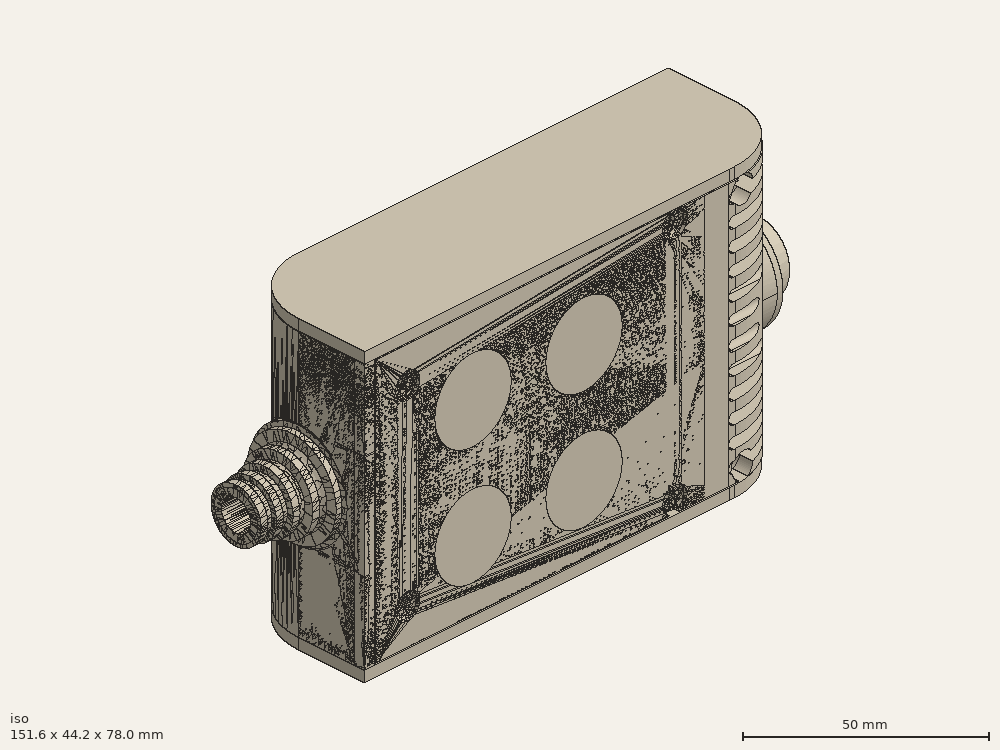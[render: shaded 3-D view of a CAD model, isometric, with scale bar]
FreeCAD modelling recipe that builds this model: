
FCSTD DOCUMENT  (FreeCAD 0.19R0.19.2)
Label: enclosure_176FCStd
License: All rights reserved
LicenseURL: http://en.wikipedia.org/wiki/All_rights_reserved
objects: Part::Revolution×152, Part::MultiFuse×146, Part::Feature×146, Sketcher::SketchObject×84, Part::Cut×70, Part::Cylinder×70, Part::Extrusion×67, Part::Fillet×58, Part::Box×36, App::MeasureDistance×4, PartDesign::Body×2, Image::ImagePlane×1
note: 831 computed .brp shape members not serialized (recipe doc carries the construction recipe); baked Part::Feature solids carry a one-line shape summary decoded from their .brp

FEATURE [Sketcher::SketchObject] Sketch  label="topSketch"
  FullyConstrained = true
  sketch-geometry (20):
    g0: LineSegment StartX=5.21097e-06 StartY=3 StartZ=0 EndX=5.21097e-06 EndY=19 EndZ=0
    g1: ArcOfCircle CenterX=19 CenterY=19 CenterZ=0 NormalX=0 NormalY=0 NormalZ=1 AngleXU=0 Radius=19 StartAngle=1.5708 EndAngle=3.14159
    g2: ArcOfCircle CenterX=19 CenterY=19 CenterZ=0 NormalX=0 NormalY=0 NormalZ=1 AngleXU=0 Radius=16 StartAngle=1.5708 EndAngle=3.14159
    g3: LineSegment StartX=114 StartY=35 StartZ=0 EndX=19 EndY=35 EndZ=0
    g4: LineSegment StartX=5.21097e-06 StartY=3 StartZ=0 EndX=5.21097e-06 EndY=0 EndZ=0
    g5: LineSegment StartX=3 StartY=0 StartZ=0 EndX=5.21097e-06 EndY=0 EndZ=0
    g6: LineSegment StartX=3 StartY=19 StartZ=0 EndX=3 EndY=0 EndZ=0
    g7: LineSegment StartX=19 StartY=38 StartZ=0 EndX=124 EndY=38 EndZ=0
    g8: Circle CenterX=119 CenterY=35 CenterZ=0 NormalX=0 NormalY=0 NormalZ=1 AngleXU=0 Radius=1
    g9: Circle CenterX=121 CenterY=35 CenterZ=0 NormalX=0 NormalY=0 NormalZ=1 AngleXU=0 Radius=1
    g10: Circle CenterX=121 CenterY=33 CenterZ=0 NormalX=0 NormalY=0 NormalZ=1 AngleXU=0 Radius=1
    g11: BSplineCurve PolesCount=3 KnotsCount=2 Degree=2 IsPeriodic=0
    g12: GeomPoint X=119 Y=35 Z=0
    g13: GeomPoint X=121 Y=33 Z=0
    g14: LineSegment StartX=119 StartY=35 StartZ=0 EndX=114 EndY=35 EndZ=0
    g15: ArcOfCircle CenterX=105 CenterY=19 CenterZ=0 NormalX=0 NormalY=0 NormalZ=1 AngleXU=0 Radius=19 StartAngle=5.7297 EndAngle=6.28319
    g16: ArcOfCircle CenterX=105 CenterY=19 CenterZ=0 NormalX=0 NormalY=0 NormalZ=1 AngleXU=0 Radius=16 StartAngle=5.60905 EndAngle=6.28319
    g17: LineSegment StartX=121 StartY=33 StartZ=0 EndX=121 EndY=19 EndZ=0
    g18: LineSegment StartX=124 StartY=38 StartZ=0 EndX=124 EndY=19 EndZ=0
    g19: LineSegment StartX=117.5 StartY=9.01251 StartZ=0 EndX=121.163 EndY=9.0125 EndZ=0
  constraints (46):
    c: Vertical(g0)
    c: Block(g0)
    c: Coincident(g1,g0)
    c: Block(g1)
    c: Coincident(g2,g1)
    c: Block(g2)
    c: Coincident(g3,g2)
    c: Horizontal(g3)
    c: Tangent(g3,g2)
    c: Coincident(g4,g0)
    c: Distance(g4) = 3
    c: Vertical(g4)
    c: Coincident(g5,g4)
    c: Horizontal(g5)
    c: Coincident(g6,g2)
    c: Coincident(g6,g5)
    c: Vertical(g6)
    c: Horizontal(g7)
    c: Distance(g7) = 105
    c: Coincident(g7,g1)
    c: Block(g3)
    c: Weight(g8) = 1
    c: Equal(g8,g9)
    c: Equal(g8,g10)
    c: InternalAlignment(g8,g11)
    c: InternalAlignment(g9,g11)
    c: InternalAlignment(g10,g11)
    c: InternalAlignment(g12,g11)
    c: InternalAlignment(g13,g11)
    c: Block(g11)
    c: Coincident(g14,g11)
    c: Coincident(g14,g3)
    c: Horizontal(g14)
    c: Block(g15)
    c: Coincident(g16,g15)
    c: Block(g16)
    c: Coincident(g17,g11)
    c: Coincident(g17,g16)
    c: Vertical(g17)
    c: Distance(g17) = 14
    c: Coincident(g18,g7)
    c: Coincident(g18,g15)
    c: Vertical(g18)
    c: Distance(g18) = 19
    c: Coincident(g19,g16)
    c: Coincident(g19,g15)
FEATURE [Sketcher::SketchObject] Sketch001  label="bottomSketch"
  FullyConstrained = true
  sketch-geometry (32):
    g0: LineSegment StartX=3.3 StartY=-6.03275e-07 StartZ=0 EndX=98 EndY=-6.03275e-07 EndZ=0
    g1: ArcOfCircle CenterX=98 CenterY=19 CenterZ=0 NormalX=0 NormalY=0 NormalZ=1 AngleXU=0 Radius=19 StartAngle=4.71239 EndAngle=5.71103
    g2: LineSegment StartX=6.3 StartY=8 StartZ=0 EndX=3.3 EndY=8 EndZ=0
    g3: LineSegment StartX=3.3 StartY=8 StartZ=0 EndX=3.3 EndY=-6.03275e-07 EndZ=0
    g4: ArcOfCircle CenterX=8.3 CenterY=5 CenterZ=0 NormalX=0 NormalY=0 NormalZ=1 AngleXU=0 Radius=2 StartAngle=3.14159 EndAngle=4.71239
    g5: LineSegment StartX=6.3 StartY=8 StartZ=0 EndX=6.3 EndY=5 EndZ=0
    g6: ArcOfCircle CenterX=98 CenterY=19 CenterZ=0 NormalX=0 NormalY=0 NormalZ=1 AngleXU=0 Radius=12.7 StartAngle=4.71239 EndAngle=6.28319
    g7: LineSegment StartX=94.7 StartY=3 StartZ=0 EndX=8.3 EndY=3 EndZ=0
    g8-g12: Circle x5 (B-spline internal-alignment scaffolding for g13; pole/knot coordinates omitted)
    g13: BSplineCurve PolesCount=5 KnotsCount=3 Degree=3 IsPeriodic=0
    g14: GeomPoint X=98 Y=6.3 Z=0
    g15: GeomPoint X=96.3938 Y=4.71946 Z=0
    g16: GeomPoint X=94.7 Y=3 Z=0
    g17-g23: Circle x7 (B-spline internal-alignment scaffolding for g24; pole/knot coordinates omitted)
    g24: BSplineCurve PolesCount=7 KnotsCount=5 Degree=3 IsPeriodic=0
    g25-g29: GeomPoint x5 (B-spline internal-alignment scaffolding for g24; pole/knot coordinates omitted)
    g30: ArcOfCircle CenterX=98 CenterY=19 CenterZ=0 NormalX=0 NormalY=0 NormalZ=1 AngleXU=0 Radius=15.7 StartAngle=5.81226 EndAngle=6.28319
    g31: LineSegment StartX=110.7 StartY=19 StartZ=0 EndX=113.7 EndY=19 EndZ=0
  constraints (41):
    c: Horizontal(g0)
    c: Coincident(g1,g0)
    c: Block(g1)
    c: Horizontal(g2)
    c: Distance(g2) = 3
    c: Coincident(g3,g2)
    c: Vertical(g3)
    c: Coincident(g3,g0)
    c: Block(g4)
    c: Block(g2)
    c: Coincident(g5,g2)
    c: Coincident(g5,g4)
    c: Vertical(g5)
    c: Coincident(g6,g1)
    c: Block(g6)
    c: Coincident(g7,g4)
    c: Horizontal(g7)
    c: Block(g0)
    c: Block(g7)
    c: Block(g3)
    c: Coincident(g13,g6)
    c: Weight(g8) = 1
    c: Equal(g8, g9-g12) x4
    c: Coincident(g13,g7)
    c: InternalAlignment(g8-g12 -> g13) x5
    c: InternalAlignment(g14,g13)
    c: InternalAlignment(g15,g13)
    c: InternalAlignment(g16,g13)
    c: Block(g13)
    c: Weight(g17) = 1
    c: Equal(g17, g18-g23) x6
    c: Coincident(g24,g1)
    c: InternalAlignment(g17-g23 -> g24) x7
    c: InternalAlignment(g25-g29 -> g24) x5
    c: Block(g24)
    c: Coincident(g30,g24)
    c: Coincident(g31,g6)
    c: Coincident(g31,g30)
    c: Horizontal(g31)
    c: Block(g31)
    c: Block(g30)
FEATURE [Part::Extrusion] Extrude  label="top"
  Base = -> Sketch
  Dir = (0,0,1)
  DirMode = 2
  FaceMakerClass = Part::FaceMakerBullseye
  LengthFwd = 72
  LengthRev = 0
  Solid = true
  Symmetric = false
FEATURE [Part::Extrusion] Extrude001  label="bottom"
  Base = -> Sketch001
  Dir = (0,0,1)
  DirMode = 2
  FaceMakerClass = Part::FaceMakerBullseye
  LengthFwd = 71.4
  LengthRev = 0
  Placement = pos=(0,0,0.3) rot=(0,0,1;0rad)
  Solid = true
  Symmetric = false
FEATURE [Sketcher::SketchObject] Sketch002  label="topSketch001"
  FullyConstrained = true
  sketch-geometry (8):
    g0: ArcOfCircle CenterX=19 CenterY=19.0975 CenterZ=0 NormalX=0 NormalY=0 NormalZ=1 AngleXU=0 Radius=18.9025 StartAngle=1.5708 EndAngle=3.14674
    g1: LineSegment StartX=0.0977805 StartY=19.0003 StartZ=0 EndX=0.0977805 EndY=0.000251602 EndZ=0
    g2: LineSegment StartX=19 StartY=38 StartZ=0 EndX=124 EndY=38 EndZ=0
    g3: LineSegment StartX=0.0977805 StartY=0.000251602 StartZ=0 EndX=105.098 EndY=0.000251602 EndZ=0
    g4: LineSegment StartX=124 StartY=38 StartZ=0 EndX=125.616 EndY=38 EndZ=0
    g5: LineSegment StartX=105.098 StartY=0.000251602 StartZ=0 EndX=106.713 EndY=0.000251602 EndZ=0
    g6: ArcOfCircle CenterX=106.616 CenterY=19 CenterZ=0 NormalX=0 NormalY=0 NormalZ=1 AngleXU=0 Radius=19 StartAngle=4.71754 EndAngle=6.28319
    g7: LineSegment StartX=125.616 StartY=38 StartZ=0 EndX=125.616 EndY=19 EndZ=0
  constraints (21):
    c: Block(g0)
    c: Coincident(g1,g0)
    c: Vertical(g1)
    c: Horizontal(g2)
    c: Distance(g2) = 105
    c: Coincident(g2,g0)
    c: Distance(g1) = 19
    c: Coincident(g3,g1)
    c: Horizontal(g3)
    c: Distance(g3) = 105
    c: Coincident(g4,g2)
    c: Horizontal(g4)
    c: Distance(g4) = 1.61553
    c: Horizontal(g5)
    c: Equal(g4,g5) = 1.61553
    c: Coincident(g5,g3)
    c: Block(g6)
    c: Coincident(g6,g5)
    c: Coincident(g7,g4)
    c: Coincident(g7,g6)
    c: Vertical(g7)
FEATURE [Part::Extrusion] Extrude002  label="sideA"
  Base = -> Sketch002
  Dir = (0,0,1)
  DirMode = 2
  FaceMakerClass = Part::FaceMakerBullseye
  LengthFwd = 3
  LengthRev = 0
  Placement = pos=(0,0,-3) rot=(0,0,1;0rad)
  Solid = true
  Symmetric = false
FEATURE [Sketcher::SketchObject] Sketch003  label="topSketch002"
  FullyConstrained = true
  sketch-geometry (6):
    g0: LineSegment StartX=19 StartY=38 StartZ=0 EndX=117 EndY=38 EndZ=0
    g1: ArcOfCircle CenterX=19 CenterY=19 CenterZ=0 NormalX=0 NormalY=0 NormalZ=1 AngleXU=0 Radius=19 StartAngle=1.5708 EndAngle=3.14159
    g2: LineSegment StartX=117 StartY=38 StartZ=0 EndX=117 EndY=19 EndZ=0
    g3: LineSegment StartX=98 StartY=1.0161e-12 StartZ=0 EndX=5.22862e-06 EndY=1.0161e-12 EndZ=0
    g4: LineSegment StartX=5.22862e-06 StartY=19 StartZ=0 EndX=5.22862e-06 EndY=1.0161e-12 EndZ=0
    g5: ArcOfCircle CenterX=98 CenterY=19 CenterZ=0 NormalX=0 NormalY=0 NormalZ=1 AngleXU=0 Radius=19 StartAngle=4.71239 EndAngle=6.28319
  constraints (16):
    c: Horizontal(g0)
    c: Distance(g0) = 98
    c: Coincident(g1,g0)
    c: Block(g1)
    c: Coincident(g2,g0)
    c: Vertical(g2)
    c: Distance(g2) = 19
    c: Horizontal(g3)
    c: Coincident(g4,g1)
    c: Vertical(g4)
    c: Coincident(g3,g4)
    c: Block(g3)
    c: Coincident(g5,g2)
    c: Coincident(g5,g3)
    c: Block(g0)
    c: Block(g5)
FEATURE [Sketcher::SketchObject] Sketch004
  FullyConstrained = true
  MapMode = 3
  Placement = pos=(0,0,0) rot=(1,0,0;1.5708rad)
  Support = -> [Extrude]
  sketch-geometry (8):
    g0: Circle CenterX=80.351 CenterY=-67.6202 CenterZ=0 NormalX=0 NormalY=0 NormalZ=1 AngleXU=0 Radius=2
    g1: Circle CenterX=80.351 CenterY=-67.6202 CenterZ=0 NormalX=0 NormalY=0 NormalZ=1 AngleXU=0 Radius=3
    g2: Circle CenterX=80.351 CenterY=-4.92017 CenterZ=0 NormalX=0 NormalY=0 NormalZ=1 AngleXU=0 Radius=2
    g3: Circle CenterX=80.351 CenterY=-4.92017 CenterZ=0 NormalX=0 NormalY=0 NormalZ=1 AngleXU=0 Radius=3
    g4: Circle CenterX=23.851 CenterY=-4.92017 CenterZ=0 NormalX=0 NormalY=0 NormalZ=1 AngleXU=0 Radius=2
    g5: Circle CenterX=23.851 CenterY=-4.92017 CenterZ=0 NormalX=0 NormalY=0 NormalZ=1 AngleXU=0 Radius=3
    g6: Circle CenterX=23.851 CenterY=-67.6202 CenterZ=0 NormalX=0 NormalY=0 NormalZ=1 AngleXU=0 Radius=2
    g7: Circle CenterX=23.851 CenterY=-67.6202 CenterZ=0 NormalX=0 NormalY=0 NormalZ=1 AngleXU=0 Radius=3
  constraints (8):
    c: Block(g3)
    c: Block(g2)
    c: Block(g1)
    c: Block(g0)
    c: Block(g6)
    c: Block(g7)
    c: Block(g4)
    c: Block(g5)
FEATURE [Part::Extrusion] Extrude004
  Base = -> Sketch004
  Dir = (0,-1,2e-16)
  DirMode = 2
  FaceMakerClass = Part::FaceMakerBullseye
  LengthFwd = 6
  LengthRev = 0
  Placement = pos=(0,9,0) rot=(0,0,1;0rad)
  Solid = true
  Symmetric = false
FEATURE [Sketcher::SketchObject] Sketch005
  FullyConstrained = true
  MapMode = 3
  Placement = pos=(0,0,0) rot=(1,0,0;1.5708rad)
  Support = -> [Extrude]
  sketch-geometry (8):
    g0: Circle CenterX=80.351 CenterY=-67.6202 CenterZ=0 NormalX=0 NormalY=0 NormalZ=1 AngleXU=0 Radius=3
    g1: Circle CenterX=80.351 CenterY=-4.92017 CenterZ=0 NormalX=0 NormalY=0 NormalZ=1 AngleXU=0 Radius=3
    g2: Circle CenterX=23.851 CenterY=-4.92017 CenterZ=0 NormalX=0 NormalY=0 NormalZ=1 AngleXU=0 Radius=3
    g3: Circle CenterX=23.851 CenterY=-67.6202 CenterZ=0 NormalX=0 NormalY=0 NormalZ=1 AngleXU=0 Radius=3
    g4: Circle CenterX=23.851 CenterY=-67.6202 CenterZ=0 NormalX=0 NormalY=0 NormalZ=1 AngleXU=0 Radius=5
    g5: Circle CenterX=80.351 CenterY=-67.6202 CenterZ=0 NormalX=0 NormalY=0 NormalZ=1 AngleXU=0 Radius=5
    g6: Circle CenterX=23.851 CenterY=-4.92017 CenterZ=0 NormalX=0 NormalY=0 NormalZ=1 AngleXU=0 Radius=5
    g7: Circle CenterX=80.351 CenterY=-4.92017 CenterZ=0 NormalX=0 NormalY=0 NormalZ=1 AngleXU=0 Radius=5
  constraints (8):
    c: Block(g1)
    c: Block(g0)
    c: Block(g3)
    c: Block(g2)
    c: Block(g5)
    c: Block(g4)
    c: Block(g6)
    c: Block(g7)
FEATURE [Part::Extrusion] Extrude005
  Base = -> Sketch005
  Dir = (0,-1,2e-16)
  DirMode = 2
  FaceMakerClass = Part::FaceMakerBullseye
  LengthFwd = 2
  LengthRev = 0
  Solid = true
  Symmetric = false
FEATURE [Sketcher::SketchObject] Sketch006
  FullyConstrained = true
  MapMode = 3
  Placement = pos=(0,0,0) rot=(1,0,0;1.5708rad)
  sketch-geometry (8):
    g0: Circle CenterX=80.351 CenterY=-67.6202 CenterZ=0 NormalX=0 NormalY=0 NormalZ=1 AngleXU=0 Radius=3
    g1: Circle CenterX=80.351 CenterY=-4.92017 CenterZ=0 NormalX=0 NormalY=0 NormalZ=1 AngleXU=0 Radius=3
    g2: Circle CenterX=23.851 CenterY=-4.92017 CenterZ=0 NormalX=0 NormalY=0 NormalZ=1 AngleXU=0 Radius=3
    g3: Circle CenterX=23.851 CenterY=-67.6202 CenterZ=0 NormalX=0 NormalY=0 NormalZ=1 AngleXU=0 Radius=3
    g4: Circle CenterX=23.851 CenterY=-67.6202 CenterZ=0 NormalX=0 NormalY=0 NormalZ=1 AngleXU=0 Radius=5
    g5: Circle CenterX=80.351 CenterY=-67.6202 CenterZ=0 NormalX=0 NormalY=0 NormalZ=1 AngleXU=0 Radius=5
    g6: Circle CenterX=23.851 CenterY=-4.92017 CenterZ=0 NormalX=0 NormalY=0 NormalZ=1 AngleXU=0 Radius=5
    g7: Circle CenterX=80.351 CenterY=-4.92017 CenterZ=0 NormalX=0 NormalY=0 NormalZ=1 AngleXU=0 Radius=5
  constraints (8):
    c: Block(g1)
    c: Block(g0)
    c: Block(g3)
    c: Block(g2)
    c: Block(g5)
    c: Block(g4)
    c: Block(g6)
    c: Block(g7)
FEATURE [Part::Extrusion] Extrude007
  Base = -> Sketch006
  Dir = (0,-1,2e-16)
  DirMode = 2
  FaceMakerClass = Part::FaceMakerBullseye
  LengthFwd = 2
  LengthRev = 0
  Solid = true
  Symmetric = false
FEATURE [Part::Fillet] Fillet
  Base = -> Extrude007
  Edges = 4 edges r=1.99: [Edge6,Edge12,Edge18,Edge24]
FEATURE [Part::Cut] Cut
  Base = -> Extrude005
  Placement = pos=(0,5,0) rot=(0,0,1;0rad)
  Tool = -> Fillet
FEATURE [Part::MultiFuse] Fusion  label="pCBScrews"
  Placement = pos=(-2.5,0,72.3) rot=(0,0,1;0rad)
  Shapes = -> [Extrude004,Cut]
FEATURE [App::MeasureDistance] Distance  label="Distance: 0.69 mm"
  Distance = 0.685967
  P1 = (24.0138,2.9647,0.3)
  P2 = (23.8901,3,-0.373787)
FEATURE [App::MeasureDistance] Distance001  label="Distance: 0.53 mm"
  Distance = 0.533607
  P1 = (80.2939,3,72.2334)
  P2 = (80.281,2.99661,71.7)
FEATURE [Part::Fillet] Fillet001
  Base = -> Extrude001
  Edges = 1 edges r=2.4: [Edge17]
FEATURE [Part::Fillet] Fillet002  label="bottom001"
  Base = -> Fillet001
  Edges = 1 edges r=2.4: [Edge36]
FEATURE [Part::Fillet] Fillet003  label="top001"
  Base = -> Extrude
  Edges = 1 edges r=2: [Edge1]
FEATURE [Sketcher::SketchObject] Sketch007
  FullyConstrained = true
  sketch-geometry (16):
    g0: LineSegment StartX=4 StartY=0 StartZ=0 EndX=4 EndY=2.4 EndZ=0
    g1: LineSegment StartX=4 StartY=2.4 StartZ=0 EndX=7 EndY=2.4 EndZ=0
    g2: LineSegment StartX=4 StartY=0 StartZ=0 EndX=5.7 EndY=0 EndZ=0
    g3: LineSegment StartX=5.7 StartY=0 StartZ=0 EndX=5.7 EndY=-5.6 EndZ=0
    g4-g8: Circle x5 (B-spline internal-alignment scaffolding for g9; pole/knot coordinates omitted)
    g9: BSplineCurve PolesCount=5 KnotsCount=3 Degree=3 IsPeriodic=0
    g10: GeomPoint X=7 Y=2.4 Z=0
    g11: GeomPoint X=10.4582 Y=-1.55472 Z=0
    g12: GeomPoint X=14 Y=-5.6 Z=0
    g13: LineSegment StartX=14 StartY=-5.6 StartZ=0 EndX=14 EndY=-14.1 EndZ=0
    g14: LineSegment StartX=14 StartY=-14.1 StartZ=0 EndX=6.5 EndY=-14.1 EndZ=0
    g15: LineSegment StartX=5.7 StartY=-5.6 StartZ=0 EndX=6.5 EndY=-14.1 EndZ=0
  constraints (28):
    c: Distance(g0) = 2.4
    c: Vertical(g0)
    c: Block(g0)
    c: Coincident(g1,g0)
    c: Horizontal(g1)
    c: Distance(g1) = 3
    c: Coincident(g2,g0)
    c: Horizontal(g2)
    c: Distance(g2) = 1.7
    c: Coincident(g3,g2)
    c: Vertical(g3)
    c: Distance(g3) = 5.6
    c: Coincident(g9,g1)
    c: Weight(g4) = 1
    c: Equal(g4, g5-g8) x4
    c: InternalAlignment(g4-g8 -> g9) x5
    c: InternalAlignment(g10,g9)
    c: InternalAlignment(g11,g9)
    c: InternalAlignment(g12,g9)
    c: Block(g9)
    c: Coincident(g13,g9)
    c: Vertical(g13)
    c: Distance(g13) = 8.5
    c: Coincident(g14,g13)
    c: Horizontal(g14)
    c: Distance(g14) = 7.5
    c: Coincident(g15,g3)
    c: Coincident(g15,g14)
FEATURE [Part::Feature] Face
  shape: bbox 10 x 16.5 x 2e-07 mm, 1 faces, 0 solids (baked)
FEATURE [Part::Revolution] Revolve  label="plugHousing"
  Angle = 360
  Axis = (0,1,0)
  Base = (0,0,0)
  FaceMakerClass = Part::FaceMakerBullseye
  Placement = pos=(0,0,36.15) rot=(0,0,1;0rad)
  Solid = false
  Source = -> Face
  Symmetric = false
FEATURE [Part::Feature] Face001
  shape: bbox 10 x 16.5 x 2e-07 mm, 1 faces, 0 solids (baked)
FEATURE [Part::Revolution] Revolve001  label="plugHousing001"
  Angle = 360
  Axis = (0,1,0)
  Base = (0,0,0)
  FaceMakerClass = Part::FaceMakerBullseye
  Placement = pos=(0,0,36.15) rot=(0,0,1;0rad)
  Solid = false
  Source = -> Face001
  Symmetric = false
FEATURE [Part::MultiFuse] Fusion001  label="plugHousing002"
  Placement = pos=(0,0,0) rot=(0,0,1;1.5708rad)
  Shapes = -> [Revolve001,Revolve]
FEATURE [Part::Feature] Face002
  shape: bbox 10 x 16.5 x 2e-07 mm, 1 faces, 0 solids (baked)
FEATURE [Part::Revolution] Revolve003  label="plugHousing005"
  Angle = 360
  Axis = (0,1,0)
  Base = (0,0,0)
  FaceMakerClass = Part::FaceMakerBullseye
  Placement = pos=(0,0,36.15) rot=(0,0,1;0rad)
  Solid = false
  Source = -> Face002
  Symmetric = false
FEATURE [Part::Feature] Face003
  shape: bbox 10 x 16.5 x 2e-07 mm, 1 faces, 0 solids (baked)
FEATURE [Part::Revolution] Revolve002  label="plugHousing003"
  Angle = 360
  Axis = (0,1,0)
  Base = (0,0,0)
  FaceMakerClass = Part::FaceMakerBullseye
  Placement = pos=(0,0,36.15) rot=(0,0,1;0rad)
  Solid = false
  Source = -> Face003
  Symmetric = false
FEATURE [Part::MultiFuse] Fusion002  label="plugHousing004"
  Placement = pos=(0,0,0) rot=(0,0,1;1.5708rad)
  Shapes = -> [Revolve002,Revolve003]
FEATURE [Part::MultiFuse] Fusion003  label="plugHousing006"
  Placement = pos=(0,19,0) rot=(0,0,1;3.14159rad)
  Shapes = -> [Fusion002,Fusion001]
FEATURE [Part::Feature] Face004
  shape: bbox 10 x 16.5 x 2e-07 mm, 1 faces, 0 solids (baked)
FEATURE [Part::Revolution] Revolve006  label="plugHousing010"
  Angle = 360
  Axis = (0,1,0)
  Base = (0,0,0)
  FaceMakerClass = Part::FaceMakerBullseye
  Placement = pos=(0,0,36.15) rot=(0,0,1;0rad)
  Solid = false
  Source = -> Face004
  Symmetric = false
FEATURE [Part::Feature] Face005
  shape: bbox 10 x 16.5 x 2e-07 mm, 1 faces, 0 solids (baked)
FEATURE [Part::Revolution] Revolve007  label="plugHousing011"
  Angle = 360
  Axis = (0,1,0)
  Base = (0,0,0)
  FaceMakerClass = Part::FaceMakerBullseye
  Placement = pos=(0,0,36.15) rot=(0,0,1;0rad)
  Solid = false
  Source = -> Face005
  Symmetric = false
FEATURE [Part::Feature] Face006
  shape: bbox 10 x 16.5 x 2e-07 mm, 1 faces, 0 solids (baked)
FEATURE [Part::Revolution] Revolve004  label="plugHousing007"
  Angle = 360
  Axis = (0,1,0)
  Base = (0,0,0)
  FaceMakerClass = Part::FaceMakerBullseye
  Placement = pos=(0,0,36.15) rot=(0,0,1;0rad)
  Solid = false
  Source = -> Face006
  Symmetric = false
FEATURE [Part::MultiFuse] Fusion004  label="plugHousing009"
  Placement = pos=(0,0,0) rot=(0,0,1;1.5708rad)
  Shapes = -> [Revolve004,Revolve007]
FEATURE [Part::Feature] Face007
  shape: bbox 10 x 16.5 x 2e-07 mm, 1 faces, 0 solids (baked)
FEATURE [Part::Revolution] Revolve005  label="plugHousing008"
  Angle = 360
  Axis = (0,1,0)
  Base = (0,0,0)
  FaceMakerClass = Part::FaceMakerBullseye
  Placement = pos=(0,0,36.15) rot=(0,0,1;0rad)
  Solid = false
  Source = -> Face007
  Symmetric = false
FEATURE [Part::MultiFuse] Fusion005  label="plugHousing012"
  Placement = pos=(0,0,0) rot=(0,0,1;1.5708rad)
  Shapes = -> [Revolve006,Revolve005]
FEATURE [Part::MultiFuse] Fusion006  label="plugHousing013"
  Placement = pos=(0,19,0) rot=(0,0,1;3.14159rad)
  Shapes = -> [Fusion005,Fusion004]
FEATURE [Part::MultiFuse] Fusion007  label="plugHousing014"
  Placement = pos=(122.621,0,-0.15) rot=(0,0,1;0rad)
  Shapes = -> [Fusion003,Fusion006]
FEATURE [Part::Cylinder] Cylinder002
  Angle = 360
  AttacherType = Attacher::AttachEngine3D
  Height = 20
  Placement = pos=(0,0,36.15) rot=(0,0,1;0rad)
  Radius = 4
FEATURE [Part::Cylinder] Cylinder003
  Angle = 360
  AttacherType = Attacher::AttachEngine3D
  Height = 10
  Placement = pos=(0,0,36.15) rot=(0,0,1;0rad)
  Radius = 4
FEATURE [Part::MultiFuse] Fusion009  label="removeToCreateHoleForPlugHousing"
  Placement = pos=(70,19,36.15) rot=(0,1,0;1.5708rad)
  Shapes = -> [Cylinder002,Cylinder003]
FEATURE [Part::Cylinder] Cylinder004
  Angle = 360
  AttacherType = Attacher::AttachEngine3D
  Height = 20
  Placement = pos=(0,0,36.15) rot=(0,0,1;0rad)
  Radius = 4
FEATURE [Part::Cylinder] Cylinder005
  Angle = 360
  AttacherType = Attacher::AttachEngine3D
  Height = 10
  Placement = pos=(0,0,36.15) rot=(0,0,1;0rad)
  Radius = 4
FEATURE [Part::MultiFuse] Fusion010  label="removeToCreateHoleForPlugHousing001"
  Placement = pos=(70,19,36.15) rot=(0,1,0;1.5708rad)
  Shapes = -> [Cylinder004,Cylinder005]
FEATURE [Part::Cut] Cut001
  Base = -> Fillet003
  Tool = -> Fusion010
FEATURE [Part::Cut] Cut002  label="Bottom"
  Base = -> Fillet002
  Tool = -> Fusion009
FEATURE [Part::Feature] Face008
  shape: bbox 10 x 16.5 x 2e-07 mm, 1 faces, 0 solids (baked)
FEATURE [Part::Revolution] Revolve011  label="plugHousing021"
  Angle = 360
  Axis = (0,1,0)
  Base = (0,0,0)
  FaceMakerClass = Part::FaceMakerBullseye
  Placement = pos=(0,0,36.15) rot=(0,0,1;0rad)
  Solid = false
  Source = -> Face008
  Symmetric = false
FEATURE [Part::Feature] Face009
  shape: bbox 10 x 16.5 x 2e-07 mm, 1 faces, 0 solids (baked)
FEATURE [Part::Revolution] Revolve012  label="plugHousing022"
  Angle = 360
  Axis = (0,1,0)
  Base = (0,0,0)
  FaceMakerClass = Part::FaceMakerBullseye
  Placement = pos=(0,0,36.15) rot=(0,0,1;0rad)
  Solid = false
  Source = -> Face009
  Symmetric = false
FEATURE [Part::Feature] Face010 .. Face013  x4 (patterned run collapsed; names and placements below)
  shape: bbox 10 x 16.5 x 2e-07 mm, 1 faces, 0 solids (baked)
FEATURE [Part::Revolution] Revolve015  label="plugHousing027"
  Angle = 360
  Axis = (0,1,0)
  Base = (0,0,0)
  FaceMakerClass = Part::FaceMakerBullseye
  Placement = pos=(0,0,36.15) rot=(0,0,1;0rad)
  Solid = false
  Source = -> Face013
  Symmetric = false
FEATURE [Part::Feature] Face014
  shape: bbox 10 x 16.5 x 2e-07 mm, 1 faces, 0 solids (baked)
FEATURE [Part::Feature] Face015
  shape: bbox 10 x 16.5 x 2e-07 mm, 1 faces, 0 solids (baked)
FEATURE [Part::Feature] Face016
  shape: bbox 10 x 16.5 x 2e-07 mm, 1 faces, 0 solids (baked)
FEATURE [Part::Revolution] Revolve019  label="plugHousing033"
  Angle = 360
  Axis = (0,1,0)
  Base = (0,0,0)
  FaceMakerClass = Part::FaceMakerBullseye
  Placement = pos=(0,0,36.15) rot=(0,0,1;0rad)
  Solid = false
  Source = -> Face016
  Symmetric = false
FEATURE [Part::Feature] Face017
  shape: bbox 10 x 16.5 x 2e-07 mm, 1 faces, 0 solids (baked)
FEATURE [Part::Revolution] Revolve020  label="plugHousing034"
  Angle = 360
  Axis = (0,1,0)
  Base = (0,0,0)
  FaceMakerClass = Part::FaceMakerBullseye
  Placement = pos=(0,0,36.15) rot=(0,0,1;0rad)
  Solid = false
  Source = -> Face017
  Symmetric = false
FEATURE [Part::Feature] Face018
  shape: bbox 10 x 16.5 x 2e-07 mm, 1 faces, 0 solids (baked)
FEATURE [Part::Revolution] Revolve016  label="plugHousing030"
  Angle = 360
  Axis = (0,1,0)
  Base = (0,0,0)
  FaceMakerClass = Part::FaceMakerBullseye
  Placement = pos=(0,0,36.15) rot=(0,0,1;0rad)
  Solid = false
  Source = -> Face018
  Symmetric = false
FEATURE [Part::MultiFuse] Fusion020  label="plugHousing038"
  Placement = pos=(0,0,0) rot=(0,0,1;1.5708rad)
  Shapes = -> [Revolve016,Revolve020]
FEATURE [Part::Feature] Face019
  shape: bbox 10 x 16.5 x 2e-07 mm, 1 faces, 0 solids (baked)
FEATURE [Part::Feature] Face020
  shape: bbox 10 x 16.5 x 2e-07 mm, 1 faces, 0 solids (baked)
FEATURE [Part::Revolution] Revolve017  label="plugHousing031"
  Angle = 360
  Axis = (0,1,0)
  Base = (0,0,0)
  FaceMakerClass = Part::FaceMakerBullseye
  Placement = pos=(0,0,36.15) rot=(0,0,1;0rad)
  Solid = false
  Source = -> Face020
  Symmetric = false
FEATURE [Part::MultiFuse] Fusion021  label="plugHousing039"
  Placement = pos=(0,0,0) rot=(0,0,1;1.5708rad)
  Shapes = -> [Revolve019,Revolve017]
FEATURE [Part::MultiFuse] Fusion023  label="plugHousing041"
  Placement = pos=(0,19,0) rot=(0,0,1;3.14159rad)
  Shapes = -> [Fusion021,Fusion020]
FEATURE [Part::Revolution] Revolve022  label="plugHousing043"
  Angle = 360
  Axis = (0,1,0)
  Base = (0,0,0)
  FaceMakerClass = Part::FaceMakerBullseye
  Placement = pos=(0,0,36.15) rot=(0,0,1;0rad)
  Solid = false
  Source = -> Face019
  Symmetric = false
FEATURE [Part::Feature] Face021
  shape: bbox 10 x 16.5 x 2e-07 mm, 1 faces, 0 solids (baked)
FEATURE [Part::Revolution] Revolve023  label="plugHousing044"
  Angle = 360
  Axis = (0,1,0)
  Base = (0,0,0)
  FaceMakerClass = Part::FaceMakerBullseye
  Placement = pos=(0,0,36.15) rot=(0,0,1;0rad)
  Solid = false
  Source = -> Face021
  Symmetric = false
FEATURE [Part::Feature] Face022
  shape: bbox 10 x 16.5 x 2e-07 mm, 1 faces, 0 solids (baked)
FEATURE [Part::Revolution] Revolve018  label="plugHousing032"
  Angle = 360
  Axis = (0,1,0)
  Base = (0,0,0)
  FaceMakerClass = Part::FaceMakerBullseye
  Placement = pos=(0,0,36.15) rot=(0,0,1;0rad)
  Solid = false
  Source = -> Face022
  Symmetric = false
FEATURE [Part::MultiFuse] Fusion022  label="plugHousing040"
  Placement = pos=(0,0,0) rot=(0,0,1;1.5708rad)
  Shapes = -> [Revolve018,Revolve023]
FEATURE [Part::Feature] Face023
  shape: bbox 10 x 16.5 x 2e-07 mm, 1 faces, 0 solids (baked)
FEATURE [Part::Revolution] Revolve021  label="plugHousing035"
  Angle = 360
  Axis = (0,1,0)
  Base = (0,0,0)
  FaceMakerClass = Part::FaceMakerBullseye
  Placement = pos=(0,0,36.15) rot=(0,0,1;0rad)
  Solid = false
  Source = -> Face023
  Symmetric = false
FEATURE [Part::MultiFuse] Fusion018  label="plugHousing036"
  Placement = pos=(0,0,0) rot=(0,0,1;1.5708rad)
  Shapes = -> [Revolve022,Revolve021]
FEATURE [Part::MultiFuse] Fusion019  label="plugHousing037"
  Placement = pos=(0,19,0) rot=(0,0,1;3.14159rad)
  Shapes = -> [Fusion018,Fusion022]
FEATURE [Part::MultiFuse] Fusion024  label="plugHousing042"
  Placement = pos=(122.621,0,-0.15) rot=(0,0,1;0rad)
  Shapes = -> [Fusion023,Fusion019]
FEATURE [Part::Cylinder] Cylinder006
  Angle = 360
  AttacherType = Attacher::AttachEngine3D
  Height = 20
  Placement = pos=(0,0,36.15) rot=(0,0,1;0rad)
  Radius = 14.3
FEATURE [Part::Cylinder] Cylinder007
  Angle = 360
  AttacherType = Attacher::AttachEngine3D
  Height = 10
  Placement = pos=(0,0,36.15) rot=(0,0,1;0rad)
  Radius = 4
FEATURE [Part::MultiFuse] Fusion026  label="removeToCreteHoleForPlugHousing"
  Placement = pos=(70,19,36) rot=(0,1,0;1.5708rad)
  Shapes = -> [Cylinder006,Cylinder007]
FEATURE [Part::Box] Box001  label="Cube001"
  AttacherType = Attacher::AttachEngine3D
  Height = 28
  Length = 3
  Placement = pos=(110.7,19,22) rot=(0,0,1;0rad)
  Width = 15.7
FEATURE [Part::Cut] Cut003  label="top002"
  Base = -> Cut001
  Tool = -> Fusion007
FEATURE [Part::Revolution] Revolve008  label="plugHousing015"
  Angle = 360
  Axis = (0,1,0)
  Base = (0,0,0)
  FaceMakerClass = Part::FaceMakerBullseye
  Placement = pos=(0,0,36.15) rot=(0,0,1;0rad)
  Solid = false
  Source = -> Face010
  Symmetric = false
FEATURE [Part::MultiFuse] Fusion013  label="plugHousing020"
  Placement = pos=(0,0,0) rot=(0,0,1;1.5708rad)
  Shapes = -> [Revolve008,Revolve012]
FEATURE [Part::Cut] Cut004  label="top003"
  Base = -> Cut003
  Placement = pos=(1,0,0) rot=(0,0,1;0rad)
  Tool = -> Fusion026
FEATURE [Part::Cylinder] Cylinder008
  Angle = 360
  AttacherType = Attacher::AttachEngine3D
  Height = 20
  Placement = pos=(0,0,36.15) rot=(0,0,1;0rad)
  Radius = 10.3
FEATURE [Part::Cylinder] Cylinder009
  Angle = 360
  AttacherType = Attacher::AttachEngine3D
  Height = 10
  Placement = pos=(0,0,36.15) rot=(0,0,1;0rad)
  Radius = 4
FEATURE [Part::MultiFuse] Fusion027  label="removeToCreteHoleForPlugHousing001"
  Placement = pos=(70,19,36) rot=(0,1,0;1.5708rad)
  Shapes = -> [Cylinder008,Cylinder009]
FEATURE [Part::Cut] Cut005  label="plugHousingTab"
  Base = -> Box001
  Tool = -> Fusion027
FEATURE [Part::MultiFuse] Fusion028  label="plugHousing045"
  Shapes = -> [Fusion024,Cut005]
FEATURE [Part::Box] Box002  label="Cube002"
  AttacherType = Attacher::AttachEngine3D
  Height = 28.8
  Length = 3
  Placement = pos=(107.3,28,21.6) rot=(0,0,1;0rad)
  Width = 7
FEATURE [Part::Box] Box003  label="Cube003"
  AttacherType = Attacher::AttachEngine3D
  Height = 3
  Length = 6.4
  Placement = pos=(107.3,28,18.6) rot=(0,0,1;0rad)
  Width = 7
FEATURE [Part::Box] Box004  label="Cube004"
  AttacherType = Attacher::AttachEngine3D
  Height = 3
  Length = 6.4
  Placement = pos=(107.3,28,50.4) rot=(0,0,1;0rad)
  Width = 7
FEATURE [Part::MultiFuse] Fusion029  label="plugHousingBracketHolder"
  Shapes = -> [Box004,Box002,Box003]
FEATURE [Part::Cylinder] Cylinder010
  Angle = 360
  AttacherType = Attacher::AttachEngine3D
  Height = 20
  Placement = pos=(0,0,36.15) rot=(0,0,1;0rad)
  Radius = 14.3
FEATURE [Part::Cylinder] Cylinder011
  Angle = 360
  AttacherType = Attacher::AttachEngine3D
  Height = 10
  Placement = pos=(0,0,36.15) rot=(0,0,1;0rad)
  Radius = 4
FEATURE [Part::MultiFuse] Fusion030  label="removeToCreteHoleForPlugHousing002"
  Placement = pos=(70,19,36) rot=(0,1,0;1.5708rad)
  Shapes = -> [Cylinder010,Cylinder011]
FEATURE [Part::Cut] Cut006  label="plugHousingBracketHolder001"
  Base = -> Fusion029
  Tool = -> Fusion030
FEATURE [Part::Cylinder] Cylinder012
  Angle = 360
  AttacherType = Attacher::AttachEngine3D
  Height = 20
  Placement = pos=(0,0,36.15) rot=(0,0,1;0rad)
  Radius = 7
FEATURE [Part::Cylinder] Cylinder013
  Angle = 360
  AttacherType = Attacher::AttachEngine3D
  Height = 10
  Placement = pos=(0,0,36.15) rot=(0,0,1;0rad)
  Radius = 4
FEATURE [Part::MultiFuse] Fusion032  label="removeToCreteHoleForPlugHousing003"
  Placement = pos=(70,19,36) rot=(0,1,0;1.5708rad)
  Shapes = -> [Cylinder012,Cylinder013]
FEATURE [Part::Cut] Cut007  label="bottom002"
  Base = -> Cut002
  Tool = -> Fusion032
FEATURE [Sketcher::SketchObject] Sketch008
  FullyConstrained = true
  sketch-geometry (54):
    g0: LineSegment StartX=-4.2 StartY=0 StartZ=0 EndX=-6.2 EndY=0 EndZ=0
    g1: LineSegment StartX=-14 StartY=-18 StartZ=0 EndX=-14 EndY=-26.5 EndZ=0
    g2: LineSegment StartX=-4.2 StartY=0 StartZ=0 EndX=-4.2 EndY=-13.4877 EndZ=0
    g3: Circle CenterX=-4.2 CenterY=-13.4877 CenterZ=0 NormalX=0 NormalY=0 NormalZ=1 AngleXU=0 Radius=1
    g4: Circle CenterX=-4.2 CenterY=-26.5 CenterZ=0 NormalX=0 NormalY=0 NormalZ=1 AngleXU=0 Radius=1
    g5: Circle CenterX=-8.2 CenterY=-26.5 CenterZ=0 NormalX=0 NormalY=0 NormalZ=1 AngleXU=0 Radius=1
    g6: BSplineCurve PolesCount=3 KnotsCount=2 Degree=2 IsPeriodic=0
    g7: GeomPoint X=-4.2 Y=-13.4877 Z=0
    g8: GeomPoint X=-8.2 Y=-26.5 Z=0
    g9: LineSegment StartX=-14 StartY=-26.5 StartZ=0 EndX=-8.2 EndY=-26.5 EndZ=0
    g10: LineSegment StartX=-10.15 StartY=-12 StartZ=0 EndX=-10.15 EndY=-14 EndZ=0
    g11: LineSegment StartX=-12.8401 StartY=-16 StartZ=0 EndX=-10.1571 EndY=-16 EndZ=0
    g12: LineSegment StartX=-10.15 StartY=-14 StartZ=0 EndX=-8.70761 EndY=-14 EndZ=0
    g13: LineSegment StartX=-12.8401 StartY=-16 StartZ=0 EndX=-12.8401 EndY=-17.6958 EndZ=0
    g14: LineSegment StartX=-10.15 StartY=-12 StartZ=0 EndX=-7.79258 EndY=-12 EndZ=0
    g15: Circle CenterX=-6.2215 CenterY=-2 CenterZ=0 NormalX=0 NormalY=0 NormalZ=1 AngleXU=0 Radius=1
    g16: Circle CenterX=-6.22762 CenterY=-2.58724 CenterZ=0 NormalX=0 NormalY=0 NormalZ=1 AngleXU=0 Radius=1
    g17: Circle CenterX=-6.32538 CenterY=-4 CenterZ=0 NormalX=0 NormalY=0 NormalZ=1 AngleXU=0 Radius=1
    g18: BSplineCurve PolesCount=3 KnotsCount=2 Degree=2 IsPeriodic=0
    g19: GeomPoint X=-6.2215 Y=-2 Z=0
    g20: GeomPoint X=-6.32538 Y=-4 Z=0
    g21: Circle CenterX=-6.48644 CenterY=-5.99526 CenterZ=0 NormalX=0 NormalY=0 NormalZ=1 AngleXU=0 Radius=1
    g22: Circle CenterX=-6.58486 CenterY=-6.99526 CenterZ=0 NormalX=0 NormalY=0 NormalZ=1 AngleXU=0 Radius=1
    g23: Circle CenterX=-6.77343 CenterY=-8 CenterZ=0 NormalX=0 NormalY=0 NormalZ=1 AngleXU=0 Radius=1
    g24: BSplineCurve PolesCount=3 KnotsCount=2 Degree=2 IsPeriodic=0
    g25: GeomPoint X=-6.48644 Y=-5.99526 Z=0
    g26: GeomPoint X=-6.77343 Y=-8 Z=0
    g27: Circle CenterX=-7.19003 CenterY=-10 CenterZ=0 NormalX=0 NormalY=0 NormalZ=1 AngleXU=0 Radius=1
    g28: Circle CenterX=-7.44407 CenterY=-11.0915 CenterZ=0 NormalX=0 NormalY=0 NormalZ=1 AngleXU=0 Radius=1
    g29: Circle CenterX=-7.79258 CenterY=-12 CenterZ=0 NormalX=0 NormalY=0 NormalZ=1 AngleXU=0 Radius=1
    g30: BSplineCurve PolesCount=3 KnotsCount=2 Degree=2 IsPeriodic=0
    g31: GeomPoint X=-7.19003 Y=-10 Z=0
    g32: GeomPoint X=-7.79258 Y=-12 Z=0
    g33: Circle CenterX=-8.70761 CenterY=-14 CenterZ=0 NormalX=0 NormalY=0 NormalZ=1 AngleXU=0 Radius=1
    g34: Circle CenterX=-9.33087 CenterY=-15.1837 CenterZ=0 NormalX=0 NormalY=0 NormalZ=1 AngleXU=0 Radius=1
    g35: Circle CenterX=-10.1571 CenterY=-16 CenterZ=0 NormalX=0 NormalY=0 NormalZ=1 AngleXU=0 Radius=1
    g36: BSplineCurve PolesCount=3 KnotsCount=2 Degree=2 IsPeriodic=0
    g37: GeomPoint X=-8.70761 Y=-14 Z=0
    g38: GeomPoint X=-10.1571 Y=-16 Z=0
    g39: Circle CenterX=-12.8401 CenterY=-17.6958 CenterZ=0 NormalX=0 NormalY=0 NormalZ=1 AngleXU=0 Radius=1
    g40: Circle CenterX=-13.3521 CenterY=-17.9027 CenterZ=0 NormalX=0 NormalY=0 NormalZ=1 AngleXU=0 Radius=1
    g41: Circle CenterX=-14 CenterY=-18 CenterZ=0 NormalX=0 NormalY=0 NormalZ=1 AngleXU=0 Radius=1
    g42: BSplineCurve PolesCount=3 KnotsCount=2 Degree=2 IsPeriodic=0
    g43: GeomPoint X=-12.8401 Y=-17.6958 Z=0
    g44: GeomPoint X=-14 Y=-18 Z=0
    g45: LineSegment StartX=-6.2 StartY=0 StartZ=0 EndX=-7.2 EndY=0 EndZ=0
    g46: LineSegment StartX=-7.2 StartY=0 StartZ=0 EndX=-7.2 EndY=-2 EndZ=0
    g47: LineSegment StartX=-7.2 StartY=-2 StartZ=0 EndX=-6.2215 EndY=-2 EndZ=0
    g48: LineSegment StartX=-6.32538 StartY=-4 StartZ=0 EndX=-7.65538 EndY=-4 EndZ=0
    g49: LineSegment StartX=-7.65538 StartY=-4 StartZ=0 EndX=-7.65538 EndY=-5.99526 EndZ=0
    g50: LineSegment StartX=-7.65538 StartY=-5.99526 StartZ=0 EndX=-6.48644 EndY=-5.99526 EndZ=0
    g51: LineSegment StartX=-6.77343 StartY=-8 StartZ=0 EndX=-8.43343 EndY=-8 EndZ=0
    g52: LineSegment StartX=-8.43343 StartY=-8 StartZ=0 EndX=-8.43343 EndY=-10 EndZ=0
    g53: LineSegment StartX=-8.43343 StartY=-10 StartZ=0 EndX=-7.19003 EndY=-10 EndZ=0
  constraints (112):
    c: Horizontal(g0)
    c: Distance(g0) = 2
    c: Block(g0)
    c: Vertical(g1)
    c: Coincident(g2,g0)
    c: Vertical(g2)
    c: Block(g2)
    c: Coincident(g6,g2)
    c: Weight(g3) = 1
    c: Equal(g3,g4)
    c: Equal(g3,g5)
    c: InternalAlignment(g3,g6)
    c: InternalAlignment(g4,g6)
    c: InternalAlignment(g5,g6)
    c: InternalAlignment(g7,g6)
    c: InternalAlignment(g8,g6)
    c: Block(g6)
    c: Coincident(g9,g1)
    c: Coincident(g9,g6)
    c: Horizontal(g9)
    c: Vertical(g10)
    c: Block(g10)
    c: Horizontal(g11)
    c: Block(g11)
    c: Coincident(g12,g10)
    c: Horizontal(g12)
    c: Block(g12)
    c: Coincident(g13,g11)
    c: Vertical(g13)
    c: Block(g13)
    c: Coincident(g14,g10)
    c: Horizontal(g14)
    c: Block(g14)
    c: Block(g9)
    c: Block(g1)
    c: Weight(g15) = 1
    c: Equal(g15,g16)
    c: Equal(g15,g17)
    c: InternalAlignment(g15,g18)
    c: InternalAlignment(g16,g18)
    c: InternalAlignment(g17,g18)
    c: InternalAlignment(g19,g18)
    c: InternalAlignment(g20,g18)
    c: Weight(g21) = 1
    c: Equal(g21,g22)
    c: Equal(g21,g23)
    c: InternalAlignment(g21,g24)
    c: InternalAlignment(g22,g24)
    c: InternalAlignment(g23,g24)
    c: InternalAlignment(g25,g24)
    c: InternalAlignment(g26,g24)
    c: Weight(g27) = 1
    c: Equal(g27,g28)
    c: Equal(g27,g29)
    c: Coincident(g30,g14)
    c: InternalAlignment(g27,g30)
    c: InternalAlignment(g28,g30)
    c: InternalAlignment(g29,g30)
    c: InternalAlignment(g31,g30)
    c: InternalAlignment(g32,g30)
    c: Coincident(g36,g12)
    c: Weight(g33) = 1
    c: Equal(g33,g34)
    c: Equal(g33,g35)
    c: Coincident(g36,g11)
    c: InternalAlignment(g33,g36)
    c: InternalAlignment(g34,g36)
    c: InternalAlignment(g35,g36)
    c: InternalAlignment(g37,g36)
    c: InternalAlignment(g38,g36)
    c: Coincident(g42,g13)
    c: Weight(g39) = 1
    c: Equal(g39,g40)
    c: Equal(g39,g41)
    c: Coincident(g42,g1)
    c: InternalAlignment(g39,g42)
    c: InternalAlignment(g40,g42)
    c: InternalAlignment(g41,g42)
    c: InternalAlignment(g43,g42)
    c: InternalAlignment(g44,g42)
    c: Block(g18)
    c: Block(g24)
    c: Block(g30)
    c: Block(g36)
    c: Block(g42)
    c: Horizontal(g45)
    c: Coincident(g45,g0)
    c: Vertical(g46)
    c: Coincident(g46,g45)
    c: Coincident(g47,g46)
    c: Coincident(g47,g18)
    c: Horizontal(g47)
    c: Block(g46)
    c: Coincident(g48,g18)
    c: Horizontal(g48)
    c: Distance(g48) = 1.33
    c: Vertical(g49)
    c: Coincident(g49,g48)
    c: Coincident(g50,g49)
    c: Coincident(g50,g24)
    c: Horizontal(g50)
    c: Tangent(g50,g22)
    c: Horizontal(g51)
    c: Coincident(g51,g24)
    c: Block(g51)
    c: Vertical(g52)
    c: Block(g52)
    c: Coincident(g52,g51)
    c: Coincident(g53,g52)
    c: Coincident(g53,g30)
    c: Horizontal(g53)
    c: Distance(g1) = 8.5
FEATURE [Part::Feature] Face024
  shape: bbox 9.8 x 26.5 x 2e-07 mm, 1 faces, 0 solids (baked)
FEATURE [Part::Revolution] Revolve024
  Angle = 360
  Axis = (0,1,0)
  Base = (0,0,0)
  FaceMakerClass = Part::FaceMakerBullseye
  Placement = pos=(0,0,0) rot=(0,0,1;1.5708rad)
  Solid = false
  Source = -> Face024
  Symmetric = false
FEATURE [Part::Feature] Face025
  shape: bbox 9.8 x 26.5 x 2e-07 mm, 1 faces, 0 solids (baked)
FEATURE [Part::Revolution] Revolve025
  Angle = 360
  Axis = (0,1,0)
  Base = (0,0,0)
  FaceMakerClass = Part::FaceMakerBullseye
  Placement = pos=(0,0,0) rot=(0,0,1;1.5708rad)
  Solid = false
  Source = -> Face025
  Symmetric = false
FEATURE [Part::MultiFuse] Fusion033
  Placement = pos=(-18,19,36) rot=(0,0,1;0rad)
  Shapes = -> [Revolve025,Revolve024]
FEATURE [Part::Cylinder] Cylinder014
  Angle = 360
  AttacherType = Attacher::AttachEngine3D
  Height = 20
  Placement = pos=(0,0,36.15) rot=(0,0,1;0rad)
  Radius = 14.3
FEATURE [Part::Cylinder] Cylinder015
  Angle = 360
  AttacherType = Attacher::AttachEngine3D
  Height = 10
  Placement = pos=(0,0,36.15) rot=(0,0,1;0rad)
  Radius = 4
FEATURE [Part::MultiFuse] Fusion034  label="removeToCreteHoleForPlugHousing004"
  Placement = pos=(-42,19,36) rot=(0,1,0;1.5708rad)
  Shapes = -> [Cylinder014,Cylinder015]
FEATURE [Part::Cut] Cut008  label="top004"
  Base = -> Cut004
  Placement = pos=(-1,0,0) rot=(0,0,1;0rad)
  Tool = -> Fusion034
FEATURE [Part::Box] Box005  label="Cube005"
  AttacherType = Attacher::AttachEngine3D
  Height = 28
  Length = 3
  Placement = pos=(110.7,19,22) rot=(0,0,1;0rad)
  Width = 15.7
FEATURE [Part::Cylinder] Cylinder016
  Angle = 360
  AttacherType = Attacher::AttachEngine3D
  Height = 10
  Placement = pos=(0,0,36.15) rot=(0,0,1;0rad)
  Radius = 4
FEATURE [Part::Cylinder] Cylinder017
  Angle = 360
  AttacherType = Attacher::AttachEngine3D
  Height = 20
  Placement = pos=(0,0,36.15) rot=(0,0,1;0rad)
  Radius = 10.3
FEATURE [Part::MultiFuse] Fusion035  label="removeToCreteHoleForPlugHousing005"
  Placement = pos=(70,19,36) rot=(0,1,0;1.5708rad)
  Shapes = -> [Cylinder017,Cylinder016]
FEATURE [Part::Cut] Cut009  label="plugHousingTab001"
  Base = -> Box005
  Placement = pos=(-107.4,-14,0) rot=(0,0,1;0rad)
  Tool = -> Fusion035
FEATURE [Part::Box] Box006  label="Cube006"
  AttacherType = Attacher::AttachEngine3D
  Height = 28
  Length = 3
  Placement = pos=(110.7,19,22) rot=(0,0,1;0rad)
  Width = 15.7
FEATURE [Part::Cylinder] Cylinder018
  Angle = 360
  AttacherType = Attacher::AttachEngine3D
  Height = 10
  Placement = pos=(0,0,36.15) rot=(0,0,1;0rad)
  Radius = 4
FEATURE [Part::Cylinder] Cylinder019
  Angle = 360
  AttacherType = Attacher::AttachEngine3D
  Height = 20
  Placement = pos=(0,0,36.15) rot=(0,0,1;0rad)
  Radius = 10.3
FEATURE [Part::MultiFuse] Fusion036  label="removeToCreteHoleForPlugHousing006"
  Placement = pos=(70,19,36) rot=(0,1,0;1.5708rad)
  Shapes = -> [Cylinder019,Cylinder018]
FEATURE [Part::Cut] Cut010  label="plugHousingTab002"
  Base = -> Box006
  Placement = pos=(-107.4,-14,0) rot=(0,0,1;0rad)
  Tool = -> Fusion036
FEATURE [Part::MultiFuse] Fusion037
  Placement = pos=(9.6,23,0) rot=(0,0,1;3.14159rad)
  Shapes = -> [Cut009,Cut010]
FEATURE [Part::Box] Box  label="Cube"
  AttacherType = Attacher::AttachEngine3D
  Height = 10
  Length = 3
  Placement = pos=(3.3,4,12) rot=(0,0,1;0rad)
  Width = 10
FEATURE [Part::Fillet] Fillet004
  Base = -> Fusion028
  Edges = 1 edges r=2: [Edge25]
FEATURE [Part::Fillet] Fillet005  label="plugHousing046"
  Base = -> Fillet004
  Edges = 1 edges r=2: [Edge8]
FEATURE [Part::Fillet] Fillet006
  Base = -> Box
  Edges = 1 edges r=2: [Edge11]
FEATURE [Part::Box] Box007  label="Cube007"
  AttacherType = Attacher::AttachEngine3D
  Height = 10
  Length = 3
  Placement = pos=(3.3,4,50) rot=(0,0,1;0rad)
  Width = 10
FEATURE [Part::Fillet] Fillet007
  Base = -> Box007
  Edges = 1 edges r=2: [Edge12]
FEATURE [Part::Box] Box008  label="Cube008"
  AttacherType = Attacher::AttachEngine3D
  Height = 28
  Length = 4
  Placement = pos=(5,0,22) rot=(0,0,1;0rad)
  Width = 10
FEATURE [Part::Fillet] Fillet008
  Base = -> Box008
  Edges = 1 edges r=1: [Edge7]
FEATURE [Part::Fillet] Fillet009
  Base = -> Fillet008
  Edges = 1 edges r=2: [Edge5]
FEATURE [Part::Fillet] Fillet010
  Base = -> Fillet009
  Edges = 1 edges r=2: [Edge2]
FEATURE [Sketcher::SketchObject] Sketch009  label="topSketch003"
  FullyConstrained = true
  sketch-geometry (4):
    g0: LineSegment StartX=16.8446 StartY=31.512 StartZ=0 EndX=16.3251 EndY=34.4666 EndZ=0
    g1: ArcOfCircle CenterX=19 CenterY=19.2524 CenterZ=0 NormalX=0 NormalY=0 NormalZ=1 AngleXU=0 Radius=15.4476 StartAngle=1.74483 EndAngle=2.72717
    g2: ArcOfCircle CenterX=19 CenterY=19.2524 CenterZ=0 NormalX=0 NormalY=0 NormalZ=1 AngleXU=0 Radius=12.4476 StartAngle=1.74483 EndAngle=2.73189
    g3: LineSegment StartX=4.86004 StartY=25.4725 StartZ=0 EndX=7.58253 EndY=24.2107 EndZ=0
  constraints (7):
    c: Block(g0)
    c: Coincident(g1,g0)
    c: Coincident(g2,g0)
    c: Coincident(g3,g1)
    c: Coincident(g3,g2)
    c: Block(g1)
    c: Block(g2)
FEATURE [Part::Extrusion] Extrude008
  Base = -> Sketch009
  Dir = (0,0,1)
  DirMode = 2
  FaceMakerClass = Part::FaceMakerBullseye
  LengthFwd = 10
  LengthRev = 0
  Placement = pos=(0,0,31) rot=(0,0,1;0rad)
  Solid = true
  Symmetric = false
FEATURE [Part::Cylinder] Cylinder020
  Angle = 360
  AttacherType = Attacher::AttachEngine3D
  Height = 20
  Placement = pos=(0,0,36.15) rot=(0,0,1;0rad)
  Radius = 8.2
FEATURE [Part::Cylinder] Cylinder021
  Angle = 360
  AttacherType = Attacher::AttachEngine3D
  Height = 10
  Placement = pos=(0,0,36.15) rot=(0,0,1;0rad)
  Radius = 4
FEATURE [Part::MultiFuse] Fusion038  label="removeToCreteHoleForPlugHousing007"
  Placement = pos=(-42,19,36) rot=(0,1,0;1.5708rad)
  Shapes = -> [Cylinder020,Cylinder021]
FEATURE [Part::Cut] Cut011
  Base = -> Extrude008
  Tool = -> Fusion038
FEATURE [Part::Fillet] Fillet011
  Base = -> Cut011
  Edges = 1 edges r=2: [Edge1]
FEATURE [Part::Fillet] Fillet012
  Base = -> Fillet011
  Edges = 1 edges r=2.5: [Edge1]
FEATURE [Part::Fillet] Fillet013
  Base = -> Fillet012
  Edges = 1 edges r=2.5: [Edge2]
FEATURE [Part::Box] Box010  label="Cube010"
  AttacherType = Attacher::AttachEngine3D
  Height = 16
  Length = 8
  Placement = pos=(12.7,31.52,28) rot=(0,0,1;0rad)
  Width = 4
FEATURE [Sketcher::SketchObject] Sketch010  label="topSketch004"
  FullyConstrained = true
  sketch-geometry (4):
    g0: LineSegment StartX=16.8446 StartY=31.512 StartZ=0 EndX=16.3251 EndY=34.4666 EndZ=0
    g1: ArcOfCircle CenterX=19 CenterY=19.2524 CenterZ=0 NormalX=0 NormalY=0 NormalZ=1 AngleXU=0 Radius=15.4476 StartAngle=1.74483 EndAngle=2.72717
    g2: ArcOfCircle CenterX=19 CenterY=19.2524 CenterZ=0 NormalX=0 NormalY=0 NormalZ=1 AngleXU=0 Radius=12.4476 StartAngle=1.74483 EndAngle=2.73189
    g3: LineSegment StartX=4.86004 StartY=25.4725 StartZ=0 EndX=7.58253 EndY=24.2107 EndZ=0
  constraints (7):
    c: Block(g0)
    c: Coincident(g1,g0)
    c: Coincident(g2,g0)
    c: Coincident(g3,g1)
    c: Coincident(g3,g2)
    c: Block(g1)
    c: Block(g2)
FEATURE [Part::Cylinder] Cylinder022
  Angle = 360
  AttacherType = Attacher::AttachEngine3D
  Height = 10
  Placement = pos=(0,0,36.15) rot=(0,0,1;0rad)
  Radius = 4
FEATURE [Sketcher::SketchObject] Sketch011  label="topSketch005"
  FullyConstrained = true
  sketch-geometry (4):
    g0: LineSegment StartX=16.8446 StartY=31.512 StartZ=0 EndX=16.3251 EndY=34.4666 EndZ=0
    g1: ArcOfCircle CenterX=19 CenterY=19.2524 CenterZ=0 NormalX=0 NormalY=0 NormalZ=1 AngleXU=0 Radius=15.4476 StartAngle=1.74483 EndAngle=2.72717
    g2: ArcOfCircle CenterX=19 CenterY=19.2524 CenterZ=0 NormalX=0 NormalY=0 NormalZ=1 AngleXU=0 Radius=12.4476 StartAngle=1.74483 EndAngle=2.73189
    g3: LineSegment StartX=4.86004 StartY=25.4725 StartZ=0 EndX=7.58253 EndY=24.2107 EndZ=0
  constraints (7):
    c: Block(g0)
    c: Coincident(g1,g0)
    c: Coincident(g2,g0)
    c: Coincident(g3,g1)
    c: Coincident(g3,g2)
    c: Block(g1)
    c: Block(g2)
FEATURE [Part::Extrusion] Extrude010
  Base = -> Sketch011
  Dir = (0,0,1)
  DirMode = 2
  FaceMakerClass = Part::FaceMakerBullseye
  LengthFwd = 10.6
  LengthRev = 0
  Placement = pos=(0,0,31) rot=(0,0,1;0rad)
  Solid = true
  Symmetric = false
FEATURE [Part::Cylinder] Cylinder023
  Angle = 360
  AttacherType = Attacher::AttachEngine3D
  Height = 20
  Placement = pos=(0,0,36.15) rot=(0,0,1;0rad)
  Radius = 8.2
FEATURE [Part::MultiFuse] Fusion039  label="removeToCreteHoleForPlugHousing008"
  Placement = pos=(-42,19,36) rot=(0,1,0;1.5708rad)
  Shapes = -> [Cylinder023,Cylinder022]
FEATURE [Part::Cut] Cut012
  Base = -> Extrude010
  Placement = pos=(0,0,-0.3) rot=(0,0,1;0rad)
  Tool = -> Fusion039
FEATURE [Part::Cut] Cut013
  Base = -> Box010
  Tool = -> Cut012
FEATURE [Part::Fillet] Fillet014
  Base = -> Cut013
  Edges = 1 edges r=0.7: [Edge13]
FEATURE [Part::Fillet] Fillet015
  Base = -> Fillet014
  Edges = 1 edges r=0.7: [Edge13]
FEATURE [Part::Fillet] Fillet016
  Base = -> Fillet015
  Edges = 1 edges r=0.7: [Edge16]
FEATURE [Part::Fillet] Fillet017
  Base = -> Fillet016
  Edges = 1 edges r=0.7: [Edge11]
FEATURE [Part::Fillet] Fillet018
  Base = -> Fillet017
  Edges = 1 edges r=0.7: [Edge10]
FEATURE [Part::Fillet] Fillet019
  Base = -> Fillet018
  Edges = 1 edges r=1.2: [Edge5]
FEATURE [Part::Fillet] Fillet020
  Base = -> Fillet019
  Edges = 1 edges r=1.2: [Edge12]
FEATURE [Part::Fillet] Fillet021
  Base = -> Fillet020
  Edges = 1 edges r=2: [Edge1]
  Placement = pos=(0.3,0,0) rot=(0,0,1;0rad)
FEATURE [Part::MultiFuse] Fusion040  label="top005"
  Shapes = -> [Cut008,Fillet021]
FEATURE [Part::MultiFuse] Fusion041  label="wireHolder"
  Shapes = -> [Fusion033,Fillet013]
FEATURE [Part::MultiFuse] Fusion042
  Shapes = -> [Fillet007,Fusion041]
FEATURE [Part::MultiFuse] Fusion043  label="wireHolder001"
  Shapes = -> [Fusion042,Fillet010]
FEATURE [Part::MultiFuse] Fusion044  label="wireHolder002"
  Shapes = -> [Fillet006,Fusion037,Fusion043]
FEATURE [Part::Feature] Face026
  shape: bbox 11 x 6 x 2e-07 mm, 1 faces, 0 solids (baked)
FEATURE [Part::Revolution] Revolve026
  Angle = 360
  Axis = (0,1,0)
  Base = (0,0,0)
  FaceMakerClass = Part::FaceMakerBullseye
  Placement = pos=(30.3,-1,19.7) rot=(0,0,1;0rad)
  Solid = false
  Source = -> Face026
  Symmetric = false
FEATURE [Sketcher::SketchObject] Sketch013  label="topSketch006"
  FullyConstrained = true
  sketch-geometry (13):
    g0: LineSegment StartX=117 StartY=19 StartZ=0 EndX=117 EndY=38 EndZ=0
    g1: ArcOfCircle CenterX=98 CenterY=19 CenterZ=0 NormalX=0 NormalY=0 NormalZ=1 AngleXU=0 Radius=19 StartAngle=5.7297 EndAngle=6.28319
    g2: LineSegment StartX=0 StartY=3 StartZ=0 EndX=0 EndY=19 EndZ=0
    g3: LineSegment StartX=19 StartY=38 StartZ=0 EndX=117 EndY=38 EndZ=0
    g4: ArcOfCircle CenterX=19 CenterY=19 CenterZ=0 NormalX=0 NormalY=0 NormalZ=1 AngleXU=0 Radius=19 StartAngle=1.5708 EndAngle=3.14159
    g5: ArcOfCircle CenterX=19 CenterY=19 CenterZ=0 NormalX=0 NormalY=0 NormalZ=1 AngleXU=0 Radius=16 StartAngle=1.5708 EndAngle=3.14159
    g6: ArcOfCircle CenterX=98 CenterY=19 CenterZ=0 NormalX=0 NormalY=0 NormalZ=1 AngleXU=0 Radius=16 StartAngle=5.60905 EndAngle=6.28319
    g7: LineSegment StartX=114 StartY=19 StartZ=0 EndX=114 EndY=35 EndZ=0
    g8: LineSegment StartX=110.5 StartY=9.01251 StartZ=0 EndX=114.163 EndY=9.01251 EndZ=0
    g9: LineSegment StartX=114 StartY=35 StartZ=0 EndX=19 EndY=35 EndZ=0
    g10: LineSegment StartX=0 StartY=3 StartZ=0 EndX=0 EndY=0 EndZ=0
    g11: LineSegment StartX=3 StartY=0 StartZ=0 EndX=0 EndY=0 EndZ=0
    g12: LineSegment StartX=3 StartY=19 StartZ=0 EndX=3 EndY=0 EndZ=0
  constraints (33):
    c: Vertical(g0)
    c: Distance(g0) = 19
    c: Block(g0)
    c: Coincident(g1,g0)
    c: Block(g1)
    c: Vertical(g2)
    c: Block(g2)
    c: Coincident(g3,g0)
    c: Horizontal(g3)
    c: Distance(g3) = 98
    c: Coincident(g4,g3)
    c: Coincident(g4,g2)
    c: Block(g4)
    c: Coincident(g5,g4)
    c: Coincident(g6,g1)
    c: Block(g6)
    c: Block(g5)
    c: Coincident(g7,g6)
    c: Vertical(g7)
    c: Coincident(g8,g6)
    c: Coincident(g8,g1)
    c: Coincident(g9,g7)
    c: Coincident(g9,g5)
    c: Horizontal(g9)
    c: Tangent(g9,g5)
    c: Coincident(g10,g2)
    c: Distance(g10) = 3
    c: Vertical(g10)
    c: Coincident(g11,g10)
    c: Horizontal(g11)
    c: Coincident(g12,g5)
    c: Coincident(g12,g11)
    c: Vertical(g12)
FEATURE [Part::Extrusion] Extrude011  label="top006"
  Base = -> Sketch013
  Dir = (0,0,1)
  DirMode = 2
  FaceMakerClass = Part::FaceMakerBullseye
  LengthFwd = 72
  LengthRev = 0
  Solid = true
  Symmetric = false
FEATURE [Sketcher::SketchObject] Sketch014
  FullyConstrained = true
  MapMode = 3
  Placement = pos=(0,0,0) rot=(1,0,0;1.5708rad)
  Support = -> [Extrude011]
  sketch-geometry (8):
    g0: Circle CenterX=80.351 CenterY=-67.6202 CenterZ=0 NormalX=0 NormalY=0 NormalZ=1 AngleXU=0 Radius=2
    g1: Circle CenterX=80.351 CenterY=-67.6202 CenterZ=0 NormalX=0 NormalY=0 NormalZ=1 AngleXU=0 Radius=3
    g2: Circle CenterX=80.351 CenterY=-4.92017 CenterZ=0 NormalX=0 NormalY=0 NormalZ=1 AngleXU=0 Radius=2
    g3: Circle CenterX=80.351 CenterY=-4.92017 CenterZ=0 NormalX=0 NormalY=0 NormalZ=1 AngleXU=0 Radius=3
    g4: Circle CenterX=23.851 CenterY=-4.92017 CenterZ=0 NormalX=0 NormalY=0 NormalZ=1 AngleXU=0 Radius=2
    g5: Circle CenterX=23.851 CenterY=-4.92017 CenterZ=0 NormalX=0 NormalY=0 NormalZ=1 AngleXU=0 Radius=3
    g6: Circle CenterX=23.851 CenterY=-67.6202 CenterZ=0 NormalX=0 NormalY=0 NormalZ=1 AngleXU=0 Radius=2
    g7: Circle CenterX=23.851 CenterY=-67.6202 CenterZ=0 NormalX=0 NormalY=0 NormalZ=1 AngleXU=0 Radius=3
  constraints (8):
    c: Block(g3)
    c: Block(g2)
    c: Block(g1)
    c: Block(g0)
    c: Block(g6)
    c: Block(g7)
    c: Block(g4)
    c: Block(g5)
FEATURE [Part::Feature] Face027
  shape: bbox 11 x 6 x 2e-07 mm, 1 faces, 0 solids (baked)
FEATURE [Part::Revolution] Revolve027
  Angle = 360
  Axis = (0,1,0)
  Base = (0,0,0)
  FaceMakerClass = Part::FaceMakerBullseye
  Placement = pos=(30.3,-1,51.7) rot=(0,0,1;0rad)
  Solid = false
  Source = -> Face027
  Symmetric = false
FEATURE [Part::Feature] Face028
  shape: bbox 11 x 6 x 2e-07 mm, 1 faces, 0 solids (baked)
FEATURE [Part::Revolution] Revolve028
  Angle = 360
  Axis = (0,1,0)
  Base = (0,0,0)
  FaceMakerClass = Part::FaceMakerBullseye
  Placement = pos=(62.3,-1,19.7) rot=(0,0,1;0rad)
  Solid = false
  Source = -> Face028
  Symmetric = false
FEATURE [Part::Feature] Face029
  shape: bbox 11 x 6 x 2e-07 mm, 1 faces, 0 solids (baked)
FEATURE [Part::Revolution] Revolve029
  Angle = 360
  Axis = (0,1,0)
  Base = (0,0,0)
  FaceMakerClass = Part::FaceMakerBullseye
  Placement = pos=(62.3,-1,51.7) rot=(0,0,1;0rad)
  Solid = false
  Source = -> Face029
  Symmetric = false
FEATURE [Part::Feature] Wire
  shape: bbox 11 x 5.2 x 2e-07 mm, 0 faces, 0 solids (baked)
FEATURE [Part::Revolution] Revolve030
  Angle = 360
  Axis = (0,1,0)
  Base = (0,0,0)
  FaceMakerClass = Part::FaceMakerBullseye
  Placement = pos=(30.3,38,19.7) rot=(0,0,1;0rad)
  Solid = true
  Source = -> Wire
  Symmetric = false
FEATURE [Part::Feature] Wire001
  shape: bbox 11 x 5.2 x 2e-07 mm, 0 faces, 0 solids (baked)
FEATURE [Part::Revolution] Revolve031
  Angle = 360
  Axis = (0,1,0)
  Base = (0,0,0)
  FaceMakerClass = Part::FaceMakerBullseye
  Placement = pos=(30.3,38,51.7) rot=(0,0,1;0rad)
  Solid = true
  Source = -> Wire001
  Symmetric = false
FEATURE [Part::Feature] Wire002
  shape: bbox 11 x 5.2 x 2e-07 mm, 0 faces, 0 solids (baked)
FEATURE [Part::Revolution] Revolve032
  Angle = 360
  Axis = (0,1,0)
  Base = (0,0,0)
  FaceMakerClass = Part::FaceMakerBullseye
  Placement = pos=(62.3,38,51.7) rot=(0,0,1;0rad)
  Solid = true
  Source = -> Wire002
  Symmetric = false
FEATURE [Part::Feature] Wire003
  shape: bbox 11 x 5.2 x 2e-07 mm, 0 faces, 0 solids (baked)
FEATURE [Part::Revolution] Revolve033
  Angle = 360
  Axis = (0,1,0)
  Base = (0,0,0)
  FaceMakerClass = Part::FaceMakerBullseye
  Placement = pos=(62.3,38,19.7) rot=(0,0,1;0rad)
  Solid = true
  Source = -> Wire003
  Symmetric = false
FEATURE [Part::MultiFuse] Fusion045  label="altRandScrewHousing"
  Shapes = -> [Revolve029,Revolve027,Revolve028,Revolve026]
FEATURE [Part::MultiFuse] Fusion046  label="fanScrewHousing"
  Shapes = -> [Revolve033,Revolve032,Revolve031,Revolve030]
FEATURE [Sketcher::SketchObject] Sketch015
  FullyConstrained = true
  sketch-geometry (17):
    g0: Circle CenterX=-3.5 CenterY=23.5 CenterZ=0 NormalX=0 NormalY=0 NormalZ=1 AngleXU=0 Radius=1
    g1: Circle CenterX=-1 CenterY=15.25 CenterZ=0 NormalX=0 NormalY=0 NormalZ=1 AngleXU=0 Radius=1
    g2: Circle CenterX=-3.5 CenterY=7 CenterZ=0 NormalX=0 NormalY=0 NormalZ=1 AngleXU=0 Radius=1
    g3: BSplineCurve PolesCount=3 KnotsCount=2 Degree=2 IsPeriodic=0
    g4: GeomPoint X=-3.5 Y=23.5 Z=0
    g5: GeomPoint X=-3.5 Y=7 Z=0
    g6: Circle CenterX=-4.8 CenterY=30.5 CenterZ=0 NormalX=0 NormalY=0 NormalZ=1 AngleXU=0 Radius=1
    g7: Circle CenterX=-3.5 CenterY=30.5 CenterZ=0 NormalX=0 NormalY=0 NormalZ=1 AngleXU=0 Radius=1
    g8: Circle CenterX=-3.5 CenterY=29.2 CenterZ=0 NormalX=0 NormalY=0 NormalZ=1 AngleXU=0 Radius=1
    g9: BSplineCurve PolesCount=3 KnotsCount=2 Degree=2 IsPeriodic=0
    g10: GeomPoint X=-4.8 Y=30.5 Z=0
    g11: GeomPoint X=-3.5 Y=29.2 Z=0
    g12: LineSegment StartX=-3.5 StartY=29.2 StartZ=0 EndX=-3.5 EndY=23.5 EndZ=0
    g13: LineSegment StartX=-4.8 StartY=30.5 StartZ=0 EndX=0 EndY=30.5 EndZ=0
    g14: LineSegment StartX=-3.5 StartY=0.3 StartZ=0 EndX=0 EndY=0.3 EndZ=0
    g15: LineSegment StartX=-3.5 StartY=0.3 StartZ=0 EndX=-3.5 EndY=7 EndZ=0
    g16: LineSegment StartX=0 StartY=0.3 StartZ=0 EndX=0 EndY=30.5 EndZ=0
  constraints (33):
    c: Weight(g0) = 1
    c: Equal(g0,g1)
    c: Equal(g0,g2)
    c: InternalAlignment(g0,g3)
    c: InternalAlignment(g1,g3)
    c: InternalAlignment(g2,g3)
    c: InternalAlignment(g4,g3)
    c: InternalAlignment(g5,g3)
    c: Block(g3)
    c: Weight(g6) = 1
    c: Equal(g6,g7)
    c: Equal(g6,g8)
    c: InternalAlignment(g6,g9)
    c: InternalAlignment(g7,g9)
    c: InternalAlignment(g8,g9)
    c: InternalAlignment(g10,g9)
    c: InternalAlignment(g11,g9)
    c: Block(g9)
    c: Coincident(g12,g9)
    c: Coincident(g12,g3)
    c: Vertical(g12)
    c: Coincident(g13,g9)
    c: Horizontal(g13)
    c: Distance(g13) = 4.8
    c: Horizontal(g14)
    c: Block(g14)
    c: Coincident(g15,g14)
    c: Coincident(g15,g3)
    c: Vertical(g15)
    c: Coincident(g16,g14)
    c: Coincident(g16,g13)
    c: Vertical(g16)
    c: Tangent(g16,g1)
FEATURE [Sketcher::SketchObject] Sketch016
  FullyConstrained = true
  sketch-geometry (16):
    g0: Circle CenterX=-3.5 CenterY=23.5 CenterZ=0 NormalX=0 NormalY=0 NormalZ=1 AngleXU=0 Radius=1
    g1: Circle CenterX=-1 CenterY=15.25 CenterZ=0 NormalX=0 NormalY=0 NormalZ=1 AngleXU=0 Radius=1
    g2: Circle CenterX=-3.5 CenterY=7 CenterZ=0 NormalX=0 NormalY=0 NormalZ=1 AngleXU=0 Radius=1
    g3: BSplineCurve PolesCount=3 KnotsCount=2 Degree=2 IsPeriodic=0
    g4: GeomPoint X=-3.5 Y=23.5 Z=0
    g5: GeomPoint X=-3.5 Y=7 Z=0
    g6: LineSegment StartX=-3.5 StartY=28.2 StartZ=0 EndX=-3.5 EndY=23.5 EndZ=0
    g7: LineSegment StartX=0 StartY=29.5 StartZ=0 EndX=0 EndY=30 EndZ=0
    g8: LineSegment StartX=-3.5 StartY=28.2 StartZ=0 EndX=-3.5 EndY=30 EndZ=0
    g9: LineSegment StartX=0 StartY=30 StartZ=0 EndX=0 EndY=30.5 EndZ=0
    g10: LineSegment StartX=0 StartY=30.5 StartZ=0 EndX=-3.5 EndY=30.5 EndZ=0
    g11: LineSegment StartX=-3.5 StartY=30.5 StartZ=0 EndX=-3.5 EndY=30 EndZ=0
    g12: LineSegment StartX=0 StartY=29.5 StartZ=0 EndX=0 EndY=5 EndZ=0
    g13: LineSegment StartX=-3.5 StartY=0.3 StartZ=0 EndX=-3.5 EndY=7 EndZ=0
    g14: LineSegment StartX=-3.5 StartY=0.3 StartZ=0 EndX=0 EndY=0.3 EndZ=0
    g15: LineSegment StartX=0 StartY=5 StartZ=0 EndX=0 EndY=0.3 EndZ=0
  constraints (39):
    c: Weight(g0) = 1
    c: Equal(g0,g1)
    c: Equal(g0,g2)
    c: InternalAlignment(g0,g3)
    c: InternalAlignment(g1,g3)
    c: InternalAlignment(g2,g3)
    c: InternalAlignment(g4,g3)
    c: InternalAlignment(g5,g3)
    c: Block(g3)
    c: Coincident(g6,g3)
    c: Vertical(g6)
    c: Vertical(g7)
    c: Distance(g7) = 0.5
    c: Coincident(g8,g6)
    c: Vertical(g8)
    c: Block(g6)
    c: Block(g7)
    c: Vertical(g9)
    c: Equal(g7,g9) = 0.5
    c: Block(g9)
    c: Coincident(g9,g7)
    c: Horizontal(g10)
    c: Coincident(g10,g9)
    c: Coincident(g11,g10)
    c: Coincident(g11,g8)
    c: Vertical(g11)
    c: Block(g11)
    c: Coincident(g12,g7)
    c: Vertical(g12)
    c: Coincident(g13,g3)
    c: Vertical(g13)
    c: Distance(g13) = 6.7
    c: Coincident(g14,g13)
    c: Horizontal(g14)
    c: Block(g14)
    c: Coincident(g15,g12)
    c: Coincident(g15,g14)
    c: Vertical(g15)
    c: Block(g15)
FEATURE [Sketcher::SketchObject] Sketch017
  FullyConstrained = true
  sketch-geometry (11):
    g0: LineSegment StartX=-3.5 StartY=1e-16 StartZ=0 EndX=-1.6 EndY=1e-16 EndZ=0
    g1: LineSegment StartX=-1.6 StartY=1e-16 StartZ=0 EndX=-1.6 EndY=1.5 EndZ=0
    g2: LineSegment StartX=-3.5 StartY=1.5 StartZ=0 EndX=-1.6 EndY=1.5 EndZ=0
    g3: LineSegment StartX=-3.5 StartY=1e-16 StartZ=0 EndX=-4.8 EndY=1e-16 EndZ=0
    g4: Circle CenterX=-3.5 CenterY=1.3 CenterZ=0 NormalX=0 NormalY=0 NormalZ=1 AngleXU=0 Radius=1
    g5: Circle CenterX=-3.5 CenterY=1e-16 CenterZ=0 NormalX=0 NormalY=0 NormalZ=1 AngleXU=0 Radius=1
    g6: Circle CenterX=-4.8 CenterY=1e-16 CenterZ=0 NormalX=0 NormalY=0 NormalZ=1 AngleXU=0 Radius=1
    g7: BSplineCurve PolesCount=3 KnotsCount=2 Degree=2 IsPeriodic=0
    g8: GeomPoint X=-3.5 Y=1.3 Z=0
    g9: GeomPoint X=-4.8 Y=1e-16 Z=0
    g10: LineSegment StartX=-3.5 StartY=1.3 StartZ=0 EndX=-3.5 EndY=1.5 EndZ=0
  constraints (24):
    c: Horizontal(g0)
    c: Distance(g0) = 1.9
    c: Block(g0)
    c: Coincident(g1,g0)
    c: Vertical(g1)
    c: Coincident(g2,g1)
    c: Horizontal(g2)
    c: Coincident(g3,g0)
    c: Horizontal(g3)
    c: Distance(g3) = 1.3
    c: Weight(g4) = 1
    c: Equal(g4,g5)
    c: Coincident(g5,g0)
    c: Equal(g4,g6)
    c: Coincident(g7,g3)
    c: InternalAlignment(g4,g7)
    c: InternalAlignment(g5,g7)
    c: InternalAlignment(g6,g7)
    c: InternalAlignment(g8,g7)
    c: InternalAlignment(g9,g7)
    c: Coincident(g10,g7)
    c: Coincident(g10,g2)
    c: Vertical(g10)
    c: Block(g10)
FEATURE [Part::Feature] Face035
  shape: bbox 3.2 x 1.5 x 2e-07 mm, 1 faces, 0 solids (baked)
FEATURE [Part::Revolution] Revolve039  label="backCaseScrewRetainer"
  Angle = 360
  Axis = (0,1,0)
  Base = (0,0,0)
  FaceMakerClass = Part::FaceMakerBullseye
  Placement = pos=(12.5,3,62) rot=(0,0,1;0rad)
  Solid = false
  Source = -> Face035
  Symmetric = false
FEATURE [Part::Feature] Face036
  shape: bbox 3.2 x 1.5 x 2e-07 mm, 1 faces, 0 solids (baked)
FEATURE [Part::Feature] Face039
  shape: bbox 4.8 x 30.2 x 2e-07 mm, 1 faces, 0 solids (baked)
FEATURE [Part::Revolution] Revolve043  label="frontCaseScrewPost002"
  Angle = 360
  Axis = (0,1,0)
  Base = (0,0,0)
  FaceMakerClass = Part::FaceMakerBullseye
  Placement = pos=(89.5,4.5,3.5) rot=(0,0,1;0rad)
  Solid = false
  Source = -> Face039
  Symmetric = false
FEATURE [Part::Feature] Face042
  shape: bbox 4.8 x 30.2 x 2e-07 mm, 1 faces, 0 solids (baked)
FEATURE [Part::Revolution] Revolve046  label="frontCaseScrewPost003"
  Angle = 360
  Axis = (0,1,0)
  Base = (0,0,0)
  FaceMakerClass = Part::FaceMakerBullseye
  Placement = pos=(89.5,4.5,68.5) rot=(0,0,1;0rad)
  Solid = false
  Source = -> Face042
  Symmetric = false
FEATURE [Part::Feature] Face043
  shape: bbox 3.2 x 1.5 x 2e-07 mm, 1 faces, 0 solids (baked)
FEATURE [Part::Revolution] Revolve047  label="frontCaseScrewRetainer002"
  Angle = 360
  Axis = (0,1,0)
  Base = (0,0,0)
  FaceMakerClass = Part::FaceMakerBullseye
  Placement = pos=(89.5,3,68.5) rot=(0,0,1;0rad)
  Solid = false
  Source = -> Face043
  Symmetric = false
FEATURE [Part::Feature] Face044
  shape: bbox 3.2 x 1.5 x 2e-07 mm, 1 faces, 0 solids (baked)
FEATURE [Part::Revolution] Revolve048  label="frontCaseScrewRetainer003"
  Angle = 360
  Axis = (0,1,0)
  Base = (0,0,0)
  FaceMakerClass = Part::FaceMakerBullseye
  Placement = pos=(89.5,3,3.5) rot=(0,0,1;0rad)
  Solid = false
  Source = -> Face044
  Symmetric = false
FEATURE [App::MeasureDistance] Distance002  label="Distance: 1.67 mm"
  Distance = 1.66921
  P1 = (99.2361,4.7524,71.7)
  P2 = (99.2347,6.42161,71.7)
FEATURE [Sketcher::SketchObject] Sketch018
  FullyConstrained = true
  sketch-geometry (7):
    g0: LineSegment StartX=0 StartY=0 StartZ=0 EndX=0 EndY=6 EndZ=0
    g1: Circle CenterX=0 CenterY=0 CenterZ=0 NormalX=0 NormalY=0 NormalZ=1 AngleXU=0 Radius=1
    g2: Circle CenterX=8 CenterY=6 CenterZ=0 NormalX=0 NormalY=0 NormalZ=1 AngleXU=0 Radius=1
    g3: BSplineCurve PolesCount=3 KnotsCount=2 Degree=2 IsPeriodic=0
    g4: GeomPoint X=0 Y=0 Z=0
    g5: GeomPoint X=8 Y=6 Z=0
    g6: LineSegment StartX=0 StartY=6 StartZ=0 EndX=8 EndY=6 EndZ=0
  constraints (14):
    c: Coincident(g0,g-1)
    c: Distance(g0) = 6
    c: Vertical(g0)
    c: Coincident(g3,g0)
    c: Weight(g1) = 1
    c: Equal(g1,g2)
    c: InternalAlignment(g1,g3)
    c: InternalAlignment(g2,g3)
    c: InternalAlignment(g4,g3)
    c: InternalAlignment(g5,g3)
    c: Block(g3)
    c: Coincident(g6,g0)
    c: Coincident(g6,g3)
    c: Horizontal(g6)
FEATURE [Part::Extrusion] Extrude012  label="caseScrewPillarBracket"
  Base = -> Sketch018
  Dir = (0,0,1)
  DirMode = 2
  FaceMakerClass = Part::FaceMakerBullseye
  LengthFwd = 2.4
  LengthRev = 0
  Placement = pos=(15.76,29,8.8) rot=(0,1,0;0rad)
  Solid = true
  Symmetric = false
FEATURE [Sketcher::SketchObject] Sketch019
  FullyConstrained = true
  sketch-geometry (7):
    g0: LineSegment StartX=0 StartY=0 StartZ=0 EndX=0 EndY=6 EndZ=0
    g1: Circle CenterX=0 CenterY=0 CenterZ=0 NormalX=0 NormalY=0 NormalZ=1 AngleXU=0 Radius=1
    g2: Circle CenterX=8 CenterY=6 CenterZ=0 NormalX=0 NormalY=0 NormalZ=1 AngleXU=0 Radius=1
    g3: BSplineCurve PolesCount=3 KnotsCount=2 Degree=2 IsPeriodic=0
    g4: GeomPoint X=0 Y=0 Z=0
    g5: GeomPoint X=8 Y=6 Z=0
    g6: LineSegment StartX=0 StartY=6 StartZ=0 EndX=8 EndY=6 EndZ=0
  constraints (14):
    c: Coincident(g0,g-1)
    c: Distance(g0) = 6
    c: Vertical(g0)
    c: Coincident(g3,g0)
    c: Weight(g1) = 1
    c: Equal(g1,g2)
    c: InternalAlignment(g1,g3)
    c: InternalAlignment(g2,g3)
    c: InternalAlignment(g4,g3)
    c: InternalAlignment(g5,g3)
    c: Block(g3)
    c: Coincident(g6,g0)
    c: Coincident(g6,g3)
    c: Horizontal(g6)
FEATURE [Part::Extrusion] Extrude013  label="caseScrewPillarBracket001"
  Base = -> Sketch019
  Dir = (0,0,1)
  DirMode = 2
  FaceMakerClass = Part::FaceMakerBullseye
  LengthFwd = 2.4
  LengthRev = 0
  Placement = pos=(15.76,29,60.8) rot=(0,0,1;0rad)
  Solid = true
  Symmetric = false
FEATURE [Sketcher::SketchObject] Sketch020
  FullyConstrained = true
  sketch-geometry (7):
    g0: LineSegment StartX=0 StartY=0 StartZ=0 EndX=0 EndY=6 EndZ=0
    g1: Circle CenterX=0 CenterY=0 CenterZ=0 NormalX=0 NormalY=0 NormalZ=1 AngleXU=0 Radius=1
    g2: Circle CenterX=8 CenterY=6 CenterZ=0 NormalX=0 NormalY=0 NormalZ=1 AngleXU=0 Radius=1
    g3: BSplineCurve PolesCount=3 KnotsCount=2 Degree=2 IsPeriodic=0
    g4: GeomPoint X=0 Y=0 Z=0
    g5: GeomPoint X=8 Y=6 Z=0
    g6: LineSegment StartX=0 StartY=6 StartZ=0 EndX=8 EndY=6 EndZ=0
  constraints (14):
    c: Coincident(g0,g-1)
    c: Distance(g0) = 6
    c: Vertical(g0)
    c: Coincident(g3,g0)
    c: Weight(g1) = 1
    c: Equal(g1,g2)
    c: InternalAlignment(g1,g3)
    c: InternalAlignment(g2,g3)
    c: InternalAlignment(g4,g3)
    c: InternalAlignment(g5,g3)
    c: Block(g3)
    c: Coincident(g6,g0)
    c: Coincident(g6,g3)
    c: Horizontal(g6)
FEATURE [Part::Extrusion] Extrude014  label="caseScrewPillarBracket002"
  Base = -> Sketch020
  Dir = (0,0,1)
  DirMode = 2
  FaceMakerClass = Part::FaceMakerBullseye
  LengthFwd = 2.4
  LengthRev = 0
  Placement = pos=(13.7,29,13.26) rot=(0,-1,0;1.5708rad)
  Solid = true
  Symmetric = false
FEATURE [Sketcher::SketchObject] Sketch021
  FullyConstrained = true
  sketch-geometry (7):
    g0: LineSegment StartX=0 StartY=0 StartZ=0 EndX=0 EndY=6 EndZ=0
    g1: Circle CenterX=0 CenterY=0 CenterZ=0 NormalX=0 NormalY=0 NormalZ=1 AngleXU=0 Radius=1
    g2: Circle CenterX=8 CenterY=6 CenterZ=0 NormalX=0 NormalY=0 NormalZ=1 AngleXU=0 Radius=1
    g3: BSplineCurve PolesCount=3 KnotsCount=2 Degree=2 IsPeriodic=0
    g4: GeomPoint X=0 Y=0 Z=0
    g5: GeomPoint X=8 Y=6 Z=0
    g6: LineSegment StartX=0 StartY=6 StartZ=0 EndX=8 EndY=6 EndZ=0
  constraints (14):
    c: Coincident(g0,g-1)
    c: Distance(g0) = 6
    c: Vertical(g0)
    c: Coincident(g3,g0)
    c: Weight(g1) = 1
    c: Equal(g1,g2)
    c: InternalAlignment(g1,g3)
    c: InternalAlignment(g2,g3)
    c: InternalAlignment(g4,g3)
    c: InternalAlignment(g5,g3)
    c: Block(g3)
    c: Coincident(g6,g0)
    c: Coincident(g6,g3)
    c: Horizontal(g6)
FEATURE [Part::Extrusion] Extrude015  label="caseScrewPillarBracket003"
  Base = -> Sketch021
  Dir = (0,0,1)
  DirMode = 2
  FaceMakerClass = Part::FaceMakerBullseye
  LengthFwd = 2.4
  LengthRev = 0
  Placement = pos=(11.3,29,58.74) rot=(0,1,0;1.5708rad)
  Solid = true
  Symmetric = false
FEATURE [Sketcher::SketchObject] Sketch022
  FullyConstrained = true
  sketch-geometry (7):
    g0: LineSegment StartX=0 StartY=0 StartZ=0 EndX=0 EndY=6 EndZ=0
    g1: Circle CenterX=0 CenterY=0 CenterZ=0 NormalX=0 NormalY=0 NormalZ=1 AngleXU=0 Radius=1
    g2: Circle CenterX=8 CenterY=6 CenterZ=0 NormalX=0 NormalY=0 NormalZ=1 AngleXU=0 Radius=1
    g3: BSplineCurve PolesCount=3 KnotsCount=2 Degree=2 IsPeriodic=0
    g4: GeomPoint X=0 Y=0 Z=0
    g5: GeomPoint X=8 Y=6 Z=0
    g6: LineSegment StartX=0 StartY=6 StartZ=0 EndX=8 EndY=6 EndZ=0
  constraints (14):
    c: Coincident(g0,g-1)
    c: Distance(g0) = 6
    c: Vertical(g0)
    c: Coincident(g3,g0)
    c: Weight(g1) = 1
    c: Equal(g1,g2)
    c: InternalAlignment(g1,g3)
    c: InternalAlignment(g2,g3)
    c: InternalAlignment(g4,g3)
    c: InternalAlignment(g5,g3)
    c: Block(g3)
    c: Coincident(g6,g0)
    c: Coincident(g6,g3)
    c: Horizontal(g6)
FEATURE [Part::Extrusion] Extrude016  label="caseScrewPillarBracket004"
  Base = -> Sketch022
  Dir = (0,0,1)
  DirMode = 2
  FaceMakerClass = Part::FaceMakerBullseye
  LengthFwd = 2.4
  LengthRev = 0
  Placement = pos=(88.3,29,65.23) rot=(0,1,0;1.5708rad)
  Solid = true
  Symmetric = false
FEATURE [Sketcher::SketchObject] Sketch023
  FullyConstrained = true
  sketch-geometry (7):
    g0: LineSegment StartX=0 StartY=0 StartZ=0 EndX=0 EndY=6 EndZ=0
    g1: Circle CenterX=0 CenterY=0 CenterZ=0 NormalX=0 NormalY=0 NormalZ=1 AngleXU=0 Radius=1
    g2: Circle CenterX=8 CenterY=6 CenterZ=0 NormalX=0 NormalY=0 NormalZ=1 AngleXU=0 Radius=1
    g3: BSplineCurve PolesCount=3 KnotsCount=2 Degree=2 IsPeriodic=0
    g4: GeomPoint X=0 Y=0 Z=0
    g5: GeomPoint X=8 Y=6 Z=0
    g6: LineSegment StartX=0 StartY=6 StartZ=0 EndX=8 EndY=6 EndZ=0
  constraints (14):
    c: Coincident(g0,g-1)
    c: Distance(g0) = 6
    c: Vertical(g0)
    c: Coincident(g3,g0)
    c: Weight(g1) = 1
    c: Equal(g1,g2)
    c: InternalAlignment(g1,g3)
    c: InternalAlignment(g2,g3)
    c: InternalAlignment(g4,g3)
    c: InternalAlignment(g5,g3)
    c: Block(g3)
    c: Coincident(g6,g0)
    c: Coincident(g6,g3)
    c: Horizontal(g6)
FEATURE [Part::Extrusion] Extrude017  label="caseScrewPillarBracket005"
  Base = -> Sketch023
  Dir = (0,0,1)
  DirMode = 2
  FaceMakerClass = Part::FaceMakerBullseye
  LengthFwd = 2.4
  LengthRev = 0
  Placement = pos=(90.7,29,6.77) rot=(0,-1,0;1.5708rad)
  Solid = true
  Symmetric = false
FEATURE [Sketcher::SketchObject] Sketch024
  FullyConstrained = true
  sketch-geometry (7):
    g0: LineSegment StartX=0 StartY=0 StartZ=0 EndX=0 EndY=6 EndZ=0
    g1: Circle CenterX=0 CenterY=0 CenterZ=0 NormalX=0 NormalY=0 NormalZ=1 AngleXU=0 Radius=1
    g2: Circle CenterX=8 CenterY=6 CenterZ=0 NormalX=0 NormalY=0 NormalZ=1 AngleXU=0 Radius=1
    g3: BSplineCurve PolesCount=3 KnotsCount=2 Degree=2 IsPeriodic=0
    g4: GeomPoint X=0 Y=0 Z=0
    g5: GeomPoint X=8 Y=6 Z=0
    g6: LineSegment StartX=0 StartY=6 StartZ=0 EndX=8 EndY=6 EndZ=0
  constraints (14):
    c: Coincident(g0,g-1)
    c: Distance(g0) = 6
    c: Vertical(g0)
    c: Coincident(g3,g0)
    c: Weight(g1) = 1
    c: Equal(g1,g2)
    c: InternalAlignment(g1,g3)
    c: InternalAlignment(g2,g3)
    c: InternalAlignment(g4,g3)
    c: InternalAlignment(g5,g3)
    c: Block(g3)
    c: Coincident(g6,g0)
    c: Coincident(g6,g3)
    c: Horizontal(g6)
FEATURE [Part::Extrusion] Extrude018  label="caseScrewPillarBracket006"
  Base = -> Sketch024
  Dir = (0,0,1)
  DirMode = 2
  FaceMakerClass = Part::FaceMakerBullseye
  LengthFwd = 2.4
  LengthRev = 0
  Placement = pos=(103.7,29,6.77) rot=(0,-1,0;1.5708rad)
  Solid = true
  Symmetric = false
FEATURE [Sketcher::SketchObject] Sketch025
  FullyConstrained = true
  sketch-geometry (7):
    g0: LineSegment StartX=0 StartY=0 StartZ=0 EndX=0 EndY=6 EndZ=0
    g1: Circle CenterX=0 CenterY=0 CenterZ=0 NormalX=0 NormalY=0 NormalZ=1 AngleXU=0 Radius=1
    g2: Circle CenterX=8 CenterY=6 CenterZ=0 NormalX=0 NormalY=0 NormalZ=1 AngleXU=0 Radius=1
    g3: BSplineCurve PolesCount=3 KnotsCount=2 Degree=2 IsPeriodic=0
    g4: GeomPoint X=0 Y=0 Z=0
    g5: GeomPoint X=8 Y=6 Z=0
    g6: LineSegment StartX=0 StartY=6 StartZ=0 EndX=8 EndY=6 EndZ=0
  constraints (14):
    c: Coincident(g0,g-1)
    c: Distance(g0) = 6
    c: Vertical(g0)
    c: Coincident(g3,g0)
    c: Weight(g1) = 1
    c: Equal(g1,g2)
    c: InternalAlignment(g1,g3)
    c: InternalAlignment(g2,g3)
    c: InternalAlignment(g4,g3)
    c: InternalAlignment(g5,g3)
    c: Block(g3)
    c: Coincident(g6,g0)
    c: Coincident(g6,g3)
    c: Horizontal(g6)
FEATURE [Part::Extrusion] Extrude019  label="caseScrewPillarBracket007"
  Base = -> Sketch025
  Dir = (0,0,1)
  DirMode = 2
  FaceMakerClass = Part::FaceMakerBullseye
  LengthFwd = 2.4
  LengthRev = 0
  Placement = pos=(101.3,29,65.23) rot=(0,1,0;1.5708rad)
  Solid = true
  Symmetric = false
FEATURE [Part::Box] Box011  label="frontCaseScrewPillarBracket"
  AttacherType = Attacher::AttachEngine3D
  Height = 2.4
  Length = 16
  Placement = pos=(87,28,2.3) rot=(0,0,1;0rad)
  Width = 7
FEATURE [Part::Box] Box012  label="frontCaseScrewPillarBracket001"
  AttacherType = Attacher::AttachEngine3D
  Height = 2.4
  Length = 16
  Placement = pos=(87,28,67.3) rot=(0,0,1;0rad)
  Width = 7
FEATURE [Sketcher::SketchObject] Sketch026
  FullyConstrained = true
  sketch-geometry (17):
    g0: Circle CenterX=-3.5 CenterY=23.5 CenterZ=0 NormalX=0 NormalY=0 NormalZ=1 AngleXU=0 Radius=1
    g1: Circle CenterX=-1 CenterY=15.25 CenterZ=0 NormalX=0 NormalY=0 NormalZ=1 AngleXU=0 Radius=1
    g2: Circle CenterX=-3.5 CenterY=7 CenterZ=0 NormalX=0 NormalY=0 NormalZ=1 AngleXU=0 Radius=1
    g3: BSplineCurve PolesCount=3 KnotsCount=2 Degree=2 IsPeriodic=0
    g4: GeomPoint X=-3.5 Y=23.5 Z=0
    g5: GeomPoint X=-3.5 Y=7 Z=0
    g6: Circle CenterX=-4.8 CenterY=30.5 CenterZ=0 NormalX=0 NormalY=0 NormalZ=1 AngleXU=0 Radius=1
    g7: Circle CenterX=-3.5 CenterY=30.5 CenterZ=0 NormalX=0 NormalY=0 NormalZ=1 AngleXU=0 Radius=1
    g8: Circle CenterX=-3.5 CenterY=29.2 CenterZ=0 NormalX=0 NormalY=0 NormalZ=1 AngleXU=0 Radius=1
    g9: BSplineCurve PolesCount=3 KnotsCount=2 Degree=2 IsPeriodic=0
    g10: GeomPoint X=-4.8 Y=30.5 Z=0
    g11: GeomPoint X=-3.5 Y=29.2 Z=0
    g12: LineSegment StartX=-3.5 StartY=29.2 StartZ=0 EndX=-3.5 EndY=23.5 EndZ=0
    g13: LineSegment StartX=-4.8 StartY=30.5 StartZ=0 EndX=0 EndY=30.5 EndZ=0
    g14: LineSegment StartX=-3.5 StartY=5 StartZ=0 EndX=-3.5 EndY=7 EndZ=0
    g15: LineSegment StartX=0 StartY=5 StartZ=0 EndX=0 EndY=30.5 EndZ=0
    g16: LineSegment StartX=-3.5 StartY=5 StartZ=0 EndX=0 EndY=5 EndZ=0
  constraints (33):
    c: Weight(g0) = 1
    c: Equal(g0,g1)
    c: Equal(g0,g2)
    c: InternalAlignment(g0,g3)
    c: InternalAlignment(g1,g3)
    c: InternalAlignment(g2,g3)
    c: InternalAlignment(g4,g3)
    c: InternalAlignment(g5,g3)
    c: Block(g3)
    c: Weight(g6) = 1
    c: Equal(g6,g7)
    c: Equal(g6,g8)
    c: InternalAlignment(g6,g9)
    c: InternalAlignment(g7,g9)
    c: InternalAlignment(g8,g9)
    c: InternalAlignment(g10,g9)
    c: InternalAlignment(g11,g9)
    c: Block(g9)
    c: Coincident(g12,g9)
    c: Coincident(g12,g3)
    c: Vertical(g12)
    c: Coincident(g13,g9)
    c: Horizontal(g13)
    c: Distance(g13) = 4.8
    c: Coincident(g14,g3)
    c: Vertical(g14)
    c: Coincident(g15,g13)
    c: Vertical(g15)
    c: Tangent(g15,g1)
    c: Distance(g14) = 2
    c: Coincident(g16,g14)
    c: Horizontal(g16)
    c: Coincident(g15,g16)
FEATURE [Part::Feature] Face050
  shape: bbox 4.8 x 25.5 x 2e-07 mm, 1 faces, 0 solids (baked)
FEATURE [Part::Revolution] Revolve054  label="moreFrontCaseScrewPost001"
  Angle = 360
  Axis = (0,1,0)
  Base = (0,0,0)
  FaceMakerClass = Part::FaceMakerBullseye
  Placement = pos=(102.5,4.5,3.5) rot=(0,0,1;0rad)
  Solid = false
  Source = -> Face050
  Symmetric = false
FEATURE [Part::Feature] Face051
  shape: bbox 4.8 x 25.5 x 2e-07 mm, 1 faces, 0 solids (baked)
FEATURE [Part::Revolution] Revolve055  label="moreFrontCaseScrewPost002"
  Angle = 360
  Axis = (0,1,0)
  Base = (0,0,0)
  FaceMakerClass = Part::FaceMakerBullseye
  Placement = pos=(102.5,4.5,68.5) rot=(0,0,1;0rad)
  Solid = false
  Source = -> Face051
  Symmetric = false
FEATURE [Sketcher::SketchObject] Sketch027
  FullyConstrained = true
  sketch-geometry (10):
    g0: LineSegment StartX=-1.6 StartY=4.7 StartZ=0 EndX=-1.6 EndY=1.7 EndZ=0
    g1: LineSegment StartX=-3.5 StartY=4.7 StartZ=0 EndX=-1.6 EndY=4.7 EndZ=0
    g2: LineSegment StartX=-1.6 StartY=1.7 StartZ=0 EndX=-1.6 EndY=1.5 EndZ=0
    g3: LineSegment StartX=-1.6 StartY=1.5 StartZ=0 EndX=-5.2 EndY=1.5 EndZ=0
    g4: Circle CenterX=-3.5 CenterY=4.7 CenterZ=0 NormalX=0 NormalY=0 NormalZ=1 AngleXU=0 Radius=1
    g5: Circle CenterX=-3.59627 CenterY=2.99743 CenterZ=0 NormalX=0 NormalY=0 NormalZ=1 AngleXU=0 Radius=1
    g6: Circle CenterX=-5.2 CenterY=1.5 CenterZ=0 NormalX=0 NormalY=0 NormalZ=1 AngleXU=0 Radius=1
    g7: BSplineCurve PolesCount=3 KnotsCount=2 Degree=2 IsPeriodic=0
    g8: GeomPoint X=-3.5 Y=4.7 Z=0
    g9: GeomPoint X=-5.2 Y=1.5 Z=0
  constraints (23):
    c: Vertical(g0)
    c: Distance(g0) = 3
    c: Coincident(g1,g0)
    c: Horizontal(g1)
    c: Block(g0)
    c: Block(g1)
    c: Coincident(g2,g0)
    c: Vertical(g2)
    c: Distance(g2) = 0.2
    c: Coincident(g3,g2)
    c: Horizontal(g3)
    c: Block(g3)
    c: Coincident(g7,g1)
    c: Weight(g4) = 1
    c: Equal(g4,g5)
    c: Equal(g4,g6)
    c: Coincident(g7,g3)
    c: InternalAlignment(g4,g7)
    c: InternalAlignment(g5,g7)
    c: InternalAlignment(g6,g7)
    c: InternalAlignment(g8,g7)
    c: InternalAlignment(g9,g7)
    c: Block(g7)
FEATURE [Sketcher::SketchObject] Sketch028
  FullyConstrained = true
  sketch-geometry (18):
    g0: LineSegment StartX=0 StartY=3e-16 StartZ=0 EndX=0 EndY=1.7 EndZ=0
    g1: LineSegment StartX=-3.5 StartY=0 StartZ=0 EndX=-3.5 EndY=0.9 EndZ=0
    g2: Circle CenterX=-2.7 CenterY=1.7 CenterZ=0 NormalX=0 NormalY=0 NormalZ=1 AngleXU=0 Radius=1
    g3: Circle CenterX=-3.5 CenterY=1.7 CenterZ=0 NormalX=0 NormalY=0 NormalZ=1 AngleXU=0 Radius=1
    g4: Circle CenterX=-3.5 CenterY=0.9 CenterZ=0 NormalX=0 NormalY=0 NormalZ=1 AngleXU=0 Radius=1
    g5: BSplineCurve PolesCount=3 KnotsCount=2 Degree=2 IsPeriodic=0
    g6: GeomPoint X=-2.7 Y=1.7 Z=0
    g7: GeomPoint X=-3.5 Y=0.9 Z=0
    g8: LineSegment StartX=-3.5 StartY=0 StartZ=0 EndX=-3.5 EndY=-7 EndZ=0
    g9: LineSegment StartX=0 StartY=3e-16 StartZ=0 EndX=0 EndY=-7 EndZ=0
    g10: LineSegment StartX=-3.5 StartY=-7 StartZ=0 EndX=0 EndY=-7 EndZ=0
    g11: LineSegment StartX=-2.7 StartY=1.7 StartZ=0 EndX=-1.6 EndY=1.7 EndZ=0
    g12: LineSegment StartX=0 StartY=1.7 StartZ=0 EndX=0 EndY=4.5 EndZ=0
    g13: LineSegment StartX=0 StartY=4.5 StartZ=0 EndX=0 EndY=10.8 EndZ=0
    g14: LineSegment StartX=0 StartY=10.8 StartZ=0 EndX=-2 EndY=10.8 EndZ=0
    g15: LineSegment StartX=-1.6 StartY=4.7 StartZ=0 EndX=-1.6 EndY=1.7 EndZ=0
    g16: LineSegment StartX=-1.6 StartY=4.7 StartZ=0 EndX=-2 EndY=4.7 EndZ=0
    g17: LineSegment StartX=-2 StartY=4.7 StartZ=0 EndX=-2 EndY=10.8 EndZ=0
  constraints (44):
    c: Vertical(g0)
    c: Vertical(g1)
    c: Distance(g1) = 0.9
    c: Block(g0)
    c: Distance(g0) = 1.7
    c: Weight(g2) = 1
    c: Equal(g2,g3)
    c: Equal(g2,g4)
    c: Coincident(g5,g1)
    c: InternalAlignment(g2,g5)
    c: InternalAlignment(g3,g5)
    c: InternalAlignment(g4,g5)
    c: InternalAlignment(g6,g5)
    c: InternalAlignment(g7,g5)
    c: Block(g5)
    c: Coincident(g8,g1)
    c: Vertical(g8)
    c: Distance(g8) = 7
    c: Vertical(g9)
    c: Equal(g8,g9) = 7
    c: Coincident(g9,g0)
    c: Coincident(g10,g8)
    c: Coincident(g10,g9)
    c: Horizontal(g10)
    c: Coincident(g11,g5)
    c: Horizontal(g11)
    c: Coincident(g12,g0)
    c: Vertical(g12)
    c: Distance(g12) = 2.8
    c: Coincident(g13,g12)
    c: Vertical(g13)
    c: Distance(g13) = 6.3
    c: Coincident(g14,g13)
    c: Horizontal(g14)
    c: Distance(g14) = 2
    c: Vertical(g15)
    c: Distance(g15) = 3
    c: Block(g11)
    c: Coincident(g15,g11)
    c: Coincident(g16,g15)
    c: Horizontal(g16)
    c: Coincident(g17,g16)
    c: Coincident(g17,g14)
    c: Vertical(g17)
FEATURE [Part::Revolution] Revolve040  label="backCaseScrewRetainer001"
  Angle = 360
  Axis = (0,1,0)
  Base = (0,0,0)
  FaceMakerClass = Part::FaceMakerBullseye
  Placement = pos=(12.5,3,10) rot=(0,0,1;0rad)
  Solid = false
  Source = -> Face036
  Symmetric = false
FEATURE [Part::Feature] Face055
  shape: bbox 3.5 x 30.2 x 2e-07 mm, 1 faces, 0 solids (baked)
FEATURE [Part::Revolution] Revolve059  label="backCaseScrewPost"
  Angle = 360
  Axis = (0,1,0)
  Base = (0,0,0)
  FaceMakerClass = Part::FaceMakerBullseye
  Placement = pos=(12.5,4.5,10) rot=(0,0,1;0rad)
  Solid = false
  Source = -> Face055
  Symmetric = false
FEATURE [Part::Feature] Face056
  shape: bbox 3.5 x 30.2 x 2e-07 mm, 1 faces, 0 solids (baked)
FEATURE [Part::Revolution] Revolve060  label="backCaseScrewPost001"
  Angle = 360
  Axis = (0,1,0)
  Base = (0,0,0)
  FaceMakerClass = Part::FaceMakerBullseye
  Placement = pos=(12.5,4.5,62) rot=(0,0,1;0rad)
  Solid = false
  Source = -> Face056
  Symmetric = false
FEATURE [Part::Feature] Face057
  shape: bbox 3.5 x 17.8 x 2e-07 mm, 1 faces, 0 solids (baked)
FEATURE [Part::Revolution] Revolve061  label="removeToCreateScrewAndThreadedInsertHole"
  Angle = 360
  Axis = (0,1,0)
  Base = (0,0,0)
  FaceMakerClass = Part::FaceMakerBullseye
  Placement = pos=(12.5,0,10) rot=(0,0,1;0rad)
  Solid = false
  Source = -> Face057
  Symmetric = false
FEATURE [Part::Feature] Face058
  shape: bbox 3.5 x 17.8 x 2e-07 mm, 1 faces, 0 solids (baked)
FEATURE [Part::Revolution] Revolve062  label="removeToCreateScrewAndThreadedInsertHole001"
  Angle = 360
  Axis = (0,1,0)
  Base = (0,0,0)
  FaceMakerClass = Part::FaceMakerBullseye
  Placement = pos=(12.5,0,62) rot=(0,0,1;0rad)
  Solid = false
  Source = -> Face058
  Symmetric = false
FEATURE [Part::Feature] Face059
  shape: bbox 3.5 x 17.8 x 2e-07 mm, 1 faces, 0 solids (baked)
FEATURE [Part::Revolution] Revolve063  label="removeToCreateScrewAndThreadedInsertHole002"
  Angle = 360
  Axis = (0,1,0)
  Base = (0,0,0)
  FaceMakerClass = Part::FaceMakerBullseye
  Placement = pos=(89.5,0,68.5) rot=(0,0,1;0rad)
  Solid = false
  Source = -> Face059
  Symmetric = false
FEATURE [Part::Feature] Face060
  shape: bbox 3.5 x 17.8 x 2e-07 mm, 1 faces, 0 solids (baked)
FEATURE [Part::Revolution] Revolve064  label="removeToCreateScrewAndThreadedInsertHole003"
  Angle = 360
  Axis = (0,1,0)
  Base = (0,0,0)
  FaceMakerClass = Part::FaceMakerBullseye
  Placement = pos=(89.5,0,3.5) rot=(0,0,1;0rad)
  Solid = false
  Source = -> Face060
  Symmetric = false
FEATURE [Part::Feature] Face061
  shape: bbox 3.5 x 17.8 x 2e-07 mm, 1 faces, 0 solids (baked)
FEATURE [Part::Revolution] Revolve065  label="removeToCreateScrewAndThreadedInsertHole004"
  Angle = 360
  Axis = (0,1,0)
  Base = (0,0,0)
  FaceMakerClass = Part::FaceMakerBullseye
  Placement = pos=(102.5,4.7,3.5) rot=(0,0,1;0rad)
  Solid = false
  Source = -> Face061
  Symmetric = false
FEATURE [Part::Feature] Face062
  shape: bbox 3.5 x 17.8 x 2e-07 mm, 1 faces, 0 solids (baked)
FEATURE [Part::Revolution] Revolve066  label="removeToCreateScrewAndThreadedInsertHole005"
  Angle = 360
  Axis = (0,1,0)
  Base = (0,0,0)
  FaceMakerClass = Part::FaceMakerBullseye
  Placement = pos=(102.5,4.7,68.5) rot=(0,0,1;0rad)
  Solid = false
  Source = -> Face062
  Symmetric = false
FEATURE [Part::MultiFuse] Fusion047  label="makeHoles"
  Shapes = -> [Revolve066,Revolve065,Revolve064,Revolve063,Revolve062,Revolve061]
FEATURE [Part::Feature] Face063
  shape: bbox 3.6 x 3.2 x 2e-07 mm, 1 faces, 0 solids (baked)
FEATURE [Part::Revolution] Revolve067  label="moreFrontCaseScrewRetainer002"
  Angle = 360
  Axis = (0,1,0)
  Base = (0,0,0)
  FaceMakerClass = Part::FaceMakerBullseye
  Placement = pos=(102.5,4.5,68.5) rot=(0,0,1;0rad)
  Solid = false
  Source = -> Face063
  Symmetric = false
FEATURE [Part::Feature] Face064
  shape: bbox 3.6 x 3.2 x 2e-07 mm, 1 faces, 0 solids (baked)
FEATURE [Part::Revolution] Revolve068  label="moreFrontCaseScrewRetainer003"
  Angle = 360
  Axis = (0,1,0)
  Base = (0,0,0)
  FaceMakerClass = Part::FaceMakerBullseye
  Placement = pos=(102.5,4.5,3.5) rot=(0,0,1;0rad)
  Solid = false
  Source = -> Face064
  Symmetric = false
FEATURE [Part::Feature] Face065
  shape: bbox 3.5 x 17.8 x 2e-07 mm, 1 faces, 0 solids (baked)
FEATURE [Part::Revolution] Revolve069  label="removeToCreateScrewAndThreadedInsertHole006"
  Angle = 360
  Axis = (0,1,0)
  Base = (0,0,0)
  FaceMakerClass = Part::FaceMakerBullseye
  Placement = pos=(12.5,0,10) rot=(0,0,1;0rad)
  Solid = false
  Source = -> Face065
  Symmetric = false
FEATURE [Part::Feature] Face066
  shape: bbox 3.5 x 17.8 x 2e-07 mm, 1 faces, 0 solids (baked)
FEATURE [Part::Revolution] Revolve070  label="removeToCreateScrewAndThreadedInsertHole007"
  Angle = 360
  Axis = (0,1,0)
  Base = (0,0,0)
  FaceMakerClass = Part::FaceMakerBullseye
  Placement = pos=(12.5,0,62) rot=(0,0,1;0rad)
  Solid = false
  Source = -> Face066
  Symmetric = false
FEATURE [Part::Feature] Face067
  shape: bbox 3.5 x 17.8 x 2e-07 mm, 1 faces, 0 solids (baked)
FEATURE [Part::Revolution] Revolve071  label="removeToCreateScrewAndThreadedInsertHole008"
  Angle = 360
  Axis = (0,1,0)
  Base = (0,0,0)
  FaceMakerClass = Part::FaceMakerBullseye
  Placement = pos=(89.5,0,68.5) rot=(0,0,1;0rad)
  Solid = false
  Source = -> Face067
  Symmetric = false
FEATURE [Part::Feature] Face068
  shape: bbox 3.5 x 17.8 x 2e-07 mm, 1 faces, 0 solids (baked)
FEATURE [Part::Revolution] Revolve072  label="removeToCreateScrewAndThreadedInsertHole009"
  Angle = 360
  Axis = (0,1,0)
  Base = (0,0,0)
  FaceMakerClass = Part::FaceMakerBullseye
  Placement = pos=(89.5,0,3.5) rot=(0,0,1;0rad)
  Solid = false
  Source = -> Face068
  Symmetric = false
FEATURE [Part::Feature] Face069
  shape: bbox 3.5 x 17.8 x 2e-07 mm, 1 faces, 0 solids (baked)
FEATURE [Part::Feature] Face070
  shape: bbox 3.5 x 17.8 x 2e-07 mm, 1 faces, 0 solids (baked)
FEATURE [Part::Revolution] Revolve073  label="removeToCreateScrewAndThreadedInsertHole010"
  Angle = 360
  Axis = (0,1,0)
  Base = (0,0,0)
  FaceMakerClass = Part::FaceMakerBullseye
  Placement = pos=(102.5,4.7,3.5) rot=(0,0,1;0rad)
  Solid = false
  Source = -> Face069
  Symmetric = false
FEATURE [Part::Revolution] Revolve074  label="removeToCreateScrewAndThreadedInsertHole011"
  Angle = 360
  Axis = (0,1,0)
  Base = (0,0,0)
  FaceMakerClass = Part::FaceMakerBullseye
  Placement = pos=(102.5,4.7,68.5) rot=(0,0,1;0rad)
  Solid = false
  Source = -> Face070
  Symmetric = false
FEATURE [Part::MultiFuse] Fusion048  label="makeHoles001"
  Shapes = -> [Revolve074,Revolve073,Revolve072,Revolve071,Revolve070,Revolve069]
FEATURE [Part::MultiFuse] Fusion049  label="caseScrewRetainers"
  Shapes = -> [Revolve067,Revolve068,Revolve048,Revolve047,Revolve039,Revolve040]
FEATURE [Part::Cut] Cut015  label="caseScrewRetainers001"
  Base = -> Fusion049
  Tool = -> Fusion048
FEATURE [Part::MultiFuse] Fusion050  label="casePillars"
  Shapes = -> [Revolve055,Revolve054,Revolve043,Revolve046,Revolve059,Revolve060]
FEATURE [Part::Feature] Face071 .. Face076  x6 (patterned run collapsed; names and placements below)
  shape: bbox 3.5 x 17.8 x 2e-07 mm, 1 faces, 0 solids (baked)
FEATURE [Part::Revolution] Revolve075  label="removeToCreateScrewAndThreadedInsertHole012"
  Angle = 360
  Axis = (0,1,0)
  Base = (0,0,0)
  FaceMakerClass = Part::FaceMakerBullseye
  Placement = pos=(12.5,0,10) rot=(0,0,1;0rad)
  Solid = false
  Source = -> Face071
  Symmetric = false
FEATURE [Part::Revolution] Revolve076  label="removeToCreateScrewAndThreadedInsertHole013"
  Angle = 360
  Axis = (0,1,0)
  Base = (0,0,0)
  FaceMakerClass = Part::FaceMakerBullseye
  Placement = pos=(12.5,0,62) rot=(0,0,1;0rad)
  Solid = false
  Source = -> Face072
  Symmetric = false
FEATURE [Part::Revolution] Revolve077  label="removeToCreateScrewAndThreadedInsertHole014"
  Angle = 360
  Axis = (0,1,0)
  Base = (0,0,0)
  FaceMakerClass = Part::FaceMakerBullseye
  Placement = pos=(89.5,0,68.5) rot=(0,0,1;0rad)
  Solid = false
  Source = -> Face073
  Symmetric = false
FEATURE [Part::Revolution] Revolve078  label="removeToCreateScrewAndThreadedInsertHole015"
  Angle = 360
  Axis = (0,1,0)
  Base = (0,0,0)
  FaceMakerClass = Part::FaceMakerBullseye
  Placement = pos=(89.5,0,3.5) rot=(0,0,1;0rad)
  Solid = false
  Source = -> Face074
  Symmetric = false
FEATURE [Part::Revolution] Revolve079  label="removeToCreateScrewAndThreadedInsertHole016"
  Angle = 360
  Axis = (0,1,0)
  Base = (0,0,0)
  FaceMakerClass = Part::FaceMakerBullseye
  Placement = pos=(102.5,4.7,3.5) rot=(0,0,1;0rad)
  Solid = false
  Source = -> Face075
  Symmetric = false
FEATURE [Part::Revolution] Revolve080  label="removeToCreateScrewAndThreadedInsertHole017"
  Angle = 360
  Axis = (0,1,0)
  Base = (0,0,0)
  FaceMakerClass = Part::FaceMakerBullseye
  Placement = pos=(102.5,4.7,68.5) rot=(0,0,1;0rad)
  Solid = false
  Source = -> Face076
  Symmetric = false
FEATURE [Part::MultiFuse] Fusion051  label="makeHoles002"
  Shapes = -> [Revolve080,Revolve079,Revolve078,Revolve077,Revolve076,Revolve075]
FEATURE [Part::Cut] Cut016  label="caesPillars"
  Base = -> Fusion050
  Tool = -> Fusion051
FEATURE [Part::Revolution] Revolve009  label="plugHousing016"
  Angle = 360
  Axis = (0,1,0)
  Base = (0,0,0)
  FaceMakerClass = Part::FaceMakerBullseye
  Placement = pos=(0,0,36.15) rot=(0,0,1;0rad)
  Solid = false
  Source = -> Face012
  Symmetric = false
FEATURE [Part::MultiFuse] Fusion014  label="plugHousing023"
  Placement = pos=(0,0,0) rot=(0,0,1;1.5708rad)
  Shapes = -> [Revolve011,Revolve009]
FEATURE [Part::Revolution] Revolve010  label="plugHousing017"
  Angle = 360
  Axis = (0,1,0)
  Base = (0,0,0)
  FaceMakerClass = Part::FaceMakerBullseye
  Placement = pos=(0,0,36.15) rot=(0,0,1;0rad)
  Solid = false
  Source = -> Face014
  Symmetric = false
FEATURE [Part::MultiFuse] Fusion015  label="plugHousing024"
  Placement = pos=(0,0,0) rot=(0,0,1;1.5708rad)
  Shapes = -> [Revolve010,Revolve015]
FEATURE [Part::Revolution] Revolve014  label="plugHousing026"
  Angle = 360
  Axis = (0,1,0)
  Base = (0,0,0)
  FaceMakerClass = Part::FaceMakerBullseye
  Placement = pos=(0,0,36.15) rot=(0,0,1;0rad)
  Solid = false
  Source = -> Face011
  Symmetric = false
FEATURE [Part::Revolution] Revolve013  label="plugHousing025"
  Angle = 360
  Axis = (0,1,0)
  Base = (0,0,0)
  FaceMakerClass = Part::FaceMakerBullseye
  Placement = pos=(0,0,36.15) rot=(0,0,1;0rad)
  Solid = false
  Source = -> Face015
  Symmetric = false
FEATURE [Part::MultiFuse] Fusion016  label="plugHousing028"
  Placement = pos=(0,19,0) rot=(0,0,1;3.14159rad)
  Shapes = -> [Fusion014,Fusion013]
FEATURE [Part::MultiFuse] Fusion011  label="plugHousing018"
  Placement = pos=(0,0,0) rot=(0,0,1;1.5708rad)
  Shapes = -> [Revolve014,Revolve013]
FEATURE [Part::MultiFuse] Fusion012  label="plugHousing019"
  Placement = pos=(0,19,0) rot=(0,0,1;3.14159rad)
  Shapes = -> [Fusion011,Fusion015]
FEATURE [Part::MultiFuse] Fusion017  label="plugHousing029"
  Placement = pos=(122.621,0,-0.15) rot=(0,0,1;0rad)
  Shapes = -> [Fusion016,Fusion012]
FEATURE [Part::MultiFuse] Fusion052  label="casePillarRetainers"
  Shapes = -> [Extrude012,Extrude013,Extrude014,Extrude015,Extrude016,Extrude017,Extrude018,Extrude019,Box011,Box012]
FEATURE [Part::Feature] Face077
  shape: bbox 3.5 x 17.8 x 2e-07 mm, 1 faces, 0 solids (baked)
FEATURE [Part::Revolution] Revolve081  label="removeToCreateScrewAndThreadedInsertHole018"
  Angle = 360
  Axis = (0,1,0)
  Base = (0,0,0)
  FaceMakerClass = Part::FaceMakerBullseye
  Placement = pos=(62.3,30.3,19.7) rot=(0,0,1;0rad)
  Solid = false
  Source = -> Face077
  Symmetric = false
FEATURE [Part::Feature] Face078
  shape: bbox 3.5 x 17.8 x 2e-07 mm, 1 faces, 0 solids (baked)
FEATURE [Part::Revolution] Revolve082  label="removeToCreateScrewAndThreadedInsertHole019"
  Angle = 360
  Axis = (0,1,0)
  Base = (0,0,0)
  FaceMakerClass = Part::FaceMakerBullseye
  Placement = pos=(62.3,30.3,51.7) rot=(0,0,1;0rad)
  Solid = false
  Source = -> Face078
  Symmetric = false
FEATURE [Part::Feature] Face079
  shape: bbox 3.5 x 17.8 x 2e-07 mm, 1 faces, 0 solids (baked)
FEATURE [Part::Revolution] Revolve083  label="removeToCreateScrewAndThreadedInsertHole020"
  Angle = 360
  Axis = (0,1,0)
  Base = (0,0,0)
  FaceMakerClass = Part::FaceMakerBullseye
  Placement = pos=(30.3,30.3,19.7) rot=(0,0,1;0rad)
  Solid = false
  Source = -> Face079
  Symmetric = false
FEATURE [Part::Feature] Face080
  shape: bbox 3.5 x 17.8 x 2e-07 mm, 1 faces, 0 solids (baked)
FEATURE [Part::Revolution] Revolve084  label="removeToCreateScrewAndThreadedInsertHole021"
  Angle = 360
  Axis = (0,1,0)
  Base = (0,0,0)
  FaceMakerClass = Part::FaceMakerBullseye
  Placement = pos=(30.3,30.3,51.7) rot=(0,0,1;0rad)
  Solid = false
  Source = -> Face080
  Symmetric = false
FEATURE [Part::MultiFuse] Fusion053  label="createThreadedInsertHolesForFan"
  Shapes = -> [Revolve081,Revolve082,Revolve083,Revolve084]
FEATURE [Part::Cut] Cut017  label="fanScrewHousing001"
  Base = -> Fusion046
  Tool = -> Fusion053
FEATURE [Part::Feature] Face081
  shape: bbox 3.5 x 17.8 x 2e-07 mm, 1 faces, 0 solids (baked)
FEATURE [Part::Revolution] Revolve085  label="removeToCreateScrewAndThreadedInsertHole022"
  Angle = 360
  Axis = (0,1,0)
  Base = (0,0,0)
  FaceMakerClass = Part::FaceMakerBullseye
  Placement = pos=(62.3,30.3,19.7) rot=(0,0,1;0rad)
  Solid = false
  Source = -> Face081
  Symmetric = false
FEATURE [Part::Feature] Face082
  shape: bbox 3.5 x 17.8 x 2e-07 mm, 1 faces, 0 solids (baked)
FEATURE [Part::Revolution] Revolve086  label="removeToCreateScrewAndThreadedInsertHole023"
  Angle = 360
  Axis = (0,1,0)
  Base = (0,0,0)
  FaceMakerClass = Part::FaceMakerBullseye
  Placement = pos=(62.3,30.3,51.7) rot=(0,0,1;0rad)
  Solid = false
  Source = -> Face082
  Symmetric = false
FEATURE [Part::Feature] Face083
  shape: bbox 3.5 x 17.8 x 2e-07 mm, 1 faces, 0 solids (baked)
FEATURE [Part::Revolution] Revolve087  label="removeToCreateScrewAndThreadedInsertHole024"
  Angle = 360
  Axis = (0,1,0)
  Base = (0,0,0)
  FaceMakerClass = Part::FaceMakerBullseye
  Placement = pos=(30.3,30.3,19.7) rot=(0,0,1;0rad)
  Solid = false
  Source = -> Face083
  Symmetric = false
FEATURE [Part::Feature] Face084
  shape: bbox 3.5 x 17.8 x 2e-07 mm, 1 faces, 0 solids (baked)
FEATURE [Part::Revolution] Revolve088  label="removeToCreateScrewAndThreadedInsertHole025"
  Angle = 360
  Axis = (0,1,0)
  Base = (0,0,0)
  FaceMakerClass = Part::FaceMakerBullseye
  Placement = pos=(30.3,30.3,51.7) rot=(0,0,1;0rad)
  Solid = false
  Source = -> Face084
  Symmetric = false
FEATURE [Part::MultiFuse] Fusion054  label="createThreadedInsertHolesForFan001"
  Shapes = -> [Revolve085,Revolve086,Revolve087,Revolve088]
FEATURE [Part::Cut] Cut018  label="top007"
  Base = -> Fusion040
  Tool = -> Fusion054
FEATURE [Sketcher::SketchObject] Sketch029
  FullyConstrained = false
  Placement = pos=(0,0,0) rot=(1,0,0;1.5708rad)
  sketch-geometry (24):
    g0: ArcOfCircle CenterX=-4 CenterY=-10.5 CenterZ=0 NormalX=0 NormalY=0 NormalZ=1 AngleXU=0 Radius=1.5 StartAngle=6e-16 EndAngle=3.14159
    g1: ArcOfCircle CenterX=-34.2 CenterY=-10.5 CenterZ=0 NormalX=0 NormalY=0 NormalZ=1 AngleXU=0 Radius=1.5 StartAngle=0 EndAngle=3.14159
    g2: ArcOfCircle CenterX=-34.2 CenterY=-27.7 CenterZ=0 NormalX=0 NormalY=0 NormalZ=1 AngleXU=0 Radius=1.5 StartAngle=3.14159 EndAngle=6.28319
    g3: ArcOfCircle CenterX=-4 CenterY=-27.7 CenterZ=0 NormalX=0 NormalY=0 NormalZ=1 AngleXU=0 Radius=1.5 StartAngle=3.1416 EndAngle=6.28319
    g4: ArcOfCircle CenterX=-10 CenterY=-4.3 CenterZ=0 NormalX=0 NormalY=0 NormalZ=1 AngleXU=0 Radius=1.5 StartAngle=2e-16 EndAngle=3.14159
    g5: ArcOfCircle CenterX=-16.1 CenterY=-1.8 CenterZ=0 NormalX=0 NormalY=0 NormalZ=1 AngleXU=0 Radius=1.5 StartAngle=5e-16 EndAngle=3.14159
    g6: ArcOfCircle CenterX=-22.1 CenterY=-1.8 CenterZ=0 NormalX=0 NormalY=0 NormalZ=1 AngleXU=0 Radius=1.5 StartAngle=5e-16 EndAngle=3.14159
    g7: ArcOfCircle CenterX=-28.2 CenterY=-4.3 CenterZ=0 NormalX=0 NormalY=0 NormalZ=1 AngleXU=0 Radius=1.5 StartAngle=2e-16 EndAngle=3.14159
    g8: ArcOfCircle CenterX=-10 CenterY=-33.9 CenterZ=0 NormalX=0 NormalY=0 NormalZ=1 AngleXU=0 Radius=1.5 StartAngle=3.14159 EndAngle=6.28319
    g9: ArcOfCircle CenterX=-16.1 CenterY=-36.4 CenterZ=0 NormalX=0 NormalY=0 NormalZ=1 AngleXU=0 Radius=1.5 StartAngle=3.14159 EndAngle=6.28319
    g10: ArcOfCircle CenterX=-22.1 CenterY=-36.4 CenterZ=0 NormalX=0 NormalY=0 NormalZ=1 AngleXU=0 Radius=1.5 StartAngle=3.14159 EndAngle=6.28319
    g11: ArcOfCircle CenterX=-28.2 CenterY=-33.9 CenterZ=0 NormalX=0 NormalY=0 NormalZ=1 AngleXU=0 Radius=1.5 StartAngle=3.14159 EndAngle=6.28319
    g12: LineSegment StartX=-35.7 StartY=-10.5 StartZ=0 EndX=-35.7 EndY=-27.7 EndZ=0
    g13: LineSegment StartX=-32.7 StartY=-10.5 StartZ=0 EndX=-32.7 EndY=-27.7 EndZ=0
    g14: LineSegment StartX=-29.7 StartY=-33.9 StartZ=0 EndX=-29.7 EndY=-4.3 EndZ=0
    g15: LineSegment StartX=-26.7 StartY=-33.9 StartZ=0 EndX=-26.7 EndY=-4.3 EndZ=0
    g16: LineSegment StartX=-2.5 StartY=-10.5 StartZ=0 EndX=-2.5 EndY=-27.7 EndZ=0
    g17: LineSegment StartX=-8.5 StartY=-4.3 StartZ=0 EndX=-8.5 EndY=-33.9 EndZ=0
    g18: LineSegment StartX=-5.5 StartY=-10.5 StartZ=0 EndX=-5.5 EndY=-27.7 EndZ=0
    g19: LineSegment StartX=-11.5 StartY=-4.3 StartZ=0 EndX=-11.5 EndY=-33.9 EndZ=0
    g20: LineSegment StartX=-14.6 StartY=-1.8 StartZ=0 EndX=-14.6 EndY=-36.4 EndZ=0
    g21: LineSegment StartX=-17.6 StartY=-1.8 StartZ=0 EndX=-17.6 EndY=-36.4 EndZ=0
    g22: LineSegment StartX=-20.6 StartY=-36.4 StartZ=0 EndX=-20.6 EndY=-1.8 EndZ=0
    g23: LineSegment StartX=-23.6 StartY=-1.8 StartZ=0 EndX=-23.6 EndY=-36.4 EndZ=0
  constraints (48):
    c: Block(g0)
    c: Block(g1)
    c: Block(g2)
    c: Block(g3)
    c: Block(g4)
    c: Block(g5)
    c: Block(g6)
    c: Block(g7)
    c: Block(g8)
    c: Block(g9)
    c: Block(g10)
    c: Block(g11)
    c: Coincident(g12,g1)
    c: Coincident(g12,g2)
    c: Vertical(g12)
    c: Coincident(g13,g1)
    c: Coincident(g13,g2)
    c: Vertical(g13)
    c: Coincident(g14,g11)
    c: Coincident(g14,g7)
    c: Vertical(g14)
    c: Coincident(g15,g11)
    c: Coincident(g15,g7)
    c: Vertical(g15)
    c: Coincident(g16,g0)
    c: Coincident(g16,g3)
    c: Vertical(g16)
    c: Coincident(g17,g4)
    c: Coincident(g17,g8)
    c: Vertical(g17)
    c: Coincident(g18,g0)
    c: Coincident(g18,g3)
    c: Vertical(g18)
    c: Coincident(g19,g4)
    c: Coincident(g19,g8)
    c: Vertical(g19)
    c: Coincident(g20,g5)
    c: Coincident(g20,g9)
    c: Vertical(g20)
    c: Coincident(g21,g5)
    c: Coincident(g21,g9)
    c: Vertical(g21)
    c: Coincident(g22,g10)
    c: Coincident(g22,g6)
    c: Vertical(g22)
    c: Coincident(g23,g6)
    c: Coincident(g23,g10)
    c: Vertical(g23)
FEATURE [Part::Extrusion] Extrude020  label="removeToCreateFanGrillHoles"
  Base = -> Sketch029
  Dir = (0,-1,6e-16)
  DirMode = 2
  FaceMakerClass = Part::FaceMakerBullseye
  LengthFwd = 10
  LengthRev = 0
  Placement = pos=(65.4,44,54.82) rot=(0,0,1;0rad)
  Solid = true
  Symmetric = false
FEATURE [Part::MultiFuse] Fusion055  label="top008"
  Shapes = -> [Cut017,Cut018]
FEATURE [Part::Cut] Cut019  label="top009"
  Base = -> Fusion055
  Tool = -> Extrude020
FEATURE [App::MeasureDistance] Distance003  label="Distance: 71.95 mm"
  Distance = 71.9513
  P1 = (117,38,72)
  P2 = (117,38,0.0487319)
FEATURE [Sketcher::SketchObject] Sketch030
  FullyConstrained = true
  Placement = pos=(117,19,0) rot=(0.57735,0.57735,0.57735;2.0944rad)
  sketch-geometry (48):
    g0: LineSegment StartX=-49.19 StartY=69.25 StartZ=0 EndX=-49.19 EndY=66.25 EndZ=0
    g1: LineSegment StartX=-49.19 StartY=63.5 StartZ=0 EndX=-49.19 EndY=60.5 EndZ=0
    g2: LineSegment StartX=-49.19 StartY=57.75 StartZ=0 EndX=-49.19 EndY=54.75 EndZ=0
    g3: LineSegment StartX=-49.19 StartY=52 StartZ=0 EndX=-49.19 EndY=49 EndZ=0
    g4: LineSegment StartX=-49.19 StartY=46.25 StartZ=0 EndX=-49.19 EndY=43.25 EndZ=0
    g5: LineSegment StartX=-49.19 StartY=40.5 StartZ=0 EndX=-49.19 EndY=37.5 EndZ=0
    g6: LineSegment StartX=-49.19 StartY=34.5 StartZ=0 EndX=-49.19 EndY=31.5 EndZ=0
    g7: LineSegment StartX=-49.19 StartY=28.75 StartZ=0 EndX=-49.19 EndY=25.75 EndZ=0
    g8: LineSegment StartX=-49.19 StartY=23 StartZ=0 EndX=-49.19 EndY=20 EndZ=0
    g9: LineSegment StartX=-49.19 StartY=17.25 StartZ=0 EndX=-49.19 EndY=14.25 EndZ=0
    g10: LineSegment StartX=-49.19 StartY=11.5 StartZ=0 EndX=-49.19 EndY=8.5 EndZ=0
    g11: LineSegment StartX=-49.19 StartY=5.75 StartZ=0 EndX=-49.19 EndY=2.75 EndZ=0
    g12: ArcOfCircle CenterX=-1.5 CenterY=67.75 CenterZ=0 NormalX=0 NormalY=0 NormalZ=1 AngleXU=0 Radius=1.5 StartAngle=4.71239 EndAngle=7.85398
    g13: ArcOfCircle CenterX=-1.5 CenterY=62 CenterZ=0 NormalX=0 NormalY=0 NormalZ=1 AngleXU=0 Radius=1.5 StartAngle=4.71239 EndAngle=7.85398
    g14: ArcOfCircle CenterX=-1.5 CenterY=56.25 CenterZ=0 NormalX=0 NormalY=0 NormalZ=1 AngleXU=0 Radius=1.5 StartAngle=4.71239 EndAngle=7.85398
    g15: ArcOfCircle CenterX=-11.49 CenterY=50.5 CenterZ=0 NormalX=0 NormalY=0 NormalZ=1 AngleXU=0 Radius=1.5 StartAngle=4.71239 EndAngle=7.85398
    g16: ArcOfCircle CenterX=-16.28 CenterY=44.75 CenterZ=0 NormalX=0 NormalY=0 NormalZ=1 AngleXU=0 Radius=1.5 StartAngle=4.71239 EndAngle=7.85398
    g17: ArcOfCircle CenterX=-18.2337 CenterY=39 CenterZ=0 NormalX=0 NormalY=0 NormalZ=1 AngleXU=0 Radius=1.5 StartAngle=4.71485 EndAngle=7.85398
    g18: ArcOfCircle CenterX=-16.2837 CenterY=27.25 CenterZ=0 NormalX=0 NormalY=0 NormalZ=1 AngleXU=0 Radius=1.5 StartAngle=4.71485 EndAngle=7.85398
    g19: ArcOfCircle CenterX=-18.2337 CenterY=33 CenterZ=0 NormalX=0 NormalY=0 NormalZ=1 AngleXU=0 Radius=1.5 StartAngle=4.71485 EndAngle=7.85398
    g20: ArcOfCircle CenterX=-11.49 CenterY=21.5 CenterZ=0 NormalX=0 NormalY=0 NormalZ=1 AngleXU=0 Radius=1.5 StartAngle=4.71239 EndAngle=7.85398
    g21: ArcOfCircle CenterX=-1.5 CenterY=4.25 CenterZ=0 NormalX=0 NormalY=0 NormalZ=1 AngleXU=0 Radius=1.5 StartAngle=4.71239 EndAngle=7.85398
    g22: ArcOfCircle CenterX=-1.5 CenterY=10 CenterZ=0 NormalX=0 NormalY=0 NormalZ=1 AngleXU=0 Radius=1.5 StartAngle=4.71239 EndAngle=7.85398
    g23: ArcOfCircle CenterX=-1.5 CenterY=15.75 CenterZ=0 NormalX=0 NormalY=0 NormalZ=1 AngleXU=0 Radius=1.5 StartAngle=4.71239 EndAngle=7.85398
    g24: LineSegment StartX=-49.19 StartY=69.25 StartZ=0 EndX=-1.5 EndY=69.25 EndZ=0
    g25: LineSegment StartX=-49.19 StartY=66.25 StartZ=0 EndX=-1.5 EndY=66.25 EndZ=0
    g26: LineSegment StartX=-49.19 StartY=63.5 StartZ=0 EndX=-1.5 EndY=63.5 EndZ=0
    g27: LineSegment StartX=-49.19 StartY=60.5 StartZ=0 EndX=-1.5 EndY=60.5 EndZ=0
    g28: LineSegment StartX=-49.19 StartY=57.75 StartZ=0 EndX=-1.5 EndY=57.75 EndZ=0
    g29: LineSegment StartX=-49.19 StartY=54.75 StartZ=0 EndX=-1.5 EndY=54.75 EndZ=0
    g30: LineSegment StartX=-49.19 StartY=52 StartZ=0 EndX=-11.49 EndY=52 EndZ=0
    g31: LineSegment StartX=-49.19 StartY=49 StartZ=0 EndX=-11.49 EndY=49 EndZ=0
    g32: LineSegment StartX=-49.19 StartY=46.25 StartZ=0 EndX=-16.28 EndY=46.25 EndZ=0
    g33: LineSegment StartX=-49.19 StartY=43.25 StartZ=0 EndX=-16.28 EndY=43.25 EndZ=0
    g34: LineSegment StartX=-49.19 StartY=40.5 StartZ=0 EndX=-18.2337 EndY=40.5 EndZ=0
    g35: LineSegment StartX=-49.19 StartY=37.5 StartZ=0 EndX=-18.23 EndY=37.5 EndZ=0
    g36: LineSegment StartX=-49.19 StartY=34.5 StartZ=0 EndX=-18.2337 EndY=34.5 EndZ=0
    g37: LineSegment StartX=-49.19 StartY=31.5 StartZ=0 EndX=-18.23 EndY=31.5 EndZ=0
    g38: LineSegment StartX=-49.19 StartY=28.75 StartZ=0 EndX=-16.2837 EndY=28.75 EndZ=0
    g39: LineSegment StartX=-49.19 StartY=25.75 StartZ=0 EndX=-16.28 EndY=25.75 EndZ=0
    g40: LineSegment StartX=-49.19 StartY=23 StartZ=0 EndX=-11.49 EndY=23 EndZ=0
    g41: LineSegment StartX=-49.19 StartY=20 StartZ=0 EndX=-11.49 EndY=20 EndZ=0
    g42: LineSegment StartX=-49.19 StartY=17.25 StartZ=0 EndX=-1.5 EndY=17.25 EndZ=0
    g43: LineSegment StartX=-49.19 StartY=14.25 StartZ=0 EndX=-1.5 EndY=14.25 EndZ=0
    g44: LineSegment StartX=-49.19 StartY=11.5 StartZ=0 EndX=-1.5 EndY=11.5 EndZ=0
    g45: LineSegment StartX=-49.19 StartY=8.5 StartZ=0 EndX=-1.5 EndY=8.5 EndZ=0
    g46: LineSegment StartX=-49.19 StartY=5.75 StartZ=0 EndX=-1.5 EndY=5.75 EndZ=0
    g47: LineSegment StartX=-49.19 StartY=2.75 StartZ=0 EndX=-1.5 EndY=2.75 EndZ=0
  constraints (120):
    c: Vertical(g0)
    c: Distance(g0) = 3
    c: Block(g0)
    c: Vertical(g1)
    c: Distance(g1) = 3
    c: Vertical(g2)
    c: Equal(g0,g2) = 3
    c: Block(g2)
    c: Vertical(g3)
    c: Equal(g1,g3) = 3
    c: Vertical(g4)
    c: Equal(g0,g4) = 3
    c: Block(g4)
    c: Vertical(g5)
    c: Equal(g1,g5) = 3
    c: Vertical(g6)
    c: Equal(g0,g6) = 3
    c: Block(g6)
    c: Vertical(g7)
    c: Equal(g1,g7) = 3
    c: Vertical(g8)
    c: Equal(g0,g8) = 3
    c: Block(g8)
    c: Vertical(g9)
    c: Equal(g1,g9) = 3
    c: Vertical(g10)
    c: Equal(g0,g10) = 3
    c: Block(g10)
    c: Vertical(g11)
    c: Equal(g1,g11) = 3
    c: Block(g12)
    c: Block(g13)
    c: Block(g14)
    c: Block(g15)
    c: Block(g16)
    c: Block(g17)
    c: Block(g18)
    c: Block(g19)
    c: Block(g20)
    c: Block(g21)
    c: Block(g22)
    c: Block(g23)
    c: Block(g11)
    c: Block(g9)
    c: Block(g7)
    c: Block(g5)
    c: Block(g3)
    c: Block(g1)
    c: Coincident(g24,g0)
    c: Coincident(g24,g12)
    c: Horizontal(g24)
    c: Coincident(g25,g0)
    c: Coincident(g25,g12)
    c: Horizontal(g25)
    c: Coincident(g26,g1)
    c: Coincident(g26,g13)
    c: Horizontal(g26)
    c: Coincident(g27,g1)
    c: Coincident(g27,g13)
    c: Horizontal(g27)
    c: Coincident(g28,g2)
    c: Coincident(g28,g14)
    c: Horizontal(g28)
    c: Coincident(g29,g2)
    c: Coincident(g29,g14)
    c: Horizontal(g29)
    c: Coincident(g30,g3)
    c: Coincident(g30,g15)
    c: Horizontal(g30)
    c: Coincident(g31,g3)
    c: Coincident(g31,g15)
    c: Horizontal(g31)
    c: Coincident(g32,g4)
    c: Coincident(g32,g16)
    c: Horizontal(g32)
    c: Coincident(g33,g4)
    c: Coincident(g33,g16)
    c: Horizontal(g33)
    c: Coincident(g34,g5)
    c: Coincident(g34,g17)
    c: Horizontal(g34)
    c: Coincident(g35,g5)
    c: Coincident(g35,g17)
    c: Horizontal(g35)
    c: Coincident(g36,g6)
    c: Coincident(g36,g19)
    c: Horizontal(g36)
    c: Coincident(g37,g6)
    c: Coincident(g37,g19)
    c: Horizontal(g37)
    c: Coincident(g38,g7)
    c: Coincident(g38,g18)
    c: Horizontal(g38)
    c: Coincident(g39,g7)
    c: Coincident(g39,g18)
    c: Horizontal(g39)
    c: Coincident(g40,g8)
    c: Coincident(g40,g20)
    c: Horizontal(g40)
    c: Coincident(g41,g8)
    c: Coincident(g41,g20)
    c: Horizontal(g41)
    c: Coincident(g42,g9)
    c: Coincident(g42,g23)
    c: Horizontal(g42)
    c: Coincident(g43,g9)
    c: Coincident(g43,g23)
    c: Horizontal(g43)
    c: Coincident(g44,g10)
    c: Coincident(g44,g22)
    c: Horizontal(g44)
    c: Coincident(g45,g10)
    c: Coincident(g45,g22)
    c: Horizontal(g45)
    c: Coincident(g46,g11)
    c: Coincident(g46,g21)
    c: Horizontal(g46)
    c: Coincident(g47,g11)
    c: Coincident(g47,g21)
    c: Horizontal(g47)
FEATURE [Sketcher::SketchObject] Sketch031
  FullyConstrained = true
  Placement = pos=(117,19,0) rot=(0.57735,0.57735,0.57735;2.0944rad)
  sketch-geometry (24):
    g0: ArcOfCircle CenterX=-49.19 CenterY=67.75 CenterZ=0 NormalX=0 NormalY=0 NormalZ=1 AngleXU=0 Radius=1.5 StartAngle=1.5708 EndAngle=4.71239
    g1: ArcOfCircle CenterX=-49.19 CenterY=62 CenterZ=0 NormalX=0 NormalY=0 NormalZ=1 AngleXU=0 Radius=1.5 StartAngle=1.5708 EndAngle=4.71239
    g2: ArcOfCircle CenterX=-49.19 CenterY=56.25 CenterZ=0 NormalX=0 NormalY=0 NormalZ=1 AngleXU=0 Radius=1.5 StartAngle=1.5708 EndAngle=4.71239
    g3: ArcOfCircle CenterX=-49.19 CenterY=50.5 CenterZ=0 NormalX=0 NormalY=0 NormalZ=1 AngleXU=0 Radius=1.5 StartAngle=1.5708 EndAngle=4.71239
    g4: ArcOfCircle CenterX=-49.19 CenterY=44.75 CenterZ=0 NormalX=0 NormalY=0 NormalZ=1 AngleXU=0 Radius=1.5 StartAngle=1.5708 EndAngle=4.71239
    g5: ArcOfCircle CenterX=-49.19 CenterY=39 CenterZ=0 NormalX=0 NormalY=0 NormalZ=1 AngleXU=0 Radius=1.5 StartAngle=1.5708 EndAngle=4.71239
    g6: ArcOfCircle CenterX=-49.19 CenterY=33 CenterZ=0 NormalX=0 NormalY=0 NormalZ=1 AngleXU=0 Radius=1.5 StartAngle=1.5708 EndAngle=4.71239
    g7: ArcOfCircle CenterX=-49.19 CenterY=27.25 CenterZ=0 NormalX=0 NormalY=0 NormalZ=1 AngleXU=0 Radius=1.5 StartAngle=1.5708 EndAngle=4.71239
    g8: ArcOfCircle CenterX=-49.19 CenterY=21.5 CenterZ=0 NormalX=0 NormalY=0 NormalZ=1 AngleXU=0 Radius=1.5 StartAngle=1.5708 EndAngle=4.71239
    g9: ArcOfCircle CenterX=-49.19 CenterY=15.75 CenterZ=0 NormalX=0 NormalY=0 NormalZ=1 AngleXU=0 Radius=1.5 StartAngle=1.5708 EndAngle=4.71239
    g10: ArcOfCircle CenterX=-49.19 CenterY=10 CenterZ=0 NormalX=0 NormalY=0 NormalZ=1 AngleXU=0 Radius=1.5 StartAngle=1.5708 EndAngle=4.71239
    g11: ArcOfCircle CenterX=-49.19 CenterY=4.25 CenterZ=0 NormalX=0 NormalY=0 NormalZ=1 AngleXU=0 Radius=1.5 StartAngle=1.5708 EndAngle=4.71239
    g12: LineSegment StartX=-49.19 StartY=69.25 StartZ=0 EndX=-49.19 EndY=66.25 EndZ=0
    g13: LineSegment StartX=-49.19 StartY=63.5 StartZ=0 EndX=-49.19 EndY=60.5 EndZ=0
    g14: LineSegment StartX=-49.19 StartY=57.75 StartZ=0 EndX=-49.19 EndY=54.75 EndZ=0
    g15: LineSegment StartX=-49.19 StartY=52 StartZ=0 EndX=-49.19 EndY=49 EndZ=0
    g16: LineSegment StartX=-49.19 StartY=46.25 StartZ=0 EndX=-49.19 EndY=43.25 EndZ=0
    g17: LineSegment StartX=-49.19 StartY=40.5 StartZ=0 EndX=-49.19 EndY=37.5 EndZ=0
    g18: LineSegment StartX=-49.19 StartY=34.5 StartZ=0 EndX=-49.19 EndY=31.5 EndZ=0
    g19: LineSegment StartX=-49.19 StartY=28.75 StartZ=0 EndX=-49.19 EndY=25.75 EndZ=0
    g20: LineSegment StartX=-49.19 StartY=23 StartZ=0 EndX=-49.19 EndY=20 EndZ=0
    g21: LineSegment StartX=-49.19 StartY=17.25 StartZ=0 EndX=-49.19 EndY=14.25 EndZ=0
    g22: LineSegment StartX=-49.19 StartY=11.5 StartZ=0 EndX=-49.19 EndY=8.5 EndZ=0
    g23: LineSegment StartX=-49.19 StartY=5.75 StartZ=0 EndX=-49.19 EndY=2.75 EndZ=0
  constraints (48):
    c: Block(g0)
    c: Block(g1)
    c: Block(g2)
    c: Block(g3)
    c: Block(g4)
    c: Block(g5)
    c: Block(g6)
    c: Block(g7)
    c: Block(g8)
    c: Block(g9)
    c: Block(g10)
    c: Block(g11)
    c: Coincident(g12,g0)
    c: Coincident(g12,g0)
    c: Vertical(g12)
    c: Vertical(g13)
    c: Coincident(g13,g1)
    c: Vertical(g14)
    c: Coincident(g14,g2)
    c: Vertical(g15)
    c: Coincident(g15,g3)
    c: Vertical(g16)
    c: Coincident(g16,g4)
    c: Vertical(g17)
    c: Coincident(g17,g5)
    c: Vertical(g18)
    c: Coincident(g18,g6)
    c: Vertical(g19)
    c: Coincident(g19,g7)
    c: Vertical(g20)
    c: Coincident(g20,g8)
    c: Vertical(g21)
    c: Coincident(g21,g9)
    c: Vertical(g22)
    c: Coincident(g22,g10)
    c: Vertical(g23)
    c: Coincident(g23,g11)
    c: Block(g23)
    c: Block(g22)
    c: Block(g21)
    c: Block(g20)
    c: Block(g13)
    c: Block(g14)
    c: Block(g15)
    c: Block(g16)
    c: Block(g17)
    c: Block(g18)
    c: Block(g19)
FEATURE [Part::Extrusion] Extrude022
  Base = -> Sketch030
  Dir = (1,-2e-16,2e-16)
  DirMode = 2
  FaceMakerClass = Part::FaceMakerBullseye
  LengthFwd = 19
  LengthRev = 0
  Placement = pos=(-19,0,0) rot=(0,0,1;0rad)
  Solid = true
  Symmetric = false
FEATURE [Part::Fillet] Fillet022
  Base = -> Extrude022
  Edges = 24 edges r=1.49: [Edge6,Edge11,Edge18,Edge23,Edge30,Edge35,Edge42,Edge47,Edge54,Edge59,Edge66,Edge71,Edge78,Edge83,Edge90,Edge95,Edge102,Edge107,Edge114,Edge119,Edge126,Edge131,Edge138,Edge143]
FEATURE [Part::Cut] Cut020  label="top010"
  Base = -> Cut019
  Tool = -> Fillet022
FEATURE [Sketcher::SketchObject] Sketch032
  FullyConstrained = true
  Placement = pos=(117,19,0) rot=(0.57735,0.57735,0.57735;2.0944rad)
  sketch-geometry (48):
    g0: LineSegment StartX=-49.19 StartY=69.25 StartZ=0 EndX=-49.19 EndY=66.25 EndZ=0
    g1: LineSegment StartX=-49.19 StartY=63.5 StartZ=0 EndX=-49.19 EndY=60.5 EndZ=0
    g2: LineSegment StartX=-49.19 StartY=57.75 StartZ=0 EndX=-49.19 EndY=54.75 EndZ=0
    g3: LineSegment StartX=-49.19 StartY=52 StartZ=0 EndX=-49.19 EndY=49 EndZ=0
    g4: LineSegment StartX=-49.19 StartY=46.25 StartZ=0 EndX=-49.19 EndY=43.25 EndZ=0
    g5: LineSegment StartX=-49.19 StartY=40.5 StartZ=0 EndX=-49.19 EndY=37.5 EndZ=0
    g6: LineSegment StartX=-49.19 StartY=34.5 StartZ=0 EndX=-49.19 EndY=31.5 EndZ=0
    g7: LineSegment StartX=-49.19 StartY=28.75 StartZ=0 EndX=-49.19 EndY=25.75 EndZ=0
    g8: LineSegment StartX=-49.19 StartY=23 StartZ=0 EndX=-49.19 EndY=20 EndZ=0
    g9: LineSegment StartX=-49.19 StartY=17.25 StartZ=0 EndX=-49.19 EndY=14.25 EndZ=0
    g10: LineSegment StartX=-49.19 StartY=11.5 StartZ=0 EndX=-49.19 EndY=8.5 EndZ=0
    g11: LineSegment StartX=-49.19 StartY=5.75 StartZ=0 EndX=-49.19 EndY=2.75 EndZ=0
    g12: ArcOfCircle CenterX=-1.5 CenterY=67.75 CenterZ=0 NormalX=0 NormalY=0 NormalZ=1 AngleXU=0 Radius=1.5 StartAngle=4.71239 EndAngle=7.85398
    g13: ArcOfCircle CenterX=-1.5 CenterY=62 CenterZ=0 NormalX=0 NormalY=0 NormalZ=1 AngleXU=0 Radius=1.5 StartAngle=4.71239 EndAngle=7.85398
    g14: ArcOfCircle CenterX=-1.5 CenterY=56.25 CenterZ=0 NormalX=0 NormalY=0 NormalZ=1 AngleXU=0 Radius=1.5 StartAngle=4.71239 EndAngle=7.85398
    g15: ArcOfCircle CenterX=-11.49 CenterY=50.5 CenterZ=0 NormalX=0 NormalY=0 NormalZ=1 AngleXU=0 Radius=1.5 StartAngle=4.71239 EndAngle=7.85398
    g16: ArcOfCircle CenterX=-16.28 CenterY=44.75 CenterZ=0 NormalX=0 NormalY=0 NormalZ=1 AngleXU=0 Radius=1.5 StartAngle=4.71239 EndAngle=7.85398
    g17: ArcOfCircle CenterX=-18.2337 CenterY=39 CenterZ=0 NormalX=0 NormalY=0 NormalZ=1 AngleXU=0 Radius=1.5 StartAngle=4.71485 EndAngle=7.85398
    g18: ArcOfCircle CenterX=-16.2837 CenterY=27.25 CenterZ=0 NormalX=0 NormalY=0 NormalZ=1 AngleXU=0 Radius=1.5 StartAngle=4.71485 EndAngle=7.85398
    g19: ArcOfCircle CenterX=-18.2337 CenterY=33 CenterZ=0 NormalX=0 NormalY=0 NormalZ=1 AngleXU=0 Radius=1.5 StartAngle=4.71485 EndAngle=7.85398
    g20: ArcOfCircle CenterX=-11.49 CenterY=21.5 CenterZ=0 NormalX=0 NormalY=0 NormalZ=1 AngleXU=0 Radius=1.5 StartAngle=4.71239 EndAngle=7.85398
    g21: ArcOfCircle CenterX=-1.5 CenterY=4.25 CenterZ=0 NormalX=0 NormalY=0 NormalZ=1 AngleXU=0 Radius=1.5 StartAngle=4.71239 EndAngle=7.85398
    g22: ArcOfCircle CenterX=-1.5 CenterY=10 CenterZ=0 NormalX=0 NormalY=0 NormalZ=1 AngleXU=0 Radius=1.5 StartAngle=4.71239 EndAngle=7.85398
    g23: ArcOfCircle CenterX=-1.5 CenterY=15.75 CenterZ=0 NormalX=0 NormalY=0 NormalZ=1 AngleXU=0 Radius=1.5 StartAngle=4.71239 EndAngle=7.85398
    g24: LineSegment StartX=-49.19 StartY=69.25 StartZ=0 EndX=-1.5 EndY=69.25 EndZ=0
    g25: LineSegment StartX=-49.19 StartY=66.25 StartZ=0 EndX=-1.5 EndY=66.25 EndZ=0
    g26: LineSegment StartX=-49.19 StartY=63.5 StartZ=0 EndX=-1.5 EndY=63.5 EndZ=0
    g27: LineSegment StartX=-49.19 StartY=60.5 StartZ=0 EndX=-1.5 EndY=60.5 EndZ=0
    g28: LineSegment StartX=-49.19 StartY=57.75 StartZ=0 EndX=-1.5 EndY=57.75 EndZ=0
    g29: LineSegment StartX=-49.19 StartY=54.75 StartZ=0 EndX=-1.5 EndY=54.75 EndZ=0
    g30: LineSegment StartX=-49.19 StartY=52 StartZ=0 EndX=-11.49 EndY=52 EndZ=0
    g31: LineSegment StartX=-49.19 StartY=49 StartZ=0 EndX=-11.49 EndY=49 EndZ=0
    g32: LineSegment StartX=-49.19 StartY=46.25 StartZ=0 EndX=-16.28 EndY=46.25 EndZ=0
    g33: LineSegment StartX=-49.19 StartY=43.25 StartZ=0 EndX=-16.28 EndY=43.25 EndZ=0
    g34: LineSegment StartX=-49.19 StartY=40.5 StartZ=0 EndX=-18.2337 EndY=40.5 EndZ=0
    g35: LineSegment StartX=-49.19 StartY=37.5 StartZ=0 EndX=-18.23 EndY=37.5 EndZ=0
    g36: LineSegment StartX=-49.19 StartY=34.5 StartZ=0 EndX=-18.2337 EndY=34.5 EndZ=0
    g37: LineSegment StartX=-49.19 StartY=31.5 StartZ=0 EndX=-18.23 EndY=31.5 EndZ=0
    g38: LineSegment StartX=-49.19 StartY=28.75 StartZ=0 EndX=-16.2837 EndY=28.75 EndZ=0
    g39: LineSegment StartX=-49.19 StartY=25.75 StartZ=0 EndX=-16.28 EndY=25.75 EndZ=0
    g40: LineSegment StartX=-49.19 StartY=23 StartZ=0 EndX=-11.49 EndY=23 EndZ=0
    g41: LineSegment StartX=-49.19 StartY=20 StartZ=0 EndX=-11.49 EndY=20 EndZ=0
    g42: LineSegment StartX=-49.19 StartY=17.25 StartZ=0 EndX=-1.5 EndY=17.25 EndZ=0
    g43: LineSegment StartX=-49.19 StartY=14.25 StartZ=0 EndX=-1.5 EndY=14.25 EndZ=0
    g44: LineSegment StartX=-49.19 StartY=11.5 StartZ=0 EndX=-1.5 EndY=11.5 EndZ=0
    g45: LineSegment StartX=-49.19 StartY=8.5 StartZ=0 EndX=-1.5 EndY=8.5 EndZ=0
    g46: LineSegment StartX=-49.19 StartY=5.75 StartZ=0 EndX=-1.5 EndY=5.75 EndZ=0
    g47: LineSegment StartX=-49.19 StartY=2.75 StartZ=0 EndX=-1.5 EndY=2.75 EndZ=0
  constraints (120):
    c: Vertical(g0)
    c: Distance(g0) = 3
    c: Block(g0)
    c: Vertical(g1)
    c: Distance(g1) = 3
    c: Vertical(g2)
    c: Equal(g0,g2) = 3
    c: Block(g2)
    c: Vertical(g3)
    c: Equal(g1,g3) = 3
    c: Vertical(g4)
    c: Equal(g0,g4) = 3
    c: Block(g4)
    c: Vertical(g5)
    c: Equal(g1,g5) = 3
    c: Vertical(g6)
    c: Equal(g0,g6) = 3
    c: Block(g6)
    c: Vertical(g7)
    c: Equal(g1,g7) = 3
    c: Vertical(g8)
    c: Equal(g0,g8) = 3
    c: Block(g8)
    c: Vertical(g9)
    c: Equal(g1,g9) = 3
    c: Vertical(g10)
    c: Equal(g0,g10) = 3
    c: Block(g10)
    c: Vertical(g11)
    c: Equal(g1,g11) = 3
    c: Block(g12)
    c: Block(g13)
    c: Block(g14)
    c: Block(g15)
    c: Block(g16)
    c: Block(g17)
    c: Block(g18)
    c: Block(g19)
    c: Block(g20)
    c: Block(g21)
    c: Block(g22)
    c: Block(g23)
    c: Block(g11)
    c: Block(g9)
    c: Block(g7)
    c: Block(g5)
    c: Block(g3)
    c: Block(g1)
    c: Coincident(g24,g0)
    c: Coincident(g24,g12)
    c: Horizontal(g24)
    c: Coincident(g25,g0)
    c: Coincident(g25,g12)
    c: Horizontal(g25)
    c: Coincident(g26,g1)
    c: Coincident(g26,g13)
    c: Horizontal(g26)
    c: Coincident(g27,g1)
    c: Coincident(g27,g13)
    c: Horizontal(g27)
    c: Coincident(g28,g2)
    c: Coincident(g28,g14)
    c: Horizontal(g28)
    c: Coincident(g29,g2)
    c: Coincident(g29,g14)
    c: Horizontal(g29)
    c: Coincident(g30,g3)
    c: Coincident(g30,g15)
    c: Horizontal(g30)
    c: Coincident(g31,g3)
    c: Coincident(g31,g15)
    c: Horizontal(g31)
    c: Coincident(g32,g4)
    c: Coincident(g32,g16)
    c: Horizontal(g32)
    c: Coincident(g33,g4)
    c: Coincident(g33,g16)
    c: Horizontal(g33)
    c: Coincident(g34,g5)
    c: Coincident(g34,g17)
    c: Horizontal(g34)
    c: Coincident(g35,g5)
    c: Coincident(g35,g17)
    c: Horizontal(g35)
    c: Coincident(g36,g6)
    c: Coincident(g36,g19)
    c: Horizontal(g36)
    c: Coincident(g37,g6)
    c: Coincident(g37,g19)
    c: Horizontal(g37)
    c: Coincident(g38,g7)
    c: Coincident(g38,g18)
    c: Horizontal(g38)
    c: Coincident(g39,g7)
    c: Coincident(g39,g18)
    c: Horizontal(g39)
    c: Coincident(g40,g8)
    c: Coincident(g40,g20)
    c: Horizontal(g40)
    c: Coincident(g41,g8)
    c: Coincident(g41,g20)
    c: Horizontal(g41)
    c: Coincident(g42,g9)
    c: Coincident(g42,g23)
    c: Horizontal(g42)
    c: Coincident(g43,g9)
    c: Coincident(g43,g23)
    c: Horizontal(g43)
    c: Coincident(g44,g10)
    c: Coincident(g44,g22)
    c: Horizontal(g44)
    c: Coincident(g45,g10)
    c: Coincident(g45,g22)
    c: Horizontal(g45)
    c: Coincident(g46,g11)
    c: Coincident(g46,g21)
    c: Horizontal(g46)
    c: Coincident(g47,g11)
    c: Coincident(g47,g21)
    c: Horizontal(g47)
FEATURE [Part::Extrusion] Extrude023
  Base = -> Sketch032
  Dir = (1,-2e-16,2e-16)
  DirMode = 2
  FaceMakerClass = Part::FaceMakerBullseye
  LengthFwd = 19
  LengthRev = 0
  Placement = pos=(-19,0,0) rot=(0,0,1;0rad)
  Solid = true
  Symmetric = false
FEATURE [Part::Fillet] Fillet023
  Base = -> Extrude023
  Edges = <same value as first occurrence — deduplicated (x6 in doc)>
  Placement = pos=(0,0.05,0) rot=(0,0,1;0rad)
FEATURE [Part::Cut] Cut014  label="bottom003"
  Base = -> Cut007
  Tool = -> Fusion047
FEATURE [Part::Cut] Cut021  label="bottom004"
  Base = -> Cut014
  Tool = -> Fillet023
FEATURE [Sketcher::SketchObject] Sketch033
  FullyConstrained = true
  Placement = pos=(117,19,0) rot=(0.57735,0.57735,0.57735;2.0944rad)
  sketch-geometry (8):
    g0: LineSegment StartX=-49.19 StartY=69.25 StartZ=0 EndX=-49.19 EndY=66.25 EndZ=0
    g1: LineSegment StartX=-49.19 StartY=5.75 StartZ=0 EndX=-49.19 EndY=2.75 EndZ=0
    g2: ArcOfCircle CenterX=-1.5 CenterY=67.75 CenterZ=0 NormalX=0 NormalY=0 NormalZ=1 AngleXU=0 Radius=1.5 StartAngle=4.71239 EndAngle=7.85398
    g3: ArcOfCircle CenterX=-1.5 CenterY=4.25 CenterZ=0 NormalX=0 NormalY=0 NormalZ=1 AngleXU=0 Radius=1.5 StartAngle=4.71239 EndAngle=7.85398
    g4: LineSegment StartX=-49.19 StartY=69.25 StartZ=0 EndX=-1.5 EndY=69.25 EndZ=0
    g5: LineSegment StartX=-49.19 StartY=66.25 StartZ=0 EndX=-1.5 EndY=66.25 EndZ=0
    g6: LineSegment StartX=-49.19 StartY=5.75 StartZ=0 EndX=-1.5 EndY=5.75 EndZ=0
    g7: LineSegment StartX=-49.19 StartY=2.75 StartZ=0 EndX=-1.5 EndY=2.75 EndZ=0
  constraints (19):
    c: Vertical(g0)
    c: Distance(g0) = 3
    c: Block(g0)
    c: Vertical(g1)
    c: Block(g2)
    c: Block(g3)
    c: Block(g1)
    c: Coincident(g4,g0)
    c: Coincident(g4,g2)
    c: Horizontal(g4)
    c: Coincident(g5,g0)
    c: Coincident(g5,g2)
    c: Horizontal(g5)
    c: Coincident(g6,g1)
    c: Coincident(g6,g3)
    c: Horizontal(g6)
    c: Coincident(g7,g1)
    c: Coincident(g7,g3)
    c: Horizontal(g7)
FEATURE [Sketcher::SketchObject] Sketch034
  FullyConstrained = true
  Placement = pos=(117,19,0) rot=(0.57735,0.57735,0.57735;2.0944rad)
  sketch-geometry (8):
    g0: LineSegment StartX=-49.19 StartY=63.5 StartZ=0 EndX=-49.19 EndY=60.5 EndZ=0
    g1: LineSegment StartX=-49.19 StartY=11.5 StartZ=0 EndX=-49.19 EndY=8.5 EndZ=0
    g2: ArcOfCircle CenterX=-1.5 CenterY=62 CenterZ=0 NormalX=0 NormalY=0 NormalZ=1 AngleXU=0 Radius=1.5 StartAngle=4.71239 EndAngle=7.85398
    g3: ArcOfCircle CenterX=-1.5 CenterY=10 CenterZ=0 NormalX=0 NormalY=0 NormalZ=1 AngleXU=0 Radius=1.5 StartAngle=4.71239 EndAngle=7.85398
    g4: LineSegment StartX=-49.19 StartY=63.5 StartZ=0 EndX=-1.5 EndY=63.5 EndZ=0
    g5: LineSegment StartX=-49.19 StartY=60.5 StartZ=0 EndX=-1.5 EndY=60.5 EndZ=0
    g6: LineSegment StartX=-49.19 StartY=11.5 StartZ=0 EndX=-1.5 EndY=11.5 EndZ=0
    g7: LineSegment StartX=-49.19 StartY=8.5 StartZ=0 EndX=-1.5 EndY=8.5 EndZ=0
  constraints (19):
    c: Vertical(g0)
    c: Distance(g0) = 3
    c: Vertical(g1)
    c: Block(g1)
    c: Block(g2)
    c: Block(g3)
    c: Block(g0)
    c: Coincident(g4,g0)
    c: Coincident(g4,g2)
    c: Horizontal(g4)
    c: Coincident(g5,g0)
    c: Coincident(g5,g2)
    c: Horizontal(g5)
    c: Coincident(g6,g1)
    c: Coincident(g6,g3)
    c: Horizontal(g6)
    c: Coincident(g7,g1)
    c: Coincident(g7,g3)
    c: Horizontal(g7)
FEATURE [Part::Extrusion] Extrude024
  Base = -> Sketch033
  Dir = (1,0,0)
  DirMode = 2
  FaceMakerClass = Part::FaceMakerBullseye
  LengthFwd = 10
  LengthRev = 0
  Solid = true
  Symmetric = false
FEATURE [Part::Extrusion] Extrude025
  Base = -> Sketch034
  Dir = (1,0,0)
  DirMode = 2
  FaceMakerClass = Part::FaceMakerBullseye
  LengthFwd = 10
  LengthRev = 0
  Solid = true
  Symmetric = false
FEATURE [Part::Fillet] Fillet024  label="removeFromtMoreFrontCaseScrewRetainers"
  Base = -> Extrude024
  Edges = 4 edges r=1.49: [Edge6,Edge11,Edge18,Edge23]
  Placement = pos=(-11,0,0) rot=(0,0,1;0rad)
FEATURE [Part::Fillet] Fillet025  label="removeFromtMoreFrontCaseScrewRetainers001"
  Base = -> Extrude025
  Edges = 4 edges r=1.49: [Edge6,Edge11,Edge18,Edge23]
  Placement = pos=(-19,0,0) rot=(0,0,1;0rad)
FEATURE [Part::Cut] Cut022
  Base = -> Cut015
  Tool = -> Fillet025
FEATURE [Part::Cut] Cut023  label="screwRetainers"
  Base = -> Cut022
  Tool = -> Fillet024
FEATURE [Part::MultiFuse] Fusion056  label="bottom005"
  Shapes = -> [Fusion044,Cut021]
FEATURE [Part::MultiFuse] Fusion057  label="casePillars001"
  Shapes = -> [Cut016,Fusion052]
FEATURE [Part::MultiFuse] Fusion058  label="bottom006"
  Shapes = -> [Fusion056,Cut023]
FEATURE [Part::MultiFuse] Fusion059  label="bottom007"
  Shapes = -> [Fusion058,Fillet005]
FEATURE [Part::MultiFuse] Fusion060  label="bottom008"
  Shapes = -> [Fusion059,Fusion]
FEATURE [Part::MultiFuse] Fusion061  label="top011"
  Shapes = -> [Cut006,Cut020]
FEATURE [Part::MultiFuse] Fusion062  label="top012"
  Shapes = -> [Fusion057,Fusion061]
FEATURE [Sketcher::SketchObject] Sketch035  label="topSketch007"
  FullyConstrained = true
  sketch-geometry (6):
    g0: LineSegment StartX=19 StartY=38 StartZ=0 EndX=117 EndY=38 EndZ=0
    g1: ArcOfCircle CenterX=19 CenterY=19 CenterZ=0 NormalX=0 NormalY=0 NormalZ=1 AngleXU=0 Radius=19 StartAngle=1.5708 EndAngle=3.14159
    g2: LineSegment StartX=117 StartY=38 StartZ=0 EndX=117 EndY=19 EndZ=0
    g3: LineSegment StartX=98 StartY=1.0161e-12 StartZ=0 EndX=5.22862e-06 EndY=1.0161e-12 EndZ=0
    g4: LineSegment StartX=5.22862e-06 StartY=19 StartZ=0 EndX=5.22862e-06 EndY=1.0161e-12 EndZ=0
    g5: ArcOfCircle CenterX=98 CenterY=19 CenterZ=0 NormalX=0 NormalY=0 NormalZ=1 AngleXU=0 Radius=19 StartAngle=4.71239 EndAngle=6.28319
  constraints (16):
    c: Horizontal(g0)
    c: Distance(g0) = 98
    c: Coincident(g1,g0)
    c: Block(g1)
    c: Coincident(g2,g0)
    c: Vertical(g2)
    c: Distance(g2) = 19
    c: Horizontal(g3)
    c: Coincident(g4,g1)
    c: Vertical(g4)
    c: Coincident(g3,g4)
    c: Block(g3)
    c: Coincident(g5,g2)
    c: Coincident(g5,g3)
    c: Block(g0)
    c: Block(g5)
FEATURE [Part::Extrusion] Extrude026  label="sideA001"
  Base = -> Sketch035
  Dir = (0,0,1)
  DirMode = 2
  FaceMakerClass = Part::FaceMakerBullseye
  LengthFwd = 3
  LengthRev = 0
  Placement = pos=(0,0,-2.7) rot=(0,0,1;0rad)
  Solid = true
  Symmetric = false
FEATURE [Sketcher::SketchObject] Sketch036  label="topSketch008"
  FullyConstrained = true
  sketch-geometry (6):
    g0: LineSegment StartX=19 StartY=38 StartZ=0 EndX=117 EndY=38 EndZ=0
    g1: ArcOfCircle CenterX=19 CenterY=19 CenterZ=0 NormalX=0 NormalY=0 NormalZ=1 AngleXU=0 Radius=19 StartAngle=1.5708 EndAngle=3.14159
    g2: LineSegment StartX=117 StartY=38 StartZ=0 EndX=117 EndY=19 EndZ=0
    g3: LineSegment StartX=98 StartY=1.0161e-12 StartZ=0 EndX=5.22862e-06 EndY=1.0161e-12 EndZ=0
    g4: LineSegment StartX=5.22862e-06 StartY=19 StartZ=0 EndX=5.22862e-06 EndY=1.0161e-12 EndZ=0
    g5: ArcOfCircle CenterX=98 CenterY=19 CenterZ=0 NormalX=0 NormalY=0 NormalZ=1 AngleXU=0 Radius=19 StartAngle=4.71239 EndAngle=6.28319
  constraints (16):
    c: Horizontal(g0)
    c: Distance(g0) = 98
    c: Coincident(g1,g0)
    c: Block(g1)
    c: Coincident(g2,g0)
    c: Vertical(g2)
    c: Distance(g2) = 19
    c: Horizontal(g3)
    c: Coincident(g4,g1)
    c: Vertical(g4)
    c: Coincident(g3,g4)
    c: Block(g3)
    c: Coincident(g5,g2)
    c: Coincident(g5,g3)
    c: Block(g0)
    c: Block(g5)
FEATURE [Part::Extrusion] Extrude027  label="sideB001"
  Base = -> Sketch036
  Dir = (0,0,1)
  DirMode = 2
  FaceMakerClass = Part::FaceMakerBullseye
  LengthFwd = 3
  LengthRev = 0
  Placement = pos=(0,0,71.7) rot=(0,0,1;0rad)
  Solid = true
  Symmetric = false
FEATURE [Part::MultiFuse] Fusion064  label="removeFromBottom"
  Shapes = -> [Extrude026,Extrude027]
FEATURE [Part::Cut] Cut024  label="bottom009"
  Base = -> Fusion060
  Tool = -> Fusion064
FEATURE [Sketcher::SketchObject] Sketch037  label="topSketch009"
  FullyConstrained = true
  sketch-geometry (8):
    g0: ArcOfCircle CenterX=19 CenterY=19.1201 CenterZ=0 NormalX=0 NormalY=0 NormalZ=1 AngleXU=0 Radius=18.8799 StartAngle=1.5708 EndAngle=3.14793
    g1: LineSegment StartX=0.120501 StartY=19.0004 StartZ=0 EndX=0.120501 EndY=0.000382114 EndZ=0
    g2: LineSegment StartX=19 StartY=38 StartZ=0 EndX=124 EndY=38 EndZ=0
    g3: LineSegment StartX=0.120501 StartY=0.000382114 StartZ=0 EndX=105.121 EndY=0.000382114 EndZ=0
    g4: LineSegment StartX=124 StartY=38 StartZ=0 EndX=125.616 EndY=38 EndZ=0
    g5: LineSegment StartX=105.121 StartY=0.000382114 StartZ=0 EndX=106.736 EndY=0.000382114 EndZ=0
    g6: ArcOfCircle CenterX=106.616 CenterY=19 CenterZ=0 NormalX=0 NormalY=0 NormalZ=1 AngleXU=0 Radius=19 StartAngle=4.71873 EndAngle=6.28319
    g7: LineSegment StartX=125.616 StartY=38 StartZ=0 EndX=125.616 EndY=19 EndZ=0
  constraints (21):
    c: Block(g0)
    c: Coincident(g1,g0)
    c: Vertical(g1)
    c: Horizontal(g2)
    c: Distance(g2) = 105
    c: Coincident(g2,g0)
    c: Distance(g1) = 19
    c: Coincident(g3,g1)
    c: Horizontal(g3)
    c: Distance(g3) = 105
    c: Coincident(g4,g2)
    c: Horizontal(g4)
    c: Distance(g4) = 1.61553
    c: Horizontal(g5)
    c: Equal(g4,g5) = 1.61553
    c: Coincident(g5,g3)
    c: Block(g6)
    c: Coincident(g6,g5)
    c: Coincident(g7,g4)
    c: Coincident(g7,g6)
    c: Vertical(g7)
FEATURE [Part::Extrusion] Extrude028  label="sideB"
  Base = -> Sketch037
  Dir = (0,0,1)
  DirMode = 2
  FaceMakerClass = Part::FaceMakerBullseye
  LengthFwd = 3
  LengthRev = 0
  Placement = pos=(0,0,72) rot=(0,0,1;0rad)
  Solid = true
  Symmetric = false
FEATURE [Sketcher::SketchObject] Sketch038  label="topSketch010"
  FullyConstrained = true
  sketch-geometry (22):
    g0: LineSegment StartX=5.21097e-06 StartY=3 StartZ=0 EndX=5.21097e-06 EndY=19 EndZ=0
    g1: ArcOfCircle CenterX=19 CenterY=19 CenterZ=0 NormalX=0 NormalY=0 NormalZ=1 AngleXU=0 Radius=19 StartAngle=1.5708 EndAngle=3.14159
    g2: ArcOfCircle CenterX=19 CenterY=19 CenterZ=0 NormalX=0 NormalY=0 NormalZ=1 AngleXU=0 Radius=16 StartAngle=1.5708 EndAngle=3.14159
    g3: LineSegment StartX=114 StartY=35 StartZ=0 EndX=19 EndY=35 EndZ=0
    g4: LineSegment StartX=5.21097e-06 StartY=3 StartZ=0 EndX=5.21097e-06 EndY=0 EndZ=0
    g5: LineSegment StartX=3 StartY=0 StartZ=0 EndX=5.21097e-06 EndY=0 EndZ=0
    g6: LineSegment StartX=3 StartY=19 StartZ=0 EndX=3 EndY=0 EndZ=0
    g7: LineSegment StartX=19 StartY=38 StartZ=0 EndX=124 EndY=38 EndZ=0
    g8: Circle CenterX=119 CenterY=35 CenterZ=0 NormalX=0 NormalY=0 NormalZ=1 AngleXU=0 Radius=1
    g9: Circle CenterX=121 CenterY=35 CenterZ=0 NormalX=0 NormalY=0 NormalZ=1 AngleXU=0 Radius=1
    g10: Circle CenterX=121 CenterY=33 CenterZ=0 NormalX=0 NormalY=0 NormalZ=1 AngleXU=0 Radius=1
    g11: BSplineCurve PolesCount=3 KnotsCount=2 Degree=2 IsPeriodic=0
    g12: GeomPoint X=119 Y=35 Z=0
    g13: GeomPoint X=121 Y=33 Z=0
    g14: LineSegment StartX=119 StartY=35 StartZ=0 EndX=114 EndY=35 EndZ=0
    g15: ArcOfCircle CenterX=105 CenterY=19 CenterZ=0 NormalX=0 NormalY=0 NormalZ=1 AngleXU=0 Radius=16 StartAngle=5.60905 EndAngle=6.28319
    g16: LineSegment StartX=121 StartY=33 StartZ=0 EndX=121 EndY=19 EndZ=0
    g17: LineSegment StartX=117.5 StartY=9.01251 StartZ=0 EndX=121.163 EndY=9.0125 EndZ=0
    g18: ArcOfCircle CenterX=105 CenterY=19 CenterZ=0 NormalX=0 NormalY=0 NormalZ=1 AngleXU=0 Radius=20.6155 StartAngle=5.7297 EndAngle=6.28319
    g19: LineSegment StartX=121.163 StartY=9.0125 StartZ=0 EndX=122.538 EndY=8.16329 EndZ=0
    g20: LineSegment StartX=124 StartY=38 StartZ=0 EndX=125.616 EndY=38 EndZ=0
    g21: LineSegment StartX=125.616 StartY=19 StartZ=0 EndX=125.616 EndY=38 EndZ=0
  constraints (49):
    c: Vertical(g0)
    c: Block(g0)
    c: Coincident(g1,g0)
    c: Block(g1)
    c: Coincident(g2,g1)
    c: Block(g2)
    c: Coincident(g3,g2)
    c: Horizontal(g3)
    c: Tangent(g3,g2)
    c: Coincident(g4,g0)
    c: Distance(g4) = 3
    c: Vertical(g4)
    c: Coincident(g5,g4)
    c: Horizontal(g5)
    c: Coincident(g6,g2)
    c: Coincident(g6,g5)
    c: Vertical(g6)
    c: Horizontal(g7)
    c: Distance(g7) = 105
    c: Coincident(g7,g1)
    c: Block(g3)
    c: Weight(g8) = 1
    c: Equal(g8,g9)
    c: Equal(g8,g10)
    c: InternalAlignment(g8,g11)
    c: InternalAlignment(g9,g11)
    c: InternalAlignment(g10,g11)
    c: InternalAlignment(g12,g11)
    c: InternalAlignment(g13,g11)
    c: Block(g11)
    c: Coincident(g14,g11)
    c: Coincident(g14,g3)
    c: Horizontal(g14)
    c: Block(g15)
    c: Coincident(g16,g11)
    c: Coincident(g16,g15)
    c: Vertical(g16)
    c: Distance(g16) = 14
    c: Coincident(g17,g15)
    c: Block(g18)
    c: Coincident(g19,g18)
    c: Coincident(g20,g7)
    c: Horizontal(g20)
    c: Vertical(g21)
    c: Coincident(g20,g21)
    c: Block(g20)
    c: Block(g21)
    c: Block(g19)
    c: Block(g17)
FEATURE [Part::Extrusion] Extrude029
  Base = -> Sketch038
  Dir = (0,0,1)
  DirMode = 2
  FaceMakerClass = Part::FaceMakerBullseye
  LengthFwd = 72
  LengthRev = 0
  Solid = true
  Symmetric = false
FEATURE [Part::Feature] Face085
  shape: bbox 4.8 x 25.5 x 2e-07 mm, 1 faces, 0 solids (baked)
FEATURE [Part::Revolution] Revolve089  label="moreFrontCaseScrewPost003"
  Angle = 360
  Axis = (0,1,0)
  Base = (0,0,0)
  FaceMakerClass = Part::FaceMakerBullseye
  Placement = pos=(109.5,4.5,3.5) rot=(0,0,1;0rad)
  Solid = false
  Source = -> Face085
  Symmetric = false
FEATURE [Part::Feature] Face086
  shape: bbox 4.8 x 25.5 x 2e-07 mm, 1 faces, 0 solids (baked)
FEATURE [Part::Revolution] Revolve090  label="moreFrontCaseScrewPost004"
  Angle = 360
  Axis = (0,1,0)
  Base = (0,0,0)
  FaceMakerClass = Part::FaceMakerBullseye
  Placement = pos=(109.5,4.5,68.5) rot=(0,0,1;0rad)
  Solid = false
  Source = -> Face086
  Symmetric = false
FEATURE [Part::Fillet] Fillet026  label="top013"
  Base = -> Extrude029
  Edges = 1 edges r=2: [Edge35]
FEATURE [Sketcher::SketchObject] Sketch039
  FullyConstrained = true
  sketch-geometry (7):
    g0: LineSegment StartX=0 StartY=0 StartZ=0 EndX=0 EndY=6 EndZ=0
    g1: Circle CenterX=0 CenterY=0 CenterZ=0 NormalX=0 NormalY=0 NormalZ=1 AngleXU=0 Radius=1
    g2: Circle CenterX=8 CenterY=6 CenterZ=0 NormalX=0 NormalY=0 NormalZ=1 AngleXU=0 Radius=1
    g3: BSplineCurve PolesCount=3 KnotsCount=2 Degree=2 IsPeriodic=0
    g4: GeomPoint X=0 Y=0 Z=0
    g5: GeomPoint X=8 Y=6 Z=0
    g6: LineSegment StartX=0 StartY=6 StartZ=0 EndX=8 EndY=6 EndZ=0
  constraints (14):
    c: Coincident(g0,g-1)
    c: Distance(g0) = 6
    c: Vertical(g0)
    c: Coincident(g3,g0)
    c: Weight(g1) = 1
    c: Equal(g1,g2)
    c: InternalAlignment(g1,g3)
    c: InternalAlignment(g2,g3)
    c: InternalAlignment(g4,g3)
    c: InternalAlignment(g5,g3)
    c: Block(g3)
    c: Coincident(g6,g0)
    c: Coincident(g6,g3)
    c: Horizontal(g6)
FEATURE [Sketcher::SketchObject] Sketch040
  FullyConstrained = true
  sketch-geometry (7):
    g0: LineSegment StartX=0 StartY=0 StartZ=0 EndX=0 EndY=6 EndZ=0
    g1: Circle CenterX=0 CenterY=0 CenterZ=0 NormalX=0 NormalY=0 NormalZ=1 AngleXU=0 Radius=1
    g2: Circle CenterX=8 CenterY=6 CenterZ=0 NormalX=0 NormalY=0 NormalZ=1 AngleXU=0 Radius=1
    g3: BSplineCurve PolesCount=3 KnotsCount=2 Degree=2 IsPeriodic=0
    g4: GeomPoint X=0 Y=0 Z=0
    g5: GeomPoint X=8 Y=6 Z=0
    g6: LineSegment StartX=0 StartY=6 StartZ=0 EndX=8 EndY=6 EndZ=0
  constraints (14):
    c: Coincident(g0,g-1)
    c: Distance(g0) = 6
    c: Vertical(g0)
    c: Coincident(g3,g0)
    c: Weight(g1) = 1
    c: Equal(g1,g2)
    c: InternalAlignment(g1,g3)
    c: InternalAlignment(g2,g3)
    c: InternalAlignment(g4,g3)
    c: InternalAlignment(g5,g3)
    c: Block(g3)
    c: Coincident(g6,g0)
    c: Coincident(g6,g3)
    c: Horizontal(g6)
FEATURE [Sketcher::SketchObject] Sketch041
  FullyConstrained = true
  sketch-geometry (7):
    g0: LineSegment StartX=0 StartY=0 StartZ=0 EndX=0 EndY=6 EndZ=0
    g1: Circle CenterX=0 CenterY=0 CenterZ=0 NormalX=0 NormalY=0 NormalZ=1 AngleXU=0 Radius=1
    g2: Circle CenterX=8 CenterY=6 CenterZ=0 NormalX=0 NormalY=0 NormalZ=1 AngleXU=0 Radius=1
    g3: BSplineCurve PolesCount=3 KnotsCount=2 Degree=2 IsPeriodic=0
    g4: GeomPoint X=0 Y=0 Z=0
    g5: GeomPoint X=8 Y=6 Z=0
    g6: LineSegment StartX=0 StartY=6 StartZ=0 EndX=8 EndY=6 EndZ=0
  constraints (14):
    c: Coincident(g0,g-1)
    c: Distance(g0) = 6
    c: Vertical(g0)
    c: Coincident(g3,g0)
    c: Weight(g1) = 1
    c: Equal(g1,g2)
    c: InternalAlignment(g1,g3)
    c: InternalAlignment(g2,g3)
    c: InternalAlignment(g4,g3)
    c: InternalAlignment(g5,g3)
    c: Block(g3)
    c: Coincident(g6,g0)
    c: Coincident(g6,g3)
    c: Horizontal(g6)
FEATURE [Sketcher::SketchObject] Sketch042
  FullyConstrained = true
  sketch-geometry (7):
    g0: LineSegment StartX=0 StartY=0 StartZ=0 EndX=0 EndY=6 EndZ=0
    g1: Circle CenterX=0 CenterY=0 CenterZ=0 NormalX=0 NormalY=0 NormalZ=1 AngleXU=0 Radius=1
    g2: Circle CenterX=8 CenterY=6 CenterZ=0 NormalX=0 NormalY=0 NormalZ=1 AngleXU=0 Radius=1
    g3: BSplineCurve PolesCount=3 KnotsCount=2 Degree=2 IsPeriodic=0
    g4: GeomPoint X=0 Y=0 Z=0
    g5: GeomPoint X=8 Y=6 Z=0
    g6: LineSegment StartX=0 StartY=6 StartZ=0 EndX=8 EndY=6 EndZ=0
  constraints (14):
    c: Coincident(g0,g-1)
    c: Distance(g0) = 6
    c: Vertical(g0)
    c: Coincident(g3,g0)
    c: Weight(g1) = 1
    c: Equal(g1,g2)
    c: InternalAlignment(g1,g3)
    c: InternalAlignment(g2,g3)
    c: InternalAlignment(g4,g3)
    c: InternalAlignment(g5,g3)
    c: Block(g3)
    c: Coincident(g6,g0)
    c: Coincident(g6,g3)
    c: Horizontal(g6)
FEATURE [Part::Extrusion] Extrude030  label="caseScrewPillarBracket008"
  Base = -> Sketch039
  Dir = (0,0,1)
  DirMode = 2
  FaceMakerClass = Part::FaceMakerBullseye
  LengthFwd = 2.4
  LengthRev = 0
  Placement = pos=(15.76,29,8.8) rot=(0,1,0;0rad)
  Solid = true
  Symmetric = false
FEATURE [Part::Extrusion] Extrude031  label="caseScrewPillarBracket009"
  Base = -> Sketch040
  Dir = (0,0,1)
  DirMode = 2
  FaceMakerClass = Part::FaceMakerBullseye
  LengthFwd = 2.4
  LengthRev = 0
  Placement = pos=(15.76,29,60.8) rot=(0,0,1;0rad)
  Solid = true
  Symmetric = false
FEATURE [Part::Extrusion] Extrude032  label="caseScrewPillarBracket010"
  Base = -> Sketch041
  Dir = (0,0,1)
  DirMode = 2
  FaceMakerClass = Part::FaceMakerBullseye
  LengthFwd = 2.4
  LengthRev = 0
  Placement = pos=(13.7,29,13.26) rot=(0,-1,0;1.5708rad)
  Solid = true
  Symmetric = false
FEATURE [Part::Extrusion] Extrude033  label="caseScrewPillarBracket011"
  Base = -> Sketch042
  Dir = (0,0,1)
  DirMode = 2
  FaceMakerClass = Part::FaceMakerBullseye
  LengthFwd = 2.4
  LengthRev = 0
  Placement = pos=(11.3,29,58.74) rot=(0,1,0;1.5708rad)
  Solid = true
  Symmetric = false
FEATURE [Sketcher::SketchObject] Sketch043
  FullyConstrained = true
  sketch-geometry (7):
    g0: LineSegment StartX=0 StartY=0 StartZ=0 EndX=0 EndY=6 EndZ=0
    g1: Circle CenterX=0 CenterY=0 CenterZ=0 NormalX=0 NormalY=0 NormalZ=1 AngleXU=0 Radius=1
    g2: Circle CenterX=8 CenterY=6 CenterZ=0 NormalX=0 NormalY=0 NormalZ=1 AngleXU=0 Radius=1
    g3: BSplineCurve PolesCount=3 KnotsCount=2 Degree=2 IsPeriodic=0
    g4: GeomPoint X=0 Y=0 Z=0
    g5: GeomPoint X=8 Y=6 Z=0
    g6: LineSegment StartX=0 StartY=6 StartZ=0 EndX=8 EndY=6 EndZ=0
  constraints (14):
    c: Coincident(g0,g-1)
    c: Distance(g0) = 6
    c: Vertical(g0)
    c: Coincident(g3,g0)
    c: Weight(g1) = 1
    c: Equal(g1,g2)
    c: InternalAlignment(g1,g3)
    c: InternalAlignment(g2,g3)
    c: InternalAlignment(g4,g3)
    c: InternalAlignment(g5,g3)
    c: Block(g3)
    c: Coincident(g6,g0)
    c: Coincident(g6,g3)
    c: Horizontal(g6)
FEATURE [Part::Extrusion] Extrude034  label="caseScrewPillarBracket012"
  Base = -> Sketch043
  Dir = (0,0,1)
  DirMode = 2
  FaceMakerClass = Part::FaceMakerBullseye
  LengthFwd = 2.4
  LengthRev = 0
  Placement = pos=(88.3,29,65.23) rot=(0,1,0;1.5708rad)
  Solid = true
  Symmetric = false
FEATURE [Sketcher::SketchObject] Sketch044
  FullyConstrained = true
  sketch-geometry (7):
    g0: LineSegment StartX=0 StartY=0 StartZ=0 EndX=0 EndY=6 EndZ=0
    g1: Circle CenterX=0 CenterY=0 CenterZ=0 NormalX=0 NormalY=0 NormalZ=1 AngleXU=0 Radius=1
    g2: Circle CenterX=8 CenterY=6 CenterZ=0 NormalX=0 NormalY=0 NormalZ=1 AngleXU=0 Radius=1
    g3: BSplineCurve PolesCount=3 KnotsCount=2 Degree=2 IsPeriodic=0
    g4: GeomPoint X=0 Y=0 Z=0
    g5: GeomPoint X=8 Y=6 Z=0
    g6: LineSegment StartX=0 StartY=6 StartZ=0 EndX=8 EndY=6 EndZ=0
  constraints (14):
    c: Coincident(g0,g-1)
    c: Distance(g0) = 6
    c: Vertical(g0)
    c: Coincident(g3,g0)
    c: Weight(g1) = 1
    c: Equal(g1,g2)
    c: InternalAlignment(g1,g3)
    c: InternalAlignment(g2,g3)
    c: InternalAlignment(g4,g3)
    c: InternalAlignment(g5,g3)
    c: Block(g3)
    c: Coincident(g6,g0)
    c: Coincident(g6,g3)
    c: Horizontal(g6)
FEATURE [Part::Extrusion] Extrude035  label="caseScrewPillarBracket013"
  Base = -> Sketch044
  Dir = (0,0,1)
  DirMode = 2
  FaceMakerClass = Part::FaceMakerBullseye
  LengthFwd = 2.4
  LengthRev = 0
  Placement = pos=(90.7,29,6.77) rot=(0,-1,0;1.5708rad)
  Solid = true
  Symmetric = false
FEATURE [Sketcher::SketchObject] Sketch045
  FullyConstrained = true
  sketch-geometry (7):
    g0: LineSegment StartX=0 StartY=0 StartZ=0 EndX=0 EndY=6 EndZ=0
    g1: Circle CenterX=0 CenterY=0 CenterZ=0 NormalX=0 NormalY=0 NormalZ=1 AngleXU=0 Radius=1
    g2: Circle CenterX=8 CenterY=6 CenterZ=0 NormalX=0 NormalY=0 NormalZ=1 AngleXU=0 Radius=1
    g3: BSplineCurve PolesCount=3 KnotsCount=2 Degree=2 IsPeriodic=0
    g4: GeomPoint X=0 Y=0 Z=0
    g5: GeomPoint X=8 Y=6 Z=0
    g6: LineSegment StartX=0 StartY=6 StartZ=0 EndX=8 EndY=6 EndZ=0
  constraints (14):
    c: Coincident(g0,g-1)
    c: Distance(g0) = 6
    c: Vertical(g0)
    c: Coincident(g3,g0)
    c: Weight(g1) = 1
    c: Equal(g1,g2)
    c: InternalAlignment(g1,g3)
    c: InternalAlignment(g2,g3)
    c: InternalAlignment(g4,g3)
    c: InternalAlignment(g5,g3)
    c: Block(g3)
    c: Coincident(g6,g0)
    c: Coincident(g6,g3)
    c: Horizontal(g6)
FEATURE [Sketcher::SketchObject] Sketch046
  FullyConstrained = true
  sketch-geometry (7):
    g0: LineSegment StartX=0 StartY=0 StartZ=0 EndX=0 EndY=6 EndZ=0
    g1: Circle CenterX=0 CenterY=0 CenterZ=0 NormalX=0 NormalY=0 NormalZ=1 AngleXU=0 Radius=1
    g2: Circle CenterX=8 CenterY=6 CenterZ=0 NormalX=0 NormalY=0 NormalZ=1 AngleXU=0 Radius=1
    g3: BSplineCurve PolesCount=3 KnotsCount=2 Degree=2 IsPeriodic=0
    g4: GeomPoint X=0 Y=0 Z=0
    g5: GeomPoint X=8 Y=6 Z=0
    g6: LineSegment StartX=0 StartY=6 StartZ=0 EndX=8 EndY=6 EndZ=0
  constraints (14):
    c: Coincident(g0,g-1)
    c: Distance(g0) = 6
    c: Vertical(g0)
    c: Coincident(g3,g0)
    c: Weight(g1) = 1
    c: Equal(g1,g2)
    c: InternalAlignment(g1,g3)
    c: InternalAlignment(g2,g3)
    c: InternalAlignment(g4,g3)
    c: InternalAlignment(g5,g3)
    c: Block(g3)
    c: Coincident(g6,g0)
    c: Coincident(g6,g3)
    c: Horizontal(g6)
FEATURE [Part::Extrusion] Extrude036  label="caseScrewPillarBracket014"
  Base = -> Sketch045
  Dir = (0,0,1)
  DirMode = 2
  FaceMakerClass = Part::FaceMakerBullseye
  LengthFwd = 2.4
  LengthRev = 0
  Placement = pos=(110.7,29,6.77) rot=(0,-1,0;1.5708rad)
  Solid = true
  Symmetric = false
FEATURE [Part::Extrusion] Extrude037  label="caseScrewPillarBracket015"
  Base = -> Sketch046
  Dir = (0,0,1)
  DirMode = 2
  FaceMakerClass = Part::FaceMakerBullseye
  LengthFwd = 2.4
  LengthRev = 0
  Placement = pos=(108.3,29,65.23) rot=(0,1,0;1.5708rad)
  Solid = true
  Symmetric = false
FEATURE [Part::Box] Box013  label="frontCaseScrewPillarBracket002"
  AttacherType = Attacher::AttachEngine3D
  Height = 2.4
  Length = 22
  Placement = pos=(87,28,2.3) rot=(0,0,1;0rad)
  Width = 7
FEATURE [Part::Box] Box014  label="frontCaseScrewPillarBracket003"
  AttacherType = Attacher::AttachEngine3D
  Height = 2.4
  Length = 22
  Placement = pos=(87,28,67.3) rot=(0,0,1;0rad)
  Width = 7
FEATURE [Part::Feature] Face087
  shape: bbox 4.8 x 30.2 x 2e-07 mm, 1 faces, 0 solids (baked)
FEATURE [Part::Revolution] Revolve091  label="frontCaseScrewPost004"
  Angle = 360
  Axis = (0,1,0)
  Base = (0,0,0)
  FaceMakerClass = Part::FaceMakerBullseye
  Placement = pos=(89.5,4.5,3.5) rot=(0,0,1;0rad)
  Solid = false
  Source = -> Face087
  Symmetric = false
FEATURE [Part::Feature] Face088
  shape: bbox 4.8 x 30.2 x 2e-07 mm, 1 faces, 0 solids (baked)
FEATURE [Part::Revolution] Revolve092  label="frontCaseScrewPost005"
  Angle = 360
  Axis = (0,1,0)
  Base = (0,0,0)
  FaceMakerClass = Part::FaceMakerBullseye
  Placement = pos=(89.5,4.5,68.5) rot=(0,0,1;0rad)
  Solid = false
  Source = -> Face088
  Symmetric = false
FEATURE [Part::Feature] Face089
  shape: bbox 3.5 x 30.2 x 2e-07 mm, 1 faces, 0 solids (baked)
FEATURE [Part::Revolution] Revolve093  label="backCaseScrewPost002"
  Angle = 360
  Axis = (0,1,0)
  Base = (0,0,0)
  FaceMakerClass = Part::FaceMakerBullseye
  Placement = pos=(12.5,4.5,10) rot=(0,0,1;0rad)
  Solid = false
  Source = -> Face089
  Symmetric = false
FEATURE [Part::Feature] Face090
  shape: bbox 3.5 x 30.2 x 2e-07 mm, 1 faces, 0 solids (baked)
FEATURE [Part::Revolution] Revolve094  label="backCaseScrewPost003"
  Angle = 360
  Axis = (0,1,0)
  Base = (0,0,0)
  FaceMakerClass = Part::FaceMakerBullseye
  Placement = pos=(12.5,4.5,62) rot=(0,0,1;0rad)
  Solid = false
  Source = -> Face090
  Symmetric = false
FEATURE [Part::Box] Box015  label="Cube011"
  AttacherType = Attacher::AttachEngine3D
  Height = 28.8
  Length = 3
  Placement = pos=(107.3,28,21.6) rot=(0,0,1;0rad)
  Width = 7
FEATURE [Part::Box] Box016  label="Cube012"
  AttacherType = Attacher::AttachEngine3D
  Height = 3
  Length = 7.4
  Placement = pos=(107.3,28,18.6) rot=(0,0,1;0rad)
  Width = 7
FEATURE [Part::Box] Box017  label="Cube013"
  AttacherType = Attacher::AttachEngine3D
  Height = 3
  Length = 7.4
  Placement = pos=(107.3,28,50.4) rot=(0,0,1;0rad)
  Width = 7
FEATURE [Part::Cylinder] Cylinder024
  Angle = 360
  AttacherType = Attacher::AttachEngine3D
  Height = 20
  Placement = pos=(0,0,36.15) rot=(0,0,1;0rad)
  Radius = 14.3
FEATURE [Part::Cylinder] Cylinder025
  Angle = 360
  AttacherType = Attacher::AttachEngine3D
  Height = 10
  Placement = pos=(0,0,36.15) rot=(0,0,1;0rad)
  Radius = 4
FEATURE [Part::MultiFuse] Fusion066  label="removeToCreteHoleForPlugHousing009"
  Placement = pos=(70,19,36) rot=(0,1,0;1.5708rad)
  Shapes = -> [Cylinder024,Cylinder025]
FEATURE [Part::MultiFuse] Fusion065  label="plugHousingBracketHolder002"
  Shapes = -> [Box017,Box015,Box016]
FEATURE [Part::Cut] Cut025  label="plugHousingBracketHolder003"
  Base = -> Fusion065
  Placement = pos=(7,0,0) rot=(0,0,1;0rad)
  Tool = -> Fusion066
FEATURE [Sketcher::SketchObject] Sketch047
  FullyConstrained = false
  Placement = pos=(0,0,0) rot=(1,0,0;1.5708rad)
  sketch-geometry (24):
    g0: ArcOfCircle CenterX=-4 CenterY=-10.5 CenterZ=0 NormalX=0 NormalY=0 NormalZ=1 AngleXU=0 Radius=1.5 StartAngle=6e-16 EndAngle=3.14159
    g1: ArcOfCircle CenterX=-34.2 CenterY=-10.5 CenterZ=0 NormalX=0 NormalY=0 NormalZ=1 AngleXU=0 Radius=1.5 StartAngle=0 EndAngle=3.14159
    g2: ArcOfCircle CenterX=-34.2 CenterY=-27.7 CenterZ=0 NormalX=0 NormalY=0 NormalZ=1 AngleXU=0 Radius=1.5 StartAngle=3.14159 EndAngle=6.28319
    g3: ArcOfCircle CenterX=-4 CenterY=-27.7 CenterZ=0 NormalX=0 NormalY=0 NormalZ=1 AngleXU=0 Radius=1.5 StartAngle=3.1416 EndAngle=6.28319
    g4: ArcOfCircle CenterX=-10 CenterY=-4.3 CenterZ=0 NormalX=0 NormalY=0 NormalZ=1 AngleXU=0 Radius=1.5 StartAngle=2e-16 EndAngle=3.14159
    g5: ArcOfCircle CenterX=-16.1 CenterY=-1.8 CenterZ=0 NormalX=0 NormalY=0 NormalZ=1 AngleXU=0 Radius=1.5 StartAngle=5e-16 EndAngle=3.14159
    g6: ArcOfCircle CenterX=-22.1 CenterY=-1.8 CenterZ=0 NormalX=0 NormalY=0 NormalZ=1 AngleXU=0 Radius=1.5 StartAngle=5e-16 EndAngle=3.14159
    g7: ArcOfCircle CenterX=-28.2 CenterY=-4.3 CenterZ=0 NormalX=0 NormalY=0 NormalZ=1 AngleXU=0 Radius=1.5 StartAngle=2e-16 EndAngle=3.14159
    g8: ArcOfCircle CenterX=-10 CenterY=-33.9 CenterZ=0 NormalX=0 NormalY=0 NormalZ=1 AngleXU=0 Radius=1.5 StartAngle=3.14159 EndAngle=6.28319
    g9: ArcOfCircle CenterX=-16.1 CenterY=-36.4 CenterZ=0 NormalX=0 NormalY=0 NormalZ=1 AngleXU=0 Radius=1.5 StartAngle=3.14159 EndAngle=6.28319
    g10: ArcOfCircle CenterX=-22.1 CenterY=-36.4 CenterZ=0 NormalX=0 NormalY=0 NormalZ=1 AngleXU=0 Radius=1.5 StartAngle=3.14159 EndAngle=6.28319
    g11: ArcOfCircle CenterX=-28.2 CenterY=-33.9 CenterZ=0 NormalX=0 NormalY=0 NormalZ=1 AngleXU=0 Radius=1.5 StartAngle=3.14159 EndAngle=6.28319
    g12: LineSegment StartX=-35.7 StartY=-10.5 StartZ=0 EndX=-35.7 EndY=-27.7 EndZ=0
    g13: LineSegment StartX=-32.7 StartY=-10.5 StartZ=0 EndX=-32.7 EndY=-27.7 EndZ=0
    g14: LineSegment StartX=-29.7 StartY=-33.9 StartZ=0 EndX=-29.7 EndY=-4.3 EndZ=0
    g15: LineSegment StartX=-26.7 StartY=-33.9 StartZ=0 EndX=-26.7 EndY=-4.3 EndZ=0
    g16: LineSegment StartX=-2.5 StartY=-10.5 StartZ=0 EndX=-2.5 EndY=-27.7 EndZ=0
    g17: LineSegment StartX=-8.5 StartY=-4.3 StartZ=0 EndX=-8.5 EndY=-33.9 EndZ=0
    g18: LineSegment StartX=-5.5 StartY=-10.5 StartZ=0 EndX=-5.5 EndY=-27.7 EndZ=0
    g19: LineSegment StartX=-11.5 StartY=-4.3 StartZ=0 EndX=-11.5 EndY=-33.9 EndZ=0
    g20: LineSegment StartX=-14.6 StartY=-1.8 StartZ=0 EndX=-14.6 EndY=-36.4 EndZ=0
    g21: LineSegment StartX=-17.6 StartY=-1.8 StartZ=0 EndX=-17.6 EndY=-36.4 EndZ=0
    g22: LineSegment StartX=-20.6 StartY=-36.4 StartZ=0 EndX=-20.6 EndY=-1.8 EndZ=0
    g23: LineSegment StartX=-23.6 StartY=-1.8 StartZ=0 EndX=-23.6 EndY=-36.4 EndZ=0
  constraints (48):
    c: Block(g0)
    c: Block(g1)
    c: Block(g2)
    c: Block(g3)
    c: Block(g4)
    c: Block(g5)
    c: Block(g6)
    c: Block(g7)
    c: Block(g8)
    c: Block(g9)
    c: Block(g10)
    c: Block(g11)
    c: Coincident(g12,g1)
    c: Coincident(g12,g2)
    c: Vertical(g12)
    c: Coincident(g13,g1)
    c: Coincident(g13,g2)
    c: Vertical(g13)
    c: Coincident(g14,g11)
    c: Coincident(g14,g7)
    c: Vertical(g14)
    c: Coincident(g15,g11)
    c: Coincident(g15,g7)
    c: Vertical(g15)
    c: Coincident(g16,g0)
    c: Coincident(g16,g3)
    c: Vertical(g16)
    c: Coincident(g17,g4)
    c: Coincident(g17,g8)
    c: Vertical(g17)
    c: Coincident(g18,g0)
    c: Coincident(g18,g3)
    c: Vertical(g18)
    c: Coincident(g19,g4)
    c: Coincident(g19,g8)
    c: Vertical(g19)
    c: Coincident(g20,g5)
    c: Coincident(g20,g9)
    c: Vertical(g20)
    c: Coincident(g21,g5)
    c: Coincident(g21,g9)
    c: Vertical(g21)
    c: Coincident(g22,g10)
    c: Coincident(g22,g6)
    c: Vertical(g22)
    c: Coincident(g23,g6)
    c: Coincident(g23,g10)
    c: Vertical(g23)
FEATURE [Part::Extrusion] Extrude038  label="removeToCreateFanGrillHoles001"
  Base = -> Sketch047
  Dir = (0,-1,6e-16)
  DirMode = 2
  FaceMakerClass = Part::FaceMakerBullseye
  LengthFwd = 10
  LengthRev = 0
  Placement = pos=(65.4,44,54.82) rot=(0,0,1;0rad)
  Solid = true
  Symmetric = false
FEATURE [Part::Feature] Wire004
  shape: bbox 11 x 5.2 x 2e-07 mm, 0 faces, 0 solids (baked)
FEATURE [Part::Revolution] Revolve095
  Angle = 360
  Axis = (0,1,0)
  Base = (0,0,0)
  FaceMakerClass = Part::FaceMakerBullseye
  Placement = pos=(30.3,38,19.7) rot=(0,0,1;0rad)
  Solid = true
  Source = -> Wire004
  Symmetric = false
FEATURE [Part::Feature] Wire005
  shape: bbox 11 x 5.2 x 2e-07 mm, 0 faces, 0 solids (baked)
FEATURE [Part::Revolution] Revolve096
  Angle = 360
  Axis = (0,1,0)
  Base = (0,0,0)
  FaceMakerClass = Part::FaceMakerBullseye
  Placement = pos=(30.3,38,51.7) rot=(0,0,1;0rad)
  Solid = true
  Source = -> Wire005
  Symmetric = false
FEATURE [Part::Feature] Wire006
  shape: bbox 11 x 5.2 x 2e-07 mm, 0 faces, 0 solids (baked)
FEATURE [Part::Revolution] Revolve097
  Angle = 360
  Axis = (0,1,0)
  Base = (0,0,0)
  FaceMakerClass = Part::FaceMakerBullseye
  Placement = pos=(62.3,38,51.7) rot=(0,0,1;0rad)
  Solid = true
  Source = -> Wire006
  Symmetric = false
FEATURE [Part::Feature] Wire007
  shape: bbox 11 x 5.2 x 2e-07 mm, 0 faces, 0 solids (baked)
FEATURE [Part::Revolution] Revolve098
  Angle = 360
  Axis = (0,1,0)
  Base = (0,0,0)
  FaceMakerClass = Part::FaceMakerBullseye
  Placement = pos=(62.3,38,19.7) rot=(0,0,1;0rad)
  Solid = true
  Source = -> Wire007
  Symmetric = false
FEATURE [Part::MultiFuse] Fusion067  label="fanScrewHousing002"
  Shapes = -> [Revolve098,Revolve097,Revolve096,Revolve095]
FEATURE [Part::Feature] Face091 .. Face094  x4 (patterned run collapsed; names and placements below)
  shape: bbox 3.5 x 17.8 x 2e-07 mm, 1 faces, 0 solids (baked)
FEATURE [Part::Revolution] Revolve099  label="removeToCreateScrewAndThreadedInsertHole026"
  Angle = 360
  Axis = (0,1,0)
  Base = (0,0,0)
  FaceMakerClass = Part::FaceMakerBullseye
  Placement = pos=(62.3,30.3,19.7) rot=(0,0,1;0rad)
  Solid = false
  Source = -> Face091
  Symmetric = false
FEATURE [Part::Revolution] Revolve100  label="removeToCreateScrewAndThreadedInsertHole027"
  Angle = 360
  Axis = (0,1,0)
  Base = (0,0,0)
  FaceMakerClass = Part::FaceMakerBullseye
  Placement = pos=(62.3,30.3,51.7) rot=(0,0,1;0rad)
  Solid = false
  Source = -> Face092
  Symmetric = false
FEATURE [Part::Revolution] Revolve101  label="removeToCreateScrewAndThreadedInsertHole028"
  Angle = 360
  Axis = (0,1,0)
  Base = (0,0,0)
  FaceMakerClass = Part::FaceMakerBullseye
  Placement = pos=(30.3,30.3,19.7) rot=(0,0,1;0rad)
  Solid = false
  Source = -> Face093
  Symmetric = false
FEATURE [Part::Revolution] Revolve102  label="removeToCreateScrewAndThreadedInsertHole029"
  Angle = 360
  Axis = (0,1,0)
  Base = (0,0,0)
  FaceMakerClass = Part::FaceMakerBullseye
  Placement = pos=(30.3,30.3,51.7) rot=(0,0,1;0rad)
  Solid = false
  Source = -> Face094
  Symmetric = false
FEATURE [Part::MultiFuse] Fusion068  label="createThreadedInsertHolesForFan002"
  Shapes = -> [Revolve099,Revolve100,Revolve101,Revolve102]
FEATURE [Part::Cut] Cut026  label="fanScrewHousing003"
  Base = -> Fusion067
  Tool = -> Fusion068
FEATURE [Sketcher::SketchObject] Sketch048
  FullyConstrained = false
  Placement = pos=(0,0,0) rot=(1,0,0;1.5708rad)
  sketch-geometry (24):
    g0: ArcOfCircle CenterX=-4 CenterY=-10.5 CenterZ=0 NormalX=0 NormalY=0 NormalZ=1 AngleXU=0 Radius=1.5 StartAngle=6e-16 EndAngle=3.14159
    g1: ArcOfCircle CenterX=-34.2 CenterY=-10.5 CenterZ=0 NormalX=0 NormalY=0 NormalZ=1 AngleXU=0 Radius=1.5 StartAngle=0 EndAngle=3.14159
    g2: ArcOfCircle CenterX=-34.2 CenterY=-27.7 CenterZ=0 NormalX=0 NormalY=0 NormalZ=1 AngleXU=0 Radius=1.5 StartAngle=3.14159 EndAngle=6.28319
    g3: ArcOfCircle CenterX=-4 CenterY=-27.7 CenterZ=0 NormalX=0 NormalY=0 NormalZ=1 AngleXU=0 Radius=1.5 StartAngle=3.1416 EndAngle=6.28319
    g4: ArcOfCircle CenterX=-10 CenterY=-4.3 CenterZ=0 NormalX=0 NormalY=0 NormalZ=1 AngleXU=0 Radius=1.5 StartAngle=2e-16 EndAngle=3.14159
    g5: ArcOfCircle CenterX=-16.1 CenterY=-1.8 CenterZ=0 NormalX=0 NormalY=0 NormalZ=1 AngleXU=0 Radius=1.5 StartAngle=5e-16 EndAngle=3.14159
    g6: ArcOfCircle CenterX=-22.1 CenterY=-1.8 CenterZ=0 NormalX=0 NormalY=0 NormalZ=1 AngleXU=0 Radius=1.5 StartAngle=5e-16 EndAngle=3.14159
    g7: ArcOfCircle CenterX=-28.2 CenterY=-4.3 CenterZ=0 NormalX=0 NormalY=0 NormalZ=1 AngleXU=0 Radius=1.5 StartAngle=2e-16 EndAngle=3.14159
    g8: ArcOfCircle CenterX=-10 CenterY=-33.9 CenterZ=0 NormalX=0 NormalY=0 NormalZ=1 AngleXU=0 Radius=1.5 StartAngle=3.14159 EndAngle=6.28319
    g9: ArcOfCircle CenterX=-16.1 CenterY=-36.4 CenterZ=0 NormalX=0 NormalY=0 NormalZ=1 AngleXU=0 Radius=1.5 StartAngle=3.14159 EndAngle=6.28319
    g10: ArcOfCircle CenterX=-22.1 CenterY=-36.4 CenterZ=0 NormalX=0 NormalY=0 NormalZ=1 AngleXU=0 Radius=1.5 StartAngle=3.14159 EndAngle=6.28319
    g11: ArcOfCircle CenterX=-28.2 CenterY=-33.9 CenterZ=0 NormalX=0 NormalY=0 NormalZ=1 AngleXU=0 Radius=1.5 StartAngle=3.14159 EndAngle=6.28319
    g12: LineSegment StartX=-35.7 StartY=-10.5 StartZ=0 EndX=-35.7 EndY=-27.7 EndZ=0
    g13: LineSegment StartX=-32.7 StartY=-10.5 StartZ=0 EndX=-32.7 EndY=-27.7 EndZ=0
    g14: LineSegment StartX=-29.7 StartY=-33.9 StartZ=0 EndX=-29.7 EndY=-4.3 EndZ=0
    g15: LineSegment StartX=-26.7 StartY=-33.9 StartZ=0 EndX=-26.7 EndY=-4.3 EndZ=0
    g16: LineSegment StartX=-2.5 StartY=-10.5 StartZ=0 EndX=-2.5 EndY=-27.7 EndZ=0
    g17: LineSegment StartX=-8.5 StartY=-4.3 StartZ=0 EndX=-8.5 EndY=-33.9 EndZ=0
    g18: LineSegment StartX=-5.5 StartY=-10.5 StartZ=0 EndX=-5.5 EndY=-27.7 EndZ=0
    g19: LineSegment StartX=-11.5 StartY=-4.3 StartZ=0 EndX=-11.5 EndY=-33.9 EndZ=0
    g20: LineSegment StartX=-14.6 StartY=-1.8 StartZ=0 EndX=-14.6 EndY=-36.4 EndZ=0
    g21: LineSegment StartX=-17.6 StartY=-1.8 StartZ=0 EndX=-17.6 EndY=-36.4 EndZ=0
    g22: LineSegment StartX=-20.6 StartY=-36.4 StartZ=0 EndX=-20.6 EndY=-1.8 EndZ=0
    g23: LineSegment StartX=-23.6 StartY=-1.8 StartZ=0 EndX=-23.6 EndY=-36.4 EndZ=0
  constraints (48):
    c: Block(g0)
    c: Block(g1)
    c: Block(g2)
    c: Block(g3)
    c: Block(g4)
    c: Block(g5)
    c: Block(g6)
    c: Block(g7)
    c: Block(g8)
    c: Block(g9)
    c: Block(g10)
    c: Block(g11)
    c: Coincident(g12,g1)
    c: Coincident(g12,g2)
    c: Vertical(g12)
    c: Coincident(g13,g1)
    c: Coincident(g13,g2)
    c: Vertical(g13)
    c: Coincident(g14,g11)
    c: Coincident(g14,g7)
    c: Vertical(g14)
    c: Coincident(g15,g11)
    c: Coincident(g15,g7)
    c: Vertical(g15)
    c: Coincident(g16,g0)
    c: Coincident(g16,g3)
    c: Vertical(g16)
    c: Coincident(g17,g4)
    c: Coincident(g17,g8)
    c: Vertical(g17)
    c: Coincident(g18,g0)
    c: Coincident(g18,g3)
    c: Vertical(g18)
    c: Coincident(g19,g4)
    c: Coincident(g19,g8)
    c: Vertical(g19)
    c: Coincident(g20,g5)
    c: Coincident(g20,g9)
    c: Vertical(g20)
    c: Coincident(g21,g5)
    c: Coincident(g21,g9)
    c: Vertical(g21)
    c: Coincident(g22,g10)
    c: Coincident(g22,g6)
    c: Vertical(g22)
    c: Coincident(g23,g6)
    c: Coincident(g23,g10)
    c: Vertical(g23)
FEATURE [Part::Extrusion] Extrude039  label="removeToCreateFanGrillHoles002"
  Base = -> Sketch048
  Dir = (0,-1,6e-16)
  DirMode = 2
  FaceMakerClass = Part::FaceMakerBullseye
  LengthFwd = 10
  LengthRev = 0
  Placement = pos=(65.4,44,54.82) rot=(0,0,1;0rad)
  Solid = true
  Symmetric = false
FEATURE [Part::Cut] Cut027  label="fanScrewHousing004"
  Base = -> Cut026
  Tool = -> Extrude038
FEATURE [Part::Cut] Cut028  label="top014"
  Base = -> Fillet026
  Tool = -> Extrude039
FEATURE [Part::Feature] Face095 .. Face098  x4 (patterned run collapsed; names and placements below)
  shape: bbox 3.5 x 17.8 x 2e-07 mm, 1 faces, 0 solids (baked)
FEATURE [Part::Revolution] Revolve103  label="removeToCreateScrewAndThreadedInsertHole030"
  Angle = 360
  Axis = (0,1,0)
  Base = (0,0,0)
  FaceMakerClass = Part::FaceMakerBullseye
  Placement = pos=(62.3,30.3,19.7) rot=(0,0,1;0rad)
  Solid = false
  Source = -> Face095
  Symmetric = false
FEATURE [Part::Revolution] Revolve104  label="removeToCreateScrewAndThreadedInsertHole031"
  Angle = 360
  Axis = (0,1,0)
  Base = (0,0,0)
  FaceMakerClass = Part::FaceMakerBullseye
  Placement = pos=(62.3,30.3,51.7) rot=(0,0,1;0rad)
  Solid = false
  Source = -> Face096
  Symmetric = false
FEATURE [Part::Revolution] Revolve105  label="removeToCreateScrewAndThreadedInsertHole032"
  Angle = 360
  Axis = (0,1,0)
  Base = (0,0,0)
  FaceMakerClass = Part::FaceMakerBullseye
  Placement = pos=(30.3,30.3,19.7) rot=(0,0,1;0rad)
  Solid = false
  Source = -> Face097
  Symmetric = false
FEATURE [Part::Revolution] Revolve106  label="removeToCreateScrewAndThreadedInsertHole033"
  Angle = 360
  Axis = (0,1,0)
  Base = (0,0,0)
  FaceMakerClass = Part::FaceMakerBullseye
  Placement = pos=(30.3,30.3,51.7) rot=(0,0,1;0rad)
  Solid = false
  Source = -> Face098
  Symmetric = false
FEATURE [Part::MultiFuse] Fusion069  label="createThreadedInsertHolesForFan003"
  Shapes = -> [Revolve103,Revolve104,Revolve105,Revolve106]
FEATURE [Part::Cut] Cut029  label="top015"
  Base = -> Cut028
  Tool = -> Fusion054
FEATURE [Part::Cut] Cut030  label="fanScrewHousing005"
  Base = -> Cut027
  Tool = -> Fusion069
FEATURE [Part::Cylinder] Cylinder026  label="removeToCreteHoleForPlugHousing010"
  Angle = 360
  AttacherType = Attacher::AttachEngine3D
  Height = 20
  Placement = pos=(-2,19,36) rot=(0,1,0;1.5708rad)
  Radius = 14.3
FEATURE [Part::Box] Box018  label="removeToCreteHoleForPlugHousing011"
  AttacherType = Attacher::AttachEngine3D
  Height = 28.6
  Length = 10
  Placement = pos=(-2,0,21.7) rot=(0,0,1;0rad)
  Width = 19
FEATURE [Part::Box] Box019  label="wireHolderBottomCaseBit"
  AttacherType = Attacher::AttachEngine3D
  Height = 28
  Length = 3
  Placement = pos=(0,0,22) rot=(0,0,1;0rad)
  Width = 21
FEATURE [Part::Cylinder] Cylinder027  label="removeToCreteHoleForPlugHousing012"
  Angle = 360
  AttacherType = Attacher::AttachEngine3D
  Height = 20
  Placement = pos=(-2,19,36) rot=(0,1,0;1.5708rad)
  Radius = 14.3
FEATURE [Part::Cut] Cut031  label="wireHolderBottomCaseBit001"
  Base = -> Box019
  Tool = -> Cylinder027
FEATURE [Part::MultiFuse] Fusion070  label="removeToCreteHoleForPlugHousing013"
  Shapes = -> [Box018,Cylinder026]
FEATURE [Part::Cut] Cut032  label="top016"
  Base = -> Cut029
  Tool = -> Fusion070
FEATURE [Part::Cylinder] Cylinder028
  Angle = 360
  AttacherType = Attacher::AttachEngine3D
  Height = 20
  Placement = pos=(0,0,36.15) rot=(0,0,1;0rad)
  Radius = 14.3
FEATURE [Part::Cylinder] Cylinder029
  Angle = 360
  AttacherType = Attacher::AttachEngine3D
  Height = 10
  Placement = pos=(0,0,36.15) rot=(0,0,1;0rad)
  Radius = 4
FEATURE [Part::MultiFuse] Fusion071  label="removeToCreteHoleForPlugHousing014"
  Placement = pos=(70,19,36) rot=(0,1,0;1.5708rad)
  Shapes = -> [Cylinder028,Cylinder029]
FEATURE [Sketcher::SketchObject] Sketch049  label="topSketch011"
  FullyConstrained = true
  sketch-geometry (4):
    g0: ArcOfCircle CenterX=105 CenterY=19 CenterZ=0 NormalX=0 NormalY=0 NormalZ=1 AngleXU=0 Radius=20.6155 StartAngle=5.54125 EndAngle=6.28319
    g1: ArcOfCircle CenterX=105 CenterY=19 CenterZ=0 NormalX=0 NormalY=0 NormalZ=1 AngleXU=0 Radius=13 StartAngle=5.54125 EndAngle=6.28319
    g2: LineSegment StartX=118 StartY=19 StartZ=0 EndX=125.616 EndY=19 EndZ=0
    g3: LineSegment StartX=114.583 StartY=10.2157 StartZ=0 EndX=120.197 EndY=5.06982 EndZ=0
  constraints (7):
    c: Block(g0)
    c: Block(g1)
    c: Coincident(g2,g1)
    c: Coincident(g2,g0)
    c: Horizontal(g2)
    c: Coincident(g3,g1)
    c: Coincident(g3,g0)
FEATURE [Part::Box] Box020  label="removeToCreteHoleForPlugHousing015"
  AttacherType = Attacher::AttachEngine3D
  Height = 28.6
  Length = 20
  Placement = pos=(106.15,0,21.7) rot=(0,0,1;0rad)
  Width = 19
FEATURE [Part::MultiFuse] Fusion072  label="removeToCreteHoleForPlugHousing016"
  Shapes = -> [Box020,Fusion071]
FEATURE [Part::Cut] Cut033  label="removeToCreteHoleForPlugHousing017"
  Base = -> Cut032
  Tool = -> Fusion072
FEATURE [Part::Cylinder] Cylinder030
  Angle = 360
  AttacherType = Attacher::AttachEngine3D
  Height = 20
  Placement = pos=(0,0,36.15) rot=(0,0,1;0rad)
  Radius = 14.3
FEATURE [Part::Cylinder] Cylinder031
  Angle = 360
  AttacherType = Attacher::AttachEngine3D
  Height = 10
  Placement = pos=(0,0,36.15) rot=(0,0,1;0rad)
  Radius = 4
FEATURE [Part::Box] Box021  label="removeToCreteHoleForPlugHousing019"
  AttacherType = Attacher::AttachEngine3D
  Height = 28.6
  Length = 20
  Placement = pos=(106.15,0,21.7) rot=(0,0,1;0rad)
  Width = 19
FEATURE [Part::MultiFuse] Fusion074  label="removeToCreteHoleForPlugHousing020"
  Placement = pos=(70,19,36) rot=(0,1,0;1.5708rad)
  Shapes = -> [Cylinder030,Cylinder031]
FEATURE [Part::MultiFuse] Fusion073  label="removeToCreteHoleForPlugHousing018"
  Placement = pos=(0,0,28.3) rot=(0,0,1;0rad)
  Shapes = -> [Box021,Fusion074]
FEATURE [Part::Cylinder] Cylinder032
  Angle = 360
  AttacherType = Attacher::AttachEngine3D
  Height = 20
  Placement = pos=(0,0,36.15) rot=(0,0,1;0rad)
  Radius = 14.3
FEATURE [Part::Cylinder] Cylinder033
  Angle = 360
  AttacherType = Attacher::AttachEngine3D
  Height = 10
  Placement = pos=(0,0,36.15) rot=(0,0,1;0rad)
  Radius = 4
FEATURE [Part::Box] Box022  label="removeToCreteHoleForPlugHousing021"
  AttacherType = Attacher::AttachEngine3D
  Height = 28.6
  Length = 20
  Placement = pos=(106.15,0,21.7) rot=(0,0,1;0rad)
  Width = 19
FEATURE [Part::MultiFuse] Fusion076  label="removeToCreteHoleForPlugHousing023"
  Placement = pos=(70,19,36) rot=(0,1,0;1.5708rad)
  Shapes = -> [Cylinder032,Cylinder033]
FEATURE [Part::MultiFuse] Fusion075  label="removeToCreteHoleForPlugHousing022"
  Placement = pos=(0,0,-28.3) rot=(0,0,1;0rad)
  Shapes = -> [Box022,Fusion076]
FEATURE [Part::MultiFuse] Fusion077  label="removeToCreatePlugHousingBottomBit"
  Shapes = -> [Fusion075,Fusion073]
FEATURE [Part::Cylinder] Cylinder034
  Angle = 360
  AttacherType = Attacher::AttachEngine3D
  Height = 20
  Placement = pos=(0,0,36.15) rot=(0,0,1;0rad)
  Radius = 14
FEATURE [Part::Cylinder] Cylinder035
  Angle = 360
  AttacherType = Attacher::AttachEngine3D
  Height = 10
  Placement = pos=(0,0,36.15) rot=(0,0,1;0rad)
  Radius = 4
FEATURE [Part::MultiFuse] Fusion078  label="removeToCreteHoleForPlugHousing024"
  Placement = pos=(70,19,36) rot=(0,1,0;1.5708rad)
  Shapes = -> [Cylinder034,Cylinder035]
FEATURE [Part::MultiFuse] Fusion079  label="removeToCreatePlugHousingBottomBit001"
  Shapes = -> [Fusion078,Fusion077]
FEATURE [Part::Extrusion] Extrude040  label="bottomPlugHousingBit"
  Base = -> Sketch049
  Dir = (0,0,1)
  DirMode = 2
  FaceMakerClass = Part::FaceMakerBullseye
  LengthFwd = 72
  LengthRev = 0
  Solid = true
  Symmetric = false
FEATURE [Part::Cut] Cut034  label="bottomPlugHousingBit001"
  Base = -> Extrude040
  Placement = pos=(-0.09,0,0) rot=(0,0,1;0rad)
  Tool = -> Fusion079
FEATURE [Part::Box] Box023  label="Cube014"
  AttacherType = Attacher::AttachEngine3D
  Height = 16
  Length = 8
  Placement = pos=(12.7,31.52,28) rot=(0,0,1;0rad)
  Width = 4
FEATURE [Part::Cylinder] Cylinder036
  Angle = 360
  AttacherType = Attacher::AttachEngine3D
  Height = 10
  Placement = pos=(0,0,36.15) rot=(0,0,1;0rad)
  Radius = 4
FEATURE [Part::Cylinder] Cylinder037
  Angle = 360
  AttacherType = Attacher::AttachEngine3D
  Height = 20
  Placement = pos=(0,0,36.15) rot=(0,0,1;0rad)
  Radius = 8.2
FEATURE [Part::MultiFuse] Fusion080  label="removeToCreteHoleForPlugHousing025"
  Placement = pos=(-42,19,36) rot=(0,1,0;1.5708rad)
  Shapes = -> [Cylinder037,Cylinder036]
FEATURE [Sketcher::SketchObject] Sketch050  label="topSketch012"
  FullyConstrained = true
  sketch-geometry (4):
    g0: LineSegment StartX=16.8446 StartY=31.512 StartZ=0 EndX=16.3251 EndY=34.4666 EndZ=0
    g1: ArcOfCircle CenterX=19 CenterY=19.2524 CenterZ=0 NormalX=0 NormalY=0 NormalZ=1 AngleXU=0 Radius=15.4476 StartAngle=1.74483 EndAngle=2.72717
    g2: ArcOfCircle CenterX=19 CenterY=19.2524 CenterZ=0 NormalX=0 NormalY=0 NormalZ=1 AngleXU=0 Radius=12.4476 StartAngle=1.74483 EndAngle=2.73189
    g3: LineSegment StartX=4.86004 StartY=25.4725 StartZ=0 EndX=7.58253 EndY=24.2107 EndZ=0
  constraints (7):
    c: Block(g0)
    c: Coincident(g1,g0)
    c: Coincident(g2,g0)
    c: Coincident(g3,g1)
    c: Coincident(g3,g2)
    c: Block(g1)
    c: Block(g2)
FEATURE [Part::Extrusion] Extrude041
  Base = -> Sketch050
  Dir = (0,0,1)
  DirMode = 2
  FaceMakerClass = Part::FaceMakerBullseye
  LengthFwd = 10.6
  LengthRev = 0
  Placement = pos=(0,0,31) rot=(0,0,1;0rad)
  Solid = true
  Symmetric = false
FEATURE [Part::Cut] Cut035
  Base = -> Extrude041
  Placement = pos=(0,0,-0.3) rot=(0,0,1;0rad)
  Tool = -> Fusion080
FEATURE [Part::Cut] Cut036
  Base = -> Box023
  Tool = -> Cut035
FEATURE [Part::Fillet] Fillet027
  Base = -> Cut036
  Edges = 1 edges r=0.7: [Edge13]
FEATURE [Part::Fillet] Fillet028
  Base = -> Fillet027
  Edges = 1 edges r=0.7: [Edge13]
FEATURE [Part::Fillet] Fillet029
  Base = -> Fillet028
  Edges = 1 edges r=0.7: [Edge16]
FEATURE [Part::Fillet] Fillet030
  Base = -> Fillet029
  Edges = 1 edges r=0.7: [Edge11]
FEATURE [Part::Fillet] Fillet031
  Base = -> Fillet030
  Edges = 1 edges r=0.7: [Edge10]
FEATURE [Part::Fillet] Fillet032
  Base = -> Fillet031
  Edges = 1 edges r=1.2: [Edge5]
FEATURE [Part::Fillet] Fillet033
  Base = -> Fillet032
  Edges = 1 edges r=1.2: [Edge12]
FEATURE [Part::Fillet] Fillet034  label="wireHousingRetainer"
  Base = -> Fillet033
  Edges = 1 edges r=2: [Edge1]
  Placement = pos=(0.3,0,0) rot=(0,0,1;0rad)
FEATURE [Part::Feature] Face099
  shape: bbox 3.5 x 17.8 x 2e-07 mm, 1 faces, 0 solids (baked)
FEATURE [Part::Revolution] Revolve107  label="removeToCreateScrewAndThreadedInsertHole034"
  Angle = 360
  Axis = (0,1,0)
  Base = (0,0,0)
  FaceMakerClass = Part::FaceMakerBullseye
  Placement = pos=(12.5,0,10) rot=(0,0,1;0rad)
  Solid = false
  Source = -> Face099
  Symmetric = false
FEATURE [Part::Feature] Face100
  shape: bbox 3.5 x 17.8 x 2e-07 mm, 1 faces, 0 solids (baked)
FEATURE [Part::Revolution] Revolve108  label="removeToCreateScrewAndThreadedInsertHole035"
  Angle = 360
  Axis = (0,1,0)
  Base = (0,0,0)
  FaceMakerClass = Part::FaceMakerBullseye
  Placement = pos=(12.5,0,62) rot=(0,0,1;0rad)
  Solid = false
  Source = -> Face100
  Symmetric = false
FEATURE [Part::Feature] Face101
  shape: bbox 3.5 x 17.8 x 2e-07 mm, 1 faces, 0 solids (baked)
FEATURE [Part::Revolution] Revolve109  label="removeToCreateScrewAndThreadedInsertHole036"
  Angle = 360
  Axis = (0,1,0)
  Base = (0,0,0)
  FaceMakerClass = Part::FaceMakerBullseye
  Placement = pos=(89.5,0,68.5) rot=(0,0,1;0rad)
  Solid = false
  Source = -> Face101
  Symmetric = false
FEATURE [Part::Feature] Face102
  shape: bbox 3.5 x 17.8 x 2e-07 mm, 1 faces, 0 solids (baked)
FEATURE [Part::Revolution] Revolve110  label="removeToCreateScrewAndThreadedInsertHole037"
  Angle = 360
  Axis = (0,1,0)
  Base = (0,0,0)
  FaceMakerClass = Part::FaceMakerBullseye
  Placement = pos=(89.5,0,3.5) rot=(0,0,1;0rad)
  Solid = false
  Source = -> Face102
  Symmetric = false
FEATURE [Part::Feature] Face103
  shape: bbox 3.5 x 17.8 x 2e-07 mm, 1 faces, 0 solids (baked)
FEATURE [Part::Revolution] Revolve111  label="removeToCreateScrewAndThreadedInsertHole038"
  Angle = 360
  Axis = (0,1,0)
  Base = (0,0,0)
  FaceMakerClass = Part::FaceMakerBullseye
  Placement = pos=(109.5,4.7,3.5) rot=(0,0,1;0rad)
  Solid = false
  Source = -> Face103
  Symmetric = false
FEATURE [Part::Feature] Face104
  shape: bbox 3.5 x 17.8 x 2e-07 mm, 1 faces, 0 solids (baked)
FEATURE [Part::Revolution] Revolve112  label="removeToCreateScrewAndThreadedInsertHole039"
  Angle = 360
  Axis = (0,1,0)
  Base = (0,0,0)
  FaceMakerClass = Part::FaceMakerBullseye
  Placement = pos=(109.5,4.7,68.5) rot=(0,0,1;0rad)
  Solid = false
  Source = -> Face104
  Symmetric = false
FEATURE [Part::MultiFuse] Fusion081  label="removeToCreateScrewAndThreadedInsertHole040"
  Shapes = -> [Revolve107,Revolve108,Revolve109,Revolve110,Revolve111,Revolve112]
FEATURE [Part::MultiFuse] Fusion082  label="casePillars002"
  Shapes = -> [Revolve094,Revolve092,Revolve090,Revolve089,Revolve091,Revolve093]
FEATURE [Part::Cut] Cut037  label="casePillars003"
  Base = -> Fusion082
  Tool = -> Fusion081
FEATURE [Sketcher::SketchObject] Sketch051
  FullyConstrained = true
  Placement = pos=(117,19,0) rot=(0.57735,0.57735,0.57735;2.0944rad)
  sketch-geometry (48):
    g0: LineSegment StartX=-49.19 StartY=69.25 StartZ=0 EndX=-49.19 EndY=66.25 EndZ=0
    g1: LineSegment StartX=-49.19 StartY=63.5 StartZ=0 EndX=-49.19 EndY=60.5 EndZ=0
    g2: LineSegment StartX=-49.19 StartY=57.75 StartZ=0 EndX=-49.19 EndY=54.75 EndZ=0
    g3: LineSegment StartX=-49.19 StartY=52 StartZ=0 EndX=-49.19 EndY=49 EndZ=0
    g4: LineSegment StartX=-49.19 StartY=46.25 StartZ=0 EndX=-49.19 EndY=43.25 EndZ=0
    g5: LineSegment StartX=-49.19 StartY=40.5 StartZ=0 EndX=-49.19 EndY=37.5 EndZ=0
    g6: LineSegment StartX=-49.19 StartY=34.5 StartZ=0 EndX=-49.19 EndY=31.5 EndZ=0
    g7: LineSegment StartX=-49.19 StartY=28.75 StartZ=0 EndX=-49.19 EndY=25.75 EndZ=0
    g8: LineSegment StartX=-49.19 StartY=23 StartZ=0 EndX=-49.19 EndY=20 EndZ=0
    g9: LineSegment StartX=-49.19 StartY=17.25 StartZ=0 EndX=-49.19 EndY=14.25 EndZ=0
    g10: LineSegment StartX=-49.19 StartY=11.5 StartZ=0 EndX=-49.19 EndY=8.5 EndZ=0
    g11: LineSegment StartX=-49.19 StartY=5.75 StartZ=0 EndX=-49.19 EndY=2.75 EndZ=0
    g12: ArcOfCircle CenterX=-1.5 CenterY=67.75 CenterZ=0 NormalX=0 NormalY=0 NormalZ=1 AngleXU=0 Radius=1.5 StartAngle=4.71239 EndAngle=7.85398
    g13: ArcOfCircle CenterX=-1.5 CenterY=62 CenterZ=0 NormalX=0 NormalY=0 NormalZ=1 AngleXU=0 Radius=1.5 StartAngle=4.71239 EndAngle=7.85398
    g14: ArcOfCircle CenterX=-1.5 CenterY=56.25 CenterZ=0 NormalX=0 NormalY=0 NormalZ=1 AngleXU=0 Radius=1.5 StartAngle=4.71239 EndAngle=7.85398
    g15: ArcOfCircle CenterX=-11.49 CenterY=50.5 CenterZ=0 NormalX=0 NormalY=0 NormalZ=1 AngleXU=0 Radius=1.5 StartAngle=4.71239 EndAngle=7.85398
    g16: ArcOfCircle CenterX=-16.28 CenterY=44.75 CenterZ=0 NormalX=0 NormalY=0 NormalZ=1 AngleXU=0 Radius=1.5 StartAngle=4.71239 EndAngle=7.85398
    g17: ArcOfCircle CenterX=-18.2337 CenterY=39 CenterZ=0 NormalX=0 NormalY=0 NormalZ=1 AngleXU=0 Radius=1.5 StartAngle=4.71485 EndAngle=7.85398
    g18: ArcOfCircle CenterX=-16.2837 CenterY=27.25 CenterZ=0 NormalX=0 NormalY=0 NormalZ=1 AngleXU=0 Radius=1.5 StartAngle=4.71485 EndAngle=7.85398
    g19: ArcOfCircle CenterX=-18.2337 CenterY=33 CenterZ=0 NormalX=0 NormalY=0 NormalZ=1 AngleXU=0 Radius=1.5 StartAngle=4.71485 EndAngle=7.85398
    g20: ArcOfCircle CenterX=-11.49 CenterY=21.5 CenterZ=0 NormalX=0 NormalY=0 NormalZ=1 AngleXU=0 Radius=1.5 StartAngle=4.71239 EndAngle=7.85398
    g21: ArcOfCircle CenterX=-1.5 CenterY=4.25 CenterZ=0 NormalX=0 NormalY=0 NormalZ=1 AngleXU=0 Radius=1.5 StartAngle=4.71239 EndAngle=7.85398
    g22: ArcOfCircle CenterX=-1.5 CenterY=10 CenterZ=0 NormalX=0 NormalY=0 NormalZ=1 AngleXU=0 Radius=1.5 StartAngle=4.71239 EndAngle=7.85398
    g23: ArcOfCircle CenterX=-1.5 CenterY=15.75 CenterZ=0 NormalX=0 NormalY=0 NormalZ=1 AngleXU=0 Radius=1.5 StartAngle=4.71239 EndAngle=7.85398
    g24: LineSegment StartX=-49.19 StartY=69.25 StartZ=0 EndX=-1.5 EndY=69.25 EndZ=0
    g25: LineSegment StartX=-49.19 StartY=66.25 StartZ=0 EndX=-1.5 EndY=66.25 EndZ=0
    g26: LineSegment StartX=-49.19 StartY=63.5 StartZ=0 EndX=-1.5 EndY=63.5 EndZ=0
    g27: LineSegment StartX=-49.19 StartY=60.5 StartZ=0 EndX=-1.5 EndY=60.5 EndZ=0
    g28: LineSegment StartX=-49.19 StartY=57.75 StartZ=0 EndX=-1.5 EndY=57.75 EndZ=0
    g29: LineSegment StartX=-49.19 StartY=54.75 StartZ=0 EndX=-1.5 EndY=54.75 EndZ=0
    g30: LineSegment StartX=-49.19 StartY=52 StartZ=0 EndX=-11.49 EndY=52 EndZ=0
    g31: LineSegment StartX=-49.19 StartY=49 StartZ=0 EndX=-11.49 EndY=49 EndZ=0
    g32: LineSegment StartX=-49.19 StartY=46.25 StartZ=0 EndX=-16.28 EndY=46.25 EndZ=0
    g33: LineSegment StartX=-49.19 StartY=43.25 StartZ=0 EndX=-16.28 EndY=43.25 EndZ=0
    g34: LineSegment StartX=-49.19 StartY=40.5 StartZ=0 EndX=-18.2337 EndY=40.5 EndZ=0
    g35: LineSegment StartX=-49.19 StartY=37.5 StartZ=0 EndX=-18.23 EndY=37.5 EndZ=0
    g36: LineSegment StartX=-49.19 StartY=34.5 StartZ=0 EndX=-18.2337 EndY=34.5 EndZ=0
    g37: LineSegment StartX=-49.19 StartY=31.5 StartZ=0 EndX=-18.23 EndY=31.5 EndZ=0
    g38: LineSegment StartX=-49.19 StartY=28.75 StartZ=0 EndX=-16.2837 EndY=28.75 EndZ=0
    g39: LineSegment StartX=-49.19 StartY=25.75 StartZ=0 EndX=-16.28 EndY=25.75 EndZ=0
    g40: LineSegment StartX=-49.19 StartY=23 StartZ=0 EndX=-11.49 EndY=23 EndZ=0
    g41: LineSegment StartX=-49.19 StartY=20 StartZ=0 EndX=-11.49 EndY=20 EndZ=0
    g42: LineSegment StartX=-49.19 StartY=17.25 StartZ=0 EndX=-1.5 EndY=17.25 EndZ=0
    g43: LineSegment StartX=-49.19 StartY=14.25 StartZ=0 EndX=-1.5 EndY=14.25 EndZ=0
    g44: LineSegment StartX=-49.19 StartY=11.5 StartZ=0 EndX=-1.5 EndY=11.5 EndZ=0
    g45: LineSegment StartX=-49.19 StartY=8.5 StartZ=0 EndX=-1.5 EndY=8.5 EndZ=0
    g46: LineSegment StartX=-49.19 StartY=5.75 StartZ=0 EndX=-1.5 EndY=5.75 EndZ=0
    g47: LineSegment StartX=-49.19 StartY=2.75 StartZ=0 EndX=-1.5 EndY=2.75 EndZ=0
  constraints (120):
    c: Vertical(g0)
    c: Distance(g0) = 3
    c: Block(g0)
    c: Vertical(g1)
    c: Distance(g1) = 3
    c: Vertical(g2)
    c: Equal(g0,g2) = 3
    c: Block(g2)
    c: Vertical(g3)
    c: Equal(g1,g3) = 3
    c: Vertical(g4)
    c: Equal(g0,g4) = 3
    c: Block(g4)
    c: Vertical(g5)
    c: Equal(g1,g5) = 3
    c: Vertical(g6)
    c: Equal(g0,g6) = 3
    c: Block(g6)
    c: Vertical(g7)
    c: Equal(g1,g7) = 3
    c: Vertical(g8)
    c: Equal(g0,g8) = 3
    c: Block(g8)
    c: Vertical(g9)
    c: Equal(g1,g9) = 3
    c: Vertical(g10)
    c: Equal(g0,g10) = 3
    c: Block(g10)
    c: Vertical(g11)
    c: Equal(g1,g11) = 3
    c: Block(g12)
    c: Block(g13)
    c: Block(g14)
    c: Block(g15)
    c: Block(g16)
    c: Block(g17)
    c: Block(g18)
    c: Block(g19)
    c: Block(g20)
    c: Block(g21)
    c: Block(g22)
    c: Block(g23)
    c: Block(g11)
    c: Block(g9)
    c: Block(g7)
    c: Block(g5)
    c: Block(g3)
    c: Block(g1)
    c: Coincident(g24,g0)
    c: Coincident(g24,g12)
    c: Horizontal(g24)
    c: Coincident(g25,g0)
    c: Coincident(g25,g12)
    c: Horizontal(g25)
    c: Coincident(g26,g1)
    c: Coincident(g26,g13)
    c: Horizontal(g26)
    c: Coincident(g27,g1)
    c: Coincident(g27,g13)
    c: Horizontal(g27)
    c: Coincident(g28,g2)
    c: Coincident(g28,g14)
    c: Horizontal(g28)
    c: Coincident(g29,g2)
    c: Coincident(g29,g14)
    c: Horizontal(g29)
    c: Coincident(g30,g3)
    c: Coincident(g30,g15)
    c: Horizontal(g30)
    c: Coincident(g31,g3)
    c: Coincident(g31,g15)
    c: Horizontal(g31)
    c: Coincident(g32,g4)
    c: Coincident(g32,g16)
    c: Horizontal(g32)
    c: Coincident(g33,g4)
    c: Coincident(g33,g16)
    c: Horizontal(g33)
    c: Coincident(g34,g5)
    c: Coincident(g34,g17)
    c: Horizontal(g34)
    c: Coincident(g35,g5)
    c: Coincident(g35,g17)
    c: Horizontal(g35)
    c: Coincident(g36,g6)
    c: Coincident(g36,g19)
    c: Horizontal(g36)
    c: Coincident(g37,g6)
    c: Coincident(g37,g19)
    c: Horizontal(g37)
    c: Coincident(g38,g7)
    c: Coincident(g38,g18)
    c: Horizontal(g38)
    c: Coincident(g39,g7)
    c: Coincident(g39,g18)
    c: Horizontal(g39)
    c: Coincident(g40,g8)
    c: Coincident(g40,g20)
    c: Horizontal(g40)
    c: Coincident(g41,g8)
    c: Coincident(g41,g20)
    c: Horizontal(g41)
    c: Coincident(g42,g9)
    c: Coincident(g42,g23)
    c: Horizontal(g42)
    c: Coincident(g43,g9)
    c: Coincident(g43,g23)
    c: Horizontal(g43)
    c: Coincident(g44,g10)
    c: Coincident(g44,g22)
    c: Horizontal(g44)
    c: Coincident(g45,g10)
    c: Coincident(g45,g22)
    c: Horizontal(g45)
    c: Coincident(g46,g11)
    c: Coincident(g46,g21)
    c: Horizontal(g46)
    c: Coincident(g47,g11)
    c: Coincident(g47,g21)
    c: Horizontal(g47)
FEATURE [Part::Extrusion] Extrude042
  Base = -> Sketch051
  Dir = (1,-2e-16,2e-16)
  DirMode = 2
  FaceMakerClass = Part::FaceMakerBullseye
  LengthFwd = 19
  LengthRev = 0
  Placement = pos=(-19,0,0) rot=(0,0,1;0rad)
  Solid = true
  Symmetric = false
FEATURE [Part::Fillet] Fillet035  label="removeToCreateVentalationHoles"
  Base = -> Extrude042
  Edges = <same value as first occurrence — deduplicated (x6 in doc)>
  Placement = pos=(7,0,0) rot=(0,0,1;0rad)
FEATURE [Part::Cut] Cut038  label="top017"
  Base = -> Cut033
  Tool = -> Fillet035
FEATURE [Sketcher::SketchObject] Sketch052  label="bottomSketch001"
  FullyConstrained = true
  sketch-geometry (45):
    g0: LineSegment StartX=6.29999 StartY=8 StartZ=0 EndX=3.29999 EndY=8 EndZ=0
    g1: LineSegment StartX=3.29999 StartY=8 StartZ=0 EndX=3.29999 EndY=-6.03275e-07 EndZ=0
    g2: ArcOfCircle CenterX=8.29999 CenterY=5 CenterZ=0 NormalX=0 NormalY=0 NormalZ=1 AngleXU=0 Radius=2 StartAngle=3.14159 EndAngle=4.71239
    g3: LineSegment StartX=6.29999 StartY=8 StartZ=0 EndX=6.29999 EndY=5 EndZ=0
    g4: ArcOfCircle CenterX=105 CenterY=19 CenterZ=0 NormalX=0 NormalY=0 NormalZ=1 AngleXU=0 Radius=12.7 StartAngle=4.71239 EndAngle=5.94289
    g5-g11: Circle x7 (B-spline internal-alignment scaffolding for g12; pole/knot coordinates omitted)
    g12: BSplineCurve PolesCount=7 KnotsCount=5 Degree=3 IsPeriodic=0
    g13-g17: GeomPoint x5 (B-spline internal-alignment scaffolding for g12; pole/knot coordinates omitted)
    g18: ArcOfCircle CenterX=105 CenterY=19 CenterZ=0 NormalX=0 NormalY=0 NormalZ=1 AngleXU=0 Radius=15.7 StartAngle=5.81226 EndAngle=6.28319
    g19: BSplineCurve PolesCount=5 KnotsCount=3 Degree=3 IsPeriodic=0
    g20: LineSegment StartX=8.29999 StartY=3 StartZ=0 EndX=101.7 EndY=3 EndZ=0
    g21: LineSegment StartX=3.29999 StartY=-6.03275e-07 StartZ=0 EndX=105 EndY=-6.03275e-07 EndZ=0
    g22: LineSegment StartX=120.974 StartY=8.71251 StartZ=0 EndX=122.332 EndY=7.83778 EndZ=0
    g23: LineSegment StartX=105 StartY=-6.03274e-07 StartZ=0 EndX=113 EndY=-6.03274e-07 EndZ=0
    g24: ArcOfCircle CenterX=105 CenterY=19 CenterZ=0 NormalX=0 NormalY=0 NormalZ=1 AngleXU=0 Radius=20.6155 StartAngle=5.11091 EndAngle=5.71103
    g25: ArcOfCircle CenterX=117.7 CenterY=19 CenterZ=0 NormalX=0 NormalY=0 NormalZ=1 AngleXU=0 Radius=3 StartAngle=1.2e-15 EndAngle=2.10468
    g26: Circle CenterX=116.345 CenterY=16.3232 CenterZ=0 NormalX=0 NormalY=0 NormalZ=1 AngleXU=0 Radius=1
    g27: Circle CenterX=117.24 CenterY=15.7584 CenterZ=0 NormalX=0 NormalY=0 NormalZ=1 AngleXU=0 Radius=1
    g28: Circle CenterX=116.972 CenterY=14.7612 CenterZ=0 NormalX=0 NormalY=0 NormalZ=1 AngleXU=0 Radius=1
    g29: BSplineCurve PolesCount=3 KnotsCount=2 Degree=2 IsPeriodic=0
    g30: GeomPoint X=116.345 Y=16.3232 Z=0
    g31: GeomPoint X=116.972 Y=14.7612 Z=0
    g32: Circle CenterX=115.828 CenterY=17.157 CenterZ=0 NormalX=0 NormalY=0 NormalZ=1 AngleXU=0 Radius=1
    g33: Circle CenterX=115.841 CenterY=16.639 CenterZ=0 NormalX=0 NormalY=0 NormalZ=1 AngleXU=0 Radius=1
    g34: Circle CenterX=116.345 CenterY=16.3232 CenterZ=0 NormalX=0 NormalY=0 NormalZ=1 AngleXU=0 Radius=1
    g35: BSplineCurve PolesCount=3 KnotsCount=2 Degree=2 IsPeriodic=0
    g36: GeomPoint X=115.828 Y=17.157 Z=0
    g37: GeomPoint X=116.345 Y=16.3232 Z=0
    g38: LineSegment StartX=115.828 StartY=17.157 StartZ=0 EndX=115.828 EndY=20.8307 EndZ=0
    g39: Circle CenterX=115.828 CenterY=20.8307 CenterZ=0 NormalX=0 NormalY=0 NormalZ=1 AngleXU=0 Radius=1
    g40: Circle CenterX=115.831 CenterY=21.3396 CenterZ=0 NormalX=0 NormalY=0 NormalZ=1 AngleXU=0 Radius=1
    g41: Circle CenterX=116.173 CenterY=21.5825 CenterZ=0 NormalX=0 NormalY=0 NormalZ=1 AngleXU=0 Radius=1
    g42: BSplineCurve PolesCount=3 KnotsCount=2 Degree=2 IsPeriodic=0
    g43: GeomPoint X=115.828 Y=20.8307 Z=0
    g44: GeomPoint X=116.173 Y=21.5825 Z=0
  constraints (70):
    c: Horizontal(g0)
    c: Distance(g0) = 3
    c: Coincident(g1,g0)
    c: Vertical(g1)
    c: Block(g2)
    c: Block(g0)
    c: Coincident(g3,g0)
    c: Coincident(g3,g2)
    c: Vertical(g3)
    c: Block(g1)
    c: Block(g4)
    c: Coincident(g19,g4)
    c: Block(g19)
    c: Equal(g5, g6-g11) x6
    c: InternalAlignment(g5-g11 -> g12) x7
    c: InternalAlignment(g13-g17 -> g12) x5
    c: Block(g12)
    c: Coincident(g18,g12)
    c: Block(g18)
    c: Coincident(g20,g2)
    c: Coincident(g20,g19)
    c: Horizontal(g20)
    c: Distance(g20) = 93.4
    c: Coincident(g21,g1)
    c: Horizontal(g21)
    c: Distance(g21) = 101.7
    c: Horizontal(g23)
    c: Distance(g23) = 8
    c: Coincident(g24,g23)
    c: Block(g23)
    c: Coincident(g22,g24)
    c: Block(g24)
    c: Block(g22)
    c: Distance(g22) = 1.61553
    c: Coincident(g25,g18)
    c: Block(g25)
    c: Weight(g26) = 1
    c: Equal(g26,g27)
    c: Equal(g26,g28)
    c: Coincident(g29,g4)
    c: InternalAlignment(g26,g29)
    c: InternalAlignment(g27,g29)
    c: InternalAlignment(g28,g29)
    c: InternalAlignment(g30,g29)
    c: InternalAlignment(g31,g29)
    c: Block(g29)
    c: Weight(g32) = 1
    c: Equal(g32,g33)
    c: Equal(g32,g34)
    c: Coincident(g35,g29)
    c: InternalAlignment(g32,g35)
    c: InternalAlignment(g33,g35)
    c: InternalAlignment(g34,g35)
    c: InternalAlignment(g36,g35)
    c: InternalAlignment(g37,g35)
    c: Block(g35)
    c: Coincident(g38,g35)
    c: Vertical(g38)
    c: Block(g38)
    c: Coincident(g42,g38)
    c: Weight(g39) = 1
    c: Equal(g39,g40)
    c: Equal(g39,g41)
    c: Coincident(g42,g25)
    c: InternalAlignment(g39,g42)
    c: InternalAlignment(g40,g42)
    c: InternalAlignment(g41,g42)
    c: InternalAlignment(g43,g42)
    c: InternalAlignment(g44,g42)
    c: Block(g42)
FEATURE [Part::Extrusion] Extrude043  label="bottom010"
  Base = -> Sketch052
  Dir = (0,0,1)
  DirMode = 2
  FaceMakerClass = Part::FaceMakerBullseye
  LengthFwd = 71.4
  LengthRev = 0
  Placement = pos=(0,0,0.3) rot=(0,0,1;0rad)
  Solid = true
  Symmetric = false
FEATURE [Sketcher::SketchObject] Sketch053  label="topSketch013"
  FullyConstrained = true
  sketch-geometry (22):
    g0: LineSegment StartX=5.21097e-06 StartY=3 StartZ=0 EndX=5.21097e-06 EndY=19 EndZ=0
    g1: ArcOfCircle CenterX=19 CenterY=19 CenterZ=0 NormalX=0 NormalY=0 NormalZ=1 AngleXU=0 Radius=19 StartAngle=1.5708 EndAngle=3.14159
    g2: ArcOfCircle CenterX=19 CenterY=19 CenterZ=0 NormalX=0 NormalY=0 NormalZ=1 AngleXU=0 Radius=16 StartAngle=1.5708 EndAngle=3.14159
    g3: LineSegment StartX=114 StartY=35 StartZ=0 EndX=19 EndY=35 EndZ=0
    g4: LineSegment StartX=5.21097e-06 StartY=3 StartZ=0 EndX=5.21097e-06 EndY=0 EndZ=0
    g5: LineSegment StartX=3 StartY=0 StartZ=0 EndX=5.21097e-06 EndY=0 EndZ=0
    g6: LineSegment StartX=3 StartY=19 StartZ=0 EndX=3 EndY=0 EndZ=0
    g7: LineSegment StartX=19 StartY=38 StartZ=0 EndX=124 EndY=38 EndZ=0
    g8: Circle CenterX=119 CenterY=35 CenterZ=0 NormalX=0 NormalY=0 NormalZ=1 AngleXU=0 Radius=1
    g9: Circle CenterX=121 CenterY=35 CenterZ=0 NormalX=0 NormalY=0 NormalZ=1 AngleXU=0 Radius=1
    g10: Circle CenterX=121 CenterY=33 CenterZ=0 NormalX=0 NormalY=0 NormalZ=1 AngleXU=0 Radius=1
    g11: BSplineCurve PolesCount=3 KnotsCount=2 Degree=2 IsPeriodic=0
    g12: GeomPoint X=119 Y=35 Z=0
    g13: GeomPoint X=121 Y=33 Z=0
    g14: LineSegment StartX=119 StartY=35 StartZ=0 EndX=114 EndY=35 EndZ=0
    g15: ArcOfCircle CenterX=105 CenterY=19 CenterZ=0 NormalX=0 NormalY=0 NormalZ=1 AngleXU=0 Radius=16 StartAngle=5.60905 EndAngle=6.28319
    g16: LineSegment StartX=121 StartY=33 StartZ=0 EndX=121 EndY=19 EndZ=0
    g17: LineSegment StartX=117.5 StartY=9.01251 StartZ=0 EndX=121.163 EndY=9.0125 EndZ=0
    g18: ArcOfCircle CenterX=105 CenterY=19 CenterZ=0 NormalX=0 NormalY=0 NormalZ=1 AngleXU=0 Radius=20.6155 StartAngle=5.7297 EndAngle=6.28319
    g19: LineSegment StartX=121.163 StartY=9.0125 StartZ=0 EndX=122.538 EndY=8.16329 EndZ=0
    g20: LineSegment StartX=124 StartY=38 StartZ=0 EndX=125.616 EndY=38 EndZ=0
    g21: LineSegment StartX=125.616 StartY=19 StartZ=0 EndX=125.616 EndY=38 EndZ=0
  constraints (50):
    c: Vertical(g0)
    c: Block(g0)
    c: Coincident(g1,g0)
    c: Block(g1)
    c: Coincident(g2,g1)
    c: Block(g2)
    c: Coincident(g3,g2)
    c: Horizontal(g3)
    c: Tangent(g3,g2)
    c: Coincident(g4,g0)
    c: Distance(g4) = 3
    c: Vertical(g4)
    c: Coincident(g5,g4)
    c: Horizontal(g5)
    c: Coincident(g6,g2)
    c: Coincident(g6,g5)
    c: Vertical(g6)
    c: Horizontal(g7)
    c: Distance(g7) = 105
    c: Coincident(g7,g1)
    c: Block(g3)
    c: Weight(g8) = 1
    c: Equal(g8,g9)
    c: Equal(g8,g10)
    c: InternalAlignment(g8,g11)
    c: InternalAlignment(g9,g11)
    c: InternalAlignment(g10,g11)
    c: InternalAlignment(g12,g11)
    c: InternalAlignment(g13,g11)
    c: Block(g11)
    c: Coincident(g14,g11)
    c: Coincident(g14,g3)
    c: Horizontal(g14)
    c: Block(g15)
    c: Coincident(g16,g11)
    c: Coincident(g16,g15)
    c: Vertical(g16)
    c: Distance(g16) = 14
    c: Coincident(g17,g15)
    c: Block(g18)
    c: Coincident(g19,g18)
    c: Coincident(g20,g7)
    c: Horizontal(g20)
    c: Vertical(g21)
    c: Coincident(g20,g21)
    c: Block(g20)
    c: Block(g21)
    c: Block(g19)
    c: Block(g17)
    c: Distance(g20) = 1.61553
FEATURE [Part::Extrusion] Extrude044
  Base = -> Sketch053
  Dir = (0,0,1)
  DirMode = 2
  FaceMakerClass = Part::FaceMakerBullseye
  LengthFwd = 72
  LengthRev = 0
  Solid = true
  Symmetric = false
FEATURE [Part::Fillet] Fillet036  label="top018"
  Base = -> Extrude044
  Edges = 1 edges r=2: [Edge41]
FEATURE [Sketcher::SketchObject] Sketch054
  FullyConstrained = false
  Placement = pos=(0,0,0) rot=(1,0,0;1.5708rad)
  sketch-geometry (24):
    g0: ArcOfCircle CenterX=-4 CenterY=-10.5 CenterZ=0 NormalX=0 NormalY=0 NormalZ=1 AngleXU=0 Radius=1.5 StartAngle=6e-16 EndAngle=3.14159
    g1: ArcOfCircle CenterX=-34.2 CenterY=-10.5 CenterZ=0 NormalX=0 NormalY=0 NormalZ=1 AngleXU=0 Radius=1.5 StartAngle=0 EndAngle=3.14159
    g2: ArcOfCircle CenterX=-34.2 CenterY=-27.7 CenterZ=0 NormalX=0 NormalY=0 NormalZ=1 AngleXU=0 Radius=1.5 StartAngle=3.14159 EndAngle=6.28319
    g3: ArcOfCircle CenterX=-4 CenterY=-27.7 CenterZ=0 NormalX=0 NormalY=0 NormalZ=1 AngleXU=0 Radius=1.5 StartAngle=3.1416 EndAngle=6.28319
    g4: ArcOfCircle CenterX=-10 CenterY=-4.3 CenterZ=0 NormalX=0 NormalY=0 NormalZ=1 AngleXU=0 Radius=1.5 StartAngle=2e-16 EndAngle=3.14159
    g5: ArcOfCircle CenterX=-16.1 CenterY=-1.8 CenterZ=0 NormalX=0 NormalY=0 NormalZ=1 AngleXU=0 Radius=1.5 StartAngle=5e-16 EndAngle=3.14159
    g6: ArcOfCircle CenterX=-22.1 CenterY=-1.8 CenterZ=0 NormalX=0 NormalY=0 NormalZ=1 AngleXU=0 Radius=1.5 StartAngle=5e-16 EndAngle=3.14159
    g7: ArcOfCircle CenterX=-28.2 CenterY=-4.3 CenterZ=0 NormalX=0 NormalY=0 NormalZ=1 AngleXU=0 Radius=1.5 StartAngle=2e-16 EndAngle=3.14159
    g8: ArcOfCircle CenterX=-10 CenterY=-33.9 CenterZ=0 NormalX=0 NormalY=0 NormalZ=1 AngleXU=0 Radius=1.5 StartAngle=3.14159 EndAngle=6.28319
    g9: ArcOfCircle CenterX=-16.1 CenterY=-36.4 CenterZ=0 NormalX=0 NormalY=0 NormalZ=1 AngleXU=0 Radius=1.5 StartAngle=3.14159 EndAngle=6.28319
    g10: ArcOfCircle CenterX=-22.1 CenterY=-36.4 CenterZ=0 NormalX=0 NormalY=0 NormalZ=1 AngleXU=0 Radius=1.5 StartAngle=3.14159 EndAngle=6.28319
    g11: ArcOfCircle CenterX=-28.2 CenterY=-33.9 CenterZ=0 NormalX=0 NormalY=0 NormalZ=1 AngleXU=0 Radius=1.5 StartAngle=3.14159 EndAngle=6.28319
    g12: LineSegment StartX=-35.7 StartY=-10.5 StartZ=0 EndX=-35.7 EndY=-27.7 EndZ=0
    g13: LineSegment StartX=-32.7 StartY=-10.5 StartZ=0 EndX=-32.7 EndY=-27.7 EndZ=0
    g14: LineSegment StartX=-29.7 StartY=-33.9 StartZ=0 EndX=-29.7 EndY=-4.3 EndZ=0
    g15: LineSegment StartX=-26.7 StartY=-33.9 StartZ=0 EndX=-26.7 EndY=-4.3 EndZ=0
    g16: LineSegment StartX=-2.5 StartY=-10.5 StartZ=0 EndX=-2.5 EndY=-27.7 EndZ=0
    g17: LineSegment StartX=-8.5 StartY=-4.3 StartZ=0 EndX=-8.5 EndY=-33.9 EndZ=0
    g18: LineSegment StartX=-5.5 StartY=-10.5 StartZ=0 EndX=-5.5 EndY=-27.7 EndZ=0
    g19: LineSegment StartX=-11.5 StartY=-4.3 StartZ=0 EndX=-11.5 EndY=-33.9 EndZ=0
    g20: LineSegment StartX=-14.6 StartY=-1.8 StartZ=0 EndX=-14.6 EndY=-36.4 EndZ=0
    g21: LineSegment StartX=-17.6 StartY=-1.8 StartZ=0 EndX=-17.6 EndY=-36.4 EndZ=0
    g22: LineSegment StartX=-20.6 StartY=-36.4 StartZ=0 EndX=-20.6 EndY=-1.8 EndZ=0
    g23: LineSegment StartX=-23.6 StartY=-1.8 StartZ=0 EndX=-23.6 EndY=-36.4 EndZ=0
  constraints (48):
    c: Block(g0)
    c: Block(g1)
    c: Block(g2)
    c: Block(g3)
    c: Block(g4)
    c: Block(g5)
    c: Block(g6)
    c: Block(g7)
    c: Block(g8)
    c: Block(g9)
    c: Block(g10)
    c: Block(g11)
    c: Coincident(g12,g1)
    c: Coincident(g12,g2)
    c: Vertical(g12)
    c: Coincident(g13,g1)
    c: Coincident(g13,g2)
    c: Vertical(g13)
    c: Coincident(g14,g11)
    c: Coincident(g14,g7)
    c: Vertical(g14)
    c: Coincident(g15,g11)
    c: Coincident(g15,g7)
    c: Vertical(g15)
    c: Coincident(g16,g0)
    c: Coincident(g16,g3)
    c: Vertical(g16)
    c: Coincident(g17,g4)
    c: Coincident(g17,g8)
    c: Vertical(g17)
    c: Coincident(g18,g0)
    c: Coincident(g18,g3)
    c: Vertical(g18)
    c: Coincident(g19,g4)
    c: Coincident(g19,g8)
    c: Vertical(g19)
    c: Coincident(g20,g5)
    c: Coincident(g20,g9)
    c: Vertical(g20)
    c: Coincident(g21,g5)
    c: Coincident(g21,g9)
    c: Vertical(g21)
    c: Coincident(g22,g10)
    c: Coincident(g22,g6)
    c: Vertical(g22)
    c: Coincident(g23,g6)
    c: Coincident(g23,g10)
    c: Vertical(g23)
FEATURE [Part::Extrusion] Extrude045  label="removeToCreateFanGrillHoles003"
  Base = -> Sketch054
  Dir = (0,-1,6e-16)
  DirMode = 2
  FaceMakerClass = Part::FaceMakerBullseye
  LengthFwd = 10
  LengthRev = 0
  Placement = pos=(65.4,44,54.82) rot=(0,0,1;0rad)
  Solid = true
  Symmetric = false
FEATURE [Part::Feature] Face105 .. Face108  x4 (patterned run collapsed; names and placements below)
  shape: bbox 3.5 x 17.8 x 2e-07 mm, 1 faces, 0 solids (baked)
FEATURE [Part::Revolution] Revolve113  label="removeToCreateScrewAndThreadedInsertHole041"
  Angle = 360
  Axis = (0,1,0)
  Base = (0,0,0)
  FaceMakerClass = Part::FaceMakerBullseye
  Placement = pos=(62.3,30.3,19.7) rot=(0,0,1;0rad)
  Solid = false
  Source = -> Face105
  Symmetric = false
FEATURE [Part::Revolution] Revolve114  label="removeToCreateScrewAndThreadedInsertHole042"
  Angle = 360
  Axis = (0,1,0)
  Base = (0,0,0)
  FaceMakerClass = Part::FaceMakerBullseye
  Placement = pos=(62.3,30.3,51.7) rot=(0,0,1;0rad)
  Solid = false
  Source = -> Face106
  Symmetric = false
FEATURE [Part::Revolution] Revolve115  label="removeToCreateScrewAndThreadedInsertHole043"
  Angle = 360
  Axis = (0,1,0)
  Base = (0,0,0)
  FaceMakerClass = Part::FaceMakerBullseye
  Placement = pos=(30.3,30.3,19.7) rot=(0,0,1;0rad)
  Solid = false
  Source = -> Face107
  Symmetric = false
FEATURE [Part::Revolution] Revolve116  label="removeToCreateScrewAndThreadedInsertHole044"
  Angle = 360
  Axis = (0,1,0)
  Base = (0,0,0)
  FaceMakerClass = Part::FaceMakerBullseye
  Placement = pos=(30.3,30.3,51.7) rot=(0,0,1;0rad)
  Solid = false
  Source = -> Face108
  Symmetric = false
FEATURE [Part::MultiFuse] Fusion083  label="createThreadedInsertHolesForFan004"
  Shapes = -> [Revolve113,Revolve114,Revolve115,Revolve116]
FEATURE [Part::Box] Box024  label="removeToCreteHoleForPlugHousing026"
  AttacherType = Attacher::AttachEngine3D
  Height = 28.6
  Length = 10
  Placement = pos=(-2,0,21.7) rot=(0,0,1;0rad)
  Width = 19
FEATURE [Part::Cylinder] Cylinder038  label="removeToCreteHoleForPlugHousing027"
  Angle = 360
  AttacherType = Attacher::AttachEngine3D
  Height = 20
  Placement = pos=(-2,19,36) rot=(0,1,0;1.5708rad)
  Radius = 14.3
FEATURE [Part::MultiFuse] Fusion084  label="removeToCreteHoleForPlugHousing028"
  Shapes = -> [Box024,Cylinder038]
FEATURE [Part::Cylinder] Cylinder039
  Angle = 360
  AttacherType = Attacher::AttachEngine3D
  Height = 20
  Placement = pos=(0,0,36.15) rot=(0,0,1;0rad)
  Radius = 14.3
FEATURE [Part::Cylinder] Cylinder040
  Angle = 360
  AttacherType = Attacher::AttachEngine3D
  Height = 10
  Placement = pos=(0,0,36.15) rot=(0,0,1;0rad)
  Radius = 4
FEATURE [Part::Box] Box025  label="removeToCreteHoleForPlugHousing030"
  AttacherType = Attacher::AttachEngine3D
  Height = 28.6
  Length = 20
  Placement = pos=(106.15,0,21.7) rot=(0,0,1;0rad)
  Width = 19
FEATURE [Part::MultiFuse] Fusion086  label="removeToCreteHoleForPlugHousing031"
  Placement = pos=(70,19,36) rot=(0,1,0;1.5708rad)
  Shapes = -> [Cylinder039,Cylinder040]
FEATURE [Part::MultiFuse] Fusion085  label="removeToCreteHoleForPlugHousing029"
  Shapes = -> [Box025,Fusion086]
FEATURE [Sketcher::SketchObject] Sketch055
  FullyConstrained = true
  Placement = pos=(117,19,0) rot=(0.57735,0.57735,0.57735;2.0944rad)
  sketch-geometry (48):
    g0: LineSegment StartX=-49.19 StartY=69.25 StartZ=0 EndX=-49.19 EndY=66.25 EndZ=0
    g1: LineSegment StartX=-49.19 StartY=63.5 StartZ=0 EndX=-49.19 EndY=60.5 EndZ=0
    g2: LineSegment StartX=-49.19 StartY=57.75 StartZ=0 EndX=-49.19 EndY=54.75 EndZ=0
    g3: LineSegment StartX=-49.19 StartY=52 StartZ=0 EndX=-49.19 EndY=49 EndZ=0
    g4: LineSegment StartX=-49.19 StartY=46.25 StartZ=0 EndX=-49.19 EndY=43.25 EndZ=0
    g5: LineSegment StartX=-49.19 StartY=40.5 StartZ=0 EndX=-49.19 EndY=37.5 EndZ=0
    g6: LineSegment StartX=-49.19 StartY=34.5 StartZ=0 EndX=-49.19 EndY=31.5 EndZ=0
    g7: LineSegment StartX=-49.19 StartY=28.75 StartZ=0 EndX=-49.19 EndY=25.75 EndZ=0
    g8: LineSegment StartX=-49.19 StartY=23 StartZ=0 EndX=-49.19 EndY=20 EndZ=0
    g9: LineSegment StartX=-49.19 StartY=17.25 StartZ=0 EndX=-49.19 EndY=14.25 EndZ=0
    g10: LineSegment StartX=-49.19 StartY=11.5 StartZ=0 EndX=-49.19 EndY=8.5 EndZ=0
    g11: LineSegment StartX=-49.19 StartY=5.75 StartZ=0 EndX=-49.19 EndY=2.75 EndZ=0
    g12: ArcOfCircle CenterX=-1.5 CenterY=67.75 CenterZ=0 NormalX=0 NormalY=0 NormalZ=1 AngleXU=0 Radius=1.5 StartAngle=4.71239 EndAngle=7.85398
    g13: ArcOfCircle CenterX=-1.5 CenterY=62 CenterZ=0 NormalX=0 NormalY=0 NormalZ=1 AngleXU=0 Radius=1.5 StartAngle=4.71239 EndAngle=7.85398
    g14: ArcOfCircle CenterX=-1.5 CenterY=56.25 CenterZ=0 NormalX=0 NormalY=0 NormalZ=1 AngleXU=0 Radius=1.5 StartAngle=4.71239 EndAngle=7.85398
    g15: ArcOfCircle CenterX=-11.49 CenterY=50.5 CenterZ=0 NormalX=0 NormalY=0 NormalZ=1 AngleXU=0 Radius=1.5 StartAngle=4.71239 EndAngle=7.85398
    g16: ArcOfCircle CenterX=-16.28 CenterY=44.75 CenterZ=0 NormalX=0 NormalY=0 NormalZ=1 AngleXU=0 Radius=1.5 StartAngle=4.71239 EndAngle=7.85398
    g17: ArcOfCircle CenterX=-18.2337 CenterY=39 CenterZ=0 NormalX=0 NormalY=0 NormalZ=1 AngleXU=0 Radius=1.5 StartAngle=4.71485 EndAngle=7.85398
    g18: ArcOfCircle CenterX=-16.2837 CenterY=27.25 CenterZ=0 NormalX=0 NormalY=0 NormalZ=1 AngleXU=0 Radius=1.5 StartAngle=4.71485 EndAngle=7.85398
    g19: ArcOfCircle CenterX=-18.2337 CenterY=33 CenterZ=0 NormalX=0 NormalY=0 NormalZ=1 AngleXU=0 Radius=1.5 StartAngle=4.71485 EndAngle=7.85398
    g20: ArcOfCircle CenterX=-11.49 CenterY=21.5 CenterZ=0 NormalX=0 NormalY=0 NormalZ=1 AngleXU=0 Radius=1.5 StartAngle=4.71239 EndAngle=7.85398
    g21: ArcOfCircle CenterX=-1.5 CenterY=4.25 CenterZ=0 NormalX=0 NormalY=0 NormalZ=1 AngleXU=0 Radius=1.5 StartAngle=4.71239 EndAngle=7.85398
    g22: ArcOfCircle CenterX=-1.5 CenterY=10 CenterZ=0 NormalX=0 NormalY=0 NormalZ=1 AngleXU=0 Radius=1.5 StartAngle=4.71239 EndAngle=7.85398
    g23: ArcOfCircle CenterX=-1.5 CenterY=15.75 CenterZ=0 NormalX=0 NormalY=0 NormalZ=1 AngleXU=0 Radius=1.5 StartAngle=4.71239 EndAngle=7.85398
    g24: LineSegment StartX=-49.19 StartY=69.25 StartZ=0 EndX=-1.5 EndY=69.25 EndZ=0
    g25: LineSegment StartX=-49.19 StartY=66.25 StartZ=0 EndX=-1.5 EndY=66.25 EndZ=0
    g26: LineSegment StartX=-49.19 StartY=63.5 StartZ=0 EndX=-1.5 EndY=63.5 EndZ=0
    g27: LineSegment StartX=-49.19 StartY=60.5 StartZ=0 EndX=-1.5 EndY=60.5 EndZ=0
    g28: LineSegment StartX=-49.19 StartY=57.75 StartZ=0 EndX=-1.5 EndY=57.75 EndZ=0
    g29: LineSegment StartX=-49.19 StartY=54.75 StartZ=0 EndX=-1.5 EndY=54.75 EndZ=0
    g30: LineSegment StartX=-49.19 StartY=52 StartZ=0 EndX=-11.49 EndY=52 EndZ=0
    g31: LineSegment StartX=-49.19 StartY=49 StartZ=0 EndX=-11.49 EndY=49 EndZ=0
    g32: LineSegment StartX=-49.19 StartY=46.25 StartZ=0 EndX=-16.28 EndY=46.25 EndZ=0
    g33: LineSegment StartX=-49.19 StartY=43.25 StartZ=0 EndX=-16.28 EndY=43.25 EndZ=0
    g34: LineSegment StartX=-49.19 StartY=40.5 StartZ=0 EndX=-18.2337 EndY=40.5 EndZ=0
    g35: LineSegment StartX=-49.19 StartY=37.5 StartZ=0 EndX=-18.23 EndY=37.5 EndZ=0
    g36: LineSegment StartX=-49.19 StartY=34.5 StartZ=0 EndX=-18.2337 EndY=34.5 EndZ=0
    g37: LineSegment StartX=-49.19 StartY=31.5 StartZ=0 EndX=-18.23 EndY=31.5 EndZ=0
    g38: LineSegment StartX=-49.19 StartY=28.75 StartZ=0 EndX=-16.2837 EndY=28.75 EndZ=0
    g39: LineSegment StartX=-49.19 StartY=25.75 StartZ=0 EndX=-16.28 EndY=25.75 EndZ=0
    g40: LineSegment StartX=-49.19 StartY=23 StartZ=0 EndX=-11.49 EndY=23 EndZ=0
    g41: LineSegment StartX=-49.19 StartY=20 StartZ=0 EndX=-11.49 EndY=20 EndZ=0
    g42: LineSegment StartX=-49.19 StartY=17.25 StartZ=0 EndX=-1.5 EndY=17.25 EndZ=0
    g43: LineSegment StartX=-49.19 StartY=14.25 StartZ=0 EndX=-1.5 EndY=14.25 EndZ=0
    g44: LineSegment StartX=-49.19 StartY=11.5 StartZ=0 EndX=-1.5 EndY=11.5 EndZ=0
    g45: LineSegment StartX=-49.19 StartY=8.5 StartZ=0 EndX=-1.5 EndY=8.5 EndZ=0
    g46: LineSegment StartX=-49.19 StartY=5.75 StartZ=0 EndX=-1.5 EndY=5.75 EndZ=0
    g47: LineSegment StartX=-49.19 StartY=2.75 StartZ=0 EndX=-1.5 EndY=2.75 EndZ=0
  constraints (120):
    c: Vertical(g0)
    c: Distance(g0) = 3
    c: Block(g0)
    c: Vertical(g1)
    c: Distance(g1) = 3
    c: Vertical(g2)
    c: Equal(g0,g2) = 3
    c: Block(g2)
    c: Vertical(g3)
    c: Equal(g1,g3) = 3
    c: Vertical(g4)
    c: Equal(g0,g4) = 3
    c: Block(g4)
    c: Vertical(g5)
    c: Equal(g1,g5) = 3
    c: Vertical(g6)
    c: Equal(g0,g6) = 3
    c: Block(g6)
    c: Vertical(g7)
    c: Equal(g1,g7) = 3
    c: Vertical(g8)
    c: Equal(g0,g8) = 3
    c: Block(g8)
    c: Vertical(g9)
    c: Equal(g1,g9) = 3
    c: Vertical(g10)
    c: Equal(g0,g10) = 3
    c: Block(g10)
    c: Vertical(g11)
    c: Equal(g1,g11) = 3
    c: Block(g12)
    c: Block(g13)
    c: Block(g14)
    c: Block(g15)
    c: Block(g16)
    c: Block(g17)
    c: Block(g18)
    c: Block(g19)
    c: Block(g20)
    c: Block(g21)
    c: Block(g22)
    c: Block(g23)
    c: Block(g11)
    c: Block(g9)
    c: Block(g7)
    c: Block(g5)
    c: Block(g3)
    c: Block(g1)
    c: Coincident(g24,g0)
    c: Coincident(g24,g12)
    c: Horizontal(g24)
    c: Coincident(g25,g0)
    c: Coincident(g25,g12)
    c: Horizontal(g25)
    c: Coincident(g26,g1)
    c: Coincident(g26,g13)
    c: Horizontal(g26)
    c: Coincident(g27,g1)
    c: Coincident(g27,g13)
    c: Horizontal(g27)
    c: Coincident(g28,g2)
    c: Coincident(g28,g14)
    c: Horizontal(g28)
    c: Coincident(g29,g2)
    c: Coincident(g29,g14)
    c: Horizontal(g29)
    c: Coincident(g30,g3)
    c: Coincident(g30,g15)
    c: Horizontal(g30)
    c: Coincident(g31,g3)
    c: Coincident(g31,g15)
    c: Horizontal(g31)
    c: Coincident(g32,g4)
    c: Coincident(g32,g16)
    c: Horizontal(g32)
    c: Coincident(g33,g4)
    c: Coincident(g33,g16)
    c: Horizontal(g33)
    c: Coincident(g34,g5)
    c: Coincident(g34,g17)
    c: Horizontal(g34)
    c: Coincident(g35,g5)
    c: Coincident(g35,g17)
    c: Horizontal(g35)
    c: Coincident(g36,g6)
    c: Coincident(g36,g19)
    c: Horizontal(g36)
    c: Coincident(g37,g6)
    c: Coincident(g37,g19)
    c: Horizontal(g37)
    c: Coincident(g38,g7)
    c: Coincident(g38,g18)
    c: Horizontal(g38)
    c: Coincident(g39,g7)
    c: Coincident(g39,g18)
    c: Horizontal(g39)
    c: Coincident(g40,g8)
    c: Coincident(g40,g20)
    c: Horizontal(g40)
    c: Coincident(g41,g8)
    c: Coincident(g41,g20)
    c: Horizontal(g41)
    c: Coincident(g42,g9)
    c: Coincident(g42,g23)
    c: Horizontal(g42)
    c: Coincident(g43,g9)
    c: Coincident(g43,g23)
    c: Horizontal(g43)
    c: Coincident(g44,g10)
    c: Coincident(g44,g22)
    c: Horizontal(g44)
    c: Coincident(g45,g10)
    c: Coincident(g45,g22)
    c: Horizontal(g45)
    c: Coincident(g46,g11)
    c: Coincident(g46,g21)
    c: Horizontal(g46)
    c: Coincident(g47,g11)
    c: Coincident(g47,g21)
    c: Horizontal(g47)
FEATURE [Part::Extrusion] Extrude046
  Base = -> Sketch055
  Dir = (1,0,0)
  DirMode = 2
  FaceMakerClass = Part::FaceMakerBullseye
  LengthFwd = 23
  LengthRev = 0
  Placement = pos=(-19,0,0) rot=(0,0,1;0rad)
  Solid = true
  Symmetric = false
FEATURE [Part::Fillet] Fillet038  label="removeToCreateVentalationHoles001"
  Base = -> Extrude046
  Edges = <same value as first occurrence — deduplicated (x6 in doc)>
  Placement = pos=(7,0,0) rot=(0,0,1;0rad)
FEATURE [Sketcher::SketchObject] Sketch056  label="topSketch014"
  FullyConstrained = true
  sketch-geometry (22):
    g0: LineSegment StartX=5.21097e-06 StartY=3 StartZ=0 EndX=5.21097e-06 EndY=19 EndZ=0
    g1: ArcOfCircle CenterX=19 CenterY=19 CenterZ=0 NormalX=0 NormalY=0 NormalZ=1 AngleXU=0 Radius=19 StartAngle=1.5708 EndAngle=3.14159
    g2: ArcOfCircle CenterX=19 CenterY=19 CenterZ=0 NormalX=0 NormalY=0 NormalZ=1 AngleXU=0 Radius=16 StartAngle=1.5708 EndAngle=3.14159
    g3: LineSegment StartX=114 StartY=35 StartZ=0 EndX=19 EndY=35 EndZ=0
    g4: LineSegment StartX=5.21097e-06 StartY=3 StartZ=0 EndX=5.21097e-06 EndY=0 EndZ=0
    g5: LineSegment StartX=3 StartY=0 StartZ=0 EndX=5.21097e-06 EndY=0 EndZ=0
    g6: LineSegment StartX=3 StartY=19 StartZ=0 EndX=3 EndY=0 EndZ=0
    g7: LineSegment StartX=19 StartY=38 StartZ=0 EndX=124 EndY=38 EndZ=0
    g8: Circle CenterX=119 CenterY=35 CenterZ=0 NormalX=0 NormalY=0 NormalZ=1 AngleXU=0 Radius=1
    g9: Circle CenterX=121 CenterY=35 CenterZ=0 NormalX=0 NormalY=0 NormalZ=1 AngleXU=0 Radius=1
    g10: Circle CenterX=121 CenterY=33 CenterZ=0 NormalX=0 NormalY=0 NormalZ=1 AngleXU=0 Radius=1
    g11: BSplineCurve PolesCount=3 KnotsCount=2 Degree=2 IsPeriodic=0
    g12: GeomPoint X=119 Y=35 Z=0
    g13: GeomPoint X=121 Y=33 Z=0
    g14: LineSegment StartX=119 StartY=35 StartZ=0 EndX=114 EndY=35 EndZ=0
    g15: ArcOfCircle CenterX=105 CenterY=19 CenterZ=0 NormalX=0 NormalY=0 NormalZ=1 AngleXU=0 Radius=16 StartAngle=5.60905 EndAngle=6.28319
    g16: LineSegment StartX=121 StartY=33 StartZ=0 EndX=121 EndY=19 EndZ=0
    g17: LineSegment StartX=117.5 StartY=9.01251 StartZ=0 EndX=121.163 EndY=9.0125 EndZ=0
    g18: ArcOfCircle CenterX=105 CenterY=19 CenterZ=0 NormalX=0 NormalY=0 NormalZ=1 AngleXU=0 Radius=20.6155 StartAngle=5.7297 EndAngle=6.28319
    g19: LineSegment StartX=121.163 StartY=9.0125 StartZ=0 EndX=122.538 EndY=8.16329 EndZ=0
    g20: LineSegment StartX=124 StartY=38 StartZ=0 EndX=125.616 EndY=38 EndZ=0
    g21: LineSegment StartX=125.616 StartY=19 StartZ=0 EndX=125.616 EndY=38 EndZ=0
  constraints (49):
    c: Vertical(g0)
    c: Block(g0)
    c: Coincident(g1,g0)
    c: Block(g1)
    c: Coincident(g2,g1)
    c: Block(g2)
    c: Coincident(g3,g2)
    c: Horizontal(g3)
    c: Tangent(g3,g2)
    c: Coincident(g4,g0)
    c: Distance(g4) = 3
    c: Vertical(g4)
    c: Coincident(g5,g4)
    c: Horizontal(g5)
    c: Coincident(g6,g2)
    c: Coincident(g6,g5)
    c: Vertical(g6)
    c: Horizontal(g7)
    c: Distance(g7) = 105
    c: Coincident(g7,g1)
    c: Block(g3)
    c: Weight(g8) = 1
    c: Equal(g8,g9)
    c: Equal(g8,g10)
    c: InternalAlignment(g8,g11)
    c: InternalAlignment(g9,g11)
    c: InternalAlignment(g10,g11)
    c: InternalAlignment(g12,g11)
    c: InternalAlignment(g13,g11)
    c: Block(g11)
    c: Coincident(g14,g11)
    c: Coincident(g14,g3)
    c: Horizontal(g14)
    c: Block(g15)
    c: Coincident(g16,g11)
    c: Coincident(g16,g15)
    c: Vertical(g16)
    c: Distance(g16) = 14
    c: Coincident(g17,g15)
    c: Block(g18)
    c: Coincident(g19,g18)
    c: Coincident(g20,g7)
    c: Horizontal(g20)
    c: Vertical(g21)
    c: Coincident(g20,g21)
    c: Block(g20)
    c: Block(g21)
    c: Block(g19)
    c: Block(g17)
FEATURE [Part::Box] Box026  label="removeToCreteHoleForPlugHousing032"
  AttacherType = Attacher::AttachEngine3D
  Height = 28.6
  Length = 10
  Placement = pos=(-2,0,21.7) rot=(0,0,1;0rad)
  Width = 19
FEATURE [Part::Feature] Face109 .. Face112  x4 (patterned run collapsed; names and placements below)
  shape: bbox 3.5 x 17.8 x 2e-07 mm, 1 faces, 0 solids (baked)
FEATURE [Part::Revolution] Revolve117  label="removeToCreateScrewAndThreadedInsertHole045"
  Angle = 360
  Axis = (0,1,0)
  Base = (0,0,0)
  FaceMakerClass = Part::FaceMakerBullseye
  Placement = pos=(62.3,30.3,19.7) rot=(0,0,1;0rad)
  Solid = false
  Source = -> Face109
  Symmetric = false
FEATURE [Part::Revolution] Revolve118  label="removeToCreateScrewAndThreadedInsertHole046"
  Angle = 360
  Axis = (0,1,0)
  Base = (0,0,0)
  FaceMakerClass = Part::FaceMakerBullseye
  Placement = pos=(62.3,30.3,51.7) rot=(0,0,1;0rad)
  Solid = false
  Source = -> Face110
  Symmetric = false
FEATURE [Part::Revolution] Revolve119  label="removeToCreateScrewAndThreadedInsertHole047"
  Angle = 360
  Axis = (0,1,0)
  Base = (0,0,0)
  FaceMakerClass = Part::FaceMakerBullseye
  Placement = pos=(30.3,30.3,19.7) rot=(0,0,1;0rad)
  Solid = false
  Source = -> Face111
  Symmetric = false
FEATURE [Part::Revolution] Revolve120  label="removeToCreateScrewAndThreadedInsertHole048"
  Angle = 360
  Axis = (0,1,0)
  Base = (0,0,0)
  FaceMakerClass = Part::FaceMakerBullseye
  Placement = pos=(30.3,30.3,51.7) rot=(0,0,1;0rad)
  Solid = false
  Source = -> Face112
  Symmetric = false
FEATURE [Part::MultiFuse] Fusion087  label="createThreadedInsertHolesForFan005"
  Shapes = -> [Revolve117,Revolve118,Revolve119,Revolve120]
FEATURE [Part::Extrusion] Extrude047
  Base = -> Sketch056
  Dir = (0,0,1)
  DirMode = 2
  FaceMakerClass = Part::FaceMakerBullseye
  LengthFwd = 72
  LengthRev = 0
  Solid = true
  Symmetric = false
FEATURE [Part::Fillet] Fillet039  label="top019"
  Base = -> Extrude047
  Edges = 1 edges r=2: [Edge35]
FEATURE [Sketcher::SketchObject] Sketch057
  FullyConstrained = false
  Placement = pos=(0,0,0) rot=(1,0,0;1.5708rad)
  sketch-geometry (24):
    g0: ArcOfCircle CenterX=-4 CenterY=-10.5 CenterZ=0 NormalX=0 NormalY=0 NormalZ=1 AngleXU=0 Radius=1.5 StartAngle=6e-16 EndAngle=3.14159
    g1: ArcOfCircle CenterX=-34.2 CenterY=-10.5 CenterZ=0 NormalX=0 NormalY=0 NormalZ=1 AngleXU=0 Radius=1.5 StartAngle=0 EndAngle=3.14159
    g2: ArcOfCircle CenterX=-34.2 CenterY=-27.7 CenterZ=0 NormalX=0 NormalY=0 NormalZ=1 AngleXU=0 Radius=1.5 StartAngle=3.14159 EndAngle=6.28319
    g3: ArcOfCircle CenterX=-4 CenterY=-27.7 CenterZ=0 NormalX=0 NormalY=0 NormalZ=1 AngleXU=0 Radius=1.5 StartAngle=3.1416 EndAngle=6.28319
    g4: ArcOfCircle CenterX=-10 CenterY=-4.3 CenterZ=0 NormalX=0 NormalY=0 NormalZ=1 AngleXU=0 Radius=1.5 StartAngle=2e-16 EndAngle=3.14159
    g5: ArcOfCircle CenterX=-16.1 CenterY=-1.8 CenterZ=0 NormalX=0 NormalY=0 NormalZ=1 AngleXU=0 Radius=1.5 StartAngle=5e-16 EndAngle=3.14159
    g6: ArcOfCircle CenterX=-22.1 CenterY=-1.8 CenterZ=0 NormalX=0 NormalY=0 NormalZ=1 AngleXU=0 Radius=1.5 StartAngle=5e-16 EndAngle=3.14159
    g7: ArcOfCircle CenterX=-28.2 CenterY=-4.3 CenterZ=0 NormalX=0 NormalY=0 NormalZ=1 AngleXU=0 Radius=1.5 StartAngle=2e-16 EndAngle=3.14159
    g8: ArcOfCircle CenterX=-10 CenterY=-33.9 CenterZ=0 NormalX=0 NormalY=0 NormalZ=1 AngleXU=0 Radius=1.5 StartAngle=3.14159 EndAngle=6.28319
    g9: ArcOfCircle CenterX=-16.1 CenterY=-36.4 CenterZ=0 NormalX=0 NormalY=0 NormalZ=1 AngleXU=0 Radius=1.5 StartAngle=3.14159 EndAngle=6.28319
    g10: ArcOfCircle CenterX=-22.1 CenterY=-36.4 CenterZ=0 NormalX=0 NormalY=0 NormalZ=1 AngleXU=0 Radius=1.5 StartAngle=3.14159 EndAngle=6.28319
    g11: ArcOfCircle CenterX=-28.2 CenterY=-33.9 CenterZ=0 NormalX=0 NormalY=0 NormalZ=1 AngleXU=0 Radius=1.5 StartAngle=3.14159 EndAngle=6.28319
    g12: LineSegment StartX=-35.7 StartY=-10.5 StartZ=0 EndX=-35.7 EndY=-27.7 EndZ=0
    g13: LineSegment StartX=-32.7 StartY=-10.5 StartZ=0 EndX=-32.7 EndY=-27.7 EndZ=0
    g14: LineSegment StartX=-29.7 StartY=-33.9 StartZ=0 EndX=-29.7 EndY=-4.3 EndZ=0
    g15: LineSegment StartX=-26.7 StartY=-33.9 StartZ=0 EndX=-26.7 EndY=-4.3 EndZ=0
    g16: LineSegment StartX=-2.5 StartY=-10.5 StartZ=0 EndX=-2.5 EndY=-27.7 EndZ=0
    g17: LineSegment StartX=-8.5 StartY=-4.3 StartZ=0 EndX=-8.5 EndY=-33.9 EndZ=0
    g18: LineSegment StartX=-5.5 StartY=-10.5 StartZ=0 EndX=-5.5 EndY=-27.7 EndZ=0
    g19: LineSegment StartX=-11.5 StartY=-4.3 StartZ=0 EndX=-11.5 EndY=-33.9 EndZ=0
    g20: LineSegment StartX=-14.6 StartY=-1.8 StartZ=0 EndX=-14.6 EndY=-36.4 EndZ=0
    g21: LineSegment StartX=-17.6 StartY=-1.8 StartZ=0 EndX=-17.6 EndY=-36.4 EndZ=0
    g22: LineSegment StartX=-20.6 StartY=-36.4 StartZ=0 EndX=-20.6 EndY=-1.8 EndZ=0
    g23: LineSegment StartX=-23.6 StartY=-1.8 StartZ=0 EndX=-23.6 EndY=-36.4 EndZ=0
  constraints (48):
    c: Block(g0)
    c: Block(g1)
    c: Block(g2)
    c: Block(g3)
    c: Block(g4)
    c: Block(g5)
    c: Block(g6)
    c: Block(g7)
    c: Block(g8)
    c: Block(g9)
    c: Block(g10)
    c: Block(g11)
    c: Coincident(g12,g1)
    c: Coincident(g12,g2)
    c: Vertical(g12)
    c: Coincident(g13,g1)
    c: Coincident(g13,g2)
    c: Vertical(g13)
    c: Coincident(g14,g11)
    c: Coincident(g14,g7)
    c: Vertical(g14)
    c: Coincident(g15,g11)
    c: Coincident(g15,g7)
    c: Vertical(g15)
    c: Coincident(g16,g0)
    c: Coincident(g16,g3)
    c: Vertical(g16)
    c: Coincident(g17,g4)
    c: Coincident(g17,g8)
    c: Vertical(g17)
    c: Coincident(g18,g0)
    c: Coincident(g18,g3)
    c: Vertical(g18)
    c: Coincident(g19,g4)
    c: Coincident(g19,g8)
    c: Vertical(g19)
    c: Coincident(g20,g5)
    c: Coincident(g20,g9)
    c: Vertical(g20)
    c: Coincident(g21,g5)
    c: Coincident(g21,g9)
    c: Vertical(g21)
    c: Coincident(g22,g10)
    c: Coincident(g22,g6)
    c: Vertical(g22)
    c: Coincident(g23,g6)
    c: Coincident(g23,g10)
    c: Vertical(g23)
FEATURE [Part::Extrusion] Extrude048  label="removeToCreateFanGrillHoles004"
  Base = -> Sketch057
  Dir = (0,-1,6e-16)
  DirMode = 2
  FaceMakerClass = Part::FaceMakerBullseye
  LengthFwd = 10
  LengthRev = 0
  Placement = pos=(65.4,44,54.82) rot=(0,0,1;0rad)
  Solid = true
  Symmetric = false
FEATURE [Part::Cut] Cut040  label="top021"
  Base = -> Fillet039
  Tool = -> Extrude048
FEATURE [Part::Cylinder] Cylinder041  label="removeToCreteHoleForPlugHousing034"
  Angle = 360
  AttacherType = Attacher::AttachEngine3D
  Height = 20
  Placement = pos=(-2,19,36) rot=(0,1,0;1.5708rad)
  Radius = 14.3
FEATURE [Part::MultiFuse] Fusion089  label="removeToCreteHoleForPlugHousing035"
  Shapes = -> [Box026,Cylinder041]
FEATURE [Part::Cylinder] Cylinder042
  Angle = 360
  AttacherType = Attacher::AttachEngine3D
  Height = 20
  Placement = pos=(0,0,36.15) rot=(0,0,1;0rad)
  Radius = 14.3
FEATURE [Part::Cylinder] Cylinder043
  Angle = 360
  AttacherType = Attacher::AttachEngine3D
  Height = 10
  Placement = pos=(0,0,36.15) rot=(0,0,1;0rad)
  Radius = 4
FEATURE [Part::Box] Box027  label="removeToCreteHoleForPlugHousing036"
  AttacherType = Attacher::AttachEngine3D
  Height = 28.6
  Length = 20
  Placement = pos=(106.15,0,21.7) rot=(0,0,1;0rad)
  Width = 19
FEATURE [Part::Cut] Cut041  label="top022"
  Base = -> Cut040
  Tool = -> Fusion087
FEATURE [Part::Cut] Cut039  label="top020"
  Base = -> Cut041
  Tool = -> Fusion089
FEATURE [Part::MultiFuse] Fusion090  label="removeToCreteHoleForPlugHousing037"
  Placement = pos=(70,19,36) rot=(0,1,0;1.5708rad)
  Shapes = -> [Cylinder042,Cylinder043]
FEATURE [Part::MultiFuse] Fusion088  label="removeToCreteHoleForPlugHousing033"
  Shapes = -> [Box027,Fusion090]
FEATURE [Part::Cut] Cut042  label="removeToCreteHoleForPlugHousing038"
  Base = -> Cut039
  Tool = -> Fusion088
FEATURE [Part::MultiFuse] Fusion091  label="removeFromTop"
  Shapes = -> [Fillet038,Fusion085,Fusion084,Fusion083,Extrude045]
FEATURE [Part::Cut] Cut043  label="REAL TOP ====="
  Base = -> Fillet036
  Tool = -> Fusion091
FEATURE [Part::MultiFuse] Fusion092  label="caseScrewPillarBracket016"
  Shapes = -> [Extrude030,Extrude031,Extrude032,Extrude033,Extrude034,Extrude035,Extrude036,Extrude037,Box013,Box014]
FEATURE [Sketcher::SketchObject] Sketch058  label="topSketch015"
  FullyConstrained = true
  sketch-geometry (20):
    g0: LineSegment StartX=5.21097e-06 StartY=3 StartZ=0 EndX=5.21097e-06 EndY=19 EndZ=0
    g1: ArcOfCircle CenterX=19 CenterY=19 CenterZ=0 NormalX=0 NormalY=0 NormalZ=1 AngleXU=0 Radius=19 StartAngle=1.5708 EndAngle=3.14159
    g2: ArcOfCircle CenterX=19 CenterY=19 CenterZ=0 NormalX=0 NormalY=0 NormalZ=1 AngleXU=0 Radius=16 StartAngle=1.5708 EndAngle=3.14159
    g3: LineSegment StartX=114 StartY=35 StartZ=0 EndX=19 EndY=35 EndZ=0
    g4: LineSegment StartX=5.21097e-06 StartY=3 StartZ=0 EndX=5.21097e-06 EndY=0 EndZ=0
    g5: LineSegment StartX=3 StartY=0 StartZ=0 EndX=5.21097e-06 EndY=0 EndZ=0
    g6: LineSegment StartX=3 StartY=19 StartZ=0 EndX=3 EndY=0 EndZ=0
    g7: LineSegment StartX=19 StartY=38 StartZ=0 EndX=124 EndY=38 EndZ=0
    g8: Circle CenterX=119 CenterY=35 CenterZ=0 NormalX=0 NormalY=0 NormalZ=1 AngleXU=0 Radius=1
    g9: Circle CenterX=121 CenterY=35 CenterZ=0 NormalX=0 NormalY=0 NormalZ=1 AngleXU=0 Radius=1
    g10: Circle CenterX=121 CenterY=33 CenterZ=0 NormalX=0 NormalY=0 NormalZ=1 AngleXU=0 Radius=1
    g11: BSplineCurve PolesCount=3 KnotsCount=2 Degree=2 IsPeriodic=0
    g12: GeomPoint X=119 Y=35 Z=0
    g13: GeomPoint X=121 Y=33 Z=0
    g14: LineSegment StartX=119 StartY=35 StartZ=0 EndX=114 EndY=35 EndZ=0
    g15: ArcOfCircle CenterX=105 CenterY=19 CenterZ=0 NormalX=0 NormalY=0 NormalZ=1 AngleXU=0 Radius=19 StartAngle=5.7297 EndAngle=6.28319
    g16: ArcOfCircle CenterX=105 CenterY=19 CenterZ=0 NormalX=0 NormalY=0 NormalZ=1 AngleXU=0 Radius=16 StartAngle=5.60905 EndAngle=6.28319
    g17: LineSegment StartX=121 StartY=33 StartZ=0 EndX=121 EndY=19 EndZ=0
    g18: LineSegment StartX=124 StartY=38 StartZ=0 EndX=124 EndY=19 EndZ=0
    g19: LineSegment StartX=117.5 StartY=9.01251 StartZ=0 EndX=121.163 EndY=9.0125 EndZ=0
  constraints (46):
    c: Vertical(g0)
    c: Block(g0)
    c: Coincident(g1,g0)
    c: Block(g1)
    c: Coincident(g2,g1)
    c: Block(g2)
    c: Coincident(g3,g2)
    c: Horizontal(g3)
    c: Tangent(g3,g2)
    c: Coincident(g4,g0)
    c: Distance(g4) = 3
    c: Vertical(g4)
    c: Coincident(g5,g4)
    c: Horizontal(g5)
    c: Coincident(g6,g2)
    c: Coincident(g6,g5)
    c: Vertical(g6)
    c: Horizontal(g7)
    c: Distance(g7) = 105
    c: Coincident(g7,g1)
    c: Block(g3)
    c: Weight(g8) = 1
    c: Equal(g8,g9)
    c: Equal(g8,g10)
    c: InternalAlignment(g8,g11)
    c: InternalAlignment(g9,g11)
    c: InternalAlignment(g10,g11)
    c: InternalAlignment(g12,g11)
    c: InternalAlignment(g13,g11)
    c: Block(g11)
    c: Coincident(g14,g11)
    c: Coincident(g14,g3)
    c: Horizontal(g14)
    c: Block(g15)
    c: Coincident(g16,g15)
    c: Block(g16)
    c: Coincident(g17,g11)
    c: Coincident(g17,g16)
    c: Vertical(g17)
    c: Distance(g17) = 14
    c: Coincident(g18,g7)
    c: Coincident(g18,g15)
    c: Vertical(g18)
    c: Distance(g18) = 19
    c: Coincident(g19,g16)
    c: Coincident(g19,g15)
FEATURE [Part::Extrusion] Extrude049  label="top023"
  Base = -> Sketch058
  Dir = (0,0,1)
  DirMode = 2
  FaceMakerClass = Part::FaceMakerBullseye
  LengthFwd = 72
  LengthRev = 0
  Solid = true
  Symmetric = false
FEATURE [Sketcher::SketchObject] Sketch059
  FullyConstrained = true
  MapMode = 3
  Placement = pos=(0,0,0) rot=(1,0,0;1.5708rad)
  Support = -> [Extrude049]
  sketch-geometry (8):
    g0: Circle CenterX=80.351 CenterY=-67.6202 CenterZ=0 NormalX=0 NormalY=0 NormalZ=1 AngleXU=0 Radius=2
    g1: Circle CenterX=80.351 CenterY=-67.6202 CenterZ=0 NormalX=0 NormalY=0 NormalZ=1 AngleXU=0 Radius=3
    g2: Circle CenterX=80.351 CenterY=-4.92017 CenterZ=0 NormalX=0 NormalY=0 NormalZ=1 AngleXU=0 Radius=2
    g3: Circle CenterX=80.351 CenterY=-4.92017 CenterZ=0 NormalX=0 NormalY=0 NormalZ=1 AngleXU=0 Radius=3
    g4: Circle CenterX=23.851 CenterY=-4.92017 CenterZ=0 NormalX=0 NormalY=0 NormalZ=1 AngleXU=0 Radius=2
    g5: Circle CenterX=23.851 CenterY=-4.92017 CenterZ=0 NormalX=0 NormalY=0 NormalZ=1 AngleXU=0 Radius=3
    g6: Circle CenterX=23.851 CenterY=-67.6202 CenterZ=0 NormalX=0 NormalY=0 NormalZ=1 AngleXU=0 Radius=2
    g7: Circle CenterX=23.851 CenterY=-67.6202 CenterZ=0 NormalX=0 NormalY=0 NormalZ=1 AngleXU=0 Radius=3
  constraints (8):
    c: Block(g3)
    c: Block(g2)
    c: Block(g1)
    c: Block(g0)
    c: Block(g6)
    c: Block(g7)
    c: Block(g4)
    c: Block(g5)
FEATURE [Sketcher::SketchObject] Sketch060
  FullyConstrained = true
  MapMode = 3
  Placement = pos=(0,0,0) rot=(1,0,0;1.5708rad)
  Support = -> [Extrude049]
  sketch-geometry (8):
    g0: Circle CenterX=80.351 CenterY=-67.6202 CenterZ=0 NormalX=0 NormalY=0 NormalZ=1 AngleXU=0 Radius=3
    g1: Circle CenterX=80.351 CenterY=-4.92017 CenterZ=0 NormalX=0 NormalY=0 NormalZ=1 AngleXU=0 Radius=3
    g2: Circle CenterX=23.851 CenterY=-4.92017 CenterZ=0 NormalX=0 NormalY=0 NormalZ=1 AngleXU=0 Radius=3
    g3: Circle CenterX=23.851 CenterY=-67.6202 CenterZ=0 NormalX=0 NormalY=0 NormalZ=1 AngleXU=0 Radius=3
    g4: Circle CenterX=23.851 CenterY=-67.6202 CenterZ=0 NormalX=0 NormalY=0 NormalZ=1 AngleXU=0 Radius=5
    g5: Circle CenterX=80.351 CenterY=-67.6202 CenterZ=0 NormalX=0 NormalY=0 NormalZ=1 AngleXU=0 Radius=5
    g6: Circle CenterX=23.851 CenterY=-4.92017 CenterZ=0 NormalX=0 NormalY=0 NormalZ=1 AngleXU=0 Radius=5
    g7: Circle CenterX=80.351 CenterY=-4.92017 CenterZ=0 NormalX=0 NormalY=0 NormalZ=1 AngleXU=0 Radius=5
  constraints (8):
    c: Block(g1)
    c: Block(g0)
    c: Block(g3)
    c: Block(g2)
    c: Block(g5)
    c: Block(g4)
    c: Block(g6)
    c: Block(g7)
FEATURE [Sketcher::SketchObject] Sketch061
  FullyConstrained = true
  MapMode = 3
  Placement = pos=(0,0,0) rot=(1,0,0;1.5708rad)
  sketch-geometry (8):
    g0: Circle CenterX=80.351 CenterY=-67.6202 CenterZ=0 NormalX=0 NormalY=0 NormalZ=1 AngleXU=0 Radius=3
    g1: Circle CenterX=80.351 CenterY=-4.92017 CenterZ=0 NormalX=0 NormalY=0 NormalZ=1 AngleXU=0 Radius=3
    g2: Circle CenterX=23.851 CenterY=-4.92017 CenterZ=0 NormalX=0 NormalY=0 NormalZ=1 AngleXU=0 Radius=3
    g3: Circle CenterX=23.851 CenterY=-67.6202 CenterZ=0 NormalX=0 NormalY=0 NormalZ=1 AngleXU=0 Radius=3
    g4: Circle CenterX=23.851 CenterY=-67.6202 CenterZ=0 NormalX=0 NormalY=0 NormalZ=1 AngleXU=0 Radius=5
    g5: Circle CenterX=80.351 CenterY=-67.6202 CenterZ=0 NormalX=0 NormalY=0 NormalZ=1 AngleXU=0 Radius=5
    g6: Circle CenterX=23.851 CenterY=-4.92017 CenterZ=0 NormalX=0 NormalY=0 NormalZ=1 AngleXU=0 Radius=5
    g7: Circle CenterX=80.351 CenterY=-4.92017 CenterZ=0 NormalX=0 NormalY=0 NormalZ=1 AngleXU=0 Radius=5
  constraints (8):
    c: Block(g1)
    c: Block(g0)
    c: Block(g3)
    c: Block(g2)
    c: Block(g5)
    c: Block(g4)
    c: Block(g6)
    c: Block(g7)
FEATURE [Sketcher::SketchObject] Sketch062  label="topSketch016"
  FullyConstrained = true
  sketch-geometry (20):
    g0: LineSegment StartX=5.21097e-06 StartY=3 StartZ=0 EndX=5.21097e-06 EndY=19 EndZ=0
    g1: ArcOfCircle CenterX=19 CenterY=19 CenterZ=0 NormalX=0 NormalY=0 NormalZ=1 AngleXU=0 Radius=19 StartAngle=1.5708 EndAngle=3.14159
    g2: ArcOfCircle CenterX=19 CenterY=19 CenterZ=0 NormalX=0 NormalY=0 NormalZ=1 AngleXU=0 Radius=16 StartAngle=1.5708 EndAngle=3.14159
    g3: LineSegment StartX=114 StartY=35 StartZ=0 EndX=19 EndY=35 EndZ=0
    g4: LineSegment StartX=5.21097e-06 StartY=3 StartZ=0 EndX=5.21097e-06 EndY=0 EndZ=0
    g5: LineSegment StartX=3 StartY=0 StartZ=0 EndX=5.21097e-06 EndY=0 EndZ=0
    g6: LineSegment StartX=3 StartY=19 StartZ=0 EndX=3 EndY=0 EndZ=0
    g7: LineSegment StartX=19 StartY=38 StartZ=0 EndX=124 EndY=38 EndZ=0
    g8: Circle CenterX=119 CenterY=35 CenterZ=0 NormalX=0 NormalY=0 NormalZ=1 AngleXU=0 Radius=1
    g9: Circle CenterX=121 CenterY=35 CenterZ=0 NormalX=0 NormalY=0 NormalZ=1 AngleXU=0 Radius=1
    g10: Circle CenterX=121 CenterY=33 CenterZ=0 NormalX=0 NormalY=0 NormalZ=1 AngleXU=0 Radius=1
    g11: BSplineCurve PolesCount=3 KnotsCount=2 Degree=2 IsPeriodic=0
    g12: GeomPoint X=119 Y=35 Z=0
    g13: GeomPoint X=121 Y=33 Z=0
    g14: LineSegment StartX=119 StartY=35 StartZ=0 EndX=114 EndY=35 EndZ=0
    g15: ArcOfCircle CenterX=105 CenterY=19 CenterZ=0 NormalX=0 NormalY=0 NormalZ=1 AngleXU=0 Radius=19 StartAngle=5.7297 EndAngle=6.28319
    g16: ArcOfCircle CenterX=105 CenterY=19 CenterZ=0 NormalX=0 NormalY=0 NormalZ=1 AngleXU=0 Radius=16 StartAngle=5.60905 EndAngle=6.28319
    g17: LineSegment StartX=121 StartY=33 StartZ=0 EndX=121 EndY=19 EndZ=0
    g18: LineSegment StartX=124 StartY=38 StartZ=0 EndX=124 EndY=19 EndZ=0
    g19: LineSegment StartX=117.5 StartY=9.01251 StartZ=0 EndX=121.163 EndY=9.0125 EndZ=0
  constraints (46):
    c: Vertical(g0)
    c: Block(g0)
    c: Coincident(g1,g0)
    c: Block(g1)
    c: Coincident(g2,g1)
    c: Block(g2)
    c: Coincident(g3,g2)
    c: Horizontal(g3)
    c: Tangent(g3,g2)
    c: Coincident(g4,g0)
    c: Distance(g4) = 3
    c: Vertical(g4)
    c: Coincident(g5,g4)
    c: Horizontal(g5)
    c: Coincident(g6,g2)
    c: Coincident(g6,g5)
    c: Vertical(g6)
    c: Horizontal(g7)
    c: Distance(g7) = 105
    c: Coincident(g7,g1)
    c: Block(g3)
    c: Weight(g8) = 1
    c: Equal(g8,g9)
    c: Equal(g8,g10)
    c: InternalAlignment(g8,g11)
    c: InternalAlignment(g9,g11)
    c: InternalAlignment(g10,g11)
    c: InternalAlignment(g12,g11)
    c: InternalAlignment(g13,g11)
    c: Block(g11)
    c: Coincident(g14,g11)
    c: Coincident(g14,g3)
    c: Horizontal(g14)
    c: Block(g15)
    c: Coincident(g16,g15)
    c: Block(g16)
    c: Coincident(g17,g11)
    c: Coincident(g17,g16)
    c: Vertical(g17)
    c: Distance(g17) = 14
    c: Coincident(g18,g7)
    c: Coincident(g18,g15)
    c: Vertical(g18)
    c: Distance(g18) = 19
    c: Coincident(g19,g16)
    c: Coincident(g19,g15)
FEATURE [Part::Extrusion] Extrude053  label="top024"
  Base = -> Sketch062
  Dir = (0,0,1)
  DirMode = 2
  FaceMakerClass = Part::FaceMakerBullseye
  LengthFwd = 72
  LengthRev = 0
  Solid = true
  Symmetric = false
FEATURE [Sketcher::SketchObject] Sketch063
  FullyConstrained = true
  MapMode = 3
  Placement = pos=(0,0,0) rot=(1,0,0;1.5708rad)
  Support = -> [Extrude053]
  sketch-geometry (8):
    g0: Circle CenterX=80.351 CenterY=-67.6202 CenterZ=0 NormalX=0 NormalY=0 NormalZ=1 AngleXU=0 Radius=2
    g1: Circle CenterX=80.351 CenterY=-67.6202 CenterZ=0 NormalX=0 NormalY=0 NormalZ=1 AngleXU=0 Radius=3
    g2: Circle CenterX=80.351 CenterY=-4.92017 CenterZ=0 NormalX=0 NormalY=0 NormalZ=1 AngleXU=0 Radius=2
    g3: Circle CenterX=80.351 CenterY=-4.92017 CenterZ=0 NormalX=0 NormalY=0 NormalZ=1 AngleXU=0 Radius=3
    g4: Circle CenterX=23.851 CenterY=-4.92017 CenterZ=0 NormalX=0 NormalY=0 NormalZ=1 AngleXU=0 Radius=2
    g5: Circle CenterX=23.851 CenterY=-4.92017 CenterZ=0 NormalX=0 NormalY=0 NormalZ=1 AngleXU=0 Radius=3
    g6: Circle CenterX=23.851 CenterY=-67.6202 CenterZ=0 NormalX=0 NormalY=0 NormalZ=1 AngleXU=0 Radius=2
    g7: Circle CenterX=23.851 CenterY=-67.6202 CenterZ=0 NormalX=0 NormalY=0 NormalZ=1 AngleXU=0 Radius=3
  constraints (8):
    c: Block(g3)
    c: Block(g2)
    c: Block(g1)
    c: Block(g0)
    c: Block(g6)
    c: Block(g7)
    c: Block(g4)
    c: Block(g5)
FEATURE [Part::Extrusion] Extrude054
  Base = -> Sketch063
  Dir = (0,-1,2e-16)
  DirMode = 2
  FaceMakerClass = Part::FaceMakerBullseye
  LengthFwd = 6
  LengthRev = 0
  Placement = pos=(0,9,0) rot=(0,0,1;0rad)
  Solid = true
  Symmetric = false
FEATURE [Sketcher::SketchObject] Sketch064  label="topSketch017"
  FullyConstrained = true
  sketch-geometry (20):
    g0: LineSegment StartX=5.21097e-06 StartY=3 StartZ=0 EndX=5.21097e-06 EndY=19 EndZ=0
    g1: ArcOfCircle CenterX=19 CenterY=19 CenterZ=0 NormalX=0 NormalY=0 NormalZ=1 AngleXU=0 Radius=19 StartAngle=1.5708 EndAngle=3.14159
    g2: ArcOfCircle CenterX=19 CenterY=19 CenterZ=0 NormalX=0 NormalY=0 NormalZ=1 AngleXU=0 Radius=16 StartAngle=1.5708 EndAngle=3.14159
    g3: LineSegment StartX=114 StartY=35 StartZ=0 EndX=19 EndY=35 EndZ=0
    g4: LineSegment StartX=5.21097e-06 StartY=3 StartZ=0 EndX=5.21097e-06 EndY=0 EndZ=0
    g5: LineSegment StartX=3 StartY=0 StartZ=0 EndX=5.21097e-06 EndY=0 EndZ=0
    g6: LineSegment StartX=3 StartY=19 StartZ=0 EndX=3 EndY=0 EndZ=0
    g7: LineSegment StartX=19 StartY=38 StartZ=0 EndX=124 EndY=38 EndZ=0
    g8: Circle CenterX=119 CenterY=35 CenterZ=0 NormalX=0 NormalY=0 NormalZ=1 AngleXU=0 Radius=1
    g9: Circle CenterX=121 CenterY=35 CenterZ=0 NormalX=0 NormalY=0 NormalZ=1 AngleXU=0 Radius=1
    g10: Circle CenterX=121 CenterY=33 CenterZ=0 NormalX=0 NormalY=0 NormalZ=1 AngleXU=0 Radius=1
    g11: BSplineCurve PolesCount=3 KnotsCount=2 Degree=2 IsPeriodic=0
    g12: GeomPoint X=119 Y=35 Z=0
    g13: GeomPoint X=121 Y=33 Z=0
    g14: LineSegment StartX=119 StartY=35 StartZ=0 EndX=114 EndY=35 EndZ=0
    g15: ArcOfCircle CenterX=105 CenterY=19 CenterZ=0 NormalX=0 NormalY=0 NormalZ=1 AngleXU=0 Radius=19 StartAngle=5.7297 EndAngle=6.28319
    g16: ArcOfCircle CenterX=105 CenterY=19 CenterZ=0 NormalX=0 NormalY=0 NormalZ=1 AngleXU=0 Radius=16 StartAngle=5.60905 EndAngle=6.28319
    g17: LineSegment StartX=121 StartY=33 StartZ=0 EndX=121 EndY=19 EndZ=0
    g18: LineSegment StartX=124 StartY=38 StartZ=0 EndX=124 EndY=19 EndZ=0
    g19: LineSegment StartX=117.5 StartY=9.01251 StartZ=0 EndX=121.163 EndY=9.0125 EndZ=0
  constraints (46):
    c: Vertical(g0)
    c: Block(g0)
    c: Coincident(g1,g0)
    c: Block(g1)
    c: Coincident(g2,g1)
    c: Block(g2)
    c: Coincident(g3,g2)
    c: Horizontal(g3)
    c: Tangent(g3,g2)
    c: Coincident(g4,g0)
    c: Distance(g4) = 3
    c: Vertical(g4)
    c: Coincident(g5,g4)
    c: Horizontal(g5)
    c: Coincident(g6,g2)
    c: Coincident(g6,g5)
    c: Vertical(g6)
    c: Horizontal(g7)
    c: Distance(g7) = 105
    c: Coincident(g7,g1)
    c: Block(g3)
    c: Weight(g8) = 1
    c: Equal(g8,g9)
    c: Equal(g8,g10)
    c: InternalAlignment(g8,g11)
    c: InternalAlignment(g9,g11)
    c: InternalAlignment(g10,g11)
    c: InternalAlignment(g12,g11)
    c: InternalAlignment(g13,g11)
    c: Block(g11)
    c: Coincident(g14,g11)
    c: Coincident(g14,g3)
    c: Horizontal(g14)
    c: Block(g15)
    c: Coincident(g16,g15)
    c: Block(g16)
    c: Coincident(g17,g11)
    c: Coincident(g17,g16)
    c: Vertical(g17)
    c: Distance(g17) = 14
    c: Coincident(g18,g7)
    c: Coincident(g18,g15)
    c: Vertical(g18)
    c: Distance(g18) = 19
    c: Coincident(g19,g16)
    c: Coincident(g19,g15)
FEATURE [Sketcher::SketchObject] Sketch065
  FullyConstrained = true
  MapMode = 3
  Placement = pos=(0,0,0) rot=(1,0,0;1.5708rad)
  sketch-geometry (8):
    g0: Circle CenterX=80.351 CenterY=-67.6202 CenterZ=0 NormalX=0 NormalY=0 NormalZ=1 AngleXU=0 Radius=3
    g1: Circle CenterX=80.351 CenterY=-4.92017 CenterZ=0 NormalX=0 NormalY=0 NormalZ=1 AngleXU=0 Radius=3
    g2: Circle CenterX=23.851 CenterY=-4.92017 CenterZ=0 NormalX=0 NormalY=0 NormalZ=1 AngleXU=0 Radius=3
    g3: Circle CenterX=23.851 CenterY=-67.6202 CenterZ=0 NormalX=0 NormalY=0 NormalZ=1 AngleXU=0 Radius=3
    g4: Circle CenterX=23.851 CenterY=-67.6202 CenterZ=0 NormalX=0 NormalY=0 NormalZ=1 AngleXU=0 Radius=5
    g5: Circle CenterX=80.351 CenterY=-67.6202 CenterZ=0 NormalX=0 NormalY=0 NormalZ=1 AngleXU=0 Radius=5
    g6: Circle CenterX=23.851 CenterY=-4.92017 CenterZ=0 NormalX=0 NormalY=0 NormalZ=1 AngleXU=0 Radius=5
    g7: Circle CenterX=80.351 CenterY=-4.92017 CenterZ=0 NormalX=0 NormalY=0 NormalZ=1 AngleXU=0 Radius=5
  constraints (8):
    c: Block(g1)
    c: Block(g0)
    c: Block(g3)
    c: Block(g2)
    c: Block(g5)
    c: Block(g4)
    c: Block(g6)
    c: Block(g7)
FEATURE [Part::Extrusion] Extrude056
  Base = -> Sketch065
  Dir = (0,-1,2e-16)
  DirMode = 2
  FaceMakerClass = Part::FaceMakerBullseye
  LengthFwd = 2
  LengthRev = 0
  Solid = true
  Symmetric = false
FEATURE [Part::Extrusion] Extrude057  label="top025"
  Base = -> Sketch064
  Dir = (0,0,1)
  DirMode = 2
  FaceMakerClass = Part::FaceMakerBullseye
  LengthFwd = 72
  LengthRev = 0
  Solid = true
  Symmetric = false
FEATURE [Sketcher::SketchObject] Sketch066
  FullyConstrained = true
  MapMode = 3
  Placement = pos=(0,0,0) rot=(1,0,0;1.5708rad)
  Support = -> [Extrude057]
  sketch-geometry (8):
    g0: Circle CenterX=80.351 CenterY=-67.6202 CenterZ=0 NormalX=0 NormalY=0 NormalZ=1 AngleXU=0 Radius=3
    g1: Circle CenterX=80.351 CenterY=-4.92017 CenterZ=0 NormalX=0 NormalY=0 NormalZ=1 AngleXU=0 Radius=3
    g2: Circle CenterX=23.851 CenterY=-4.92017 CenterZ=0 NormalX=0 NormalY=0 NormalZ=1 AngleXU=0 Radius=3
    g3: Circle CenterX=23.851 CenterY=-67.6202 CenterZ=0 NormalX=0 NormalY=0 NormalZ=1 AngleXU=0 Radius=3
    g4: Circle CenterX=23.851 CenterY=-67.6202 CenterZ=0 NormalX=0 NormalY=0 NormalZ=1 AngleXU=0 Radius=5
    g5: Circle CenterX=80.351 CenterY=-67.6202 CenterZ=0 NormalX=0 NormalY=0 NormalZ=1 AngleXU=0 Radius=5
    g6: Circle CenterX=23.851 CenterY=-4.92017 CenterZ=0 NormalX=0 NormalY=0 NormalZ=1 AngleXU=0 Radius=5
    g7: Circle CenterX=80.351 CenterY=-4.92017 CenterZ=0 NormalX=0 NormalY=0 NormalZ=1 AngleXU=0 Radius=5
  constraints (8):
    c: Block(g1)
    c: Block(g0)
    c: Block(g3)
    c: Block(g2)
    c: Block(g5)
    c: Block(g4)
    c: Block(g6)
    c: Block(g7)
FEATURE [Part::Extrusion] Extrude055
  Base = -> Sketch066
  Dir = (0,-1,2e-16)
  DirMode = 2
  FaceMakerClass = Part::FaceMakerBullseye
  LengthFwd = 2
  LengthRev = 0
  Solid = true
  Symmetric = false
FEATURE [Part::Fillet] Fillet041
  Base = -> Extrude056
  Edges = 4 edges r=1.99: [Edge6,Edge12,Edge18,Edge24]
FEATURE [Part::Cut] Cut045
  Base = -> Extrude055
  Placement = pos=(0,6,0) rot=(0,0,1;0rad)
  Tool = -> Fillet041
FEATURE [Part::MultiFuse] Fusion095  label="pcbScrewPillars"
  Placement = pos=(-3.2,-1,72.3) rot=(0,0,1;0rad)
  Shapes = -> [Cut045,Extrude054]
FEATURE [Part::Feature] Face113
  shape: bbox 3.2 x 1.5 x 2e-07 mm, 1 faces, 0 solids (baked)
FEATURE [Part::Revolution] Revolve121  label="backCaseScrewRetainer002"
  Angle = 360
  Axis = (0,1,0)
  Base = (0,0,0)
  FaceMakerClass = Part::FaceMakerBullseye
  Placement = pos=(12.5,3,62) rot=(0,0,1;0rad)
  Solid = false
  Source = -> Face113
  Symmetric = false
FEATURE [Part::Feature] Face114
  shape: bbox 3.2 x 1.5 x 2e-07 mm, 1 faces, 0 solids (baked)
FEATURE [Part::Feature] Face115
  shape: bbox 3.2 x 1.5 x 2e-07 mm, 1 faces, 0 solids (baked)
FEATURE [Part::Feature] Face116
  shape: bbox 3.2 x 1.5 x 2e-07 mm, 1 faces, 0 solids (baked)
FEATURE [Part::Revolution] Revolve122  label="frontCaseScrewRetainer004"
  Angle = 360
  Axis = (0,1,0)
  Base = (0,0,0)
  FaceMakerClass = Part::FaceMakerBullseye
  Placement = pos=(89.5,3,68.5) rot=(0,0,1;0rad)
  Solid = false
  Source = -> Face115
  Symmetric = false
FEATURE [Part::Revolution] Revolve123  label="frontCaseScrewRetainer005"
  Angle = 360
  Axis = (0,1,0)
  Base = (0,0,0)
  FaceMakerClass = Part::FaceMakerBullseye
  Placement = pos=(89.5,3,3.5) rot=(0,0,1;0rad)
  Solid = false
  Source = -> Face116
  Symmetric = false
FEATURE [Part::Revolution] Revolve124  label="backCaseScrewRetainer003"
  Angle = 360
  Axis = (0,1,0)
  Base = (0,0,0)
  FaceMakerClass = Part::FaceMakerBullseye
  Placement = pos=(12.5,3,10) rot=(0,0,1;0rad)
  Solid = false
  Source = -> Face114
  Symmetric = false
FEATURE [Part::Feature] Face117
  shape: bbox 3.6 x 3.2 x 2e-07 mm, 1 faces, 0 solids (baked)
FEATURE [Part::Revolution] Revolve125  label="moreFrontCaseScrewRetainer004"
  Angle = 360
  Axis = (0,1,0)
  Base = (0,0,0)
  FaceMakerClass = Part::FaceMakerBullseye
  Placement = pos=(109.5,4.5,68.5) rot=(0,0,1;0rad)
  Solid = false
  Source = -> Face117
  Symmetric = false
FEATURE [Part::Feature] Face118
  shape: bbox 3.6 x 3.2 x 2e-07 mm, 1 faces, 0 solids (baked)
FEATURE [Part::Revolution] Revolve126  label="moreFrontCaseScrewRetainer005"
  Angle = 360
  Axis = (0,1,0)
  Base = (0,0,0)
  FaceMakerClass = Part::FaceMakerBullseye
  Placement = pos=(109.5,4.5,3.5) rot=(0,0,1;0rad)
  Solid = false
  Source = -> Face118
  Symmetric = false
FEATURE [Part::MultiFuse] Fusion096  label="screwRetainers001"
  Shapes = -> [Revolve126,Revolve125,Revolve124,Revolve123,Revolve122,Revolve121]
FEATURE [Part::Feature] Face119
  shape: bbox 10 x 16.5 x 2e-07 mm, 1 faces, 0 solids (baked)
FEATURE [Part::Revolution] Revolve130  label="plugHousing050"
  Angle = 360
  Axis = (0,1,0)
  Base = (0,0,0)
  FaceMakerClass = Part::FaceMakerBullseye
  Placement = pos=(0,0,36.15) rot=(0,0,1;0rad)
  Solid = false
  Source = -> Face119
  Symmetric = false
FEATURE [Part::Feature] Face120
  shape: bbox 10 x 16.5 x 2e-07 mm, 1 faces, 0 solids (baked)
FEATURE [Part::Feature] Face121
  shape: bbox 10 x 16.5 x 2e-07 mm, 1 faces, 0 solids (baked)
FEATURE [Part::Revolution] Revolve127  label="plugHousing047"
  Angle = 360
  Axis = (0,1,0)
  Base = (0,0,0)
  FaceMakerClass = Part::FaceMakerBullseye
  Placement = pos=(0,0,36.15) rot=(0,0,1;0rad)
  Solid = false
  Source = -> Face121
  Symmetric = false
FEATURE [Part::Feature] Face122
  shape: bbox 10 x 16.5 x 2e-07 mm, 1 faces, 0 solids (baked)
FEATURE [Part::Feature] Face123
  shape: bbox 10 x 16.5 x 2e-07 mm, 1 faces, 0 solids (baked)
FEATURE [Part::Revolution] Revolve128  label="plugHousing048"
  Angle = 360
  Axis = (0,1,0)
  Base = (0,0,0)
  FaceMakerClass = Part::FaceMakerBullseye
  Placement = pos=(0,0,36.15) rot=(0,0,1;0rad)
  Solid = false
  Source = -> Face123
  Symmetric = false
FEATURE [Part::MultiFuse] Fusion100  label="plugHousing054"
  Placement = pos=(0,0,0) rot=(0,0,1;1.5708rad)
  Shapes = -> [Revolve130,Revolve128]
FEATURE [Part::Feature] Face124
  shape: bbox 10 x 16.5 x 2e-07 mm, 1 faces, 0 solids (baked)
FEATURE [Part::Feature] Face125
  shape: bbox 10 x 16.5 x 2e-07 mm, 1 faces, 0 solids (baked)
FEATURE [Part::Revolution] Revolve129  label="plugHousing049"
  Angle = 360
  Axis = (0,1,0)
  Base = (0,0,0)
  FaceMakerClass = Part::FaceMakerBullseye
  Placement = pos=(0,0,36.15) rot=(0,0,1;0rad)
  Solid = false
  Source = -> Face125
  Symmetric = false
FEATURE [Part::Feature] Face126
  shape: bbox 10 x 16.5 x 2e-07 mm, 1 faces, 0 solids (baked)
FEATURE [Part::Revolution] Revolve131  label="plugHousing058"
  Angle = 360
  Axis = (0,1,0)
  Base = (0,0,0)
  FaceMakerClass = Part::FaceMakerBullseye
  Placement = pos=(0,0,36.15) rot=(0,0,1;0rad)
  Solid = false
  Source = -> Face120
  Symmetric = false
FEATURE [Part::MultiFuse] Fusion099  label="plugHousing053"
  Placement = pos=(0,0,0) rot=(0,0,1;1.5708rad)
  Shapes = -> [Revolve127,Revolve131]
FEATURE [Part::MultiFuse] Fusion102  label="plugHousing056"
  Placement = pos=(0,19,0) rot=(0,0,1;3.14159rad)
  Shapes = -> [Fusion100,Fusion099]
FEATURE [Part::Revolution] Revolve132  label="plugHousing059"
  Angle = 360
  Axis = (0,1,0)
  Base = (0,0,0)
  FaceMakerClass = Part::FaceMakerBullseye
  Placement = pos=(0,0,36.15) rot=(0,0,1;0rad)
  Solid = false
  Source = -> Face126
  Symmetric = false
FEATURE [Part::Revolution] Revolve133  label="plugHousing060"
  Angle = 360
  Axis = (0,1,0)
  Base = (0,0,0)
  FaceMakerClass = Part::FaceMakerBullseye
  Placement = pos=(0,0,36.15) rot=(0,0,1;0rad)
  Solid = false
  Source = -> Face122
  Symmetric = false
FEATURE [Part::MultiFuse] Fusion097  label="plugHousing051"
  Placement = pos=(0,0,0) rot=(0,0,1;1.5708rad)
  Shapes = -> [Revolve133,Revolve132]
FEATURE [Part::Revolution] Revolve134  label="plugHousing061"
  Angle = 360
  Axis = (0,1,0)
  Base = (0,0,0)
  FaceMakerClass = Part::FaceMakerBullseye
  Placement = pos=(0,0,36.15) rot=(0,0,1;0rad)
  Solid = false
  Source = -> Face124
  Symmetric = false
FEATURE [Part::MultiFuse] Fusion101  label="plugHousing055"
  Placement = pos=(0,0,0) rot=(0,0,1;1.5708rad)
  Shapes = -> [Revolve129,Revolve134]
FEATURE [Part::MultiFuse] Fusion098  label="plugHousing052"
  Placement = pos=(0,19,0) rot=(0,0,1;3.14159rad)
  Shapes = -> [Fusion097,Fusion101]
FEATURE [Part::MultiFuse] Fusion103  label="plugHousing057"
  Placement = pos=(122.621,0,-0.15) rot=(0,0,1;0rad)
  Shapes = -> [Fusion102,Fusion098]
FEATURE [Part::Box] Box028  label="Cube015"
  AttacherType = Attacher::AttachEngine3D
  Height = 28
  Length = 3
  Placement = pos=(110.7,19,22) rot=(0,0,1;0rad)
  Width = 15.7
FEATURE [Part::Cylinder] Cylinder044
  Angle = 360
  AttacherType = Attacher::AttachEngine3D
  Height = 20
  Placement = pos=(0,0,36.15) rot=(0,0,1;0rad)
  Radius = 10.3
FEATURE [Part::Cylinder] Cylinder045
  Angle = 360
  AttacherType = Attacher::AttachEngine3D
  Height = 10
  Placement = pos=(0,0,36.15) rot=(0,0,1;0rad)
  Radius = 4
FEATURE [Part::MultiFuse] Fusion104  label="removeToCreteHoleForPlugHousing040"
  Placement = pos=(70,19,36) rot=(0,1,0;1.5708rad)
  Shapes = -> [Cylinder044,Cylinder045]
FEATURE [Part::Cut] Cut046  label="plugHousingTab003"
  Base = -> Box028
  Tool = -> Fusion104
FEATURE [Part::MultiFuse] Fusion105  label="plugHousing062"
  Shapes = -> [Fusion103,Cut046]
FEATURE [Part::Fillet] Fillet042
  Base = -> Fusion105
  Edges = 1 edges r=2: [Edge25]
FEATURE [Part::Fillet] Fillet043  label="plugHousing063"
  Base = -> Fillet042
  Edges = 1 edges r=2: [Edge8]
  Placement = pos=(7,0,0) rot=(0,0,1;0rad)
FEATURE [Part::Feature] Face127
  shape: bbox 10 x 16.5 x 2e-07 mm, 1 faces, 0 solids (baked)
FEATURE [Part::Feature] Face128
  shape: bbox 10 x 16.5 x 2e-07 mm, 1 faces, 0 solids (baked)
FEATURE [Part::Revolution] Revolve137  label="plugHousing070"
  Angle = 360
  Axis = (0,1,0)
  Base = (0,0,0)
  FaceMakerClass = Part::FaceMakerBullseye
  Placement = pos=(0,0,36.15) rot=(0,0,1;0rad)
  Solid = false
  Source = -> Face127
  Symmetric = false
FEATURE [Part::Revolution] Revolve140  label="plugHousing073"
  Angle = 360
  Axis = (0,1,0)
  Base = (0,0,0)
  FaceMakerClass = Part::FaceMakerBullseye
  Placement = pos=(0,0,36.15) rot=(0,0,1;0rad)
  Solid = false
  Source = -> Face128
  Symmetric = false
FEATURE [Part::Feature] Face129
  shape: bbox 10 x 16.5 x 2e-07 mm, 1 faces, 0 solids (baked)
FEATURE [Part::Revolution] Revolve138  label="plugHousing071"
  Angle = 360
  Axis = (0,1,0)
  Base = (0,0,0)
  FaceMakerClass = Part::FaceMakerBullseye
  Placement = pos=(0,0,36.15) rot=(0,0,1;0rad)
  Solid = false
  Source = -> Face129
  Symmetric = false
FEATURE [Part::Feature] Face130
  shape: bbox 10 x 16.5 x 2e-07 mm, 1 faces, 0 solids (baked)
FEATURE [Part::Revolution] Revolve139  label="plugHousing072"
  Angle = 360
  Axis = (0,1,0)
  Base = (0,0,0)
  FaceMakerClass = Part::FaceMakerBullseye
  Placement = pos=(0,0,36.15) rot=(0,0,1;0rad)
  Solid = false
  Source = -> Face130
  Symmetric = false
FEATURE [Part::Feature] Face131
  shape: bbox 10 x 16.5 x 2e-07 mm, 1 faces, 0 solids (baked)
FEATURE [Part::Revolution] Revolve135  label="plugHousing068"
  Angle = 360
  Axis = (0,1,0)
  Base = (0,0,0)
  FaceMakerClass = Part::FaceMakerBullseye
  Placement = pos=(0,0,36.15) rot=(0,0,1;0rad)
  Solid = false
  Source = -> Face131
  Symmetric = false
FEATURE [Part::MultiFuse] Fusion112  label="plugHousing078"
  Placement = pos=(0,0,0) rot=(0,0,1;1.5708rad)
  Shapes = -> [Revolve135,Revolve139]
FEATURE [Part::Feature] Face132
  shape: bbox 10 x 16.5 x 2e-07 mm, 1 faces, 0 solids (baked)
FEATURE [Part::Revolution] Revolve141  label="plugHousing074"
  Angle = 360
  Axis = (0,1,0)
  Base = (0,0,0)
  FaceMakerClass = Part::FaceMakerBullseye
  Placement = pos=(0,0,36.15) rot=(0,0,1;0rad)
  Solid = false
  Source = -> Face132
  Symmetric = false
FEATURE [Part::MultiFuse] Fusion110  label="plugHousing076"
  Placement = pos=(0,0,0) rot=(0,0,1;1.5708rad)
  Shapes = -> [Revolve141,Revolve140]
FEATURE [Part::Feature] Face133
  shape: bbox 10 x 16.5 x 2e-07 mm, 1 faces, 0 solids (baked)
FEATURE [Part::Revolution] Revolve136  label="plugHousing069"
  Angle = 360
  Axis = (0,1,0)
  Base = (0,0,0)
  FaceMakerClass = Part::FaceMakerBullseye
  Placement = pos=(0,0,36.15) rot=(0,0,1;0rad)
  Solid = false
  Source = -> Face133
  Symmetric = false
FEATURE [Part::MultiFuse] Fusion106  label="plugHousing064"
  Placement = pos=(0,0,0) rot=(0,0,1;1.5708rad)
  Shapes = -> [Revolve138,Revolve136]
FEATURE [Part::MultiFuse] Fusion108  label="plugHousing066"
  Placement = pos=(0,19,0) rot=(0,0,1;3.14159rad)
  Shapes = -> [Fusion106,Fusion112]
FEATURE [Part::Feature] Face134
  shape: bbox 10 x 16.5 x 2e-07 mm, 1 faces, 0 solids (baked)
FEATURE [Part::Revolution] Revolve142  label="plugHousing075"
  Angle = 360
  Axis = (0,1,0)
  Base = (0,0,0)
  FaceMakerClass = Part::FaceMakerBullseye
  Placement = pos=(0,0,36.15) rot=(0,0,1;0rad)
  Solid = false
  Source = -> Face134
  Symmetric = false
FEATURE [Part::MultiFuse] Fusion107  label="plugHousing065"
  Placement = pos=(0,0,0) rot=(0,0,1;1.5708rad)
  Shapes = -> [Revolve137,Revolve142]
FEATURE [Part::MultiFuse] Fusion111  label="plugHousing077"
  Placement = pos=(0,19,0) rot=(0,0,1;3.14159rad)
  Shapes = -> [Fusion110,Fusion107]
FEATURE [Part::MultiFuse] Fusion109  label="plugHousing067"
  Placement = pos=(131.236,0,-0.15) rot=(0,0,1;0rad)
  Shapes = -> [Fusion108,Fusion111]
FEATURE [Part::MultiFuse] Fusion113  label="plugHousing079"
  Shapes = -> [Fillet043,Fusion109]
FEATURE [Part::Feature] Face135
  shape: bbox 3.5 x 17.8 x 2e-07 mm, 1 faces, 0 solids (baked)
FEATURE [Part::Revolution] Revolve143  label="removeToCreateScrewAndThreadedInsertHole049"
  Angle = 360
  Axis = (0,1,0)
  Base = (0,0,0)
  FaceMakerClass = Part::FaceMakerBullseye
  Placement = pos=(12.5,0,10) rot=(0,0,1;0rad)
  Solid = false
  Source = -> Face135
  Symmetric = false
FEATURE [Part::Feature] Face136
  shape: bbox 3.5 x 17.8 x 2e-07 mm, 1 faces, 0 solids (baked)
FEATURE [Part::Revolution] Revolve144  label="removeToCreateScrewAndThreadedInsertHole050"
  Angle = 360
  Axis = (0,1,0)
  Base = (0,0,0)
  FaceMakerClass = Part::FaceMakerBullseye
  Placement = pos=(12.5,0,62) rot=(0,0,1;0rad)
  Solid = false
  Source = -> Face136
  Symmetric = false
FEATURE [Part::Feature] Face137
  shape: bbox 3.5 x 17.8 x 2e-07 mm, 1 faces, 0 solids (baked)
FEATURE [Part::Revolution] Revolve145  label="removeToCreateScrewAndThreadedInsertHole051"
  Angle = 360
  Axis = (0,1,0)
  Base = (0,0,0)
  FaceMakerClass = Part::FaceMakerBullseye
  Placement = pos=(89.5,0,68.5) rot=(0,0,1;0rad)
  Solid = false
  Source = -> Face137
  Symmetric = false
FEATURE [Part::Feature] Face138
  shape: bbox 3.5 x 17.8 x 2e-07 mm, 1 faces, 0 solids (baked)
FEATURE [Part::Revolution] Revolve146  label="removeToCreateScrewAndThreadedInsertHole052"
  Angle = 360
  Axis = (0,1,0)
  Base = (0,0,0)
  FaceMakerClass = Part::FaceMakerBullseye
  Placement = pos=(89.5,0,3.5) rot=(0,0,1;0rad)
  Solid = false
  Source = -> Face138
  Symmetric = false
FEATURE [Part::Feature] Face139
  shape: bbox 3.5 x 17.8 x 2e-07 mm, 1 faces, 0 solids (baked)
FEATURE [Part::Revolution] Revolve147  label="removeToCreateScrewAndThreadedInsertHole053"
  Angle = 360
  Axis = (0,1,0)
  Base = (0,0,0)
  FaceMakerClass = Part::FaceMakerBullseye
  Placement = pos=(109.5,4.7,3.5) rot=(0,0,1;0rad)
  Solid = false
  Source = -> Face139
  Symmetric = false
FEATURE [Part::Feature] Face140
  shape: bbox 3.5 x 17.8 x 2e-07 mm, 1 faces, 0 solids (baked)
FEATURE [Part::Revolution] Revolve148  label="removeToCreateScrewAndThreadedInsertHole054"
  Angle = 360
  Axis = (0,1,0)
  Base = (0,0,0)
  FaceMakerClass = Part::FaceMakerBullseye
  Placement = pos=(109.5,4.7,68.5) rot=(0,0,1;0rad)
  Solid = false
  Source = -> Face140
  Symmetric = false
FEATURE [Part::MultiFuse] Fusion114  label="removeToCreateScrewAndThreadedInsertHole055"
  Shapes = -> [Revolve148,Revolve147,Revolve146,Revolve145,Revolve144,Revolve143]
FEATURE [Part::Cut] Cut047  label="casePillars004"
  Base = -> Cut037
  Tool = -> Fusion114
FEATURE [Part::Feature] Face141
  shape: bbox 3.5 x 17.8 x 2e-07 mm, 1 faces, 0 solids (baked)
FEATURE [Part::Feature] Face142
  shape: bbox 3.5 x 17.8 x 2e-07 mm, 1 faces, 0 solids (baked)
FEATURE [Part::Feature] Face143
  shape: bbox 3.5 x 17.8 x 2e-07 mm, 1 faces, 0 solids (baked)
FEATURE [Part::Revolution] Revolve149  label="removeToCreateScrewAndThreadedInsertHole057"
  Angle = 360
  Axis = (0,1,0)
  Base = (0,0,0)
  FaceMakerClass = Part::FaceMakerBullseye
  Placement = pos=(12.5,0,10) rot=(0,0,1;0rad)
  Solid = false
  Source = -> Face141
  Symmetric = false
FEATURE [Part::Feature] Face144
  shape: bbox 3.5 x 17.8 x 2e-07 mm, 1 faces, 0 solids (baked)
FEATURE [Part::Feature] Face145
  shape: bbox 3.5 x 17.8 x 2e-07 mm, 1 faces, 0 solids (baked)
FEATURE [Part::Feature] Face146
  shape: bbox 3.5 x 17.8 x 2e-07 mm, 1 faces, 0 solids (baked)
FEATURE [Part::Revolution] Revolve150  label="removeToCreateScrewAndThreadedInsertHole058"
  Angle = 360
  Axis = (0,1,0)
  Base = (0,0,0)
  FaceMakerClass = Part::FaceMakerBullseye
  Placement = pos=(12.5,0,62) rot=(0,0,1;0rad)
  Solid = false
  Source = -> Face146
  Symmetric = false
FEATURE [Part::Revolution] Revolve151  label="removeToCreateScrewAndThreadedInsertHole059"
  Angle = 360
  Axis = (0,1,0)
  Base = (0,0,0)
  FaceMakerClass = Part::FaceMakerBullseye
  Placement = pos=(89.5,0,68.5) rot=(0,0,1;0rad)
  Solid = false
  Source = -> Face143
  Symmetric = false
FEATURE [Part::Revolution] Revolve152  label="removeToCreateScrewAndThreadedInsertHole060"
  Angle = 360
  Axis = (0,1,0)
  Base = (0,0,0)
  FaceMakerClass = Part::FaceMakerBullseye
  Placement = pos=(89.5,0,3.5) rot=(0,0,1;0rad)
  Solid = false
  Source = -> Face142
  Symmetric = false
FEATURE [Part::Revolution] Revolve153  label="removeToCreateScrewAndThreadedInsertHole061"
  Angle = 360
  Axis = (0,1,0)
  Base = (0,0,0)
  FaceMakerClass = Part::FaceMakerBullseye
  Placement = pos=(109.5,4.7,3.5) rot=(0,0,1;0rad)
  Solid = false
  Source = -> Face145
  Symmetric = false
FEATURE [Part::Revolution] Revolve154  label="removeToCreateScrewAndThreadedInsertHole062"
  Angle = 360
  Axis = (0,1,0)
  Base = (0,0,0)
  FaceMakerClass = Part::FaceMakerBullseye
  Placement = pos=(109.5,4.7,68.5) rot=(0,0,1;0rad)
  Solid = false
  Source = -> Face144
  Symmetric = false
FEATURE [Part::MultiFuse] Fusion115  label="removeToCreateScrewAndThreadedInsertHole056"
  Shapes = -> [Revolve154,Revolve153,Revolve152,Revolve151,Revolve150,Revolve149]
FEATURE [Part::Feature] Face147
  shape: bbox 9.8 x 26.5 x 2e-07 mm, 1 faces, 0 solids (baked)
FEATURE [Part::Revolution] Revolve155
  Angle = 360
  Axis = (0,1,0)
  Base = (0,0,0)
  FaceMakerClass = Part::FaceMakerBullseye
  Placement = pos=(0,0,0) rot=(0,0,1;1.5708rad)
  Solid = false
  Source = -> Face147
  Symmetric = false
FEATURE [Part::Feature] Face148
  shape: bbox 9.8 x 26.5 x 2e-07 mm, 1 faces, 0 solids (baked)
FEATURE [Part::Revolution] Revolve156
  Angle = 360
  Axis = (0,1,0)
  Base = (0,0,0)
  FaceMakerClass = Part::FaceMakerBullseye
  Placement = pos=(0,0,0) rot=(0,0,1;1.5708rad)
  Solid = false
  Source = -> Face148
  Symmetric = false
FEATURE [Part::MultiFuse] Fusion116
  Placement = pos=(-18,19,36) rot=(0,0,1;0rad)
  Shapes = -> [Revolve156,Revolve155]
FEATURE [Part::Box] Box029  label="Cube016"
  AttacherType = Attacher::AttachEngine3D
  Height = 28
  Length = 3
  Placement = pos=(110.7,19,22) rot=(0,0,1;0rad)
  Width = 15.7
FEATURE [Part::Cylinder] Cylinder046
  Angle = 360
  AttacherType = Attacher::AttachEngine3D
  Height = 10
  Placement = pos=(0,0,36.15) rot=(0,0,1;0rad)
  Radius = 4
FEATURE [Part::Cylinder] Cylinder047
  Angle = 360
  AttacherType = Attacher::AttachEngine3D
  Height = 20
  Placement = pos=(0,0,36.15) rot=(0,0,1;0rad)
  Radius = 10.3
FEATURE [Part::MultiFuse] Fusion117  label="removeToCreteHoleForPlugHousing041"
  Placement = pos=(70,19,36) rot=(0,1,0;1.5708rad)
  Shapes = -> [Cylinder047,Cylinder046]
FEATURE [Part::Cut] Cut049  label="plugHousingTab004"
  Base = -> Box029
  Placement = pos=(-107.4,-14,0) rot=(0,0,1;0rad)
  Tool = -> Fusion117
FEATURE [Part::Box] Box030  label="Cube017"
  AttacherType = Attacher::AttachEngine3D
  Height = 28
  Length = 3
  Placement = pos=(110.7,19,22) rot=(0,0,1;0rad)
  Width = 15.7
FEATURE [Part::Cylinder] Cylinder048
  Angle = 360
  AttacherType = Attacher::AttachEngine3D
  Height = 10
  Placement = pos=(0,0,36.15) rot=(0,0,1;0rad)
  Radius = 4
FEATURE [Part::Cylinder] Cylinder049
  Angle = 360
  AttacherType = Attacher::AttachEngine3D
  Height = 20
  Placement = pos=(0,0,36.15) rot=(0,0,1;0rad)
  Radius = 10.3
FEATURE [Part::MultiFuse] Fusion118  label="removeToCreteHoleForPlugHousing042"
  Placement = pos=(70,19,36) rot=(0,1,0;1.5708rad)
  Shapes = -> [Cylinder049,Cylinder048]
FEATURE [Part::Cut] Cut050  label="plugHousingTab005"
  Base = -> Box030
  Placement = pos=(-107.4,-14,0) rot=(0,0,1;0rad)
  Tool = -> Fusion118
FEATURE [Part::MultiFuse] Fusion119
  Placement = pos=(9.6,23,0) rot=(0,0,1;3.14159rad)
  Shapes = -> [Cut049,Cut050]
FEATURE [Part::Box] Box031  label="Cube018"
  AttacherType = Attacher::AttachEngine3D
  Height = 10
  Length = 3
  Placement = pos=(3.3,4,12) rot=(0,0,1;0rad)
  Width = 10
FEATURE [Part::Fillet] Fillet044
  Base = -> Box031
  Edges = 1 edges r=2: [Edge11]
FEATURE [Part::Box] Box032  label="Cube019"
  AttacherType = Attacher::AttachEngine3D
  Height = 10
  Length = 3
  Placement = pos=(3.3,4,50) rot=(0,0,1;0rad)
  Width = 10
FEATURE [Part::Fillet] Fillet045
  Base = -> Box032
  Edges = 1 edges r=2: [Edge12]
FEATURE [Part::Box] Box033  label="Cube020"
  AttacherType = Attacher::AttachEngine3D
  Height = 28
  Length = 4
  Placement = pos=(5,0,22) rot=(0,0,1;0rad)
  Width = 10
FEATURE [Part::Fillet] Fillet046
  Base = -> Box033
  Edges = 1 edges r=1: [Edge7]
FEATURE [Part::Fillet] Fillet047
  Base = -> Fillet046
  Edges = 1 edges r=2: [Edge5]
FEATURE [Part::Fillet] Fillet048
  Base = -> Fillet047
  Edges = 1 edges r=2: [Edge2]
FEATURE [Part::Cylinder] Cylinder050
  Angle = 360
  AttacherType = Attacher::AttachEngine3D
  Height = 20
  Placement = pos=(0,0,36.15) rot=(0,0,1;0rad)
  Radius = 8.2
FEATURE [Part::Cylinder] Cylinder051
  Angle = 360
  AttacherType = Attacher::AttachEngine3D
  Height = 10
  Placement = pos=(0,0,36.15) rot=(0,0,1;0rad)
  Radius = 4
FEATURE [Part::MultiFuse] Fusion120  label="removeToCreteHoleForPlugHousing043"
  Placement = pos=(-42,19,36) rot=(0,1,0;1.5708rad)
  Shapes = -> [Cylinder050,Cylinder051]
FEATURE [Sketcher::SketchObject] Sketch067  label="topSketch018"
  FullyConstrained = true
  sketch-geometry (4):
    g0: LineSegment StartX=16.8446 StartY=31.512 StartZ=0 EndX=16.3251 EndY=34.4666 EndZ=0
    g1: ArcOfCircle CenterX=19 CenterY=19.2524 CenterZ=0 NormalX=0 NormalY=0 NormalZ=1 AngleXU=0 Radius=15.4476 StartAngle=1.74483 EndAngle=2.72717
    g2: ArcOfCircle CenterX=19 CenterY=19.2524 CenterZ=0 NormalX=0 NormalY=0 NormalZ=1 AngleXU=0 Radius=12.4476 StartAngle=1.74483 EndAngle=2.73189
    g3: LineSegment StartX=4.86004 StartY=25.4725 StartZ=0 EndX=7.58253 EndY=24.2107 EndZ=0
  constraints (7):
    c: Block(g0)
    c: Coincident(g1,g0)
    c: Coincident(g2,g0)
    c: Coincident(g3,g1)
    c: Coincident(g3,g2)
    c: Block(g1)
    c: Block(g2)
FEATURE [Part::Extrusion] Extrude058
  Base = -> Sketch067
  Dir = (0,0,1)
  DirMode = 2
  FaceMakerClass = Part::FaceMakerBullseye
  LengthFwd = 10
  LengthRev = 0
  Placement = pos=(0,0,31) rot=(0,0,1;0rad)
  Solid = true
  Symmetric = false
FEATURE [Part::Cut] Cut051
  Base = -> Extrude058
  Tool = -> Fusion120
FEATURE [Part::Fillet] Fillet049
  Base = -> Cut051
  Edges = 1 edges r=2: [Edge1]
FEATURE [Part::Fillet] Fillet050
  Base = -> Fillet049
  Edges = 1 edges r=2.5: [Edge1]
FEATURE [Part::Fillet] Fillet051
  Base = -> Fillet050
  Edges = 1 edges r=2.5: [Edge2]
FEATURE [Part::MultiFuse] Fusion121  label="wireHolder003"
  Shapes = -> [Fusion116,Fillet051]
FEATURE [Part::MultiFuse] Fusion122
  Shapes = -> [Fillet045,Fusion121]
FEATURE [Part::MultiFuse] Fusion123  label="wireHolder004"
  Shapes = -> [Fusion122,Fillet048]
FEATURE [Part::MultiFuse] Fusion124  label="wireHolder005"
  Shapes = -> [Fillet044,Fusion119,Fusion123]
FEATURE [Sketcher::SketchObject] Sketch068  label="topSketch019"
  FullyConstrained = true
  sketch-geometry (6):
    g0: LineSegment StartX=19 StartY=38 StartZ=0 EndX=117 EndY=38 EndZ=0
    g1: ArcOfCircle CenterX=19 CenterY=19 CenterZ=0 NormalX=0 NormalY=0 NormalZ=1 AngleXU=0 Radius=19 StartAngle=1.5708 EndAngle=3.14159
    g2: LineSegment StartX=117 StartY=38 StartZ=0 EndX=117 EndY=19 EndZ=0
    g3: LineSegment StartX=98 StartY=1.0161e-12 StartZ=0 EndX=5.22862e-06 EndY=1.0161e-12 EndZ=0
    g4: LineSegment StartX=5.22862e-06 StartY=19 StartZ=0 EndX=5.22862e-06 EndY=1.0161e-12 EndZ=0
    g5: ArcOfCircle CenterX=98 CenterY=19 CenterZ=0 NormalX=0 NormalY=0 NormalZ=1 AngleXU=0 Radius=19 StartAngle=4.71239 EndAngle=6.28319
  constraints (16):
    c: Horizontal(g0)
    c: Distance(g0) = 98
    c: Coincident(g1,g0)
    c: Block(g1)
    c: Coincident(g2,g0)
    c: Vertical(g2)
    c: Distance(g2) = 19
    c: Horizontal(g3)
    c: Coincident(g4,g1)
    c: Vertical(g4)
    c: Coincident(g3,g4)
    c: Block(g3)
    c: Coincident(g5,g2)
    c: Coincident(g5,g3)
    c: Block(g0)
    c: Block(g5)
FEATURE [Part::Extrusion] Extrude059  label="sideA002"
  Base = -> Sketch068
  Dir = (0,0,1)
  DirMode = 2
  FaceMakerClass = Part::FaceMakerBullseye
  LengthFwd = 3
  LengthRev = 0
  Placement = pos=(0,0,-2.7) rot=(0,0,1;0rad)
  Solid = true
  Symmetric = false
FEATURE [Sketcher::SketchObject] Sketch069  label="topSketch020"
  FullyConstrained = true
  sketch-geometry (6):
    g0: LineSegment StartX=19 StartY=38 StartZ=0 EndX=117 EndY=38 EndZ=0
    g1: ArcOfCircle CenterX=19 CenterY=19 CenterZ=0 NormalX=0 NormalY=0 NormalZ=1 AngleXU=0 Radius=19 StartAngle=1.5708 EndAngle=3.14159
    g2: LineSegment StartX=117 StartY=38 StartZ=0 EndX=117 EndY=19 EndZ=0
    g3: LineSegment StartX=98 StartY=1.0161e-12 StartZ=0 EndX=5.22862e-06 EndY=1.0161e-12 EndZ=0
    g4: LineSegment StartX=5.22862e-06 StartY=19 StartZ=0 EndX=5.22862e-06 EndY=1.0161e-12 EndZ=0
    g5: ArcOfCircle CenterX=98 CenterY=19 CenterZ=0 NormalX=0 NormalY=0 NormalZ=1 AngleXU=0 Radius=19 StartAngle=4.71239 EndAngle=6.28319
  constraints (16):
    c: Horizontal(g0)
    c: Distance(g0) = 98
    c: Coincident(g1,g0)
    c: Block(g1)
    c: Coincident(g2,g0)
    c: Vertical(g2)
    c: Distance(g2) = 19
    c: Horizontal(g3)
    c: Coincident(g4,g1)
    c: Vertical(g4)
    c: Coincident(g3,g4)
    c: Block(g3)
    c: Coincident(g5,g2)
    c: Coincident(g5,g3)
    c: Block(g0)
    c: Block(g5)
FEATURE [Part::Extrusion] Extrude060  label="sideB002"
  Base = -> Sketch069
  Dir = (0,0,1)
  DirMode = 2
  FaceMakerClass = Part::FaceMakerBullseye
  LengthFwd = 3
  LengthRev = 0
  Placement = pos=(0,0,71.7) rot=(0,0,1;0rad)
  Solid = true
  Symmetric = false
FEATURE [Part::MultiFuse] Fusion127  label="removeFromBottom001"
  Placement = pos=(2,0,0) rot=(0,0,1;0rad)
  Shapes = -> [Extrude059,Extrude060]
FEATURE [Part::Cylinder] Cylinder052
  Angle = 360
  AttacherType = Attacher::AttachEngine3D
  Height = 20
  Placement = pos=(0,0,36.15) rot=(0,0,1;0rad)
  Radius = 14
FEATURE [Part::Cylinder] Cylinder053
  Angle = 360
  AttacherType = Attacher::AttachEngine3D
  Height = 10
  Placement = pos=(0,0,36.15) rot=(0,0,1;0rad)
  Radius = 4
FEATURE [Part::MultiFuse] Fusion128  label="removeToCreteHoleForPlugHousing044"
  Placement = pos=(70,19,36) rot=(0,1,0;1.5708rad)
  Shapes = -> [Cylinder052,Cylinder053]
FEATURE [Part::Cut] Cut052  label="bottom011"
  Base = -> Extrude043
  Tool = -> Fusion128
FEATURE [Part::Cut] Cut054  label="bottom012"
  Base = -> Cut052
  Tool = -> Fusion115
FEATURE [Sketcher::SketchObject] Sketch070
  FullyConstrained = true
  Placement = pos=(117,19,0) rot=(0.57735,0.57735,0.57735;2.0944rad)
  sketch-geometry (48):
    g0: LineSegment StartX=-49.19 StartY=69.25 StartZ=0 EndX=-49.19 EndY=66.25 EndZ=0
    g1: LineSegment StartX=-49.19 StartY=63.5 StartZ=0 EndX=-49.19 EndY=60.5 EndZ=0
    g2: LineSegment StartX=-49.19 StartY=57.75 StartZ=0 EndX=-49.19 EndY=54.75 EndZ=0
    g3: LineSegment StartX=-49.19 StartY=52 StartZ=0 EndX=-49.19 EndY=49 EndZ=0
    g4: LineSegment StartX=-49.19 StartY=46.25 StartZ=0 EndX=-49.19 EndY=43.25 EndZ=0
    g5: LineSegment StartX=-49.19 StartY=40.5 StartZ=0 EndX=-49.19 EndY=37.5 EndZ=0
    g6: LineSegment StartX=-49.19 StartY=34.5 StartZ=0 EndX=-49.19 EndY=31.5 EndZ=0
    g7: LineSegment StartX=-49.19 StartY=28.75 StartZ=0 EndX=-49.19 EndY=25.75 EndZ=0
    g8: LineSegment StartX=-49.19 StartY=23 StartZ=0 EndX=-49.19 EndY=20 EndZ=0
    g9: LineSegment StartX=-49.19 StartY=17.25 StartZ=0 EndX=-49.19 EndY=14.25 EndZ=0
    g10: LineSegment StartX=-49.19 StartY=11.5 StartZ=0 EndX=-49.19 EndY=8.5 EndZ=0
    g11: LineSegment StartX=-49.19 StartY=5.75 StartZ=0 EndX=-49.19 EndY=2.75 EndZ=0
    g12: ArcOfCircle CenterX=-1.5 CenterY=67.75 CenterZ=0 NormalX=0 NormalY=0 NormalZ=1 AngleXU=0 Radius=1.5 StartAngle=4.71239 EndAngle=7.85398
    g13: ArcOfCircle CenterX=-1.5 CenterY=62 CenterZ=0 NormalX=0 NormalY=0 NormalZ=1 AngleXU=0 Radius=1.5 StartAngle=4.71239 EndAngle=7.85398
    g14: ArcOfCircle CenterX=-1.5 CenterY=56.25 CenterZ=0 NormalX=0 NormalY=0 NormalZ=1 AngleXU=0 Radius=1.5 StartAngle=4.71239 EndAngle=7.85398
    g15: ArcOfCircle CenterX=-11.49 CenterY=50.5 CenterZ=0 NormalX=0 NormalY=0 NormalZ=1 AngleXU=0 Radius=1.5 StartAngle=4.71239 EndAngle=7.85398
    g16: ArcOfCircle CenterX=-16.28 CenterY=44.75 CenterZ=0 NormalX=0 NormalY=0 NormalZ=1 AngleXU=0 Radius=1.5 StartAngle=4.71239 EndAngle=7.85398
    g17: ArcOfCircle CenterX=-18.2337 CenterY=39 CenterZ=0 NormalX=0 NormalY=0 NormalZ=1 AngleXU=0 Radius=1.5 StartAngle=4.71485 EndAngle=7.85398
    g18: ArcOfCircle CenterX=-16.2837 CenterY=27.25 CenterZ=0 NormalX=0 NormalY=0 NormalZ=1 AngleXU=0 Radius=1.5 StartAngle=4.71485 EndAngle=7.85398
    g19: ArcOfCircle CenterX=-18.2337 CenterY=33 CenterZ=0 NormalX=0 NormalY=0 NormalZ=1 AngleXU=0 Radius=1.5 StartAngle=4.71485 EndAngle=7.85398
    g20: ArcOfCircle CenterX=-11.49 CenterY=21.5 CenterZ=0 NormalX=0 NormalY=0 NormalZ=1 AngleXU=0 Radius=1.5 StartAngle=4.71239 EndAngle=7.85398
    g21: ArcOfCircle CenterX=-1.5 CenterY=4.25 CenterZ=0 NormalX=0 NormalY=0 NormalZ=1 AngleXU=0 Radius=1.5 StartAngle=4.71239 EndAngle=7.85398
    g22: ArcOfCircle CenterX=-1.5 CenterY=10 CenterZ=0 NormalX=0 NormalY=0 NormalZ=1 AngleXU=0 Radius=1.5 StartAngle=4.71239 EndAngle=7.85398
    g23: ArcOfCircle CenterX=-1.5 CenterY=15.75 CenterZ=0 NormalX=0 NormalY=0 NormalZ=1 AngleXU=0 Radius=1.5 StartAngle=4.71239 EndAngle=7.85398
    g24: LineSegment StartX=-49.19 StartY=69.25 StartZ=0 EndX=-1.5 EndY=69.25 EndZ=0
    g25: LineSegment StartX=-49.19 StartY=66.25 StartZ=0 EndX=-1.5 EndY=66.25 EndZ=0
    g26: LineSegment StartX=-49.19 StartY=63.5 StartZ=0 EndX=-1.5 EndY=63.5 EndZ=0
    g27: LineSegment StartX=-49.19 StartY=60.5 StartZ=0 EndX=-1.5 EndY=60.5 EndZ=0
    g28: LineSegment StartX=-49.19 StartY=57.75 StartZ=0 EndX=-1.5 EndY=57.75 EndZ=0
    g29: LineSegment StartX=-49.19 StartY=54.75 StartZ=0 EndX=-1.5 EndY=54.75 EndZ=0
    g30: LineSegment StartX=-49.19 StartY=52 StartZ=0 EndX=-11.49 EndY=52 EndZ=0
    g31: LineSegment StartX=-49.19 StartY=49 StartZ=0 EndX=-11.49 EndY=49 EndZ=0
    g32: LineSegment StartX=-49.19 StartY=46.25 StartZ=0 EndX=-16.28 EndY=46.25 EndZ=0
    g33: LineSegment StartX=-49.19 StartY=43.25 StartZ=0 EndX=-16.28 EndY=43.25 EndZ=0
    g34: LineSegment StartX=-49.19 StartY=40.5 StartZ=0 EndX=-18.2337 EndY=40.5 EndZ=0
    g35: LineSegment StartX=-49.19 StartY=37.5 StartZ=0 EndX=-18.23 EndY=37.5 EndZ=0
    g36: LineSegment StartX=-49.19 StartY=34.5 StartZ=0 EndX=-18.2337 EndY=34.5 EndZ=0
    g37: LineSegment StartX=-49.19 StartY=31.5 StartZ=0 EndX=-18.23 EndY=31.5 EndZ=0
    g38: LineSegment StartX=-49.19 StartY=28.75 StartZ=0 EndX=-16.2837 EndY=28.75 EndZ=0
    g39: LineSegment StartX=-49.19 StartY=25.75 StartZ=0 EndX=-16.28 EndY=25.75 EndZ=0
    g40: LineSegment StartX=-49.19 StartY=23 StartZ=0 EndX=-11.49 EndY=23 EndZ=0
    g41: LineSegment StartX=-49.19 StartY=20 StartZ=0 EndX=-11.49 EndY=20 EndZ=0
    g42: LineSegment StartX=-49.19 StartY=17.25 StartZ=0 EndX=-1.5 EndY=17.25 EndZ=0
    g43: LineSegment StartX=-49.19 StartY=14.25 StartZ=0 EndX=-1.5 EndY=14.25 EndZ=0
    g44: LineSegment StartX=-49.19 StartY=11.5 StartZ=0 EndX=-1.5 EndY=11.5 EndZ=0
    g45: LineSegment StartX=-49.19 StartY=8.5 StartZ=0 EndX=-1.5 EndY=8.5 EndZ=0
    g46: LineSegment StartX=-49.19 StartY=5.75 StartZ=0 EndX=-1.5 EndY=5.75 EndZ=0
    g47: LineSegment StartX=-49.19 StartY=2.75 StartZ=0 EndX=-1.5 EndY=2.75 EndZ=0
  constraints (120):
    c: Vertical(g0)
    c: Distance(g0) = 3
    c: Block(g0)
    c: Vertical(g1)
    c: Distance(g1) = 3
    c: Vertical(g2)
    c: Equal(g0,g2) = 3
    c: Block(g2)
    c: Vertical(g3)
    c: Equal(g1,g3) = 3
    c: Vertical(g4)
    c: Equal(g0,g4) = 3
    c: Block(g4)
    c: Vertical(g5)
    c: Equal(g1,g5) = 3
    c: Vertical(g6)
    c: Equal(g0,g6) = 3
    c: Block(g6)
    c: Vertical(g7)
    c: Equal(g1,g7) = 3
    c: Vertical(g8)
    c: Equal(g0,g8) = 3
    c: Block(g8)
    c: Vertical(g9)
    c: Equal(g1,g9) = 3
    c: Vertical(g10)
    c: Equal(g0,g10) = 3
    c: Block(g10)
    c: Vertical(g11)
    c: Equal(g1,g11) = 3
    c: Block(g12)
    c: Block(g13)
    c: Block(g14)
    c: Block(g15)
    c: Block(g16)
    c: Block(g17)
    c: Block(g18)
    c: Block(g19)
    c: Block(g20)
    c: Block(g21)
    c: Block(g22)
    c: Block(g23)
    c: Block(g11)
    c: Block(g9)
    c: Block(g7)
    c: Block(g5)
    c: Block(g3)
    c: Block(g1)
    c: Coincident(g24,g0)
    c: Coincident(g24,g12)
    c: Horizontal(g24)
    c: Coincident(g25,g0)
    c: Coincident(g25,g12)
    c: Horizontal(g25)
    c: Coincident(g26,g1)
    c: Coincident(g26,g13)
    c: Horizontal(g26)
    c: Coincident(g27,g1)
    c: Coincident(g27,g13)
    c: Horizontal(g27)
    c: Coincident(g28,g2)
    c: Coincident(g28,g14)
    c: Horizontal(g28)
    c: Coincident(g29,g2)
    c: Coincident(g29,g14)
    c: Horizontal(g29)
    c: Coincident(g30,g3)
    c: Coincident(g30,g15)
    c: Horizontal(g30)
    c: Coincident(g31,g3)
    c: Coincident(g31,g15)
    c: Horizontal(g31)
    c: Coincident(g32,g4)
    c: Coincident(g32,g16)
    c: Horizontal(g32)
    c: Coincident(g33,g4)
    c: Coincident(g33,g16)
    c: Horizontal(g33)
    c: Coincident(g34,g5)
    c: Coincident(g34,g17)
    c: Horizontal(g34)
    c: Coincident(g35,g5)
    c: Coincident(g35,g17)
    c: Horizontal(g35)
    c: Coincident(g36,g6)
    c: Coincident(g36,g19)
    c: Horizontal(g36)
    c: Coincident(g37,g6)
    c: Coincident(g37,g19)
    c: Horizontal(g37)
    c: Coincident(g38,g7)
    c: Coincident(g38,g18)
    c: Horizontal(g38)
    c: Coincident(g39,g7)
    c: Coincident(g39,g18)
    c: Horizontal(g39)
    c: Coincident(g40,g8)
    c: Coincident(g40,g20)
    c: Horizontal(g40)
    c: Coincident(g41,g8)
    c: Coincident(g41,g20)
    c: Horizontal(g41)
    c: Coincident(g42,g9)
    c: Coincident(g42,g23)
    c: Horizontal(g42)
    c: Coincident(g43,g9)
    c: Coincident(g43,g23)
    c: Horizontal(g43)
    c: Coincident(g44,g10)
    c: Coincident(g44,g22)
    c: Horizontal(g44)
    c: Coincident(g45,g10)
    c: Coincident(g45,g22)
    c: Horizontal(g45)
    c: Coincident(g46,g11)
    c: Coincident(g46,g21)
    c: Horizontal(g46)
    c: Coincident(g47,g11)
    c: Coincident(g47,g21)
    c: Horizontal(g47)
FEATURE [Part::Extrusion] Extrude061
  Base = -> Sketch070
  Dir = (1,0,0)
  DirMode = 2
  FaceMakerClass = Part::FaceMakerBullseye
  LengthFwd = 23
  LengthRev = 0
  Placement = pos=(-19,0,0) rot=(0,0,1;0rad)
  Solid = true
  Symmetric = false
FEATURE [Part::Fillet] Fillet052  label="removeToCreateVentalationHoles002"
  Base = -> Extrude061
  Edges = <same value as first occurrence — deduplicated (x6 in doc)>
  Placement = pos=(7,0.02,0) rot=(0,0,1;0rad)
FEATURE [Part::MultiFuse] Fusion130  label="bottom013"
  Shapes = -> [Cut054,Cut034]
FEATURE [Part::Cut] Cut055
  Base = -> Fusion130
  Tool = -> Fillet052
FEATURE [Part::Cylinder] Cylinder054
  Angle = 360
  AttacherType = Attacher::AttachEngine3D
  Height = 20
  Placement = pos=(0,0,36.15) rot=(0,0,1;0rad)
  Radius = 4
FEATURE [Sketcher::SketchObject] Sketch071  label="bottomSketch002"
  FullyConstrained = true
  sketch-geometry (32):
    g0: LineSegment StartX=3.3 StartY=-6.03275e-07 StartZ=0 EndX=98 EndY=-6.03275e-07 EndZ=0
    g1: ArcOfCircle CenterX=98 CenterY=19 CenterZ=0 NormalX=0 NormalY=0 NormalZ=1 AngleXU=0 Radius=19 StartAngle=4.71239 EndAngle=5.71103
    g2: LineSegment StartX=6.3 StartY=8 StartZ=0 EndX=3.3 EndY=8 EndZ=0
    g3: LineSegment StartX=3.3 StartY=8 StartZ=0 EndX=3.3 EndY=-6.03275e-07 EndZ=0
    g4: ArcOfCircle CenterX=8.3 CenterY=5 CenterZ=0 NormalX=0 NormalY=0 NormalZ=1 AngleXU=0 Radius=2 StartAngle=3.14159 EndAngle=4.71239
    g5: LineSegment StartX=6.3 StartY=8 StartZ=0 EndX=6.3 EndY=5 EndZ=0
    g6: ArcOfCircle CenterX=98 CenterY=19 CenterZ=0 NormalX=0 NormalY=0 NormalZ=1 AngleXU=0 Radius=12.7 StartAngle=4.71239 EndAngle=6.28319
    g7: LineSegment StartX=94.7 StartY=3 StartZ=0 EndX=8.3 EndY=3 EndZ=0
    g8-g12: Circle x5 (B-spline internal-alignment scaffolding for g13; pole/knot coordinates omitted)
    g13: BSplineCurve PolesCount=5 KnotsCount=3 Degree=3 IsPeriodic=0
    g14: GeomPoint X=98 Y=6.3 Z=0
    g15: GeomPoint X=96.3938 Y=4.71946 Z=0
    g16: GeomPoint X=94.7 Y=3 Z=0
    g17-g23: Circle x7 (B-spline internal-alignment scaffolding for g24; pole/knot coordinates omitted)
    g24: BSplineCurve PolesCount=7 KnotsCount=5 Degree=3 IsPeriodic=0
    g25-g29: GeomPoint x5 (B-spline internal-alignment scaffolding for g24; pole/knot coordinates omitted)
    g30: ArcOfCircle CenterX=98 CenterY=19 CenterZ=0 NormalX=0 NormalY=0 NormalZ=1 AngleXU=0 Radius=15.7 StartAngle=5.81226 EndAngle=6.28319
    g31: LineSegment StartX=110.7 StartY=19 StartZ=0 EndX=113.7 EndY=19 EndZ=0
  constraints (41):
    c: Horizontal(g0)
    c: Coincident(g1,g0)
    c: Block(g1)
    c: Horizontal(g2)
    c: Distance(g2) = 3
    c: Coincident(g3,g2)
    c: Vertical(g3)
    c: Coincident(g3,g0)
    c: Block(g4)
    c: Block(g2)
    c: Coincident(g5,g2)
    c: Coincident(g5,g4)
    c: Vertical(g5)
    c: Coincident(g6,g1)
    c: Block(g6)
    c: Coincident(g7,g4)
    c: Horizontal(g7)
    c: Block(g0)
    c: Block(g7)
    c: Block(g3)
    c: Coincident(g13,g6)
    c: Weight(g8) = 1
    c: Equal(g8, g9-g12) x4
    c: Coincident(g13,g7)
    c: InternalAlignment(g8-g12 -> g13) x5
    c: InternalAlignment(g14,g13)
    c: InternalAlignment(g15,g13)
    c: InternalAlignment(g16,g13)
    c: Block(g13)
    c: Weight(g17) = 1
    c: Equal(g17, g18-g23) x6
    c: Coincident(g24,g1)
    c: InternalAlignment(g17-g23 -> g24) x7
    c: InternalAlignment(g25-g29 -> g24) x5
    c: Block(g24)
    c: Coincident(g30,g24)
    c: Coincident(g31,g6)
    c: Coincident(g31,g30)
    c: Horizontal(g31)
    c: Block(g31)
    c: Block(g30)
FEATURE [Part::Extrusion] Extrude062  label="bottom014"
  Base = -> Sketch071
  Dir = (0,0,1)
  DirMode = 2
  FaceMakerClass = Part::FaceMakerBullseye
  LengthFwd = 71.4
  LengthRev = 0
  Placement = pos=(0,0,0.3) rot=(0,0,1;0rad)
  Solid = true
  Symmetric = false
FEATURE [Part::Fillet] Fillet054
  Base = -> Extrude062
  Edges = 1 edges r=2.4: [Edge17]
FEATURE [Part::Fillet] Fillet055  label="bottom015"
  Base = -> Fillet054
  Edges = 1 edges r=2.4: [Edge36]
FEATURE [Part::Cylinder] Cylinder055
  Angle = 360
  AttacherType = Attacher::AttachEngine3D
  Height = 10
  Placement = pos=(0,0,36.15) rot=(0,0,1;0rad)
  Radius = 4
FEATURE [Part::MultiFuse] Fusion131  label="removeToCreateHoleForPlugHousing002"
  Placement = pos=(70,19,36.15) rot=(0,1,0;1.5708rad)
  Shapes = -> [Cylinder054,Cylinder055]
FEATURE [Part::Cut] Cut056  label="Bottom001"
  Base = -> Fillet055
  Placement = pos=(9,0,0) rot=(0,0,1;0rad)
  Tool = -> Fusion131
FEATURE [Part::Cut] Cut057
  Base = -> Cut055
  Tool = -> Cut056
FEATURE [Sketcher::SketchObject] Sketch072  label="topSketch021"
  FullyConstrained = true
  sketch-geometry (4):
    g0: ArcOfCircle CenterX=105 CenterY=19 CenterZ=0 NormalX=0 NormalY=0 NormalZ=1 AngleXU=0 Radius=20.6155 StartAngle=5.54125 EndAngle=6.28319
    g1: ArcOfCircle CenterX=105 CenterY=19 CenterZ=0 NormalX=0 NormalY=0 NormalZ=1 AngleXU=0 Radius=13 StartAngle=5.54125 EndAngle=6.28319
    g2: LineSegment StartX=118 StartY=19 StartZ=0 EndX=125.616 EndY=19 EndZ=0
    g3: LineSegment StartX=114.583 StartY=10.2157 StartZ=0 EndX=120.197 EndY=5.06982 EndZ=0
  constraints (7):
    c: Block(g0)
    c: Block(g1)
    c: Coincident(g2,g1)
    c: Coincident(g2,g0)
    c: Horizontal(g2)
    c: Coincident(g3,g1)
    c: Coincident(g3,g0)
FEATURE [Part::Extrusion] Extrude063  label="bottomPlugHousingBit003"
  Base = -> Sketch072
  Dir = (0,0,1)
  DirMode = 2
  FaceMakerClass = Part::FaceMakerBullseye
  LengthFwd = 72
  LengthRev = 0
  Solid = true
  Symmetric = false
FEATURE [Part::Cylinder] Cylinder056
  Angle = 360
  AttacherType = Attacher::AttachEngine3D
  Height = 20
  Placement = pos=(0,0,36.15) rot=(0,0,1;0rad)
  Radius = 14.3
FEATURE [Part::Cylinder] Cylinder057
  Angle = 360
  AttacherType = Attacher::AttachEngine3D
  Height = 10
  Placement = pos=(0,0,36.15) rot=(0,0,1;0rad)
  Radius = 4
FEATURE [Part::Box] Box034  label="removeToCreteHoleForPlugHousing047"
  AttacherType = Attacher::AttachEngine3D
  Height = 28.6
  Length = 20
  Placement = pos=(106.15,0,21.7) rot=(0,0,1;0rad)
  Width = 19
FEATURE [Part::Cylinder] Cylinder058
  Angle = 360
  AttacherType = Attacher::AttachEngine3D
  Height = 20
  Placement = pos=(0,0,36.15) rot=(0,0,1;0rad)
  Radius = 14.3
FEATURE [Part::Cylinder] Cylinder059
  Angle = 360
  AttacherType = Attacher::AttachEngine3D
  Height = 10
  Placement = pos=(0,0,36.15) rot=(0,0,1;0rad)
  Radius = 4
FEATURE [Part::MultiFuse] Fusion134  label="removeToCreteHoleForPlugHousing046"
  Placement = pos=(70,19,36) rot=(0,1,0;1.5708rad)
  Shapes = -> [Cylinder058,Cylinder059]
FEATURE [Part::Cylinder] Cylinder060
  Angle = 360
  AttacherType = Attacher::AttachEngine3D
  Height = 20
  Placement = pos=(0,0,36.15) rot=(0,0,1;0rad)
  Radius = 14
FEATURE [Part::Cylinder] Cylinder061
  Angle = 360
  AttacherType = Attacher::AttachEngine3D
  Height = 10
  Placement = pos=(0,0,36.15) rot=(0,0,1;0rad)
  Radius = 4
FEATURE [Part::MultiFuse] Fusion135  label="removeToCreteHoleForPlugHousing048"
  Placement = pos=(70,19,36) rot=(0,1,0;1.5708rad)
  Shapes = -> [Cylinder060,Cylinder061]
FEATURE [Part::Box] Box035  label="removeToCreteHoleForPlugHousing049"
  AttacherType = Attacher::AttachEngine3D
  Height = 28.6
  Length = 20
  Placement = pos=(106.15,0,21.7) rot=(0,0,1;0rad)
  Width = 19
FEATURE [Part::MultiFuse] Fusion133  label="removeToCreteHoleForPlugHousing045"
  Placement = pos=(0,0,-28.3) rot=(0,0,1;0rad)
  Shapes = -> [Box035,Fusion134]
FEATURE [Part::MultiFuse] Fusion138  label="removeToCreteHoleForPlugHousing051"
  Placement = pos=(70,19,36) rot=(0,1,0;1.5708rad)
  Shapes = -> [Cylinder056,Cylinder057]
FEATURE [Part::MultiFuse] Fusion137  label="removeToCreteHoleForPlugHousing050"
  Placement = pos=(0,0,28.3) rot=(0,0,1;0rad)
  Shapes = -> [Box034,Fusion138]
FEATURE [Part::MultiFuse] Fusion132  label="removeToCreatePlugHousingBottomBit002"
  Shapes = -> [Fusion133,Fusion137]
FEATURE [Part::MultiFuse] Fusion136  label="removeToCreatePlugHousingBottomBit003"
  Shapes = -> [Fusion135,Fusion132]
FEATURE [Part::Cut] Cut058  label="bottomPlugHousingBit002"
  Base = -> Extrude063
  Placement = pos=(-0.09,0,0) rot=(0,0,1;0rad)
  Tool = -> Fusion136
FEATURE [Sketcher::SketchObject] Sketch073  label="bottomSketch003"
  FullyConstrained = true
  sketch-geometry (45):
    g0: LineSegment StartX=6.29999 StartY=8 StartZ=0 EndX=3.29999 EndY=8 EndZ=0
    g1: LineSegment StartX=3.29999 StartY=8 StartZ=0 EndX=3.29999 EndY=-6.03275e-07 EndZ=0
    g2: ArcOfCircle CenterX=8.29999 CenterY=5 CenterZ=0 NormalX=0 NormalY=0 NormalZ=1 AngleXU=0 Radius=2 StartAngle=3.14159 EndAngle=4.71239
    g3: LineSegment StartX=6.29999 StartY=8 StartZ=0 EndX=6.29999 EndY=5 EndZ=0
    g4: ArcOfCircle CenterX=105 CenterY=19 CenterZ=0 NormalX=0 NormalY=0 NormalZ=1 AngleXU=0 Radius=12.7 StartAngle=4.71239 EndAngle=5.94289
    g5-g11: Circle x7 (B-spline internal-alignment scaffolding for g12; pole/knot coordinates omitted)
    g12: BSplineCurve PolesCount=7 KnotsCount=5 Degree=3 IsPeriodic=0
    g13-g17: GeomPoint x5 (B-spline internal-alignment scaffolding for g12; pole/knot coordinates omitted)
    g18: ArcOfCircle CenterX=105 CenterY=19 CenterZ=0 NormalX=0 NormalY=0 NormalZ=1 AngleXU=0 Radius=15.7 StartAngle=5.81226 EndAngle=6.28319
    g19: BSplineCurve PolesCount=5 KnotsCount=3 Degree=3 IsPeriodic=0
    g20: LineSegment StartX=8.29999 StartY=3 StartZ=0 EndX=101.7 EndY=3 EndZ=0
    g21: LineSegment StartX=3.29999 StartY=-6.03275e-07 StartZ=0 EndX=105 EndY=-6.03275e-07 EndZ=0
    g22: LineSegment StartX=120.974 StartY=8.71251 StartZ=0 EndX=122.332 EndY=7.83778 EndZ=0
    g23: LineSegment StartX=105 StartY=-6.03274e-07 StartZ=0 EndX=113 EndY=-6.03274e-07 EndZ=0
    g24: ArcOfCircle CenterX=105 CenterY=19 CenterZ=0 NormalX=0 NormalY=0 NormalZ=1 AngleXU=0 Radius=20.6155 StartAngle=5.11091 EndAngle=5.71103
    g25: ArcOfCircle CenterX=117.7 CenterY=19 CenterZ=0 NormalX=0 NormalY=0 NormalZ=1 AngleXU=0 Radius=3 StartAngle=1.2e-15 EndAngle=2.10468
    g26: Circle CenterX=116.345 CenterY=16.3232 CenterZ=0 NormalX=0 NormalY=0 NormalZ=1 AngleXU=0 Radius=1
    g27: Circle CenterX=117.24 CenterY=15.7584 CenterZ=0 NormalX=0 NormalY=0 NormalZ=1 AngleXU=0 Radius=1
    g28: Circle CenterX=116.972 CenterY=14.7612 CenterZ=0 NormalX=0 NormalY=0 NormalZ=1 AngleXU=0 Radius=1
    g29: BSplineCurve PolesCount=3 KnotsCount=2 Degree=2 IsPeriodic=0
    g30: GeomPoint X=116.345 Y=16.3232 Z=0
    g31: GeomPoint X=116.972 Y=14.7612 Z=0
    g32: Circle CenterX=115.828 CenterY=17.157 CenterZ=0 NormalX=0 NormalY=0 NormalZ=1 AngleXU=0 Radius=1
    g33: Circle CenterX=115.841 CenterY=16.639 CenterZ=0 NormalX=0 NormalY=0 NormalZ=1 AngleXU=0 Radius=1
    g34: Circle CenterX=116.345 CenterY=16.3232 CenterZ=0 NormalX=0 NormalY=0 NormalZ=1 AngleXU=0 Radius=1
    g35: BSplineCurve PolesCount=3 KnotsCount=2 Degree=2 IsPeriodic=0
    g36: GeomPoint X=115.828 Y=17.157 Z=0
    g37: GeomPoint X=116.345 Y=16.3232 Z=0
    g38: LineSegment StartX=115.828 StartY=17.157 StartZ=0 EndX=115.828 EndY=20.8307 EndZ=0
    g39: Circle CenterX=115.828 CenterY=20.8307 CenterZ=0 NormalX=0 NormalY=0 NormalZ=1 AngleXU=0 Radius=1
    g40: Circle CenterX=115.831 CenterY=21.3396 CenterZ=0 NormalX=0 NormalY=0 NormalZ=1 AngleXU=0 Radius=1
    g41: Circle CenterX=116.173 CenterY=21.5825 CenterZ=0 NormalX=0 NormalY=0 NormalZ=1 AngleXU=0 Radius=1
    g42: BSplineCurve PolesCount=3 KnotsCount=2 Degree=2 IsPeriodic=0
    g43: GeomPoint X=115.828 Y=20.8307 Z=0
    g44: GeomPoint X=116.173 Y=21.5825 Z=0
  constraints (70):
    c: Horizontal(g0)
    c: Distance(g0) = 3
    c: Coincident(g1,g0)
    c: Vertical(g1)
    c: Block(g2)
    c: Block(g0)
    c: Coincident(g3,g0)
    c: Coincident(g3,g2)
    c: Vertical(g3)
    c: Block(g1)
    c: Block(g4)
    c: Coincident(g19,g4)
    c: Block(g19)
    c: Equal(g5, g6-g11) x6
    c: InternalAlignment(g5-g11 -> g12) x7
    c: InternalAlignment(g13-g17 -> g12) x5
    c: Block(g12)
    c: Coincident(g18,g12)
    c: Block(g18)
    c: Coincident(g20,g2)
    c: Coincident(g20,g19)
    c: Horizontal(g20)
    c: Distance(g20) = 93.4
    c: Coincident(g21,g1)
    c: Horizontal(g21)
    c: Distance(g21) = 101.7
    c: Horizontal(g23)
    c: Distance(g23) = 8
    c: Coincident(g24,g23)
    c: Block(g23)
    c: Coincident(g22,g24)
    c: Block(g24)
    c: Block(g22)
    c: Distance(g22) = 1.61553
    c: Coincident(g25,g18)
    c: Block(g25)
    c: Weight(g26) = 1
    c: Equal(g26,g27)
    c: Equal(g26,g28)
    c: Coincident(g29,g4)
    c: InternalAlignment(g26,g29)
    c: InternalAlignment(g27,g29)
    c: InternalAlignment(g28,g29)
    c: InternalAlignment(g30,g29)
    c: InternalAlignment(g31,g29)
    c: Block(g29)
    c: Weight(g32) = 1
    c: Equal(g32,g33)
    c: Equal(g32,g34)
    c: Coincident(g35,g29)
    c: InternalAlignment(g32,g35)
    c: InternalAlignment(g33,g35)
    c: InternalAlignment(g34,g35)
    c: InternalAlignment(g36,g35)
    c: InternalAlignment(g37,g35)
    c: Block(g35)
    c: Coincident(g38,g35)
    c: Vertical(g38)
    c: Block(g38)
    c: Coincident(g42,g38)
    c: Weight(g39) = 1
    c: Equal(g39,g40)
    c: Equal(g39,g41)
    c: Coincident(g42,g25)
    c: InternalAlignment(g39,g42)
    c: InternalAlignment(g40,g42)
    c: InternalAlignment(g41,g42)
    c: InternalAlignment(g43,g42)
    c: InternalAlignment(g44,g42)
    c: Block(g42)
FEATURE [Part::Extrusion] Extrude064  label="bottom016"
  Base = -> Sketch073
  Dir = (0,0,1)
  DirMode = 2
  FaceMakerClass = Part::FaceMakerBullseye
  LengthFwd = 71.4
  LengthRev = 0
  Placement = pos=(0,0,0.3) rot=(0,0,1;0rad)
  Solid = true
  Symmetric = false
FEATURE [Part::Revolution] Revolve157  label="removeToCreateScrewAndThreadedInsertHole063"
  Angle = 360
  Axis = (0,1,0)
  Base = (0,0,0)
  FaceMakerClass = Part::FaceMakerBullseye
  Placement = pos=(12.5,0,10) rot=(0,0,1;0rad)
  Solid = false
  Source = -> Face141
  Symmetric = false
FEATURE [Sketcher::SketchObject] Sketch074
  FullyConstrained = true
  Placement = pos=(117,19,0) rot=(0.57735,0.57735,0.57735;2.0944rad)
  sketch-geometry (48):
    g0: LineSegment StartX=-49.19 StartY=69.25 StartZ=0 EndX=-49.19 EndY=66.25 EndZ=0
    g1: LineSegment StartX=-49.19 StartY=63.5 StartZ=0 EndX=-49.19 EndY=60.5 EndZ=0
    g2: LineSegment StartX=-49.19 StartY=57.75 StartZ=0 EndX=-49.19 EndY=54.75 EndZ=0
    g3: LineSegment StartX=-49.19 StartY=52 StartZ=0 EndX=-49.19 EndY=49 EndZ=0
    g4: LineSegment StartX=-49.19 StartY=46.25 StartZ=0 EndX=-49.19 EndY=43.25 EndZ=0
    g5: LineSegment StartX=-49.19 StartY=40.5 StartZ=0 EndX=-49.19 EndY=37.5 EndZ=0
    g6: LineSegment StartX=-49.19 StartY=34.5 StartZ=0 EndX=-49.19 EndY=31.5 EndZ=0
    g7: LineSegment StartX=-49.19 StartY=28.75 StartZ=0 EndX=-49.19 EndY=25.75 EndZ=0
    g8: LineSegment StartX=-49.19 StartY=23 StartZ=0 EndX=-49.19 EndY=20 EndZ=0
    g9: LineSegment StartX=-49.19 StartY=17.25 StartZ=0 EndX=-49.19 EndY=14.25 EndZ=0
    g10: LineSegment StartX=-49.19 StartY=11.5 StartZ=0 EndX=-49.19 EndY=8.5 EndZ=0
    g11: LineSegment StartX=-49.19 StartY=5.75 StartZ=0 EndX=-49.19 EndY=2.75 EndZ=0
    g12: ArcOfCircle CenterX=-1.5 CenterY=67.75 CenterZ=0 NormalX=0 NormalY=0 NormalZ=1 AngleXU=0 Radius=1.5 StartAngle=4.71239 EndAngle=7.85398
    g13: ArcOfCircle CenterX=-1.5 CenterY=62 CenterZ=0 NormalX=0 NormalY=0 NormalZ=1 AngleXU=0 Radius=1.5 StartAngle=4.71239 EndAngle=7.85398
    g14: ArcOfCircle CenterX=-1.5 CenterY=56.25 CenterZ=0 NormalX=0 NormalY=0 NormalZ=1 AngleXU=0 Radius=1.5 StartAngle=4.71239 EndAngle=7.85398
    g15: ArcOfCircle CenterX=-11.49 CenterY=50.5 CenterZ=0 NormalX=0 NormalY=0 NormalZ=1 AngleXU=0 Radius=1.5 StartAngle=4.71239 EndAngle=7.85398
    g16: ArcOfCircle CenterX=-16.28 CenterY=44.75 CenterZ=0 NormalX=0 NormalY=0 NormalZ=1 AngleXU=0 Radius=1.5 StartAngle=4.71239 EndAngle=7.85398
    g17: ArcOfCircle CenterX=-18.2337 CenterY=39 CenterZ=0 NormalX=0 NormalY=0 NormalZ=1 AngleXU=0 Radius=1.5 StartAngle=4.71485 EndAngle=7.85398
    g18: ArcOfCircle CenterX=-16.2837 CenterY=27.25 CenterZ=0 NormalX=0 NormalY=0 NormalZ=1 AngleXU=0 Radius=1.5 StartAngle=4.71485 EndAngle=7.85398
    g19: ArcOfCircle CenterX=-18.2337 CenterY=33 CenterZ=0 NormalX=0 NormalY=0 NormalZ=1 AngleXU=0 Radius=1.5 StartAngle=4.71485 EndAngle=7.85398
    g20: ArcOfCircle CenterX=-11.49 CenterY=21.5 CenterZ=0 NormalX=0 NormalY=0 NormalZ=1 AngleXU=0 Radius=1.5 StartAngle=4.71239 EndAngle=7.85398
    g21: ArcOfCircle CenterX=-1.5 CenterY=4.25 CenterZ=0 NormalX=0 NormalY=0 NormalZ=1 AngleXU=0 Radius=1.5 StartAngle=4.71239 EndAngle=7.85398
    g22: ArcOfCircle CenterX=-1.5 CenterY=10 CenterZ=0 NormalX=0 NormalY=0 NormalZ=1 AngleXU=0 Radius=1.5 StartAngle=4.71239 EndAngle=7.85398
    g23: ArcOfCircle CenterX=-1.5 CenterY=15.75 CenterZ=0 NormalX=0 NormalY=0 NormalZ=1 AngleXU=0 Radius=1.5 StartAngle=4.71239 EndAngle=7.85398
    g24: LineSegment StartX=-49.19 StartY=69.25 StartZ=0 EndX=-1.5 EndY=69.25 EndZ=0
    g25: LineSegment StartX=-49.19 StartY=66.25 StartZ=0 EndX=-1.5 EndY=66.25 EndZ=0
    g26: LineSegment StartX=-49.19 StartY=63.5 StartZ=0 EndX=-1.5 EndY=63.5 EndZ=0
    g27: LineSegment StartX=-49.19 StartY=60.5 StartZ=0 EndX=-1.5 EndY=60.5 EndZ=0
    g28: LineSegment StartX=-49.19 StartY=57.75 StartZ=0 EndX=-1.5 EndY=57.75 EndZ=0
    g29: LineSegment StartX=-49.19 StartY=54.75 StartZ=0 EndX=-1.5 EndY=54.75 EndZ=0
    g30: LineSegment StartX=-49.19 StartY=52 StartZ=0 EndX=-11.49 EndY=52 EndZ=0
    g31: LineSegment StartX=-49.19 StartY=49 StartZ=0 EndX=-11.49 EndY=49 EndZ=0
    g32: LineSegment StartX=-49.19 StartY=46.25 StartZ=0 EndX=-16.28 EndY=46.25 EndZ=0
    g33: LineSegment StartX=-49.19 StartY=43.25 StartZ=0 EndX=-16.28 EndY=43.25 EndZ=0
    g34: LineSegment StartX=-49.19 StartY=40.5 StartZ=0 EndX=-18.2337 EndY=40.5 EndZ=0
    g35: LineSegment StartX=-49.19 StartY=37.5 StartZ=0 EndX=-18.23 EndY=37.5 EndZ=0
    g36: LineSegment StartX=-49.19 StartY=34.5 StartZ=0 EndX=-18.2337 EndY=34.5 EndZ=0
    g37: LineSegment StartX=-49.19 StartY=31.5 StartZ=0 EndX=-18.23 EndY=31.5 EndZ=0
    g38: LineSegment StartX=-49.19 StartY=28.75 StartZ=0 EndX=-16.2837 EndY=28.75 EndZ=0
    g39: LineSegment StartX=-49.19 StartY=25.75 StartZ=0 EndX=-16.28 EndY=25.75 EndZ=0
    g40: LineSegment StartX=-49.19 StartY=23 StartZ=0 EndX=-11.49 EndY=23 EndZ=0
    g41: LineSegment StartX=-49.19 StartY=20 StartZ=0 EndX=-11.49 EndY=20 EndZ=0
    g42: LineSegment StartX=-49.19 StartY=17.25 StartZ=0 EndX=-1.5 EndY=17.25 EndZ=0
    g43: LineSegment StartX=-49.19 StartY=14.25 StartZ=0 EndX=-1.5 EndY=14.25 EndZ=0
    g44: LineSegment StartX=-49.19 StartY=11.5 StartZ=0 EndX=-1.5 EndY=11.5 EndZ=0
    g45: LineSegment StartX=-49.19 StartY=8.5 StartZ=0 EndX=-1.5 EndY=8.5 EndZ=0
    g46: LineSegment StartX=-49.19 StartY=5.75 StartZ=0 EndX=-1.5 EndY=5.75 EndZ=0
    g47: LineSegment StartX=-49.19 StartY=2.75 StartZ=0 EndX=-1.5 EndY=2.75 EndZ=0
  constraints (120):
    c: Vertical(g0)
    c: Distance(g0) = 3
    c: Block(g0)
    c: Vertical(g1)
    c: Distance(g1) = 3
    c: Vertical(g2)
    c: Equal(g0,g2) = 3
    c: Block(g2)
    c: Vertical(g3)
    c: Equal(g1,g3) = 3
    c: Vertical(g4)
    c: Equal(g0,g4) = 3
    c: Block(g4)
    c: Vertical(g5)
    c: Equal(g1,g5) = 3
    c: Vertical(g6)
    c: Equal(g0,g6) = 3
    c: Block(g6)
    c: Vertical(g7)
    c: Equal(g1,g7) = 3
    c: Vertical(g8)
    c: Equal(g0,g8) = 3
    c: Block(g8)
    c: Vertical(g9)
    c: Equal(g1,g9) = 3
    c: Vertical(g10)
    c: Equal(g0,g10) = 3
    c: Block(g10)
    c: Vertical(g11)
    c: Equal(g1,g11) = 3
    c: Block(g12)
    c: Block(g13)
    c: Block(g14)
    c: Block(g15)
    c: Block(g16)
    c: Block(g17)
    c: Block(g18)
    c: Block(g19)
    c: Block(g20)
    c: Block(g21)
    c: Block(g22)
    c: Block(g23)
    c: Block(g11)
    c: Block(g9)
    c: Block(g7)
    c: Block(g5)
    c: Block(g3)
    c: Block(g1)
    c: Coincident(g24,g0)
    c: Coincident(g24,g12)
    c: Horizontal(g24)
    c: Coincident(g25,g0)
    c: Coincident(g25,g12)
    c: Horizontal(g25)
    c: Coincident(g26,g1)
    c: Coincident(g26,g13)
    c: Horizontal(g26)
    c: Coincident(g27,g1)
    c: Coincident(g27,g13)
    c: Horizontal(g27)
    c: Coincident(g28,g2)
    c: Coincident(g28,g14)
    c: Horizontal(g28)
    c: Coincident(g29,g2)
    c: Coincident(g29,g14)
    c: Horizontal(g29)
    c: Coincident(g30,g3)
    c: Coincident(g30,g15)
    c: Horizontal(g30)
    c: Coincident(g31,g3)
    c: Coincident(g31,g15)
    c: Horizontal(g31)
    c: Coincident(g32,g4)
    c: Coincident(g32,g16)
    c: Horizontal(g32)
    c: Coincident(g33,g4)
    c: Coincident(g33,g16)
    c: Horizontal(g33)
    c: Coincident(g34,g5)
    c: Coincident(g34,g17)
    c: Horizontal(g34)
    c: Coincident(g35,g5)
    c: Coincident(g35,g17)
    c: Horizontal(g35)
    c: Coincident(g36,g6)
    c: Coincident(g36,g19)
    c: Horizontal(g36)
    c: Coincident(g37,g6)
    c: Coincident(g37,g19)
    c: Horizontal(g37)
    c: Coincident(g38,g7)
    c: Coincident(g38,g18)
    c: Horizontal(g38)
    c: Coincident(g39,g7)
    c: Coincident(g39,g18)
    c: Horizontal(g39)
    c: Coincident(g40,g8)
    c: Coincident(g40,g20)
    c: Horizontal(g40)
    c: Coincident(g41,g8)
    c: Coincident(g41,g20)
    c: Horizontal(g41)
    c: Coincident(g42,g9)
    c: Coincident(g42,g23)
    c: Horizontal(g42)
    c: Coincident(g43,g9)
    c: Coincident(g43,g23)
    c: Horizontal(g43)
    c: Coincident(g44,g10)
    c: Coincident(g44,g22)
    c: Horizontal(g44)
    c: Coincident(g45,g10)
    c: Coincident(g45,g22)
    c: Horizontal(g45)
    c: Coincident(g46,g11)
    c: Coincident(g46,g21)
    c: Horizontal(g46)
    c: Coincident(g47,g11)
    c: Coincident(g47,g21)
    c: Horizontal(g47)
FEATURE [Part::Extrusion] Extrude065
  Base = -> Sketch074
  Dir = (1,0,0)
  DirMode = 2
  FaceMakerClass = Part::FaceMakerBullseye
  LengthFwd = 23
  LengthRev = 0
  Placement = pos=(-19,0,0) rot=(0,0,1;0rad)
  Solid = true
  Symmetric = false
FEATURE [Part::Fillet] Fillet056  label="removeToCreateVentalationHoles003"
  Base = -> Extrude065
  Edges = <same value as first occurrence — deduplicated (x6 in doc)>
  Placement = pos=(7,0.02,0) rot=(0,0,1;0rad)
FEATURE [Part::Revolution] Revolve158  label="removeToCreateScrewAndThreadedInsertHole065"
  Angle = 360
  Axis = (0,1,0)
  Base = (0,0,0)
  FaceMakerClass = Part::FaceMakerBullseye
  Placement = pos=(12.5,0,62) rot=(0,0,1;0rad)
  Solid = false
  Source = -> Face146
  Symmetric = false
FEATURE [Part::Revolution] Revolve159  label="removeToCreateScrewAndThreadedInsertHole066"
  Angle = 360
  Axis = (0,1,0)
  Base = (0,0,0)
  FaceMakerClass = Part::FaceMakerBullseye
  Placement = pos=(89.5,0,68.5) rot=(0,0,1;0rad)
  Solid = false
  Source = -> Face143
  Symmetric = false
FEATURE [Part::Revolution] Revolve160  label="removeToCreateScrewAndThreadedInsertHole067"
  Angle = 360
  Axis = (0,1,0)
  Base = (0,0,0)
  FaceMakerClass = Part::FaceMakerBullseye
  Placement = pos=(89.5,0,3.5) rot=(0,0,1;0rad)
  Solid = false
  Source = -> Face142
  Symmetric = false
FEATURE [Part::Revolution] Revolve161  label="removeToCreateScrewAndThreadedInsertHole068"
  Angle = 360
  Axis = (0,1,0)
  Base = (0,0,0)
  FaceMakerClass = Part::FaceMakerBullseye
  Placement = pos=(109.5,4.7,3.5) rot=(0,0,1;0rad)
  Solid = false
  Source = -> Face145
  Symmetric = false
FEATURE [Part::Revolution] Revolve162  label="removeToCreateScrewAndThreadedInsertHole069"
  Angle = 360
  Axis = (0,1,0)
  Base = (0,0,0)
  FaceMakerClass = Part::FaceMakerBullseye
  Placement = pos=(109.5,4.7,68.5) rot=(0,0,1;0rad)
  Solid = false
  Source = -> Face144
  Symmetric = false
FEATURE [Part::MultiFuse] Fusion141  label="removeToCreateScrewAndThreadedInsertHole064"
  Shapes = -> [Revolve162,Revolve161,Revolve160,Revolve159,Revolve158,Revolve157]
FEATURE [Part::Cylinder] Cylinder062
  Angle = 360
  AttacherType = Attacher::AttachEngine3D
  Height = 20
  Placement = pos=(0,0,36.15) rot=(0,0,1;0rad)
  Radius = 14
FEATURE [Part::Cylinder] Cylinder063
  Angle = 360
  AttacherType = Attacher::AttachEngine3D
  Height = 10
  Placement = pos=(0,0,36.15) rot=(0,0,1;0rad)
  Radius = 4
FEATURE [Part::MultiFuse] Fusion139  label="removeToCreteHoleForPlugHousing052"
  Placement = pos=(70,19,36) rot=(0,1,0;1.5708rad)
  Shapes = -> [Cylinder062,Cylinder063]
FEATURE [Part::Cut] Cut060  label="bottom017"
  Base = -> Extrude064
  Tool = -> Fusion139
FEATURE [Part::Cut] Cut061  label="bottom019"
  Base = -> Cut060
  Tool = -> Fusion141
FEATURE [Part::MultiFuse] Fusion140  label="bottom018"
  Shapes = -> [Cut061,Cut058]
FEATURE [Part::Cut] Cut059  label="bottom020"
  Base = -> Fusion140
  Tool = -> Fillet056
FEATURE [Part::Box] Box036  label="Cube021"
  AttacherType = Attacher::AttachEngine3D
  Height = 80
  Length = 26
  Placement = pos=(0,-1,-5) rot=(0,0,1;0rad)
  Width = 11
FEATURE [Part::Cut] Cut062  label="removeFromBottom002"
  Base = -> Cut057
  Tool = -> Box036
FEATURE [Part::Cut] Cut063
  Base = -> Cut059
  Tool = -> Cut062
FEATURE [Part::Cut] Cut064  label="pcbStands"
  Base = -> Fusion095
  Tool = -> Fusion127
FEATURE [Sketcher::SketchObject] Sketch075  label="topSketch022"
  FullyConstrained = true
  sketch-geometry (6):
    g0: LineSegment StartX=19 StartY=38 StartZ=0 EndX=117 EndY=38 EndZ=0
    g1: ArcOfCircle CenterX=19 CenterY=19 CenterZ=0 NormalX=0 NormalY=0 NormalZ=1 AngleXU=0 Radius=19 StartAngle=1.5708 EndAngle=3.14159
    g2: LineSegment StartX=117 StartY=38 StartZ=0 EndX=117 EndY=19 EndZ=0
    g3: LineSegment StartX=98 StartY=1.0161e-12 StartZ=0 EndX=5.22862e-06 EndY=1.0161e-12 EndZ=0
    g4: LineSegment StartX=5.22862e-06 StartY=19 StartZ=0 EndX=5.22862e-06 EndY=1.0161e-12 EndZ=0
    g5: ArcOfCircle CenterX=98 CenterY=19 CenterZ=0 NormalX=0 NormalY=0 NormalZ=1 AngleXU=0 Radius=19 StartAngle=4.71239 EndAngle=6.28319
  constraints (16):
    c: Horizontal(g0)
    c: Distance(g0) = 98
    c: Coincident(g1,g0)
    c: Block(g1)
    c: Coincident(g2,g0)
    c: Vertical(g2)
    c: Distance(g2) = 19
    c: Horizontal(g3)
    c: Coincident(g4,g1)
    c: Vertical(g4)
    c: Coincident(g3,g4)
    c: Block(g3)
    c: Coincident(g5,g2)
    c: Coincident(g5,g3)
    c: Block(g0)
    c: Block(g5)
FEATURE [Part::Extrusion] Extrude067  label="sideB003"
  Base = -> Sketch075
  Dir = (0,0,1)
  DirMode = 2
  FaceMakerClass = Part::FaceMakerBullseye
  LengthFwd = 3
  LengthRev = 0
  Placement = pos=(0,0,71.7) rot=(0,0,1;0rad)
  Solid = true
  Symmetric = false
FEATURE [Sketcher::SketchObject] Sketch076  label="topSketch023"
  FullyConstrained = true
  sketch-geometry (6):
    g0: LineSegment StartX=19 StartY=38 StartZ=0 EndX=117 EndY=38 EndZ=0
    g1: ArcOfCircle CenterX=19 CenterY=19 CenterZ=0 NormalX=0 NormalY=0 NormalZ=1 AngleXU=0 Radius=19 StartAngle=1.5708 EndAngle=3.14159
    g2: LineSegment StartX=117 StartY=38 StartZ=0 EndX=117 EndY=19 EndZ=0
    g3: LineSegment StartX=98 StartY=1.0161e-12 StartZ=0 EndX=5.22862e-06 EndY=1.0161e-12 EndZ=0
    g4: LineSegment StartX=5.22862e-06 StartY=19 StartZ=0 EndX=5.22862e-06 EndY=1.0161e-12 EndZ=0
    g5: ArcOfCircle CenterX=98 CenterY=19 CenterZ=0 NormalX=0 NormalY=0 NormalZ=1 AngleXU=0 Radius=19 StartAngle=4.71239 EndAngle=6.28319
  constraints (16):
    c: Horizontal(g0)
    c: Distance(g0) = 98
    c: Coincident(g1,g0)
    c: Block(g1)
    c: Coincident(g2,g0)
    c: Vertical(g2)
    c: Distance(g2) = 19
    c: Horizontal(g3)
    c: Coincident(g4,g1)
    c: Vertical(g4)
    c: Coincident(g3,g4)
    c: Block(g3)
    c: Coincident(g5,g2)
    c: Coincident(g5,g3)
    c: Block(g0)
    c: Block(g5)
FEATURE [Part::Extrusion] Extrude066  label="sideA003"
  Base = -> Sketch076
  Dir = (0,0,1)
  DirMode = 2
  FaceMakerClass = Part::FaceMakerBullseye
  LengthFwd = 3
  LengthRev = 0
  Placement = pos=(0,0,-2.7) rot=(0,0,1;0rad)
  Solid = true
  Symmetric = false
FEATURE [Part::MultiFuse] Fusion142  label="removeFromBottom003"
  Placement = pos=(2,0,0) rot=(0,0,1;0rad)
  Shapes = -> [Extrude066,Extrude067]
FEATURE [Part::Cut] Cut065  label="screwRetainers002"
  Base = -> Fusion096
  Tool = -> Fusion142
FEATURE [Sketcher::SketchObject] Sketch077
  FullyConstrained = true
  Placement = pos=(117,19,0) rot=(0.57735,0.57735,0.57735;2.0944rad)
  sketch-geometry (8):
    g0: LineSegment StartX=-49.19 StartY=63.5 StartZ=0 EndX=-49.19 EndY=60.5 EndZ=0
    g1: LineSegment StartX=-49.19 StartY=11.5 StartZ=0 EndX=-49.19 EndY=8.5 EndZ=0
    g2: ArcOfCircle CenterX=-1.5 CenterY=62 CenterZ=0 NormalX=0 NormalY=0 NormalZ=1 AngleXU=0 Radius=1.5 StartAngle=4.71239 EndAngle=7.85398
    g3: ArcOfCircle CenterX=-1.5 CenterY=10 CenterZ=0 NormalX=0 NormalY=0 NormalZ=1 AngleXU=0 Radius=1.5 StartAngle=4.71239 EndAngle=7.85398
    g4: LineSegment StartX=-49.19 StartY=63.5 StartZ=0 EndX=-1.5 EndY=63.5 EndZ=0
    g5: LineSegment StartX=-49.19 StartY=60.5 StartZ=0 EndX=-1.5 EndY=60.5 EndZ=0
    g6: LineSegment StartX=-49.19 StartY=11.5 StartZ=0 EndX=-1.5 EndY=11.5 EndZ=0
    g7: LineSegment StartX=-49.19 StartY=8.5 StartZ=0 EndX=-1.5 EndY=8.5 EndZ=0
  constraints (19):
    c: Vertical(g0)
    c: Distance(g0) = 3
    c: Vertical(g1)
    c: Block(g1)
    c: Block(g2)
    c: Block(g3)
    c: Block(g0)
    c: Coincident(g4,g0)
    c: Coincident(g4,g2)
    c: Horizontal(g4)
    c: Coincident(g5,g0)
    c: Coincident(g5,g2)
    c: Horizontal(g5)
    c: Coincident(g6,g1)
    c: Coincident(g6,g3)
    c: Horizontal(g6)
    c: Coincident(g7,g1)
    c: Coincident(g7,g3)
    c: Horizontal(g7)
FEATURE [Part::Extrusion] Extrude068
  Base = -> Sketch077
  Dir = (1,0,0)
  DirMode = 2
  FaceMakerClass = Part::FaceMakerBullseye
  LengthFwd = 10
  LengthRev = 0
  Solid = true
  Symmetric = false
FEATURE [Part::Fillet] Fillet057  label="removeFromtMoreFrontCaseScrewRetainers002"
  Base = -> Extrude068
  Edges = 4 edges r=1.49: [Edge6,Edge11,Edge18,Edge23]
  Placement = pos=(-12,0,0) rot=(0,0,1;0rad)
FEATURE [Sketcher::SketchObject] Sketch078
  FullyConstrained = true
  Placement = pos=(117,19,0) rot=(0.57735,0.57735,0.57735;2.0944rad)
  sketch-geometry (8):
    g0: LineSegment StartX=-49.19 StartY=69.25 StartZ=0 EndX=-49.19 EndY=66.25 EndZ=0
    g1: LineSegment StartX=-49.19 StartY=5.75 StartZ=0 EndX=-49.19 EndY=2.75 EndZ=0
    g2: ArcOfCircle CenterX=-1.5 CenterY=67.75 CenterZ=0 NormalX=0 NormalY=0 NormalZ=1 AngleXU=0 Radius=1.5 StartAngle=4.71239 EndAngle=7.85398
    g3: ArcOfCircle CenterX=-1.5 CenterY=4.25 CenterZ=0 NormalX=0 NormalY=0 NormalZ=1 AngleXU=0 Radius=1.5 StartAngle=4.71239 EndAngle=7.85398
    g4: LineSegment StartX=-49.19 StartY=69.25 StartZ=0 EndX=-1.5 EndY=69.25 EndZ=0
    g5: LineSegment StartX=-49.19 StartY=66.25 StartZ=0 EndX=-1.5 EndY=66.25 EndZ=0
    g6: LineSegment StartX=-49.19 StartY=5.75 StartZ=0 EndX=-1.5 EndY=5.75 EndZ=0
    g7: LineSegment StartX=-49.19 StartY=2.75 StartZ=0 EndX=-1.5 EndY=2.75 EndZ=0
  constraints (19):
    c: Vertical(g0)
    c: Distance(g0) = 3
    c: Block(g0)
    c: Vertical(g1)
    c: Block(g2)
    c: Block(g3)
    c: Block(g1)
    c: Coincident(g4,g0)
    c: Coincident(g4,g2)
    c: Horizontal(g4)
    c: Coincident(g5,g0)
    c: Coincident(g5,g2)
    c: Horizontal(g5)
    c: Coincident(g6,g1)
    c: Coincident(g6,g3)
    c: Horizontal(g6)
    c: Coincident(g7,g1)
    c: Coincident(g7,g3)
    c: Horizontal(g7)
FEATURE [Part::Extrusion] Extrude069
  Base = -> Sketch078
  Dir = (1,0,0)
  DirMode = 2
  FaceMakerClass = Part::FaceMakerBullseye
  LengthFwd = 10
  LengthRev = 0
  Solid = true
  Symmetric = false
FEATURE [Part::Fillet] Fillet058  label="removeFromtMoreFrontCaseScrewRetainers003"
  Base = -> Extrude069
  Edges = 4 edges r=1.49: [Edge6,Edge11,Edge18,Edge23]
  Placement = pos=(-4,0,0) rot=(0,0,1;0rad)
FEATURE [Part::Cut] Cut066
  Base = -> Cut065
  Tool = -> Fillet058
FEATURE [Part::Cut] Cut067  label="screwPillars"
  Base = -> Cut066
  Tool = -> Fillet057
FEATURE [Part::MultiFuse] Fusion143  label="bottom021"
  Shapes = -> [Cut031,Cut063]
FEATURE [Part::Cylinder] Cylinder
  Angle = 360
  AttacherType = Attacher::AttachEngine3D
  Height = 10
  Placement = pos=(20.65,12,4.68) rot=(1,0,0;1.5708rad)
  Radius = 2
FEATURE [Part::Cylinder] Cylinder064
  Angle = 360
  AttacherType = Attacher::AttachEngine3D
  Height = 10
  Placement = pos=(20.65,12,67.38) rot=(1,0,0;1.5708rad)
  Radius = 2
FEATURE [Part::Cylinder] Cylinder065
  Angle = 360
  AttacherType = Attacher::AttachEngine3D
  Height = 10
  Placement = pos=(77.15,12,67.38) rot=(1,0,0;1.5708rad)
  Radius = 2
FEATURE [Part::Cylinder] Cylinder066
  Angle = 360
  AttacherType = Attacher::AttachEngine3D
  Height = 10
  Placement = pos=(77.15,12,4.68) rot=(1,0,0;1.5708rad)
  Radius = 2
FEATURE [Part::MultiFuse] Fusion144  label="removeFromThreadedInsertHousing"
  Shapes = -> [Cylinder065,Cylinder064,Cylinder,Cylinder066]
FEATURE [Part::Cut] Cut068  label="pcbStands001"
  Base = -> Cut064
  Tool = -> Fusion144
FEATURE [Part::MultiFuse] Fusion145
  Shapes = -> [Cut068,Fusion143]
FEATURE [Part::MultiFuse] Fusion146
  Shapes = -> [Fusion145]
FEATURE [Part::MultiFuse] Fusion147  label="bottom022"
  Shapes = -> [Cut067,Fusion146]
FEATURE [Part::MultiFuse] Fusion148  label="casePillars005"
  Shapes = -> [Cut047,Fusion092]
FEATURE [Part::MultiFuse] Fusion149  label="bottom023"
  Shapes = -> [Fusion124,Fusion113,Fusion147]
FEATURE [Part::MultiFuse] Fusion150  label="topBits"
  Shapes = -> [Cut025,Fusion148,Cut030,Fillet034]
FEATURE [Part::Feature] Face149 .. Face152  x4 (patterned run collapsed; names and placements below)
  shape: bbox 3.2 x 1.5 x 2e-07 mm, 1 faces, 0 solids (baked)
FEATURE [Part::Feature] Face153
  shape: bbox 3.6 x 3.2 x 2e-07 mm, 1 faces, 0 solids (baked)
FEATURE [Part::Feature] Face154
  shape: bbox 3.6 x 3.2 x 2e-07 mm, 1 faces, 0 solids (baked)
FEATURE [Sketcher::SketchObject] Sketch079  label="topSketch024"
  FullyConstrained = true
  sketch-geometry (6):
    g0: LineSegment StartX=19 StartY=38 StartZ=0 EndX=117 EndY=38 EndZ=0
    g1: ArcOfCircle CenterX=19 CenterY=19 CenterZ=0 NormalX=0 NormalY=0 NormalZ=1 AngleXU=0 Radius=19 StartAngle=1.5708 EndAngle=3.14159
    g2: LineSegment StartX=117 StartY=38 StartZ=0 EndX=117 EndY=19 EndZ=0
    g3: LineSegment StartX=98 StartY=1.0161e-12 StartZ=0 EndX=5.22862e-06 EndY=1.0161e-12 EndZ=0
    g4: LineSegment StartX=5.22862e-06 StartY=19 StartZ=0 EndX=5.22862e-06 EndY=1.0161e-12 EndZ=0
    g5: ArcOfCircle CenterX=98 CenterY=19 CenterZ=0 NormalX=0 NormalY=0 NormalZ=1 AngleXU=0 Radius=19 StartAngle=4.71239 EndAngle=6.28319
  constraints (16):
    c: Horizontal(g0)
    c: Distance(g0) = 98
    c: Coincident(g1,g0)
    c: Block(g1)
    c: Coincident(g2,g0)
    c: Vertical(g2)
    c: Distance(g2) = 19
    c: Horizontal(g3)
    c: Coincident(g4,g1)
    c: Vertical(g4)
    c: Coincident(g3,g4)
    c: Block(g3)
    c: Coincident(g5,g2)
    c: Coincident(g5,g3)
    c: Block(g0)
    c: Block(g5)
FEATURE [Sketcher::SketchObject] Sketch080  label="topSketch025"
  FullyConstrained = true
  sketch-geometry (6):
    g0: LineSegment StartX=19 StartY=38 StartZ=0 EndX=117 EndY=38 EndZ=0
    g1: ArcOfCircle CenterX=19 CenterY=19 CenterZ=0 NormalX=0 NormalY=0 NormalZ=1 AngleXU=0 Radius=19 StartAngle=1.5708 EndAngle=3.14159
    g2: LineSegment StartX=117 StartY=38 StartZ=0 EndX=117 EndY=19 EndZ=0
    g3: LineSegment StartX=98 StartY=1.0161e-12 StartZ=0 EndX=5.22862e-06 EndY=1.0161e-12 EndZ=0
    g4: LineSegment StartX=5.22862e-06 StartY=19 StartZ=0 EndX=5.22862e-06 EndY=1.0161e-12 EndZ=0
    g5: ArcOfCircle CenterX=98 CenterY=19 CenterZ=0 NormalX=0 NormalY=0 NormalZ=1 AngleXU=0 Radius=19 StartAngle=4.71239 EndAngle=6.28319
  constraints (16):
    c: Horizontal(g0)
    c: Distance(g0) = 98
    c: Coincident(g1,g0)
    c: Block(g1)
    c: Coincident(g2,g0)
    c: Vertical(g2)
    c: Distance(g2) = 19
    c: Horizontal(g3)
    c: Coincident(g4,g1)
    c: Vertical(g4)
    c: Coincident(g3,g4)
    c: Block(g3)
    c: Coincident(g5,g2)
    c: Coincident(g5,g3)
    c: Block(g0)
    c: Block(g5)
FEATURE [Part::Extrusion] Extrude070  label="sideA004"
  Base = -> Sketch080
  Dir = (0,0,1)
  DirMode = 2
  FaceMakerClass = Part::FaceMakerBullseye
  LengthFwd = 3
  LengthRev = 0
  Placement = pos=(0,0,-2.7) rot=(0,0,1;0rad)
  Solid = true
  Symmetric = false
FEATURE [Sketcher::SketchObject] Sketch081
  FullyConstrained = true
  Placement = pos=(117,19,0) rot=(0.57735,0.57735,0.57735;2.0944rad)
  sketch-geometry (8):
    g0: LineSegment StartX=-49.19 StartY=63.5 StartZ=0 EndX=-49.19 EndY=60.5 EndZ=0
    g1: LineSegment StartX=-49.19 StartY=11.5 StartZ=0 EndX=-49.19 EndY=8.5 EndZ=0
    g2: ArcOfCircle CenterX=-1.5 CenterY=62 CenterZ=0 NormalX=0 NormalY=0 NormalZ=1 AngleXU=0 Radius=1.5 StartAngle=4.71239 EndAngle=7.85398
    g3: ArcOfCircle CenterX=-1.5 CenterY=10 CenterZ=0 NormalX=0 NormalY=0 NormalZ=1 AngleXU=0 Radius=1.5 StartAngle=4.71239 EndAngle=7.85398
    g4: LineSegment StartX=-49.19 StartY=63.5 StartZ=0 EndX=-1.5 EndY=63.5 EndZ=0
    g5: LineSegment StartX=-49.19 StartY=60.5 StartZ=0 EndX=-1.5 EndY=60.5 EndZ=0
    g6: LineSegment StartX=-49.19 StartY=11.5 StartZ=0 EndX=-1.5 EndY=11.5 EndZ=0
    g7: LineSegment StartX=-49.19 StartY=8.5 StartZ=0 EndX=-1.5 EndY=8.5 EndZ=0
  constraints (19):
    c: Vertical(g0)
    c: Distance(g0) = 3
    c: Vertical(g1)
    c: Block(g1)
    c: Block(g2)
    c: Block(g3)
    c: Block(g0)
    c: Coincident(g4,g0)
    c: Coincident(g4,g2)
    c: Horizontal(g4)
    c: Coincident(g5,g0)
    c: Coincident(g5,g2)
    c: Horizontal(g5)
    c: Coincident(g6,g1)
    c: Coincident(g6,g3)
    c: Horizontal(g6)
    c: Coincident(g7,g1)
    c: Coincident(g7,g3)
    c: Horizontal(g7)
FEATURE [Part::Extrusion] Extrude071  label="sideB004"
  Base = -> Sketch079
  Dir = (0,0,1)
  DirMode = 2
  FaceMakerClass = Part::FaceMakerBullseye
  LengthFwd = 3
  LengthRev = 0
  Placement = pos=(0,0,71.7) rot=(0,0,1;0rad)
  Solid = true
  Symmetric = false
FEATURE [Part::MultiFuse] Fusion152  label="removeFromBottom004"
  Placement = pos=(2,0,0) rot=(0,0,1;0rad)
  Shapes = -> [Extrude070,Extrude071]
FEATURE [Part::Extrusion] Extrude072
  Base = -> Sketch081
  Dir = (1,0,0)
  DirMode = 2
  FaceMakerClass = Part::FaceMakerBullseye
  LengthFwd = 10
  LengthRev = 0
  Solid = true
  Symmetric = false
FEATURE [Part::Fillet] Fillet059  label="removeFromtMoreFrontCaseScrewRetainers004"
  Base = -> Extrude072
  Edges = 4 edges r=1.49: [Edge6,Edge11,Edge18,Edge23]
  Placement = pos=(-12,0,0) rot=(0,0,1;0rad)
FEATURE [Sketcher::SketchObject] Sketch082
  FullyConstrained = true
  Placement = pos=(117,19,0) rot=(0.57735,0.57735,0.57735;2.0944rad)
  sketch-geometry (8):
    g0: LineSegment StartX=-49.19 StartY=69.25 StartZ=0 EndX=-49.19 EndY=66.25 EndZ=0
    g1: LineSegment StartX=-49.19 StartY=5.75 StartZ=0 EndX=-49.19 EndY=2.75 EndZ=0
    g2: ArcOfCircle CenterX=-1.5 CenterY=67.75 CenterZ=0 NormalX=0 NormalY=0 NormalZ=1 AngleXU=0 Radius=1.5 StartAngle=4.71239 EndAngle=7.85398
    g3: ArcOfCircle CenterX=-1.5 CenterY=4.25 CenterZ=0 NormalX=0 NormalY=0 NormalZ=1 AngleXU=0 Radius=1.5 StartAngle=4.71239 EndAngle=7.85398
    g4: LineSegment StartX=-49.19 StartY=69.25 StartZ=0 EndX=-1.5 EndY=69.25 EndZ=0
    g5: LineSegment StartX=-49.19 StartY=66.25 StartZ=0 EndX=-1.5 EndY=66.25 EndZ=0
    g6: LineSegment StartX=-49.19 StartY=5.75 StartZ=0 EndX=-1.5 EndY=5.75 EndZ=0
    g7: LineSegment StartX=-49.19 StartY=2.75 StartZ=0 EndX=-1.5 EndY=2.75 EndZ=0
  constraints (19):
    c: Vertical(g0)
    c: Distance(g0) = 3
    c: Block(g0)
    c: Vertical(g1)
    c: Block(g2)
    c: Block(g3)
    c: Block(g1)
    c: Coincident(g4,g0)
    c: Coincident(g4,g2)
    c: Horizontal(g4)
    c: Coincident(g5,g0)
    c: Coincident(g5,g2)
    c: Horizontal(g5)
    c: Coincident(g6,g1)
    c: Coincident(g6,g3)
    c: Horizontal(g6)
    c: Coincident(g7,g1)
    c: Coincident(g7,g3)
    c: Horizontal(g7)
FEATURE [Part::Extrusion] Extrude073
  Base = -> Sketch082
  Dir = (1,0,0)
  DirMode = 2
  FaceMakerClass = Part::FaceMakerBullseye
  LengthFwd = 10
  LengthRev = 0
  Solid = true
  Symmetric = false
FEATURE [Part::Fillet] Fillet060  label="removeFromtMoreFrontCaseScrewRetainers005"
  Base = -> Extrude073
  Edges = 4 edges r=1.49: [Edge6,Edge11,Edge18,Edge23]
  Placement = pos=(-4,0,0) rot=(0,0,1;0rad)
FEATURE [Part::Revolution] Revolve163  label="backCaseScrewRetainer004"
  Angle = 360
  Axis = (0,1,0)
  Base = (0,0,0)
  FaceMakerClass = Part::FaceMakerBullseye
  Placement = pos=(12.5,3,62) rot=(0,0,1;0rad)
  Solid = false
  Source = -> Face149
  Symmetric = false
FEATURE [Part::Revolution] Revolve164  label="frontCaseScrewRetainer006"
  Angle = 360
  Axis = (0,1,0)
  Base = (0,0,0)
  FaceMakerClass = Part::FaceMakerBullseye
  Placement = pos=(89.5,3,68.5) rot=(0,0,1;0rad)
  Solid = false
  Source = -> Face151
  Symmetric = false
FEATURE [Part::Revolution] Revolve165  label="frontCaseScrewRetainer007"
  Angle = 360
  Axis = (0,1,0)
  Base = (0,0,0)
  FaceMakerClass = Part::FaceMakerBullseye
  Placement = pos=(89.5,3,3.5) rot=(0,0,1;0rad)
  Solid = false
  Source = -> Face152
  Symmetric = false
FEATURE [Part::Revolution] Revolve166  label="backCaseScrewRetainer005"
  Angle = 360
  Axis = (0,1,0)
  Base = (0,0,0)
  FaceMakerClass = Part::FaceMakerBullseye
  Placement = pos=(12.5,3,10) rot=(0,0,1;0rad)
  Solid = false
  Source = -> Face150
  Symmetric = false
FEATURE [Part::Revolution] Revolve167  label="moreFrontCaseScrewRetainer006"
  Angle = 360
  Axis = (0,1,0)
  Base = (0,0,0)
  FaceMakerClass = Part::FaceMakerBullseye
  Placement = pos=(109.5,4.5,68.5) rot=(0,0,1;0rad)
  Solid = false
  Source = -> Face153
  Symmetric = false
FEATURE [Part::Revolution] Revolve168  label="moreFrontCaseScrewRetainer007"
  Angle = 360
  Axis = (0,1,0)
  Base = (0,0,0)
  FaceMakerClass = Part::FaceMakerBullseye
  Placement = pos=(109.5,4.5,3.5) rot=(0,0,1;0rad)
  Solid = false
  Source = -> Face154
  Symmetric = false
FEATURE [Part::MultiFuse] Fusion151  label="screwRetainers003"
  Shapes = -> [Revolve168,Revolve167,Revolve166,Revolve165,Revolve164,Revolve163]
FEATURE [Part::Cut] Cut069  label="screwRetainers004"
  Base = -> Fusion151
  Tool = -> Fusion152
FEATURE [Part::Cut] Cut070
  Base = -> Cut069
  Tool = -> Fillet060
FEATURE [Part::Cut] Cut071  label="screwPillars001"
  Base = -> Cut070
  Tool = -> Fillet059
FEATURE [Part::MultiFuse] Fusion153  label="bottom024"
  Shapes = -> [Fusion149,Cut071]
FEATURE [Part::Cylinder] Cylinder067
  Angle = 360
  AttacherType = Attacher::AttachEngine3D
  Height = 10
  Placement = pos=(20.65,12,4.68) rot=(1,0,0;1.5708rad)
  Radius = 2
FEATURE [Part::Cylinder] Cylinder068
  Angle = 360
  AttacherType = Attacher::AttachEngine3D
  Height = 10
  Placement = pos=(20.65,12,67.38) rot=(1,0,0;1.5708rad)
  Radius = 2
FEATURE [Part::Cylinder] Cylinder069
  Angle = 360
  AttacherType = Attacher::AttachEngine3D
  Height = 10
  Placement = pos=(77.15,12,67.38) rot=(1,0,0;1.5708rad)
  Radius = 2
FEATURE [Part::Cylinder] Cylinder070
  Angle = 360
  AttacherType = Attacher::AttachEngine3D
  Height = 10
  Placement = pos=(77.15,12,4.68) rot=(1,0,0;1.5708rad)
  Radius = 2
FEATURE [Part::MultiFuse] Fusion154  label="removeFromThreadedInsertHousing001"
  Shapes = -> [Cylinder069,Cylinder068,Cylinder067,Cylinder070]
FEATURE [Part::Cut] Cut072  label="bottom025"
  Base = -> Fusion153
  Tool = -> Fusion154
FEATURE [Image::ImagePlane] ImagePlane
  XSize = 339
  YSize = 72
FEATURE [Sketcher::SketchObject] Sketch083
  FullyConstrained = true
  MapMode = 5
  Support = -> [XY_Plane]
  sketch-geometry (6):
    g0: LineSegment StartX=-151.619 StartY=28.8932 StartZ=0 EndX=-140.819 EndY=28.8932 EndZ=0
    g1: LineSegment StartX=-145.128 StartY=24.0313 StartZ=0 EndX=-151.619 EndY=24.0313 EndZ=0
    g2: LineSegment StartX=-151.619 StartY=24.0313 StartZ=0 EndX=-151.619 EndY=28.8932 EndZ=0
    g3: LineSegment StartX=-140.819 StartY=17.7713 StartZ=0 EndX=-151.619 EndY=17.7713 EndZ=0
    g4: LineSegment StartX=-151.619 StartY=17.7713 StartZ=0 EndX=-151.619 EndY=22.6313 EndZ=0
    g5: LineSegment StartX=-151.619 StartY=22.6313 StartZ=0 EndX=-145.128 EndY=22.6313 EndZ=0
  constraints (16):
    c: Coincident(g1,g2)
    c: Coincident(g2,g0)
    c: Horizontal(g0)
    c: Horizontal(g1)
    c: Vertical(g2)
    c: Coincident(g3,g4)
    c: Coincident(g4,g5)
    c: Horizontal(g5)
    c: Horizontal(g3)
    c: Vertical(g4)
    c: Block(g2)
    c: Block(g1)
    c: Distance(g4) = 4.86
    c: Block(g5)
    c: Distance(g0) = 10.8
    c: Distance(g3) = 10.8
FEATURE [PartDesign::Body] Body
  Group = -> [Sketch083]
  Origin = -> Origin
FEATURE [Sketcher::SketchObject] Sketch084
  FullyConstrained = true
  MapMode = 5
  Support = -> [XY_Plane001]
FEATURE [PartDesign::Body] Body001
  Group = -> [Sketch084]
  Origin = -> Origin001
